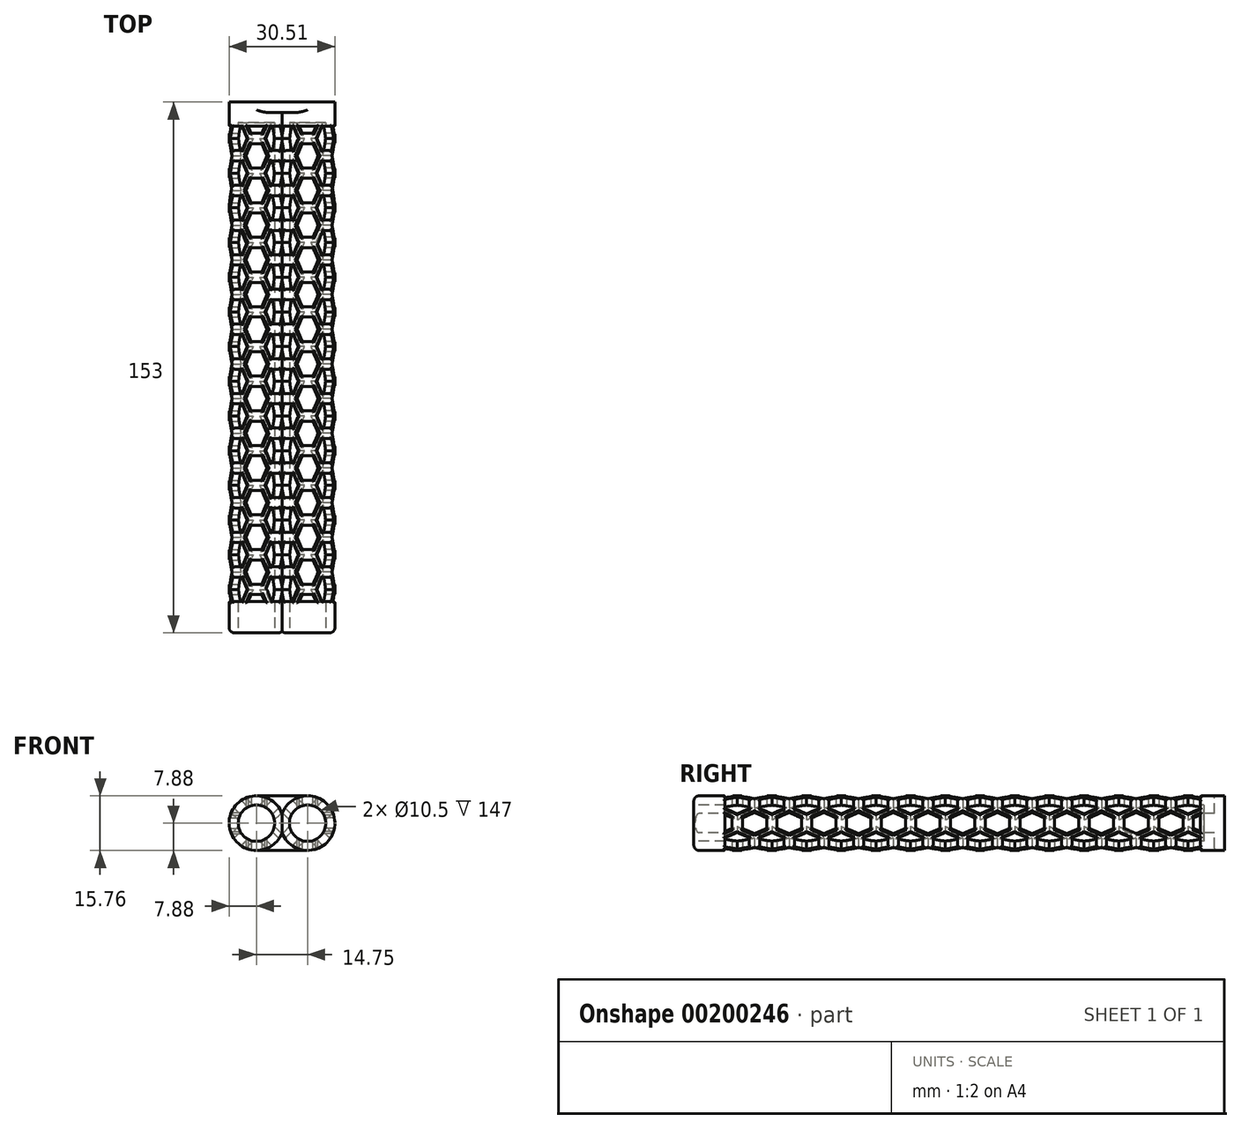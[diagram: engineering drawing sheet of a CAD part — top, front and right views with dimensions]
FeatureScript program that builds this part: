
annotation { "Feature Type Name" : "Feature", "Feature Type Description" : "" }
export const myFeature = defineFeature(function(context is Context, id is Id, definition is map)
    precondition{}
    {
        {
            var Q0;
            Q0=qCreatedBy(makeId("Front.planeOp"),FACE);
            var sketch = newSketch(context, id + "F0", { "sketchPlane" : qUnion([Q0])});
            skCircle(sketch, "E0", {"center": v(0, 0) * mm, "radius": 7.88 * mm});
            skSolve(sketch);
        }
        {
            var Q0;
            Q0=makeQuery(id+"F0.imprint","IMPRINT",FACE,{"disambiguationData":[TD([[makeQuery(id+"F0.imprint","IMPRINT",EDGE,{"derivedFrom":sQuery(id+"F0.wireOp",EDGE,"E0")}),1.0]])]});
            extrude(context, id + "F1", {"entities" : qUnion([Q0]), "oppositeDirection" : true, "depth" : 150 * mm});
        }
        {
            var Q0;
            Q0=makeQuery(id+"F1.opExtrude","CAP_FACE",FACE,{"disambiguationData":[OSD([sQuery(id+"F0.wireOp",EDGE,"E0")])],"isStart":true});
            var sketch = newSketch(context, id + "F2", { "sketchPlane" : qUnion([Q0])});
            skCircle(sketch, "E1", {"center": v(0, 0) * mm, "radius": 5.25 * mm});
            skSolve(sketch);
        }
        {
            var Q0;
            Q0=qSketchRegion(id+"F2",true);
            extrude(context, id + "F3", {"entities" : qUnion([Q0]), "operationType" : NewBodyOperationType.REMOVE, "oppositeDirection" : true, "depth" : 147 * mm});
        }
        {
            var Q0;
            Q0=qCreatedBy(makeId("Top.planeOp"),FACE);
            var sketch = newSketch(context, id + "F4", { "sketchPlane" : qUnion([Q0])});
            skLineSegment(sketch, "E2", {"start": v(0, 0) * mm, "end": v(0, 9) * mm, "construction": true});
            skLineSegment(sketch, "E3", {"start": v(0, 9) * mm, "end": v(-3, 9) * mm, "construction": true});
            skLineSegment(sketch, "E4", {"start": v(3, 9) * mm, "end": v(1.5, 9) * mm, "construction": true});
            skLineSegment(sketch, "E5", {"start": v(1.5, 9) * mm, "end": v(-1.5, 9) * mm, "construction": true});
            skLineSegment(sketch, "E6", {"start": v(-1.5, 9) * mm, "end": v(-3, 9) * mm, "construction": true});
            skLineSegment(sketch, "E7", {"start": v(-3, 9) * mm, "end": v(-3, 12.5) * mm, "construction": true});
            skLineSegment(sketch, "E8", {"start": v(-3, 12.5) * mm, "end": v(-3, 16) * mm, "construction": true});
            skLineSegment(sketch, "E9", {"start": v(-3, 16) * mm, "end": v(-1.5, 16) * mm, "construction": true});
            skLineSegment(sketch, "E10", {"start": v(-1.5, 16) * mm, "end": v(1.5, 16) * mm, "construction": true});
            skLineSegment(sketch, "E11", {"start": v(1.5, 16) * mm, "end": v(3, 16) * mm, "construction": true});
            skLineSegment(sketch, "E12", {"start": v(3, 16) * mm, "end": v(3, 12.5) * mm, "construction": true});
            skLineSegment(sketch, "E13", {"start": v(3, 12.5) * mm, "end": v(3, 9) * mm, "construction": true});
            skLineSegment(sketch, "E14", {"start": v(1.5, 16) * mm, "end": v(3, 12.5) * mm});
            skLineSegment(sketch, "E15", {"start": v(3, 12.5) * mm, "end": v(1.5, 9) * mm});
            skLineSegment(sketch, "E16", {"start": v(1.5, 9) * mm, "end": v(-1.5, 9) * mm});
            skLineSegment(sketch, "E17", {"start": v(-1.5, 9) * mm, "end": v(-3, 12.5) * mm});
            skLineSegment(sketch, "E18", {"start": v(-3, 12.5) * mm, "end": v(-1.5, 16) * mm});
            skLineSegment(sketch, "E19", {"start": v(-1.5, 16) * mm, "end": v(1.5, 16) * mm});
            skLineSegment(sketch, "E20", {"start": v(0, 9) * mm, "end": v(0, 19) * mm, "construction": true});
            skLineSegment(sketch, "E21", {"start": v(0, 19) * mm, "end": v(-3, 19) * mm, "construction": true});
            skLineSegment(sketch, "E22", {"start": v(3, 19) * mm, "end": v(1.5, 19) * mm, "construction": true});
            skLineSegment(sketch, "E23", {"start": v(1.5, 19) * mm, "end": v(-1.5, 19) * mm, "construction": true});
            skLineSegment(sketch, "E24", {"start": v(-1.5, 19) * mm, "end": v(-3, 19) * mm, "construction": true});
            skLineSegment(sketch, "E25", {"start": v(-3, 19) * mm, "end": v(-3, 22.5) * mm, "construction": true});
            skLineSegment(sketch, "E26", {"start": v(-3, 22.5) * mm, "end": v(-3, 26) * mm, "construction": true});
            skLineSegment(sketch, "E27", {"start": v(-3, 26) * mm, "end": v(-1.5, 26) * mm, "construction": true});
            skLineSegment(sketch, "E28", {"start": v(-1.5, 26) * mm, "end": v(1.5, 26) * mm, "construction": true});
            skLineSegment(sketch, "E29", {"start": v(1.5, 26) * mm, "end": v(3, 26) * mm, "construction": true});
            skLineSegment(sketch, "E30", {"start": v(3, 26) * mm, "end": v(3, 22.5) * mm, "construction": true});
            skLineSegment(sketch, "E31", {"start": v(3, 22.5) * mm, "end": v(3, 19) * mm, "construction": true});
            skLineSegment(sketch, "E32", {"start": v(1.5, 26) * mm, "end": v(3, 22.5) * mm});
            skLineSegment(sketch, "E33", {"start": v(3, 22.5) * mm, "end": v(1.5, 19) * mm});
            skLineSegment(sketch, "E34", {"start": v(1.5, 19) * mm, "end": v(-1.5, 19) * mm});
            skLineSegment(sketch, "E35", {"start": v(-1.5, 19) * mm, "end": v(-3, 22.5) * mm});
            skLineSegment(sketch, "E36", {"start": v(-3, 22.5) * mm, "end": v(-1.5, 26) * mm});
            skLineSegment(sketch, "E37", {"start": v(-1.5, 26) * mm, "end": v(1.5, 26) * mm});
            skLineSegment(sketch, "E38", {"start": v(0, 19) * mm, "end": v(0, 29) * mm, "construction": true});
            skLineSegment(sketch, "E39", {"start": v(0, 29) * mm, "end": v(-3, 29) * mm, "construction": true});
            skLineSegment(sketch, "E40", {"start": v(3, 29) * mm, "end": v(1.5, 29) * mm, "construction": true});
            skLineSegment(sketch, "E41", {"start": v(1.5, 29) * mm, "end": v(-1.5, 29) * mm, "construction": true});
            skLineSegment(sketch, "E42", {"start": v(-1.5, 29) * mm, "end": v(-3, 29) * mm, "construction": true});
            skLineSegment(sketch, "E43", {"start": v(-3, 29) * mm, "end": v(-3, 32.5) * mm, "construction": true});
            skLineSegment(sketch, "E44", {"start": v(-3, 32.5) * mm, "end": v(-3, 36) * mm, "construction": true});
            skLineSegment(sketch, "E45", {"start": v(-3, 36) * mm, "end": v(-1.5, 36) * mm, "construction": true});
            skLineSegment(sketch, "E46", {"start": v(-1.5, 36) * mm, "end": v(1.5, 36) * mm, "construction": true});
            skLineSegment(sketch, "E47", {"start": v(1.5, 36) * mm, "end": v(3, 36) * mm, "construction": true});
            skLineSegment(sketch, "E48", {"start": v(3, 36) * mm, "end": v(3, 32.5) * mm, "construction": true});
            skLineSegment(sketch, "E49", {"start": v(3, 32.5) * mm, "end": v(3, 29) * mm, "construction": true});
            skLineSegment(sketch, "E50", {"start": v(1.5, 36) * mm, "end": v(3, 32.5) * mm});
            skLineSegment(sketch, "E51", {"start": v(3, 32.5) * mm, "end": v(1.5, 29) * mm});
            skLineSegment(sketch, "E52", {"start": v(1.5, 29) * mm, "end": v(-1.5, 29) * mm});
            skLineSegment(sketch, "E53", {"start": v(-1.5, 29) * mm, "end": v(-3, 32.5) * mm});
            skLineSegment(sketch, "E54", {"start": v(-3, 32.5) * mm, "end": v(-1.5, 36) * mm});
            skLineSegment(sketch, "E55", {"start": v(-1.5, 36) * mm, "end": v(1.5, 36) * mm});
            skLineSegment(sketch, "E56", {"start": v(0, 29) * mm, "end": v(0, 39) * mm, "construction": true});
            skLineSegment(sketch, "E57", {"start": v(0, 39) * mm, "end": v(-3, 39) * mm, "construction": true});
            skLineSegment(sketch, "E58", {"start": v(3, 39) * mm, "end": v(1.5, 39) * mm, "construction": true});
            skLineSegment(sketch, "E59", {"start": v(1.5, 39) * mm, "end": v(-1.5, 39) * mm, "construction": true});
            skLineSegment(sketch, "E60", {"start": v(-1.5, 39) * mm, "end": v(-3, 39) * mm, "construction": true});
            skLineSegment(sketch, "E61", {"start": v(-3, 39) * mm, "end": v(-3, 42.5) * mm, "construction": true});
            skLineSegment(sketch, "E62", {"start": v(-3, 42.5) * mm, "end": v(-3, 46) * mm, "construction": true});
            skLineSegment(sketch, "E63", {"start": v(-3, 46) * mm, "end": v(-1.5, 46) * mm, "construction": true});
            skLineSegment(sketch, "E64", {"start": v(-1.5, 46) * mm, "end": v(1.5, 46) * mm, "construction": true});
            skLineSegment(sketch, "E65", {"start": v(1.5, 46) * mm, "end": v(3, 46) * mm, "construction": true});
            skLineSegment(sketch, "E66", {"start": v(3, 46) * mm, "end": v(3, 42.5) * mm, "construction": true});
            skLineSegment(sketch, "E67", {"start": v(3, 42.5) * mm, "end": v(3, 39) * mm, "construction": true});
            skLineSegment(sketch, "E68", {"start": v(1.5, 46) * mm, "end": v(3, 42.5) * mm});
            skLineSegment(sketch, "E69", {"start": v(3, 42.5) * mm, "end": v(1.5, 39) * mm});
            skLineSegment(sketch, "E70", {"start": v(1.5, 39) * mm, "end": v(-1.5, 39) * mm});
            skLineSegment(sketch, "E71", {"start": v(-1.5, 39) * mm, "end": v(-3, 42.5) * mm});
            skLineSegment(sketch, "E72", {"start": v(-3, 42.5) * mm, "end": v(-1.5, 46) * mm});
            skLineSegment(sketch, "E73", {"start": v(-1.5, 46) * mm, "end": v(1.5, 46) * mm});
            skLineSegment(sketch, "E74", {"start": v(0, 39) * mm, "end": v(0, 49) * mm, "construction": true});
            skLineSegment(sketch, "E75", {"start": v(0, 49) * mm, "end": v(-3, 49) * mm, "construction": true});
            skLineSegment(sketch, "E76", {"start": v(3, 49) * mm, "end": v(1.5, 49) * mm, "construction": true});
            skLineSegment(sketch, "E77", {"start": v(1.5, 49) * mm, "end": v(-1.5, 49) * mm, "construction": true});
            skLineSegment(sketch, "E78", {"start": v(-1.5, 49) * mm, "end": v(-3, 49) * mm, "construction": true});
            skLineSegment(sketch, "E79", {"start": v(-3, 49) * mm, "end": v(-3, 52.5) * mm, "construction": true});
            skLineSegment(sketch, "E80", {"start": v(-3, 52.5) * mm, "end": v(-3, 56) * mm, "construction": true});
            skLineSegment(sketch, "E81", {"start": v(-3, 56) * mm, "end": v(-1.5, 56) * mm, "construction": true});
            skLineSegment(sketch, "E82", {"start": v(-1.5, 56) * mm, "end": v(1.5, 56) * mm, "construction": true});
            skLineSegment(sketch, "E83", {"start": v(1.5, 56) * mm, "end": v(3, 56) * mm, "construction": true});
            skLineSegment(sketch, "E84", {"start": v(3, 56) * mm, "end": v(3, 52.5) * mm, "construction": true});
            skLineSegment(sketch, "E85", {"start": v(3, 52.5) * mm, "end": v(3, 49) * mm, "construction": true});
            skLineSegment(sketch, "E86", {"start": v(1.5, 56) * mm, "end": v(3, 52.5) * mm});
            skLineSegment(sketch, "E87", {"start": v(3, 52.5) * mm, "end": v(1.5, 49) * mm});
            skLineSegment(sketch, "E88", {"start": v(1.5, 49) * mm, "end": v(-1.5, 49) * mm});
            skLineSegment(sketch, "E89", {"start": v(-1.5, 49) * mm, "end": v(-3, 52.5) * mm});
            skLineSegment(sketch, "E90", {"start": v(-3, 52.5) * mm, "end": v(-1.5, 56) * mm});
            skLineSegment(sketch, "E91", {"start": v(-1.5, 56) * mm, "end": v(1.5, 56) * mm});
            skLineSegment(sketch, "E92", {"start": v(0, 49) * mm, "end": v(0, 59) * mm, "construction": true});
            skLineSegment(sketch, "E93", {"start": v(0, 59) * mm, "end": v(-3, 59) * mm, "construction": true});
            skLineSegment(sketch, "E94", {"start": v(3, 59) * mm, "end": v(1.5, 59) * mm, "construction": true});
            skLineSegment(sketch, "E95", {"start": v(1.5, 59) * mm, "end": v(-1.5, 59) * mm, "construction": true});
            skLineSegment(sketch, "E96", {"start": v(-1.5, 59) * mm, "end": v(-3, 59) * mm, "construction": true});
            skLineSegment(sketch, "E97", {"start": v(-3, 59) * mm, "end": v(-3, 62.5) * mm, "construction": true});
            skLineSegment(sketch, "E98", {"start": v(-3, 62.5) * mm, "end": v(-3, 66) * mm, "construction": true});
            skLineSegment(sketch, "E99", {"start": v(-3, 66) * mm, "end": v(-1.5, 66) * mm, "construction": true});
            skLineSegment(sketch, "E100", {"start": v(-1.5, 66) * mm, "end": v(1.5, 66) * mm, "construction": true});
            skLineSegment(sketch, "E101", {"start": v(1.5, 66) * mm, "end": v(3, 66) * mm, "construction": true});
            skLineSegment(sketch, "E102", {"start": v(3, 66) * mm, "end": v(3, 62.5) * mm, "construction": true});
            skLineSegment(sketch, "E103", {"start": v(3, 62.5) * mm, "end": v(3, 59) * mm, "construction": true});
            skLineSegment(sketch, "E104", {"start": v(1.5, 66) * mm, "end": v(3, 62.5) * mm});
            skLineSegment(sketch, "E105", {"start": v(3, 62.5) * mm, "end": v(1.5, 59) * mm});
            skLineSegment(sketch, "E106", {"start": v(1.5, 59) * mm, "end": v(-1.5, 59) * mm});
            skLineSegment(sketch, "E107", {"start": v(-1.5, 59) * mm, "end": v(-3, 62.5) * mm});
            skLineSegment(sketch, "E108", {"start": v(-3, 62.5) * mm, "end": v(-1.5, 66) * mm});
            skLineSegment(sketch, "E109", {"start": v(-1.5, 66) * mm, "end": v(1.5, 66) * mm});
            skLineSegment(sketch, "E110", {"start": v(0, 59) * mm, "end": v(0, 69) * mm, "construction": true});
            skLineSegment(sketch, "E111", {"start": v(0, 69) * mm, "end": v(-3, 69) * mm, "construction": true});
            skLineSegment(sketch, "E112", {"start": v(3, 69) * mm, "end": v(1.5, 69) * mm, "construction": true});
            skLineSegment(sketch, "E113", {"start": v(1.5, 69) * mm, "end": v(-1.5, 69) * mm, "construction": true});
            skLineSegment(sketch, "E114", {"start": v(-1.5, 69) * mm, "end": v(-3, 69) * mm, "construction": true});
            skLineSegment(sketch, "E115", {"start": v(-3, 69) * mm, "end": v(-3, 72.5) * mm, "construction": true});
            skLineSegment(sketch, "E116", {"start": v(-3, 72.5) * mm, "end": v(-3, 76) * mm, "construction": true});
            skLineSegment(sketch, "E117", {"start": v(-3, 76) * mm, "end": v(-1.5, 76) * mm, "construction": true});
            skLineSegment(sketch, "E118", {"start": v(-1.5, 76) * mm, "end": v(1.5, 76) * mm, "construction": true});
            skLineSegment(sketch, "E119", {"start": v(1.5, 76) * mm, "end": v(3, 76) * mm, "construction": true});
            skLineSegment(sketch, "E120", {"start": v(3, 76) * mm, "end": v(3, 72.5) * mm, "construction": true});
            skLineSegment(sketch, "E121", {"start": v(3, 72.5) * mm, "end": v(3, 69) * mm, "construction": true});
            skLineSegment(sketch, "E122", {"start": v(1.5, 76) * mm, "end": v(3, 72.5) * mm});
            skLineSegment(sketch, "E123", {"start": v(3, 72.5) * mm, "end": v(1.5, 69) * mm});
            skLineSegment(sketch, "E124", {"start": v(1.5, 69) * mm, "end": v(-1.5, 69) * mm});
            skLineSegment(sketch, "E125", {"start": v(-1.5, 69) * mm, "end": v(-3, 72.5) * mm});
            skLineSegment(sketch, "E126", {"start": v(-3, 72.5) * mm, "end": v(-1.5, 76) * mm});
            skLineSegment(sketch, "E127", {"start": v(-1.5, 76) * mm, "end": v(1.5, 76) * mm});
            skLineSegment(sketch, "E128", {"start": v(0, 69) * mm, "end": v(0, 79) * mm, "construction": true});
            skLineSegment(sketch, "E129", {"start": v(0, 79) * mm, "end": v(-3, 79) * mm, "construction": true});
            skLineSegment(sketch, "E130", {"start": v(3, 79) * mm, "end": v(1.5, 79) * mm, "construction": true});
            skLineSegment(sketch, "E131", {"start": v(1.5, 79) * mm, "end": v(-1.5, 79) * mm, "construction": true});
            skLineSegment(sketch, "E132", {"start": v(-1.5, 79) * mm, "end": v(-3, 79) * mm, "construction": true});
            skLineSegment(sketch, "E133", {"start": v(-3, 79) * mm, "end": v(-3, 82.5) * mm, "construction": true});
            skLineSegment(sketch, "E134", {"start": v(-3, 82.5) * mm, "end": v(-3, 86) * mm, "construction": true});
            skLineSegment(sketch, "E135", {"start": v(-3, 86) * mm, "end": v(-1.5, 86) * mm, "construction": true});
            skLineSegment(sketch, "E136", {"start": v(-1.5, 86) * mm, "end": v(1.5, 86) * mm, "construction": true});
            skLineSegment(sketch, "E137", {"start": v(1.5, 86) * mm, "end": v(3, 86) * mm, "construction": true});
            skLineSegment(sketch, "E138", {"start": v(3, 86) * mm, "end": v(3, 82.5) * mm, "construction": true});
            skLineSegment(sketch, "E139", {"start": v(3, 82.5) * mm, "end": v(3, 79) * mm, "construction": true});
            skLineSegment(sketch, "E140", {"start": v(1.5, 86) * mm, "end": v(3, 82.5) * mm});
            skLineSegment(sketch, "E141", {"start": v(3, 82.5) * mm, "end": v(1.5, 79) * mm});
            skLineSegment(sketch, "E142", {"start": v(1.5, 79) * mm, "end": v(-1.5, 79) * mm});
            skLineSegment(sketch, "E143", {"start": v(-1.5, 79) * mm, "end": v(-3, 82.5) * mm});
            skLineSegment(sketch, "E144", {"start": v(-3, 82.5) * mm, "end": v(-1.5, 86) * mm});
            skLineSegment(sketch, "E145", {"start": v(-1.5, 86) * mm, "end": v(1.5, 86) * mm});
            skLineSegment(sketch, "E146", {"start": v(0, 79) * mm, "end": v(0, 89) * mm, "construction": true});
            skLineSegment(sketch, "E147", {"start": v(0, 89) * mm, "end": v(-3, 89) * mm, "construction": true});
            skLineSegment(sketch, "E148", {"start": v(3, 89) * mm, "end": v(1.5, 89) * mm, "construction": true});
            skLineSegment(sketch, "E149", {"start": v(1.5, 89) * mm, "end": v(-1.5, 89) * mm, "construction": true});
            skLineSegment(sketch, "E150", {"start": v(-1.5, 89) * mm, "end": v(-3, 89) * mm, "construction": true});
            skLineSegment(sketch, "E151", {"start": v(-3, 89) * mm, "end": v(-3, 92.5) * mm, "construction": true});
            skLineSegment(sketch, "E152", {"start": v(-3, 92.5) * mm, "end": v(-3, 96) * mm, "construction": true});
            skLineSegment(sketch, "E153", {"start": v(-3, 96) * mm, "end": v(-1.5, 96) * mm, "construction": true});
            skLineSegment(sketch, "E154", {"start": v(-1.5, 96) * mm, "end": v(1.5, 96) * mm, "construction": true});
            skLineSegment(sketch, "E155", {"start": v(1.5, 96) * mm, "end": v(3, 96) * mm, "construction": true});
            skLineSegment(sketch, "E156", {"start": v(3, 96) * mm, "end": v(3, 92.5) * mm, "construction": true});
            skLineSegment(sketch, "E157", {"start": v(3, 92.5) * mm, "end": v(3, 89) * mm, "construction": true});
            skLineSegment(sketch, "E158", {"start": v(1.5, 96) * mm, "end": v(3, 92.5) * mm});
            skLineSegment(sketch, "E159", {"start": v(3, 92.5) * mm, "end": v(1.5, 89) * mm});
            skLineSegment(sketch, "E160", {"start": v(1.5, 89) * mm, "end": v(-1.5, 89) * mm});
            skLineSegment(sketch, "E161", {"start": v(-1.5, 89) * mm, "end": v(-3, 92.5) * mm});
            skLineSegment(sketch, "E162", {"start": v(-3, 92.5) * mm, "end": v(-1.5, 96) * mm});
            skLineSegment(sketch, "E163", {"start": v(-1.5, 96) * mm, "end": v(1.5, 96) * mm});
            skLineSegment(sketch, "E164", {"start": v(0, 89) * mm, "end": v(0, 99) * mm, "construction": true});
            skLineSegment(sketch, "E165", {"start": v(0, 99) * mm, "end": v(-3, 99) * mm, "construction": true});
            skLineSegment(sketch, "E166", {"start": v(3, 99) * mm, "end": v(1.5, 99) * mm, "construction": true});
            skLineSegment(sketch, "E167", {"start": v(1.5, 99) * mm, "end": v(-1.5, 99) * mm, "construction": true});
            skLineSegment(sketch, "E168", {"start": v(-1.5, 99) * mm, "end": v(-3, 99) * mm, "construction": true});
            skLineSegment(sketch, "E169", {"start": v(-3, 99) * mm, "end": v(-3, 102.5) * mm, "construction": true});
            skLineSegment(sketch, "E170", {"start": v(-3, 102.5) * mm, "end": v(-3, 106) * mm, "construction": true});
            skLineSegment(sketch, "E171", {"start": v(-3, 106) * mm, "end": v(-1.5, 106) * mm, "construction": true});
            skLineSegment(sketch, "E172", {"start": v(-1.5, 106) * mm, "end": v(1.5, 106) * mm, "construction": true});
            skLineSegment(sketch, "E173", {"start": v(1.5, 106) * mm, "end": v(3, 106) * mm, "construction": true});
            skLineSegment(sketch, "E174", {"start": v(3, 106) * mm, "end": v(3, 102.5) * mm, "construction": true});
            skLineSegment(sketch, "E175", {"start": v(3, 102.5) * mm, "end": v(3, 99) * mm, "construction": true});
            skLineSegment(sketch, "E176", {"start": v(1.5, 106) * mm, "end": v(3, 102.5) * mm});
            skLineSegment(sketch, "E177", {"start": v(3, 102.5) * mm, "end": v(1.5, 99) * mm});
            skLineSegment(sketch, "E178", {"start": v(1.5, 99) * mm, "end": v(-1.5, 99) * mm});
            skLineSegment(sketch, "E179", {"start": v(-1.5, 99) * mm, "end": v(-3, 102.5) * mm});
            skLineSegment(sketch, "E180", {"start": v(-3, 102.5) * mm, "end": v(-1.5, 106) * mm});
            skLineSegment(sketch, "E181", {"start": v(-1.5, 106) * mm, "end": v(1.5, 106) * mm});
            skLineSegment(sketch, "E182", {"start": v(0, 99) * mm, "end": v(0, 109) * mm, "construction": true});
            skLineSegment(sketch, "E183", {"start": v(0, 109) * mm, "end": v(-3, 109) * mm, "construction": true});
            skLineSegment(sketch, "E184", {"start": v(3, 109) * mm, "end": v(1.5, 109) * mm, "construction": true});
            skLineSegment(sketch, "E185", {"start": v(1.5, 109) * mm, "end": v(-1.5, 109) * mm, "construction": true});
            skLineSegment(sketch, "E186", {"start": v(-1.5, 109) * mm, "end": v(-3, 109) * mm, "construction": true});
            skLineSegment(sketch, "E187", {"start": v(-3, 109) * mm, "end": v(-3, 112.5) * mm, "construction": true});
            skLineSegment(sketch, "E188", {"start": v(-3, 112.5) * mm, "end": v(-3, 116) * mm, "construction": true});
            skLineSegment(sketch, "E189", {"start": v(-3, 116) * mm, "end": v(-1.5, 116) * mm, "construction": true});
            skLineSegment(sketch, "E190", {"start": v(-1.5, 116) * mm, "end": v(1.5, 116) * mm, "construction": true});
            skLineSegment(sketch, "E191", {"start": v(1.5, 116) * mm, "end": v(3, 116) * mm, "construction": true});
            skLineSegment(sketch, "E192", {"start": v(3, 116) * mm, "end": v(3, 112.5) * mm, "construction": true});
            skLineSegment(sketch, "E193", {"start": v(3, 112.5) * mm, "end": v(3, 109) * mm, "construction": true});
            skLineSegment(sketch, "E194", {"start": v(1.5, 116) * mm, "end": v(3, 112.5) * mm});
            skLineSegment(sketch, "E195", {"start": v(3, 112.5) * mm, "end": v(1.5, 109) * mm});
            skLineSegment(sketch, "E196", {"start": v(1.5, 109) * mm, "end": v(-1.5, 109) * mm});
            skLineSegment(sketch, "E197", {"start": v(-1.5, 109) * mm, "end": v(-3, 112.5) * mm});
            skLineSegment(sketch, "E198", {"start": v(-3, 112.5) * mm, "end": v(-1.5, 116) * mm});
            skLineSegment(sketch, "E199", {"start": v(-1.5, 116) * mm, "end": v(1.5, 116) * mm});
            skLineSegment(sketch, "E200", {"start": v(0, 109) * mm, "end": v(0, 119) * mm, "construction": true});
            skLineSegment(sketch, "E201", {"start": v(0, 119) * mm, "end": v(-3, 119) * mm, "construction": true});
            skLineSegment(sketch, "E202", {"start": v(3, 119) * mm, "end": v(1.5, 119) * mm, "construction": true});
            skLineSegment(sketch, "E203", {"start": v(1.5, 119) * mm, "end": v(-1.5, 119) * mm, "construction": true});
            skLineSegment(sketch, "E204", {"start": v(-1.5, 119) * mm, "end": v(-3, 119) * mm, "construction": true});
            skLineSegment(sketch, "E205", {"start": v(-3, 119) * mm, "end": v(-3, 122.5) * mm, "construction": true});
            skLineSegment(sketch, "E206", {"start": v(-3, 122.5) * mm, "end": v(-3, 126) * mm, "construction": true});
            skLineSegment(sketch, "E207", {"start": v(-3, 126) * mm, "end": v(-1.5, 126) * mm, "construction": true});
            skLineSegment(sketch, "E208", {"start": v(-1.5, 126) * mm, "end": v(1.5, 126) * mm, "construction": true});
            skLineSegment(sketch, "E209", {"start": v(1.5, 126) * mm, "end": v(3, 126) * mm, "construction": true});
            skLineSegment(sketch, "E210", {"start": v(3, 126) * mm, "end": v(3, 122.5) * mm, "construction": true});
            skLineSegment(sketch, "E211", {"start": v(3, 122.5) * mm, "end": v(3, 119) * mm, "construction": true});
            skLineSegment(sketch, "E212", {"start": v(1.5, 126) * mm, "end": v(3, 122.5) * mm});
            skLineSegment(sketch, "E213", {"start": v(3, 122.5) * mm, "end": v(1.5, 119) * mm});
            skLineSegment(sketch, "E214", {"start": v(1.5, 119) * mm, "end": v(-1.5, 119) * mm});
            skLineSegment(sketch, "E215", {"start": v(-1.5, 119) * mm, "end": v(-3, 122.5) * mm});
            skLineSegment(sketch, "E216", {"start": v(-3, 122.5) * mm, "end": v(-1.5, 126) * mm});
            skLineSegment(sketch, "E217", {"start": v(-1.5, 126) * mm, "end": v(1.5, 126) * mm});
            skLineSegment(sketch, "E218", {"start": v(0, 119) * mm, "end": v(0, 129) * mm, "construction": true});
            skLineSegment(sketch, "E219", {"start": v(0, 129) * mm, "end": v(-3, 129) * mm, "construction": true});
            skLineSegment(sketch, "E220", {"start": v(3, 129) * mm, "end": v(1.5, 129) * mm, "construction": true});
            skLineSegment(sketch, "E221", {"start": v(1.5, 129) * mm, "end": v(-1.5, 129) * mm, "construction": true});
            skLineSegment(sketch, "E222", {"start": v(-1.5, 129) * mm, "end": v(-3, 129) * mm, "construction": true});
            skLineSegment(sketch, "E223", {"start": v(-3, 129) * mm, "end": v(-3, 132.5) * mm, "construction": true});
            skLineSegment(sketch, "E224", {"start": v(-3, 132.5) * mm, "end": v(-3, 136) * mm, "construction": true});
            skLineSegment(sketch, "E225", {"start": v(-3, 136) * mm, "end": v(-1.5, 136) * mm, "construction": true});
            skLineSegment(sketch, "E226", {"start": v(-1.5, 136) * mm, "end": v(1.5, 136) * mm, "construction": true});
            skLineSegment(sketch, "E227", {"start": v(1.5, 136) * mm, "end": v(3, 136) * mm, "construction": true});
            skLineSegment(sketch, "E228", {"start": v(3, 136) * mm, "end": v(3, 132.5) * mm, "construction": true});
            skLineSegment(sketch, "E229", {"start": v(3, 132.5) * mm, "end": v(3, 129) * mm, "construction": true});
            skLineSegment(sketch, "E230", {"start": v(1.5, 136) * mm, "end": v(3, 132.5) * mm});
            skLineSegment(sketch, "E231", {"start": v(3, 132.5) * mm, "end": v(1.5, 129) * mm});
            skLineSegment(sketch, "E232", {"start": v(1.5, 129) * mm, "end": v(-1.5, 129) * mm});
            skLineSegment(sketch, "E233", {"start": v(-1.5, 129) * mm, "end": v(-3, 132.5) * mm});
            skLineSegment(sketch, "E234", {"start": v(-3, 132.5) * mm, "end": v(-1.5, 136) * mm});
            skLineSegment(sketch, "E235", {"start": v(-1.5, 136) * mm, "end": v(1.5, 136) * mm});
            skLineSegment(sketch, "E236", {"start": v(0, 129) * mm, "end": v(0, 139) * mm, "construction": true});
            skLineSegment(sketch, "E237", {"start": v(0, 139) * mm, "end": v(-3, 139) * mm, "construction": true});
            skLineSegment(sketch, "E238", {"start": v(3, 139) * mm, "end": v(1.5, 139) * mm, "construction": true});
            skLineSegment(sketch, "E239", {"start": v(1.5, 139) * mm, "end": v(-1.5, 139) * mm, "construction": true});
            skLineSegment(sketch, "E240", {"start": v(-1.5, 139) * mm, "end": v(-3, 139) * mm, "construction": true});
            skLineSegment(sketch, "E241", {"start": v(-3, 139) * mm, "end": v(-3, 142.5) * mm, "construction": true});
            skLineSegment(sketch, "E242", {"start": v(-3, 142.5) * mm, "end": v(-3, 146) * mm, "construction": true});
            skLineSegment(sketch, "E243", {"start": v(-3, 146) * mm, "end": v(-1.5, 146) * mm, "construction": true});
            skLineSegment(sketch, "E244", {"start": v(-1.5, 146) * mm, "end": v(1.5, 146) * mm, "construction": true});
            skLineSegment(sketch, "E245", {"start": v(1.5, 146) * mm, "end": v(3, 146) * mm, "construction": true});
            skLineSegment(sketch, "E246", {"start": v(3, 146) * mm, "end": v(3, 142.5) * mm, "construction": true});
            skLineSegment(sketch, "E247", {"start": v(3, 142.5) * mm, "end": v(3, 139) * mm, "construction": true});
            skLineSegment(sketch, "E248", {"start": v(1.5, 146) * mm, "end": v(3, 142.5) * mm});
            skLineSegment(sketch, "E249", {"start": v(3, 142.5) * mm, "end": v(1.5, 139) * mm});
            skLineSegment(sketch, "E250", {"start": v(1.5, 139) * mm, "end": v(-1.5, 139) * mm});
            skLineSegment(sketch, "E251", {"start": v(-1.5, 139) * mm, "end": v(-3, 142.5) * mm});
            skLineSegment(sketch, "E252", {"start": v(-3, 142.5) * mm, "end": v(-1.5, 146) * mm});
            skLineSegment(sketch, "E253", {"start": v(-1.5, 146) * mm, "end": v(1.5, 146) * mm});
            skSolve(sketch);
        }
        {
            var Q0;
            Q0=qSketchRegion(id+"F4",true);
            extrude(context, id + "F5", {"entities" : qUnion([Q0]), "operationType" : NewBodyOperationType.REMOVE, "endBound" : BoundingType.SYMMETRIC, "depth" : 25 * mm});
        }
        {
            var Q0;
            Q0=qCreatedBy(makeId("Right.planeOp"),FACE);
            var sketch = newSketch(context, id + "F6", { "sketchPlane" : qUnion([Q0])});
            skLineSegment(sketch, "E254", {"start": v(0, 0) * mm, "end": v(9, 0) * mm, "construction": true});
            skLineSegment(sketch, "E255", {"start": v(9, 0) * mm, "end": v(9, 3) * mm, "construction": true});
            skLineSegment(sketch, "E256", {"start": v(9, -3) * mm, "end": v(9, -1.5) * mm, "construction": true});
            skLineSegment(sketch, "E257", {"start": v(9, -1.5) * mm, "end": v(9, 1.5) * mm, "construction": true});
            skLineSegment(sketch, "E258", {"start": v(9, 1.5) * mm, "end": v(9, 3) * mm, "construction": true});
            skLineSegment(sketch, "E259", {"start": v(9, 3) * mm, "end": v(12.5, 3) * mm, "construction": true});
            skLineSegment(sketch, "E260", {"start": v(12.5, 3) * mm, "end": v(16, 3) * mm, "construction": true});
            skLineSegment(sketch, "E261", {"start": v(16, 3) * mm, "end": v(16, 1.5) * mm, "construction": true});
            skLineSegment(sketch, "E262", {"start": v(16, 1.5) * mm, "end": v(16, -1.5) * mm, "construction": true});
            skLineSegment(sketch, "E263", {"start": v(16, -1.5) * mm, "end": v(16, -3) * mm, "construction": true});
            skLineSegment(sketch, "E264", {"start": v(16, -3) * mm, "end": v(12.5, -3) * mm, "construction": true});
            skLineSegment(sketch, "E265", {"start": v(12.5, -3) * mm, "end": v(9, -3) * mm, "construction": true});
            skLineSegment(sketch, "E266", {"start": v(16, -1.5) * mm, "end": v(12.5, -3) * mm});
            skLineSegment(sketch, "E267", {"start": v(12.5, -3) * mm, "end": v(9, -1.5) * mm});
            skLineSegment(sketch, "E268", {"start": v(9, -1.5) * mm, "end": v(9, 1.5) * mm});
            skLineSegment(sketch, "E269", {"start": v(9, 1.5) * mm, "end": v(12.5, 3) * mm});
            skLineSegment(sketch, "E270", {"start": v(12.5, 3) * mm, "end": v(16, 1.5) * mm});
            skLineSegment(sketch, "E271", {"start": v(16, 1.5) * mm, "end": v(16, -1.5) * mm});
            skLineSegment(sketch, "E272", {"start": v(9, 0) * mm, "end": v(19, 0) * mm, "construction": true});
            skLineSegment(sketch, "E273", {"start": v(19, 0) * mm, "end": v(19, 3) * mm, "construction": true});
            skLineSegment(sketch, "E274", {"start": v(19, -3) * mm, "end": v(19, -1.5) * mm, "construction": true});
            skLineSegment(sketch, "E275", {"start": v(19, -1.5) * mm, "end": v(19, 1.5) * mm, "construction": true});
            skLineSegment(sketch, "E276", {"start": v(19, 1.5) * mm, "end": v(19, 3) * mm, "construction": true});
            skLineSegment(sketch, "E277", {"start": v(19, 3) * mm, "end": v(22.5, 3) * mm, "construction": true});
            skLineSegment(sketch, "E278", {"start": v(22.5, 3) * mm, "end": v(26, 3) * mm, "construction": true});
            skLineSegment(sketch, "E279", {"start": v(26, 3) * mm, "end": v(26, 1.5) * mm, "construction": true});
            skLineSegment(sketch, "E280", {"start": v(26, 1.5) * mm, "end": v(26, -1.5) * mm, "construction": true});
            skLineSegment(sketch, "E281", {"start": v(26, -1.5) * mm, "end": v(26, -3) * mm, "construction": true});
            skLineSegment(sketch, "E282", {"start": v(26, -3) * mm, "end": v(22.5, -3) * mm, "construction": true});
            skLineSegment(sketch, "E283", {"start": v(22.5, -3) * mm, "end": v(19, -3) * mm, "construction": true});
            skLineSegment(sketch, "E284", {"start": v(26, -1.5) * mm, "end": v(22.5, -3) * mm});
            skLineSegment(sketch, "E285", {"start": v(22.5, -3) * mm, "end": v(19, -1.5) * mm});
            skLineSegment(sketch, "E286", {"start": v(19, -1.5) * mm, "end": v(19, 1.5) * mm});
            skLineSegment(sketch, "E287", {"start": v(19, 1.5) * mm, "end": v(22.5, 3) * mm});
            skLineSegment(sketch, "E288", {"start": v(22.5, 3) * mm, "end": v(26, 1.5) * mm});
            skLineSegment(sketch, "E289", {"start": v(26, 1.5) * mm, "end": v(26, -1.5) * mm});
            skLineSegment(sketch, "E290", {"start": v(19, 0) * mm, "end": v(29, 0) * mm, "construction": true});
            skLineSegment(sketch, "E291", {"start": v(29, 0) * mm, "end": v(29, 3) * mm, "construction": true});
            skLineSegment(sketch, "E292", {"start": v(29, -3) * mm, "end": v(29, -1.5) * mm, "construction": true});
            skLineSegment(sketch, "E293", {"start": v(29, -1.5) * mm, "end": v(29, 1.5) * mm, "construction": true});
            skLineSegment(sketch, "E294", {"start": v(29, 1.5) * mm, "end": v(29, 3) * mm, "construction": true});
            skLineSegment(sketch, "E295", {"start": v(29, 3) * mm, "end": v(32.5, 3) * mm, "construction": true});
            skLineSegment(sketch, "E296", {"start": v(32.5, 3) * mm, "end": v(36, 3) * mm, "construction": true});
            skLineSegment(sketch, "E297", {"start": v(36, 3) * mm, "end": v(36, 1.5) * mm, "construction": true});
            skLineSegment(sketch, "E298", {"start": v(36, 1.5) * mm, "end": v(36, -1.5) * mm, "construction": true});
            skLineSegment(sketch, "E299", {"start": v(36, -1.5) * mm, "end": v(36, -3) * mm, "construction": true});
            skLineSegment(sketch, "E300", {"start": v(36, -3) * mm, "end": v(32.5, -3) * mm, "construction": true});
            skLineSegment(sketch, "E301", {"start": v(32.5, -3) * mm, "end": v(29, -3) * mm, "construction": true});
            skLineSegment(sketch, "E302", {"start": v(36, -1.5) * mm, "end": v(32.5, -3) * mm});
            skLineSegment(sketch, "E303", {"start": v(32.5, -3) * mm, "end": v(29, -1.5) * mm});
            skLineSegment(sketch, "E304", {"start": v(29, -1.5) * mm, "end": v(29, 1.5) * mm});
            skLineSegment(sketch, "E305", {"start": v(29, 1.5) * mm, "end": v(32.5, 3) * mm});
            skLineSegment(sketch, "E306", {"start": v(32.5, 3) * mm, "end": v(36, 1.5) * mm});
            skLineSegment(sketch, "E307", {"start": v(36, 1.5) * mm, "end": v(36, -1.5) * mm});
            skLineSegment(sketch, "E308", {"start": v(29, 0) * mm, "end": v(39, 0) * mm, "construction": true});
            skLineSegment(sketch, "E309", {"start": v(39, 0) * mm, "end": v(39, 3) * mm, "construction": true});
            skLineSegment(sketch, "E310", {"start": v(39, -3) * mm, "end": v(39, -1.5) * mm, "construction": true});
            skLineSegment(sketch, "E311", {"start": v(39, -1.5) * mm, "end": v(39, 1.5) * mm, "construction": true});
            skLineSegment(sketch, "E312", {"start": v(39, 1.5) * mm, "end": v(39, 3) * mm, "construction": true});
            skLineSegment(sketch, "E313", {"start": v(39, 3) * mm, "end": v(42.5, 3) * mm, "construction": true});
            skLineSegment(sketch, "E314", {"start": v(42.5, 3) * mm, "end": v(46, 3) * mm, "construction": true});
            skLineSegment(sketch, "E315", {"start": v(46, 3) * mm, "end": v(46, 1.5) * mm, "construction": true});
            skLineSegment(sketch, "E316", {"start": v(46, 1.5) * mm, "end": v(46, -1.5) * mm, "construction": true});
            skLineSegment(sketch, "E317", {"start": v(46, -1.5) * mm, "end": v(46, -3) * mm, "construction": true});
            skLineSegment(sketch, "E318", {"start": v(46, -3) * mm, "end": v(42.5, -3) * mm, "construction": true});
            skLineSegment(sketch, "E319", {"start": v(42.5, -3) * mm, "end": v(39, -3) * mm, "construction": true});
            skLineSegment(sketch, "E320", {"start": v(46, -1.5) * mm, "end": v(42.5, -3) * mm});
            skLineSegment(sketch, "E321", {"start": v(42.5, -3) * mm, "end": v(39, -1.5) * mm});
            skLineSegment(sketch, "E322", {"start": v(39, -1.5) * mm, "end": v(39, 1.5) * mm});
            skLineSegment(sketch, "E323", {"start": v(39, 1.5) * mm, "end": v(42.5, 3) * mm});
            skLineSegment(sketch, "E324", {"start": v(42.5, 3) * mm, "end": v(46, 1.5) * mm});
            skLineSegment(sketch, "E325", {"start": v(46, 1.5) * mm, "end": v(46, -1.5) * mm});
            skLineSegment(sketch, "E326", {"start": v(39, 0) * mm, "end": v(49, 0) * mm, "construction": true});
            skLineSegment(sketch, "E327", {"start": v(49, 0) * mm, "end": v(49, 3) * mm, "construction": true});
            skLineSegment(sketch, "E328", {"start": v(49, -3) * mm, "end": v(49, -1.5) * mm, "construction": true});
            skLineSegment(sketch, "E329", {"start": v(49, -1.5) * mm, "end": v(49, 1.5) * mm, "construction": true});
            skLineSegment(sketch, "E330", {"start": v(49, 1.5) * mm, "end": v(49, 3) * mm, "construction": true});
            skLineSegment(sketch, "E331", {"start": v(49, 3) * mm, "end": v(52.5, 3) * mm, "construction": true});
            skLineSegment(sketch, "E332", {"start": v(52.5, 3) * mm, "end": v(56, 3) * mm, "construction": true});
            skLineSegment(sketch, "E333", {"start": v(56, 3) * mm, "end": v(56, 1.5) * mm, "construction": true});
            skLineSegment(sketch, "E334", {"start": v(56, 1.5) * mm, "end": v(56, -1.5) * mm, "construction": true});
            skLineSegment(sketch, "E335", {"start": v(56, -1.5) * mm, "end": v(56, -3) * mm, "construction": true});
            skLineSegment(sketch, "E336", {"start": v(56, -3) * mm, "end": v(52.5, -3) * mm, "construction": true});
            skLineSegment(sketch, "E337", {"start": v(52.5, -3) * mm, "end": v(49, -3) * mm, "construction": true});
            skLineSegment(sketch, "E338", {"start": v(56, -1.5) * mm, "end": v(52.5, -3) * mm});
            skLineSegment(sketch, "E339", {"start": v(52.5, -3) * mm, "end": v(49, -1.5) * mm});
            skLineSegment(sketch, "E340", {"start": v(49, -1.5) * mm, "end": v(49, 1.5) * mm});
            skLineSegment(sketch, "E341", {"start": v(49, 1.5) * mm, "end": v(52.5, 3) * mm});
            skLineSegment(sketch, "E342", {"start": v(52.5, 3) * mm, "end": v(56, 1.5) * mm});
            skLineSegment(sketch, "E343", {"start": v(56, 1.5) * mm, "end": v(56, -1.5) * mm});
            skLineSegment(sketch, "E344", {"start": v(49, 0) * mm, "end": v(59, 0) * mm, "construction": true});
            skLineSegment(sketch, "E345", {"start": v(59, 0) * mm, "end": v(59, 3) * mm, "construction": true});
            skLineSegment(sketch, "E346", {"start": v(59, -3) * mm, "end": v(59, -1.5) * mm, "construction": true});
            skLineSegment(sketch, "E347", {"start": v(59, -1.5) * mm, "end": v(59, 1.5) * mm, "construction": true});
            skLineSegment(sketch, "E348", {"start": v(59, 1.5) * mm, "end": v(59, 3) * mm, "construction": true});
            skLineSegment(sketch, "E349", {"start": v(59, 3) * mm, "end": v(62.5, 3) * mm, "construction": true});
            skLineSegment(sketch, "E350", {"start": v(62.5, 3) * mm, "end": v(66, 3) * mm, "construction": true});
            skLineSegment(sketch, "E351", {"start": v(66, 3) * mm, "end": v(66, 1.5) * mm, "construction": true});
            skLineSegment(sketch, "E352", {"start": v(66, 1.5) * mm, "end": v(66, -1.5) * mm, "construction": true});
            skLineSegment(sketch, "E353", {"start": v(66, -1.5) * mm, "end": v(66, -3) * mm, "construction": true});
            skLineSegment(sketch, "E354", {"start": v(66, -3) * mm, "end": v(62.5, -3) * mm, "construction": true});
            skLineSegment(sketch, "E355", {"start": v(62.5, -3) * mm, "end": v(59, -3) * mm, "construction": true});
            skLineSegment(sketch, "E356", {"start": v(66, -1.5) * mm, "end": v(62.5, -3) * mm});
            skLineSegment(sketch, "E357", {"start": v(62.5, -3) * mm, "end": v(59, -1.5) * mm});
            skLineSegment(sketch, "E358", {"start": v(59, -1.5) * mm, "end": v(59, 1.5) * mm});
            skLineSegment(sketch, "E359", {"start": v(59, 1.5) * mm, "end": v(62.5, 3) * mm});
            skLineSegment(sketch, "E360", {"start": v(62.5, 3) * mm, "end": v(66, 1.5) * mm});
            skLineSegment(sketch, "E361", {"start": v(66, 1.5) * mm, "end": v(66, -1.5) * mm});
            skLineSegment(sketch, "E362", {"start": v(59, 0) * mm, "end": v(69, 0) * mm, "construction": true});
            skLineSegment(sketch, "E363", {"start": v(69, 0) * mm, "end": v(69, 3) * mm, "construction": true});
            skLineSegment(sketch, "E364", {"start": v(69, -3) * mm, "end": v(69, -1.5) * mm, "construction": true});
            skLineSegment(sketch, "E365", {"start": v(69, -1.5) * mm, "end": v(69, 1.5) * mm, "construction": true});
            skLineSegment(sketch, "E366", {"start": v(69, 1.5) * mm, "end": v(69, 3) * mm, "construction": true});
            skLineSegment(sketch, "E367", {"start": v(69, 3) * mm, "end": v(72.5, 3) * mm, "construction": true});
            skLineSegment(sketch, "E368", {"start": v(72.5, 3) * mm, "end": v(76, 3) * mm, "construction": true});
            skLineSegment(sketch, "E369", {"start": v(76, 3) * mm, "end": v(76, 1.5) * mm, "construction": true});
            skLineSegment(sketch, "E370", {"start": v(76, 1.5) * mm, "end": v(76, -1.5) * mm, "construction": true});
            skLineSegment(sketch, "E371", {"start": v(76, -1.5) * mm, "end": v(76, -3) * mm, "construction": true});
            skLineSegment(sketch, "E372", {"start": v(76, -3) * mm, "end": v(72.5, -3) * mm, "construction": true});
            skLineSegment(sketch, "E373", {"start": v(72.5, -3) * mm, "end": v(69, -3) * mm, "construction": true});
            skLineSegment(sketch, "E374", {"start": v(76, -1.5) * mm, "end": v(72.5, -3) * mm});
            skLineSegment(sketch, "E375", {"start": v(72.5, -3) * mm, "end": v(69, -1.5) * mm});
            skLineSegment(sketch, "E376", {"start": v(69, -1.5) * mm, "end": v(69, 1.5) * mm});
            skLineSegment(sketch, "E377", {"start": v(69, 1.5) * mm, "end": v(72.5, 3) * mm});
            skLineSegment(sketch, "E378", {"start": v(72.5, 3) * mm, "end": v(76, 1.5) * mm});
            skLineSegment(sketch, "E379", {"start": v(76, 1.5) * mm, "end": v(76, -1.5) * mm});
            skLineSegment(sketch, "E380", {"start": v(69, 0) * mm, "end": v(79, 0) * mm, "construction": true});
            skLineSegment(sketch, "E381", {"start": v(79, 0) * mm, "end": v(79, 3) * mm, "construction": true});
            skLineSegment(sketch, "E382", {"start": v(79, -3) * mm, "end": v(79, -1.5) * mm, "construction": true});
            skLineSegment(sketch, "E383", {"start": v(79, -1.5) * mm, "end": v(79, 1.5) * mm, "construction": true});
            skLineSegment(sketch, "E384", {"start": v(79, 1.5) * mm, "end": v(79, 3) * mm, "construction": true});
            skLineSegment(sketch, "E385", {"start": v(79, 3) * mm, "end": v(82.5, 3) * mm, "construction": true});
            skLineSegment(sketch, "E386", {"start": v(82.5, 3) * mm, "end": v(86, 3) * mm, "construction": true});
            skLineSegment(sketch, "E387", {"start": v(86, 3) * mm, "end": v(86, 1.5) * mm, "construction": true});
            skLineSegment(sketch, "E388", {"start": v(86, 1.5) * mm, "end": v(86, -1.5) * mm, "construction": true});
            skLineSegment(sketch, "E389", {"start": v(86, -1.5) * mm, "end": v(86, -3) * mm, "construction": true});
            skLineSegment(sketch, "E390", {"start": v(86, -3) * mm, "end": v(82.5, -3) * mm, "construction": true});
            skLineSegment(sketch, "E391", {"start": v(82.5, -3) * mm, "end": v(79, -3) * mm, "construction": true});
            skLineSegment(sketch, "E392", {"start": v(86, -1.5) * mm, "end": v(82.5, -3) * mm});
            skLineSegment(sketch, "E393", {"start": v(82.5, -3) * mm, "end": v(79, -1.5) * mm});
            skLineSegment(sketch, "E394", {"start": v(79, -1.5) * mm, "end": v(79, 1.5) * mm});
            skLineSegment(sketch, "E395", {"start": v(79, 1.5) * mm, "end": v(82.5, 3) * mm});
            skLineSegment(sketch, "E396", {"start": v(82.5, 3) * mm, "end": v(86, 1.5) * mm});
            skLineSegment(sketch, "E397", {"start": v(86, 1.5) * mm, "end": v(86, -1.5) * mm});
            skLineSegment(sketch, "E398", {"start": v(79, 0) * mm, "end": v(89, 0) * mm, "construction": true});
            skLineSegment(sketch, "E399", {"start": v(89, 0) * mm, "end": v(89, 3) * mm, "construction": true});
            skLineSegment(sketch, "E400", {"start": v(89, -3) * mm, "end": v(89, -1.5) * mm, "construction": true});
            skLineSegment(sketch, "E401", {"start": v(89, -1.5) * mm, "end": v(89, 1.5) * mm, "construction": true});
            skLineSegment(sketch, "E402", {"start": v(89, 1.5) * mm, "end": v(89, 3) * mm, "construction": true});
            skLineSegment(sketch, "E403", {"start": v(89, 3) * mm, "end": v(92.5, 3) * mm, "construction": true});
            skLineSegment(sketch, "E404", {"start": v(92.5, 3) * mm, "end": v(96, 3) * mm, "construction": true});
            skLineSegment(sketch, "E405", {"start": v(96, 3) * mm, "end": v(96, 1.5) * mm, "construction": true});
            skLineSegment(sketch, "E406", {"start": v(96, 1.5) * mm, "end": v(96, -1.5) * mm, "construction": true});
            skLineSegment(sketch, "E407", {"start": v(96, -1.5) * mm, "end": v(96, -3) * mm, "construction": true});
            skLineSegment(sketch, "E408", {"start": v(96, -3) * mm, "end": v(92.5, -3) * mm, "construction": true});
            skLineSegment(sketch, "E409", {"start": v(92.5, -3) * mm, "end": v(89, -3) * mm, "construction": true});
            skLineSegment(sketch, "E410", {"start": v(96, -1.5) * mm, "end": v(92.5, -3) * mm});
            skLineSegment(sketch, "E411", {"start": v(92.5, -3) * mm, "end": v(89, -1.5) * mm});
            skLineSegment(sketch, "E412", {"start": v(89, -1.5) * mm, "end": v(89, 1.5) * mm});
            skLineSegment(sketch, "E413", {"start": v(89, 1.5) * mm, "end": v(92.5, 3) * mm});
            skLineSegment(sketch, "E414", {"start": v(92.5, 3) * mm, "end": v(96, 1.5) * mm});
            skLineSegment(sketch, "E415", {"start": v(96, 1.5) * mm, "end": v(96, -1.5) * mm});
            skLineSegment(sketch, "E416", {"start": v(89, 0) * mm, "end": v(99, 0) * mm, "construction": true});
            skLineSegment(sketch, "E417", {"start": v(99, 0) * mm, "end": v(99, 3) * mm, "construction": true});
            skLineSegment(sketch, "E418", {"start": v(99, -3) * mm, "end": v(99, -1.5) * mm, "construction": true});
            skLineSegment(sketch, "E419", {"start": v(99, -1.5) * mm, "end": v(99, 1.5) * mm, "construction": true});
            skLineSegment(sketch, "E420", {"start": v(99, 1.5) * mm, "end": v(99, 3) * mm, "construction": true});
            skLineSegment(sketch, "E421", {"start": v(99, 3) * mm, "end": v(102.5, 3) * mm, "construction": true});
            skLineSegment(sketch, "E422", {"start": v(102.5, 3) * mm, "end": v(106, 3) * mm, "construction": true});
            skLineSegment(sketch, "E423", {"start": v(106, 3) * mm, "end": v(106, 1.5) * mm, "construction": true});
            skLineSegment(sketch, "E424", {"start": v(106, 1.5) * mm, "end": v(106, -1.5) * mm, "construction": true});
            skLineSegment(sketch, "E425", {"start": v(106, -1.5) * mm, "end": v(106, -3) * mm, "construction": true});
            skLineSegment(sketch, "E426", {"start": v(106, -3) * mm, "end": v(102.5, -3) * mm, "construction": true});
            skLineSegment(sketch, "E427", {"start": v(102.5, -3) * mm, "end": v(99, -3) * mm, "construction": true});
            skLineSegment(sketch, "E428", {"start": v(106, -1.5) * mm, "end": v(102.5, -3) * mm});
            skLineSegment(sketch, "E429", {"start": v(102.5, -3) * mm, "end": v(99, -1.5) * mm});
            skLineSegment(sketch, "E430", {"start": v(99, -1.5) * mm, "end": v(99, 1.5) * mm});
            skLineSegment(sketch, "E431", {"start": v(99, 1.5) * mm, "end": v(102.5, 3) * mm});
            skLineSegment(sketch, "E432", {"start": v(102.5, 3) * mm, "end": v(106, 1.5) * mm});
            skLineSegment(sketch, "E433", {"start": v(106, 1.5) * mm, "end": v(106, -1.5) * mm});
            skLineSegment(sketch, "E434", {"start": v(99, 0) * mm, "end": v(109, 0) * mm, "construction": true});
            skLineSegment(sketch, "E435", {"start": v(109, 0) * mm, "end": v(109, 3) * mm, "construction": true});
            skLineSegment(sketch, "E436", {"start": v(109, -3) * mm, "end": v(109, -1.5) * mm, "construction": true});
            skLineSegment(sketch, "E437", {"start": v(109, -1.5) * mm, "end": v(109, 1.5) * mm, "construction": true});
            skLineSegment(sketch, "E438", {"start": v(109, 1.5) * mm, "end": v(109, 3) * mm, "construction": true});
            skLineSegment(sketch, "E439", {"start": v(109, 3) * mm, "end": v(112.5, 3) * mm, "construction": true});
            skLineSegment(sketch, "E440", {"start": v(112.5, 3) * mm, "end": v(116, 3) * mm, "construction": true});
            skLineSegment(sketch, "E441", {"start": v(116, 3) * mm, "end": v(116, 1.5) * mm, "construction": true});
            skLineSegment(sketch, "E442", {"start": v(116, 1.5) * mm, "end": v(116, -1.5) * mm, "construction": true});
            skLineSegment(sketch, "E443", {"start": v(116, -1.5) * mm, "end": v(116, -3) * mm, "construction": true});
            skLineSegment(sketch, "E444", {"start": v(116, -3) * mm, "end": v(112.5, -3) * mm, "construction": true});
            skLineSegment(sketch, "E445", {"start": v(112.5, -3) * mm, "end": v(109, -3) * mm, "construction": true});
            skLineSegment(sketch, "E446", {"start": v(116, -1.5) * mm, "end": v(112.5, -3) * mm});
            skLineSegment(sketch, "E447", {"start": v(112.5, -3) * mm, "end": v(109, -1.5) * mm});
            skLineSegment(sketch, "E448", {"start": v(109, -1.5) * mm, "end": v(109, 1.5) * mm});
            skLineSegment(sketch, "E449", {"start": v(109, 1.5) * mm, "end": v(112.5, 3) * mm});
            skLineSegment(sketch, "E450", {"start": v(112.5, 3) * mm, "end": v(116, 1.5) * mm});
            skLineSegment(sketch, "E451", {"start": v(116, 1.5) * mm, "end": v(116, -1.5) * mm});
            skLineSegment(sketch, "E452", {"start": v(109, 0) * mm, "end": v(119, 0) * mm, "construction": true});
            skLineSegment(sketch, "E453", {"start": v(119, 0) * mm, "end": v(119, 3) * mm, "construction": true});
            skLineSegment(sketch, "E454", {"start": v(119, -3) * mm, "end": v(119, -1.5) * mm, "construction": true});
            skLineSegment(sketch, "E455", {"start": v(119, -1.5) * mm, "end": v(119, 1.5) * mm, "construction": true});
            skLineSegment(sketch, "E456", {"start": v(119, 1.5) * mm, "end": v(119, 3) * mm, "construction": true});
            skLineSegment(sketch, "E457", {"start": v(119, 3) * mm, "end": v(122.5, 3) * mm, "construction": true});
            skLineSegment(sketch, "E458", {"start": v(122.5, 3) * mm, "end": v(126, 3) * mm, "construction": true});
            skLineSegment(sketch, "E459", {"start": v(126, 3) * mm, "end": v(126, 1.5) * mm, "construction": true});
            skLineSegment(sketch, "E460", {"start": v(126, 1.5) * mm, "end": v(126, -1.5) * mm, "construction": true});
            skLineSegment(sketch, "E461", {"start": v(126, -1.5) * mm, "end": v(126, -3) * mm, "construction": true});
            skLineSegment(sketch, "E462", {"start": v(126, -3) * mm, "end": v(122.5, -3) * mm, "construction": true});
            skLineSegment(sketch, "E463", {"start": v(122.5, -3) * mm, "end": v(119, -3) * mm, "construction": true});
            skLineSegment(sketch, "E464", {"start": v(126, -1.5) * mm, "end": v(122.5, -3) * mm});
            skLineSegment(sketch, "E465", {"start": v(122.5, -3) * mm, "end": v(119, -1.5) * mm});
            skLineSegment(sketch, "E466", {"start": v(119, -1.5) * mm, "end": v(119, 1.5) * mm});
            skLineSegment(sketch, "E467", {"start": v(119, 1.5) * mm, "end": v(122.5, 3) * mm});
            skLineSegment(sketch, "E468", {"start": v(122.5, 3) * mm, "end": v(126, 1.5) * mm});
            skLineSegment(sketch, "E469", {"start": v(126, 1.5) * mm, "end": v(126, -1.5) * mm});
            skLineSegment(sketch, "E470", {"start": v(119, 0) * mm, "end": v(129, 0) * mm, "construction": true});
            skLineSegment(sketch, "E471", {"start": v(129, 0) * mm, "end": v(129, 3) * mm, "construction": true});
            skLineSegment(sketch, "E472", {"start": v(129, -3) * mm, "end": v(129, -1.5) * mm, "construction": true});
            skLineSegment(sketch, "E473", {"start": v(129, -1.5) * mm, "end": v(129, 1.5) * mm, "construction": true});
            skLineSegment(sketch, "E474", {"start": v(129, 1.5) * mm, "end": v(129, 3) * mm, "construction": true});
            skLineSegment(sketch, "E475", {"start": v(129, 3) * mm, "end": v(132.5, 3) * mm, "construction": true});
            skLineSegment(sketch, "E476", {"start": v(132.5, 3) * mm, "end": v(136, 3) * mm, "construction": true});
            skLineSegment(sketch, "E477", {"start": v(136, 3) * mm, "end": v(136, 1.5) * mm, "construction": true});
            skLineSegment(sketch, "E478", {"start": v(136, 1.5) * mm, "end": v(136, -1.5) * mm, "construction": true});
            skLineSegment(sketch, "E479", {"start": v(136, -1.5) * mm, "end": v(136, -3) * mm, "construction": true});
            skLineSegment(sketch, "E480", {"start": v(136, -3) * mm, "end": v(132.5, -3) * mm, "construction": true});
            skLineSegment(sketch, "E481", {"start": v(132.5, -3) * mm, "end": v(129, -3) * mm, "construction": true});
            skLineSegment(sketch, "E482", {"start": v(136, -1.5) * mm, "end": v(132.5, -3) * mm});
            skLineSegment(sketch, "E483", {"start": v(132.5, -3) * mm, "end": v(129, -1.5) * mm});
            skLineSegment(sketch, "E484", {"start": v(129, -1.5) * mm, "end": v(129, 1.5) * mm});
            skLineSegment(sketch, "E485", {"start": v(129, 1.5) * mm, "end": v(132.5, 3) * mm});
            skLineSegment(sketch, "E486", {"start": v(132.5, 3) * mm, "end": v(136, 1.5) * mm});
            skLineSegment(sketch, "E487", {"start": v(136, 1.5) * mm, "end": v(136, -1.5) * mm});
            skLineSegment(sketch, "E488", {"start": v(129, 0) * mm, "end": v(139, 0) * mm, "construction": true});
            skLineSegment(sketch, "E489", {"start": v(139, 0) * mm, "end": v(139, 3) * mm, "construction": true});
            skLineSegment(sketch, "E490", {"start": v(139, -3) * mm, "end": v(139, -1.5) * mm, "construction": true});
            skLineSegment(sketch, "E491", {"start": v(139, -1.5) * mm, "end": v(139, 1.5) * mm, "construction": true});
            skLineSegment(sketch, "E492", {"start": v(139, 1.5) * mm, "end": v(139, 3) * mm, "construction": true});
            skLineSegment(sketch, "E493", {"start": v(139, 3) * mm, "end": v(142.5, 3) * mm, "construction": true});
            skLineSegment(sketch, "E494", {"start": v(142.5, 3) * mm, "end": v(146, 3) * mm, "construction": true});
            skLineSegment(sketch, "E495", {"start": v(146, 3) * mm, "end": v(146, 1.5) * mm, "construction": true});
            skLineSegment(sketch, "E496", {"start": v(146, 1.5) * mm, "end": v(146, -1.5) * mm, "construction": true});
            skLineSegment(sketch, "E497", {"start": v(146, -1.5) * mm, "end": v(146, -3) * mm, "construction": true});
            skLineSegment(sketch, "E498", {"start": v(146, -3) * mm, "end": v(142.5, -3) * mm, "construction": true});
            skLineSegment(sketch, "E499", {"start": v(142.5, -3) * mm, "end": v(139, -3) * mm, "construction": true});
            skLineSegment(sketch, "E500", {"start": v(146, -1.5) * mm, "end": v(142.5, -3) * mm});
            skLineSegment(sketch, "E501", {"start": v(142.5, -3) * mm, "end": v(139, -1.5) * mm});
            skLineSegment(sketch, "E502", {"start": v(139, -1.5) * mm, "end": v(139, 1.5) * mm});
            skLineSegment(sketch, "E503", {"start": v(139, 1.5) * mm, "end": v(142.5, 3) * mm});
            skLineSegment(sketch, "E504", {"start": v(142.5, 3) * mm, "end": v(146, 1.5) * mm});
            skLineSegment(sketch, "E505", {"start": v(146, 1.5) * mm, "end": v(146, -1.5) * mm});
            skSolve(sketch);
        }
        {
            var Q0;
            Q0=qSketchRegion(id+"F6",true);
            extrude(context, id + "F7", {"entities" : qUnion([Q0]), "operationType" : NewBodyOperationType.REMOVE, "endBound" : BoundingType.SYMMETRIC, "oppositeDirection" : true, "depth" : 25 * mm});
        }
        {
            var Q0;
            Q0=makeQuery(id+"F1.opExtrude","SWEPT_BODY",BODY,{"disambiguationData":[OSD([sQuery(id+"F0.wireOp",EDGE,"E0")])]});
            var Q1;
            Q1=makeQuery(id+"F1.opExtrude","SWEPT_FACE",FACE,{"disambiguationData":[OSD([sQuery(id+"F0.wireOp",EDGE,"E0")])]});
            transform(context, id + "F8", {"entities" : qUnion([Q0]), "transformType" : TransformType.ROTATION, "transformAxis" : qUnion([Q1]), "angle" : 45 * degree, "makeCopy" : false});
        }
        {
            var Q0;
            Q0=qCreatedBy(makeId("Top.planeOp"),FACE);
            var sketch = newSketch(context, id + "F9", { "sketchPlane" : qUnion([Q0])});
            skLineSegment(sketch, "E506", {"start": v(0, 0) * mm, "end": v(0, 4) * mm, "construction": true});
            skLineSegment(sketch, "E507", {"start": v(-3, 7.5) * mm, "end": v(-3, 11) * mm, "construction": true});
            skLineSegment(sketch, "E508", {"start": v(-3, 11) * mm, "end": v(-1.5, 11) * mm, "construction": true});
            skLineSegment(sketch, "E509", {"start": v(-1.5, 11) * mm, "end": v(1.5, 11) * mm, "construction": true});
            skLineSegment(sketch, "E510", {"start": v(1.5, 11) * mm, "end": v(3, 11) * mm, "construction": true});
            skLineSegment(sketch, "E511", {"start": v(3, 11) * mm, "end": v(3, 7.5) * mm, "construction": true});
            skLineSegment(sketch, "E512", {"start": v(-1.5, 11) * mm, "end": v(1.5, 11) * mm});
            skLineSegment(sketch, "E513", {"start": v(0, 4) * mm, "end": v(0, 14) * mm, "construction": true});
            skPoint(sketch, "E513.endSnap0", {"position": v(0, 11) * mm});
            skLineSegment(sketch, "E514", {"start": v(0, 14) * mm, "end": v(-3, 14) * mm, "construction": true});
            skLineSegment(sketch, "E515", {"start": v(3, 14) * mm, "end": v(1.5, 14) * mm, "construction": true});
            skLineSegment(sketch, "E516", {"start": v(1.5, 14) * mm, "end": v(-1.5, 14) * mm, "construction": true});
            skLineSegment(sketch, "E517", {"start": v(-1.5, 14) * mm, "end": v(-3, 14) * mm, "construction": true});
            skLineSegment(sketch, "E518", {"start": v(-3, 14) * mm, "end": v(-3, 17.5) * mm, "construction": true});
            skLineSegment(sketch, "E519", {"start": v(-3, 17.5) * mm, "end": v(-3, 21) * mm, "construction": true});
            skLineSegment(sketch, "E520", {"start": v(-3, 21) * mm, "end": v(-1.5, 21) * mm, "construction": true});
            skLineSegment(sketch, "E521", {"start": v(-1.5, 21) * mm, "end": v(1.5, 21) * mm, "construction": true});
            skLineSegment(sketch, "E522", {"start": v(1.5, 21) * mm, "end": v(3, 21) * mm, "construction": true});
            skLineSegment(sketch, "E523", {"start": v(3, 21) * mm, "end": v(3, 17.5) * mm, "construction": true});
            skLineSegment(sketch, "E524", {"start": v(3, 17.5) * mm, "end": v(3, 14) * mm, "construction": true});
            skLineSegment(sketch, "E525", {"start": v(1.5, 21) * mm, "end": v(3, 17.5) * mm});
            skLineSegment(sketch, "E526", {"start": v(3, 17.5) * mm, "end": v(1.5, 14) * mm});
            skLineSegment(sketch, "E527", {"start": v(1.5, 14) * mm, "end": v(-1.5, 14) * mm});
            skLineSegment(sketch, "E528", {"start": v(-1.5, 14) * mm, "end": v(-3, 17.5) * mm});
            skLineSegment(sketch, "E529", {"start": v(-3, 17.5) * mm, "end": v(-1.5, 21) * mm});
            skLineSegment(sketch, "E530", {"start": v(-1.5, 21) * mm, "end": v(1.5, 21) * mm});
            skLineSegment(sketch, "E531", {"start": v(0, 14) * mm, "end": v(0, 24) * mm, "construction": true});
            skLineSegment(sketch, "E532", {"start": v(0, 24) * mm, "end": v(-3, 24) * mm, "construction": true});
            skLineSegment(sketch, "E533", {"start": v(3, 24) * mm, "end": v(1.5, 24) * mm, "construction": true});
            skLineSegment(sketch, "E534", {"start": v(1.5, 24) * mm, "end": v(-1.5, 24) * mm, "construction": true});
            skLineSegment(sketch, "E535", {"start": v(-1.5, 24) * mm, "end": v(-3, 24) * mm, "construction": true});
            skLineSegment(sketch, "E536", {"start": v(-3, 24) * mm, "end": v(-3, 27.5) * mm, "construction": true});
            skLineSegment(sketch, "E537", {"start": v(-3, 27.5) * mm, "end": v(-3, 31) * mm, "construction": true});
            skLineSegment(sketch, "E538", {"start": v(-3, 31) * mm, "end": v(-1.5, 31) * mm, "construction": true});
            skLineSegment(sketch, "E539", {"start": v(-1.5, 31) * mm, "end": v(1.5, 31) * mm, "construction": true});
            skLineSegment(sketch, "E540", {"start": v(1.5, 31) * mm, "end": v(3, 31) * mm, "construction": true});
            skLineSegment(sketch, "E541", {"start": v(3, 31) * mm, "end": v(3, 27.5) * mm, "construction": true});
            skLineSegment(sketch, "E542", {"start": v(3, 27.5) * mm, "end": v(3, 24) * mm, "construction": true});
            skLineSegment(sketch, "E543", {"start": v(1.5, 31) * mm, "end": v(3, 27.5) * mm});
            skLineSegment(sketch, "E544", {"start": v(3, 27.5) * mm, "end": v(1.5, 24) * mm});
            skLineSegment(sketch, "E545", {"start": v(1.5, 24) * mm, "end": v(-1.5, 24) * mm});
            skLineSegment(sketch, "E546", {"start": v(-1.5, 24) * mm, "end": v(-3, 27.5) * mm});
            skLineSegment(sketch, "E547", {"start": v(-3, 27.5) * mm, "end": v(-1.5, 31) * mm});
            skLineSegment(sketch, "E548", {"start": v(-1.5, 31) * mm, "end": v(1.5, 31) * mm});
            skLineSegment(sketch, "E549", {"start": v(0, 24) * mm, "end": v(0, 34) * mm, "construction": true});
            skLineSegment(sketch, "E550", {"start": v(0, 34) * mm, "end": v(-3, 34) * mm, "construction": true});
            skLineSegment(sketch, "E551", {"start": v(3, 34) * mm, "end": v(1.5, 34) * mm, "construction": true});
            skLineSegment(sketch, "E552", {"start": v(1.5, 34) * mm, "end": v(-1.5, 34) * mm, "construction": true});
            skLineSegment(sketch, "E553", {"start": v(-1.5, 34) * mm, "end": v(-3, 34) * mm, "construction": true});
            skLineSegment(sketch, "E554", {"start": v(-3, 34) * mm, "end": v(-3, 37.5) * mm, "construction": true});
            skLineSegment(sketch, "E555", {"start": v(-3, 37.5) * mm, "end": v(-3, 41) * mm, "construction": true});
            skLineSegment(sketch, "E556", {"start": v(-3, 41) * mm, "end": v(-1.5, 41) * mm, "construction": true});
            skLineSegment(sketch, "E557", {"start": v(-1.5, 41) * mm, "end": v(1.5, 41) * mm, "construction": true});
            skLineSegment(sketch, "E558", {"start": v(1.5, 41) * mm, "end": v(3, 41) * mm, "construction": true});
            skLineSegment(sketch, "E559", {"start": v(3, 41) * mm, "end": v(3, 37.5) * mm, "construction": true});
            skLineSegment(sketch, "E560", {"start": v(3, 37.5) * mm, "end": v(3, 34) * mm, "construction": true});
            skLineSegment(sketch, "E561", {"start": v(1.5, 41) * mm, "end": v(3, 37.5) * mm});
            skLineSegment(sketch, "E562", {"start": v(3, 37.5) * mm, "end": v(1.5, 34) * mm});
            skLineSegment(sketch, "E563", {"start": v(1.5, 34) * mm, "end": v(-1.5, 34) * mm});
            skLineSegment(sketch, "E564", {"start": v(-1.5, 34) * mm, "end": v(-3, 37.5) * mm});
            skLineSegment(sketch, "E565", {"start": v(-3, 37.5) * mm, "end": v(-1.5, 41) * mm});
            skLineSegment(sketch, "E566", {"start": v(-1.5, 41) * mm, "end": v(1.5, 41) * mm});
            skLineSegment(sketch, "E567", {"start": v(0, 34) * mm, "end": v(0, 44) * mm, "construction": true});
            skLineSegment(sketch, "E568", {"start": v(0, 44) * mm, "end": v(-3, 44) * mm, "construction": true});
            skLineSegment(sketch, "E569", {"start": v(3, 44) * mm, "end": v(1.5, 44) * mm, "construction": true});
            skLineSegment(sketch, "E570", {"start": v(1.5, 44) * mm, "end": v(-1.5, 44) * mm, "construction": true});
            skLineSegment(sketch, "E571", {"start": v(-1.5, 44) * mm, "end": v(-3, 44) * mm, "construction": true});
            skLineSegment(sketch, "E572", {"start": v(-3, 44) * mm, "end": v(-3, 47.5) * mm, "construction": true});
            skLineSegment(sketch, "E573", {"start": v(-3, 47.5) * mm, "end": v(-3, 51) * mm, "construction": true});
            skLineSegment(sketch, "E574", {"start": v(-3, 51) * mm, "end": v(-1.5, 51) * mm, "construction": true});
            skLineSegment(sketch, "E575", {"start": v(-1.5, 51) * mm, "end": v(1.5, 51) * mm, "construction": true});
            skLineSegment(sketch, "E576", {"start": v(1.5, 51) * mm, "end": v(3, 51) * mm, "construction": true});
            skLineSegment(sketch, "E577", {"start": v(3, 51) * mm, "end": v(3, 47.5) * mm, "construction": true});
            skLineSegment(sketch, "E578", {"start": v(3, 47.5) * mm, "end": v(3, 44) * mm, "construction": true});
            skLineSegment(sketch, "E579", {"start": v(1.5, 51) * mm, "end": v(3, 47.5) * mm});
            skLineSegment(sketch, "E580", {"start": v(3, 47.5) * mm, "end": v(1.5, 44) * mm});
            skLineSegment(sketch, "E581", {"start": v(1.5, 44) * mm, "end": v(-1.5, 44) * mm});
            skLineSegment(sketch, "E582", {"start": v(-1.5, 44) * mm, "end": v(-3, 47.5) * mm});
            skLineSegment(sketch, "E583", {"start": v(-3, 47.5) * mm, "end": v(-1.5, 51) * mm});
            skLineSegment(sketch, "E584", {"start": v(-1.5, 51) * mm, "end": v(1.5, 51) * mm});
            skLineSegment(sketch, "E585", {"start": v(0, 44) * mm, "end": v(0, 54) * mm, "construction": true});
            skLineSegment(sketch, "E586", {"start": v(0, 54) * mm, "end": v(-3, 54) * mm, "construction": true});
            skLineSegment(sketch, "E587", {"start": v(3, 54) * mm, "end": v(1.5, 54) * mm, "construction": true});
            skLineSegment(sketch, "E588", {"start": v(1.5, 54) * mm, "end": v(-1.5, 54) * mm, "construction": true});
            skLineSegment(sketch, "E589", {"start": v(-1.5, 54) * mm, "end": v(-3, 54) * mm, "construction": true});
            skLineSegment(sketch, "E590", {"start": v(-3, 54) * mm, "end": v(-3, 57.5) * mm, "construction": true});
            skLineSegment(sketch, "E591", {"start": v(-3, 57.5) * mm, "end": v(-3, 61) * mm, "construction": true});
            skLineSegment(sketch, "E592", {"start": v(-3, 61) * mm, "end": v(-1.5, 61) * mm, "construction": true});
            skLineSegment(sketch, "E593", {"start": v(-1.5, 61) * mm, "end": v(1.5, 61) * mm, "construction": true});
            skLineSegment(sketch, "E594", {"start": v(1.5, 61) * mm, "end": v(3, 61) * mm, "construction": true});
            skLineSegment(sketch, "E595", {"start": v(3, 61) * mm, "end": v(3, 57.5) * mm, "construction": true});
            skLineSegment(sketch, "E596", {"start": v(3, 57.5) * mm, "end": v(3, 54) * mm, "construction": true});
            skLineSegment(sketch, "E597", {"start": v(1.5, 61) * mm, "end": v(3, 57.5) * mm});
            skLineSegment(sketch, "E598", {"start": v(3, 57.5) * mm, "end": v(1.5, 54) * mm});
            skLineSegment(sketch, "E599", {"start": v(1.5, 54) * mm, "end": v(-1.5, 54) * mm});
            skLineSegment(sketch, "E600", {"start": v(-1.5, 54) * mm, "end": v(-3, 57.5) * mm});
            skLineSegment(sketch, "E601", {"start": v(-3, 57.5) * mm, "end": v(-1.5, 61) * mm});
            skLineSegment(sketch, "E602", {"start": v(-1.5, 61) * mm, "end": v(1.5, 61) * mm});
            skLineSegment(sketch, "E603", {"start": v(0, 54) * mm, "end": v(0, 64) * mm, "construction": true});
            skLineSegment(sketch, "E604", {"start": v(0, 64) * mm, "end": v(-3, 64) * mm, "construction": true});
            skLineSegment(sketch, "E605", {"start": v(3, 64) * mm, "end": v(1.5, 64) * mm, "construction": true});
            skLineSegment(sketch, "E606", {"start": v(1.5, 64) * mm, "end": v(-1.5, 64) * mm, "construction": true});
            skLineSegment(sketch, "E607", {"start": v(-1.5, 64) * mm, "end": v(-3, 64) * mm, "construction": true});
            skLineSegment(sketch, "E608", {"start": v(-3, 64) * mm, "end": v(-3, 67.5) * mm, "construction": true});
            skLineSegment(sketch, "E609", {"start": v(-3, 67.5) * mm, "end": v(-3, 71) * mm, "construction": true});
            skLineSegment(sketch, "E610", {"start": v(-3, 71) * mm, "end": v(-1.5, 71) * mm, "construction": true});
            skLineSegment(sketch, "E611", {"start": v(-1.5, 71) * mm, "end": v(1.5, 71) * mm, "construction": true});
            skLineSegment(sketch, "E612", {"start": v(1.5, 71) * mm, "end": v(3, 71) * mm, "construction": true});
            skLineSegment(sketch, "E613", {"start": v(3, 71) * mm, "end": v(3, 67.5) * mm, "construction": true});
            skLineSegment(sketch, "E614", {"start": v(3, 67.5) * mm, "end": v(3, 64) * mm, "construction": true});
            skLineSegment(sketch, "E615", {"start": v(1.5, 71) * mm, "end": v(3, 67.5) * mm});
            skLineSegment(sketch, "E616", {"start": v(3, 67.5) * mm, "end": v(1.5, 64) * mm});
            skLineSegment(sketch, "E617", {"start": v(1.5, 64) * mm, "end": v(-1.5, 64) * mm});
            skLineSegment(sketch, "E618", {"start": v(-1.5, 64) * mm, "end": v(-3, 67.5) * mm});
            skLineSegment(sketch, "E619", {"start": v(-3, 67.5) * mm, "end": v(-1.5, 71) * mm});
            skLineSegment(sketch, "E620", {"start": v(-1.5, 71) * mm, "end": v(1.5, 71) * mm});
            skLineSegment(sketch, "E621", {"start": v(0, 64) * mm, "end": v(0, 74) * mm, "construction": true});
            skLineSegment(sketch, "E622", {"start": v(0, 74) * mm, "end": v(-3, 74) * mm, "construction": true});
            skLineSegment(sketch, "E623", {"start": v(3, 74) * mm, "end": v(1.5, 74) * mm, "construction": true});
            skLineSegment(sketch, "E624", {"start": v(1.5, 74) * mm, "end": v(-1.5, 74) * mm, "construction": true});
            skLineSegment(sketch, "E625", {"start": v(-1.5, 74) * mm, "end": v(-3, 74) * mm, "construction": true});
            skLineSegment(sketch, "E626", {"start": v(-3, 74) * mm, "end": v(-3, 77.5) * mm, "construction": true});
            skLineSegment(sketch, "E627", {"start": v(-3, 77.5) * mm, "end": v(-3, 81) * mm, "construction": true});
            skLineSegment(sketch, "E628", {"start": v(-3, 81) * mm, "end": v(-1.5, 81) * mm, "construction": true});
            skLineSegment(sketch, "E629", {"start": v(-1.5, 81) * mm, "end": v(1.5, 81) * mm, "construction": true});
            skLineSegment(sketch, "E630", {"start": v(1.5, 81) * mm, "end": v(3, 81) * mm, "construction": true});
            skLineSegment(sketch, "E631", {"start": v(3, 81) * mm, "end": v(3, 77.5) * mm, "construction": true});
            skLineSegment(sketch, "E632", {"start": v(3, 77.5) * mm, "end": v(3, 74) * mm, "construction": true});
            skLineSegment(sketch, "E633", {"start": v(1.5, 81) * mm, "end": v(3, 77.5) * mm});
            skLineSegment(sketch, "E634", {"start": v(3, 77.5) * mm, "end": v(1.5, 74) * mm});
            skLineSegment(sketch, "E635", {"start": v(1.5, 74) * mm, "end": v(-1.5, 74) * mm});
            skLineSegment(sketch, "E636", {"start": v(-1.5, 74) * mm, "end": v(-3, 77.5) * mm});
            skLineSegment(sketch, "E637", {"start": v(-3, 77.5) * mm, "end": v(-1.5, 81) * mm});
            skLineSegment(sketch, "E638", {"start": v(-1.5, 81) * mm, "end": v(1.5, 81) * mm});
            skLineSegment(sketch, "E639", {"start": v(0, 74) * mm, "end": v(0, 84) * mm, "construction": true});
            skLineSegment(sketch, "E640", {"start": v(0, 84) * mm, "end": v(-3, 84) * mm, "construction": true});
            skLineSegment(sketch, "E641", {"start": v(3, 84) * mm, "end": v(1.5, 84) * mm, "construction": true});
            skLineSegment(sketch, "E642", {"start": v(1.5, 84) * mm, "end": v(-1.5, 84) * mm, "construction": true});
            skLineSegment(sketch, "E643", {"start": v(-1.5, 84) * mm, "end": v(-3, 84) * mm, "construction": true});
            skLineSegment(sketch, "E644", {"start": v(-3, 84) * mm, "end": v(-3, 87.5) * mm, "construction": true});
            skLineSegment(sketch, "E645", {"start": v(-3, 87.5) * mm, "end": v(-3, 91) * mm, "construction": true});
            skLineSegment(sketch, "E646", {"start": v(-3, 91) * mm, "end": v(-1.5, 91) * mm, "construction": true});
            skLineSegment(sketch, "E647", {"start": v(-1.5, 91) * mm, "end": v(1.5, 91) * mm, "construction": true});
            skLineSegment(sketch, "E648", {"start": v(1.5, 91) * mm, "end": v(3, 91) * mm, "construction": true});
            skLineSegment(sketch, "E649", {"start": v(3, 91) * mm, "end": v(3, 87.5) * mm, "construction": true});
            skLineSegment(sketch, "E650", {"start": v(3, 87.5) * mm, "end": v(3, 84) * mm, "construction": true});
            skLineSegment(sketch, "E651", {"start": v(1.5, 91) * mm, "end": v(3, 87.5) * mm});
            skLineSegment(sketch, "E652", {"start": v(3, 87.5) * mm, "end": v(1.5, 84) * mm});
            skLineSegment(sketch, "E653", {"start": v(1.5, 84) * mm, "end": v(-1.5, 84) * mm});
            skLineSegment(sketch, "E654", {"start": v(-1.5, 84) * mm, "end": v(-3, 87.5) * mm});
            skLineSegment(sketch, "E655", {"start": v(-3, 87.5) * mm, "end": v(-1.5, 91) * mm});
            skLineSegment(sketch, "E656", {"start": v(-1.5, 91) * mm, "end": v(1.5, 91) * mm});
            skLineSegment(sketch, "E657", {"start": v(0, 84) * mm, "end": v(0, 94) * mm, "construction": true});
            skLineSegment(sketch, "E658", {"start": v(0, 94) * mm, "end": v(-3, 94) * mm, "construction": true});
            skLineSegment(sketch, "E659", {"start": v(3, 94) * mm, "end": v(1.5, 94) * mm, "construction": true});
            skLineSegment(sketch, "E660", {"start": v(1.5, 94) * mm, "end": v(-1.5, 94) * mm, "construction": true});
            skLineSegment(sketch, "E661", {"start": v(-1.5, 94) * mm, "end": v(-3, 94) * mm, "construction": true});
            skLineSegment(sketch, "E662", {"start": v(-3, 94) * mm, "end": v(-3, 97.5) * mm, "construction": true});
            skLineSegment(sketch, "E663", {"start": v(-3, 97.5) * mm, "end": v(-3, 101) * mm, "construction": true});
            skLineSegment(sketch, "E664", {"start": v(-3, 101) * mm, "end": v(-1.5, 101) * mm, "construction": true});
            skLineSegment(sketch, "E665", {"start": v(-1.5, 101) * mm, "end": v(1.5, 101) * mm, "construction": true});
            skLineSegment(sketch, "E666", {"start": v(1.5, 101) * mm, "end": v(3, 101) * mm, "construction": true});
            skLineSegment(sketch, "E667", {"start": v(3, 101) * mm, "end": v(3, 97.5) * mm, "construction": true});
            skLineSegment(sketch, "E668", {"start": v(3, 97.5) * mm, "end": v(3, 94) * mm, "construction": true});
            skLineSegment(sketch, "E669", {"start": v(1.5, 101) * mm, "end": v(3, 97.5) * mm});
            skLineSegment(sketch, "E670", {"start": v(3, 97.5) * mm, "end": v(1.5, 94) * mm});
            skLineSegment(sketch, "E671", {"start": v(1.5, 94) * mm, "end": v(-1.5, 94) * mm});
            skLineSegment(sketch, "E672", {"start": v(-1.5, 94) * mm, "end": v(-3, 97.5) * mm});
            skLineSegment(sketch, "E673", {"start": v(-3, 97.5) * mm, "end": v(-1.5, 101) * mm});
            skLineSegment(sketch, "E674", {"start": v(-1.5, 101) * mm, "end": v(1.5, 101) * mm});
            skLineSegment(sketch, "E675", {"start": v(0, 94) * mm, "end": v(0, 104) * mm, "construction": true});
            skLineSegment(sketch, "E676", {"start": v(0, 104) * mm, "end": v(-3, 104) * mm, "construction": true});
            skLineSegment(sketch, "E677", {"start": v(3, 104) * mm, "end": v(1.5, 104) * mm, "construction": true});
            skLineSegment(sketch, "E678", {"start": v(1.5, 104) * mm, "end": v(-1.5, 104) * mm, "construction": true});
            skLineSegment(sketch, "E679", {"start": v(-1.5, 104) * mm, "end": v(-3, 104) * mm, "construction": true});
            skLineSegment(sketch, "E680", {"start": v(-3, 104) * mm, "end": v(-3, 107.5) * mm, "construction": true});
            skLineSegment(sketch, "E681", {"start": v(-3, 107.5) * mm, "end": v(-3, 111) * mm, "construction": true});
            skLineSegment(sketch, "E682", {"start": v(-3, 111) * mm, "end": v(-1.5, 111) * mm, "construction": true});
            skLineSegment(sketch, "E683", {"start": v(-1.5, 111) * mm, "end": v(1.5, 111) * mm, "construction": true});
            skLineSegment(sketch, "E684", {"start": v(1.5, 111) * mm, "end": v(3, 111) * mm, "construction": true});
            skLineSegment(sketch, "E685", {"start": v(3, 111) * mm, "end": v(3, 107.5) * mm, "construction": true});
            skLineSegment(sketch, "E686", {"start": v(3, 107.5) * mm, "end": v(3, 104) * mm, "construction": true});
            skLineSegment(sketch, "E687", {"start": v(1.5, 111) * mm, "end": v(3, 107.5) * mm});
            skLineSegment(sketch, "E688", {"start": v(3, 107.5) * mm, "end": v(1.5, 104) * mm});
            skLineSegment(sketch, "E689", {"start": v(1.5, 104) * mm, "end": v(-1.5, 104) * mm});
            skLineSegment(sketch, "E690", {"start": v(-1.5, 104) * mm, "end": v(-3, 107.5) * mm});
            skLineSegment(sketch, "E691", {"start": v(-3, 107.5) * mm, "end": v(-1.5, 111) * mm});
            skLineSegment(sketch, "E692", {"start": v(-1.5, 111) * mm, "end": v(1.5, 111) * mm});
            skLineSegment(sketch, "E693", {"start": v(0, 104) * mm, "end": v(0, 114) * mm, "construction": true});
            skLineSegment(sketch, "E694", {"start": v(0, 114) * mm, "end": v(-3, 114) * mm, "construction": true});
            skLineSegment(sketch, "E695", {"start": v(3, 114) * mm, "end": v(1.5, 114) * mm, "construction": true});
            skLineSegment(sketch, "E696", {"start": v(1.5, 114) * mm, "end": v(-1.5, 114) * mm, "construction": true});
            skLineSegment(sketch, "E697", {"start": v(-1.5, 114) * mm, "end": v(-3, 114) * mm, "construction": true});
            skLineSegment(sketch, "E698", {"start": v(-3, 114) * mm, "end": v(-3, 117.5) * mm, "construction": true});
            skLineSegment(sketch, "E699", {"start": v(-3, 117.5) * mm, "end": v(-3, 121) * mm, "construction": true});
            skLineSegment(sketch, "E700", {"start": v(-3, 121) * mm, "end": v(-1.5, 121) * mm, "construction": true});
            skLineSegment(sketch, "E701", {"start": v(-1.5, 121) * mm, "end": v(1.5, 121) * mm, "construction": true});
            skLineSegment(sketch, "E702", {"start": v(1.5, 121) * mm, "end": v(3, 121) * mm, "construction": true});
            skLineSegment(sketch, "E703", {"start": v(3, 121) * mm, "end": v(3, 117.5) * mm, "construction": true});
            skLineSegment(sketch, "E704", {"start": v(3, 117.5) * mm, "end": v(3, 114) * mm, "construction": true});
            skLineSegment(sketch, "E705", {"start": v(1.5, 121) * mm, "end": v(3, 117.5) * mm});
            skLineSegment(sketch, "E706", {"start": v(3, 117.5) * mm, "end": v(1.5, 114) * mm});
            skLineSegment(sketch, "E707", {"start": v(1.5, 114) * mm, "end": v(-1.5, 114) * mm});
            skLineSegment(sketch, "E708", {"start": v(-1.5, 114) * mm, "end": v(-3, 117.5) * mm});
            skLineSegment(sketch, "E709", {"start": v(-3, 117.5) * mm, "end": v(-1.5, 121) * mm});
            skLineSegment(sketch, "E710", {"start": v(-1.5, 121) * mm, "end": v(1.5, 121) * mm});
            skLineSegment(sketch, "E711", {"start": v(0, 114) * mm, "end": v(0, 124) * mm, "construction": true});
            skLineSegment(sketch, "E712", {"start": v(0, 124) * mm, "end": v(-3, 124) * mm, "construction": true});
            skLineSegment(sketch, "E713", {"start": v(3, 124) * mm, "end": v(1.5, 124) * mm, "construction": true});
            skLineSegment(sketch, "E714", {"start": v(1.5, 124) * mm, "end": v(-1.5, 124) * mm, "construction": true});
            skLineSegment(sketch, "E715", {"start": v(-1.5, 124) * mm, "end": v(-3, 124) * mm, "construction": true});
            skLineSegment(sketch, "E716", {"start": v(-3, 124) * mm, "end": v(-3, 127.5) * mm, "construction": true});
            skLineSegment(sketch, "E717", {"start": v(-3, 127.5) * mm, "end": v(-3, 131) * mm, "construction": true});
            skLineSegment(sketch, "E718", {"start": v(-3, 131) * mm, "end": v(-1.5, 131) * mm, "construction": true});
            skLineSegment(sketch, "E719", {"start": v(-1.5, 131) * mm, "end": v(1.5, 131) * mm, "construction": true});
            skLineSegment(sketch, "E720", {"start": v(1.5, 131) * mm, "end": v(3, 131) * mm, "construction": true});
            skLineSegment(sketch, "E721", {"start": v(3, 131) * mm, "end": v(3, 127.5) * mm, "construction": true});
            skLineSegment(sketch, "E722", {"start": v(3, 127.5) * mm, "end": v(3, 124) * mm, "construction": true});
            skLineSegment(sketch, "E723", {"start": v(1.5, 131) * mm, "end": v(3, 127.5) * mm});
            skLineSegment(sketch, "E724", {"start": v(3, 127.5) * mm, "end": v(1.5, 124) * mm});
            skLineSegment(sketch, "E725", {"start": v(1.5, 124) * mm, "end": v(-1.5, 124) * mm});
            skLineSegment(sketch, "E726", {"start": v(-1.5, 124) * mm, "end": v(-3, 127.5) * mm});
            skLineSegment(sketch, "E727", {"start": v(-3, 127.5) * mm, "end": v(-1.5, 131) * mm});
            skLineSegment(sketch, "E728", {"start": v(-1.5, 131) * mm, "end": v(1.5, 131) * mm});
            skLineSegment(sketch, "E729", {"start": v(0, 124) * mm, "end": v(0, 134) * mm, "construction": true});
            skLineSegment(sketch, "E730", {"start": v(0, 134) * mm, "end": v(-3, 134) * mm, "construction": true});
            skLineSegment(sketch, "E731", {"start": v(3, 134) * mm, "end": v(1.5, 134) * mm, "construction": true});
            skLineSegment(sketch, "E732", {"start": v(1.5, 134) * mm, "end": v(-1.5, 134) * mm, "construction": true});
            skLineSegment(sketch, "E733", {"start": v(-1.5, 134) * mm, "end": v(-3, 134) * mm, "construction": true});
            skLineSegment(sketch, "E734", {"start": v(-3, 134) * mm, "end": v(-3, 137.5) * mm, "construction": true});
            skLineSegment(sketch, "E735", {"start": v(-3, 137.5) * mm, "end": v(-3, 141) * mm, "construction": true});
            skLineSegment(sketch, "E736", {"start": v(-3, 141) * mm, "end": v(-1.5, 141) * mm, "construction": true});
            skLineSegment(sketch, "E737", {"start": v(-1.5, 141) * mm, "end": v(1.5, 141) * mm, "construction": true});
            skLineSegment(sketch, "E738", {"start": v(1.5, 141) * mm, "end": v(3, 141) * mm, "construction": true});
            skLineSegment(sketch, "E739", {"start": v(3, 141) * mm, "end": v(3, 137.5) * mm, "construction": true});
            skLineSegment(sketch, "E740", {"start": v(3, 137.5) * mm, "end": v(3, 134) * mm, "construction": true});
            skLineSegment(sketch, "E741", {"start": v(1.5, 141) * mm, "end": v(3, 137.5) * mm});
            skLineSegment(sketch, "E742", {"start": v(3, 137.5) * mm, "end": v(1.5, 134) * mm});
            skLineSegment(sketch, "E743", {"start": v(1.5, 134) * mm, "end": v(-1.5, 134) * mm});
            skLineSegment(sketch, "E744", {"start": v(-1.5, 134) * mm, "end": v(-3, 137.5) * mm});
            skLineSegment(sketch, "E745", {"start": v(-3, 137.5) * mm, "end": v(-1.5, 141) * mm});
            skLineSegment(sketch, "E746", {"start": v(-1.5, 141) * mm, "end": v(1.5, 141) * mm});
            skLineSegment(sketch, "E747", {"start": v(0, 134) * mm, "end": v(0, 144) * mm, "construction": true});
            skLineSegment(sketch, "E748", {"start": v(0, 144) * mm, "end": v(-3, 144) * mm, "construction": true});
            skLineSegment(sketch, "E749", {"start": v(3, 144) * mm, "end": v(1.5, 144) * mm, "construction": true});
            skLineSegment(sketch, "E750", {"start": v(1.5, 144) * mm, "end": v(-1.5, 144) * mm, "construction": true});
            skLineSegment(sketch, "E751", {"start": v(-1.5, 144) * mm, "end": v(-3, 144) * mm, "construction": true});
            skLineSegment(sketch, "E752", {"start": v(1.5, 144) * mm, "end": v(-1.5, 144) * mm});
            skLineSegment(sketch, "E753", {"start": v(1.5, 11) * mm, "end": v(1.5, 9) * mm, "construction": true});
            skLineSegment(sketch, "E754", {"start": v(1.5, 9) * mm, "end": v(2.36, 9) * mm});
            skLineSegment(sketch, "E755", {"start": v(1.5, 9) * mm, "end": v(-2.36, 9) * mm});
            skLineSegment(sketch, "E756", {"start": v(1.5, 11) * mm, "end": v(2.36, 9) * mm});
            skLineSegment(sketch, "E757", {"start": v(-1.5, 11) * mm, "end": v(-2.36, 9) * mm});
            skLineSegment(sketch, "E758", {"start": v(1.5, 144) * mm, "end": v(1.5, 146) * mm, "construction": true});
            skLineSegment(sketch, "E759", {"start": v(1.5, 146) * mm, "end": v(2.36, 146) * mm});
            skLineSegment(sketch, "E760", {"start": v(1.5, 146) * mm, "end": v(-2.36, 146) * mm});
            skLineSegment(sketch, "E761", {"start": v(1.5, 144) * mm, "end": v(2.36, 146) * mm});
            skLineSegment(sketch, "E762", {"start": v(-2.36, 146) * mm, "end": v(-1.5, 144) * mm});
            skSolve(sketch);
        }
        {
            var Q0;
            Q0=qSketchRegion(id+"F9",true);
            extrude(context, id + "F10", {"entities" : qUnion([Q0]), "operationType" : NewBodyOperationType.REMOVE, "endBound" : BoundingType.SYMMETRIC, "depth" : 25 * mm});
        }
        {
            var Q0;
            Q0=qCreatedBy(makeId("Right.planeOp"),FACE);
            var sketch = newSketch(context, id + "F11", { "sketchPlane" : qUnion([Q0])});
            skLineSegment(sketch, "E763", {"start": v(0, 0) * mm, "end": v(4, 0) * mm, "construction": true});
            skLineSegment(sketch, "E764", {"start": v(7.5, 3) * mm, "end": v(11, 3) * mm, "construction": true});
            skLineSegment(sketch, "E765", {"start": v(11, 3) * mm, "end": v(11, 1.5) * mm, "construction": true});
            skLineSegment(sketch, "E766", {"start": v(11, 1.5) * mm, "end": v(11, -1.5) * mm, "construction": true});
            skLineSegment(sketch, "E767", {"start": v(11, -1.5) * mm, "end": v(11, -3) * mm, "construction": true});
            skLineSegment(sketch, "E768", {"start": v(11, -3) * mm, "end": v(7.5, -3) * mm, "construction": true});
            skLineSegment(sketch, "E769", {"start": v(11, 1.5) * mm, "end": v(11, -1.5) * mm});
            skLineSegment(sketch, "E770", {"start": v(4, 0) * mm, "end": v(14, 0) * mm, "construction": true});
            skPoint(sketch, "E770.endSnap0", {"position": v(11, 0) * mm});
            skLineSegment(sketch, "E771", {"start": v(14, 0) * mm, "end": v(14, 3) * mm, "construction": true});
            skLineSegment(sketch, "E772", {"start": v(14, -3) * mm, "end": v(14, -1.5) * mm, "construction": true});
            skLineSegment(sketch, "E773", {"start": v(14, -1.5) * mm, "end": v(14, 1.5) * mm, "construction": true});
            skLineSegment(sketch, "E774", {"start": v(14, 1.5) * mm, "end": v(14, 3) * mm, "construction": true});
            skLineSegment(sketch, "E775", {"start": v(14, 3) * mm, "end": v(17.5, 3) * mm, "construction": true});
            skLineSegment(sketch, "E776", {"start": v(17.5, 3) * mm, "end": v(21, 3) * mm, "construction": true});
            skLineSegment(sketch, "E777", {"start": v(21, 3) * mm, "end": v(21, 1.5) * mm, "construction": true});
            skLineSegment(sketch, "E778", {"start": v(21, 1.5) * mm, "end": v(21, -1.5) * mm, "construction": true});
            skLineSegment(sketch, "E779", {"start": v(21, -1.5) * mm, "end": v(21, -3) * mm, "construction": true});
            skLineSegment(sketch, "E780", {"start": v(21, -3) * mm, "end": v(17.5, -3) * mm, "construction": true});
            skLineSegment(sketch, "E781", {"start": v(17.5, -3) * mm, "end": v(14, -3) * mm, "construction": true});
            skLineSegment(sketch, "E782", {"start": v(21, -1.5) * mm, "end": v(17.5, -3) * mm});
            skLineSegment(sketch, "E783", {"start": v(17.5, -3) * mm, "end": v(14, -1.5) * mm});
            skLineSegment(sketch, "E784", {"start": v(14, -1.5) * mm, "end": v(14, 1.5) * mm});
            skLineSegment(sketch, "E785", {"start": v(14, 1.5) * mm, "end": v(17.5, 3) * mm});
            skLineSegment(sketch, "E786", {"start": v(17.5, 3) * mm, "end": v(21, 1.5) * mm});
            skLineSegment(sketch, "E787", {"start": v(21, 1.5) * mm, "end": v(21, -1.5) * mm});
            skLineSegment(sketch, "E788", {"start": v(14, 0) * mm, "end": v(24, 0) * mm, "construction": true});
            skLineSegment(sketch, "E789", {"start": v(24, 0) * mm, "end": v(24, 3) * mm, "construction": true});
            skLineSegment(sketch, "E790", {"start": v(24, -3) * mm, "end": v(24, -1.5) * mm, "construction": true});
            skLineSegment(sketch, "E791", {"start": v(24, -1.5) * mm, "end": v(24, 1.5) * mm, "construction": true});
            skLineSegment(sketch, "E792", {"start": v(24, 1.5) * mm, "end": v(24, 3) * mm, "construction": true});
            skLineSegment(sketch, "E793", {"start": v(24, 3) * mm, "end": v(27.5, 3) * mm, "construction": true});
            skLineSegment(sketch, "E794", {"start": v(27.5, 3) * mm, "end": v(31, 3) * mm, "construction": true});
            skLineSegment(sketch, "E795", {"start": v(31, 3) * mm, "end": v(31, 1.5) * mm, "construction": true});
            skLineSegment(sketch, "E796", {"start": v(31, 1.5) * mm, "end": v(31, -1.5) * mm, "construction": true});
            skLineSegment(sketch, "E797", {"start": v(31, -1.5) * mm, "end": v(31, -3) * mm, "construction": true});
            skLineSegment(sketch, "E798", {"start": v(31, -3) * mm, "end": v(27.5, -3) * mm, "construction": true});
            skLineSegment(sketch, "E799", {"start": v(27.5, -3) * mm, "end": v(24, -3) * mm, "construction": true});
            skLineSegment(sketch, "E800", {"start": v(31, -1.5) * mm, "end": v(27.5, -3) * mm});
            skLineSegment(sketch, "E801", {"start": v(27.5, -3) * mm, "end": v(24, -1.5) * mm});
            skLineSegment(sketch, "E802", {"start": v(24, -1.5) * mm, "end": v(24, 1.5) * mm});
            skLineSegment(sketch, "E803", {"start": v(24, 1.5) * mm, "end": v(27.5, 3) * mm});
            skLineSegment(sketch, "E804", {"start": v(27.5, 3) * mm, "end": v(31, 1.5) * mm});
            skLineSegment(sketch, "E805", {"start": v(31, 1.5) * mm, "end": v(31, -1.5) * mm});
            skLineSegment(sketch, "E806", {"start": v(24, 0) * mm, "end": v(34, 0) * mm, "construction": true});
            skLineSegment(sketch, "E807", {"start": v(34, 0) * mm, "end": v(34, 3) * mm, "construction": true});
            skLineSegment(sketch, "E808", {"start": v(34, -3) * mm, "end": v(34, -1.5) * mm, "construction": true});
            skLineSegment(sketch, "E809", {"start": v(34, -1.5) * mm, "end": v(34, 1.5) * mm, "construction": true});
            skLineSegment(sketch, "E810", {"start": v(34, 1.5) * mm, "end": v(34, 3) * mm, "construction": true});
            skLineSegment(sketch, "E811", {"start": v(34, 3) * mm, "end": v(37.5, 3) * mm, "construction": true});
            skLineSegment(sketch, "E812", {"start": v(37.5, 3) * mm, "end": v(41, 3) * mm, "construction": true});
            skLineSegment(sketch, "E813", {"start": v(41, 3) * mm, "end": v(41, 1.5) * mm, "construction": true});
            skLineSegment(sketch, "E814", {"start": v(41, 1.5) * mm, "end": v(41, -1.5) * mm, "construction": true});
            skLineSegment(sketch, "E815", {"start": v(41, -1.5) * mm, "end": v(41, -3) * mm, "construction": true});
            skLineSegment(sketch, "E816", {"start": v(41, -3) * mm, "end": v(37.5, -3) * mm, "construction": true});
            skLineSegment(sketch, "E817", {"start": v(37.5, -3) * mm, "end": v(34, -3) * mm, "construction": true});
            skLineSegment(sketch, "E818", {"start": v(41, -1.5) * mm, "end": v(37.5, -3) * mm});
            skLineSegment(sketch, "E819", {"start": v(37.5, -3) * mm, "end": v(34, -1.5) * mm});
            skLineSegment(sketch, "E820", {"start": v(34, -1.5) * mm, "end": v(34, 1.5) * mm});
            skLineSegment(sketch, "E821", {"start": v(34, 1.5) * mm, "end": v(37.5, 3) * mm});
            skLineSegment(sketch, "E822", {"start": v(37.5, 3) * mm, "end": v(41, 1.5) * mm});
            skLineSegment(sketch, "E823", {"start": v(41, 1.5) * mm, "end": v(41, -1.5) * mm});
            skLineSegment(sketch, "E824", {"start": v(34, 0) * mm, "end": v(44, 0) * mm, "construction": true});
            skLineSegment(sketch, "E825", {"start": v(44, 0) * mm, "end": v(44, 3) * mm, "construction": true});
            skLineSegment(sketch, "E826", {"start": v(44, -3) * mm, "end": v(44, -1.5) * mm, "construction": true});
            skLineSegment(sketch, "E827", {"start": v(44, -1.5) * mm, "end": v(44, 1.5) * mm, "construction": true});
            skLineSegment(sketch, "E828", {"start": v(44, 1.5) * mm, "end": v(44, 3) * mm, "construction": true});
            skLineSegment(sketch, "E829", {"start": v(44, 3) * mm, "end": v(47.5, 3) * mm, "construction": true});
            skLineSegment(sketch, "E830", {"start": v(47.5, 3) * mm, "end": v(51, 3) * mm, "construction": true});
            skLineSegment(sketch, "E831", {"start": v(51, 3) * mm, "end": v(51, 1.5) * mm, "construction": true});
            skLineSegment(sketch, "E832", {"start": v(51, 1.5) * mm, "end": v(51, -1.5) * mm, "construction": true});
            skLineSegment(sketch, "E833", {"start": v(51, -1.5) * mm, "end": v(51, -3) * mm, "construction": true});
            skLineSegment(sketch, "E834", {"start": v(51, -3) * mm, "end": v(47.5, -3) * mm, "construction": true});
            skLineSegment(sketch, "E835", {"start": v(47.5, -3) * mm, "end": v(44, -3) * mm, "construction": true});
            skLineSegment(sketch, "E836", {"start": v(51, -1.5) * mm, "end": v(47.5, -3) * mm});
            skLineSegment(sketch, "E837", {"start": v(47.5, -3) * mm, "end": v(44, -1.5) * mm});
            skLineSegment(sketch, "E838", {"start": v(44, -1.5) * mm, "end": v(44, 1.5) * mm});
            skLineSegment(sketch, "E839", {"start": v(44, 1.5) * mm, "end": v(47.5, 3) * mm});
            skLineSegment(sketch, "E840", {"start": v(47.5, 3) * mm, "end": v(51, 1.5) * mm});
            skLineSegment(sketch, "E841", {"start": v(51, 1.5) * mm, "end": v(51, -1.5) * mm});
            skLineSegment(sketch, "E842", {"start": v(44, 0) * mm, "end": v(54, 0) * mm, "construction": true});
            skLineSegment(sketch, "E843", {"start": v(54, 0) * mm, "end": v(54, 3) * mm, "construction": true});
            skLineSegment(sketch, "E844", {"start": v(54, -3) * mm, "end": v(54, -1.5) * mm, "construction": true});
            skLineSegment(sketch, "E845", {"start": v(54, -1.5) * mm, "end": v(54, 1.5) * mm, "construction": true});
            skLineSegment(sketch, "E846", {"start": v(54, 1.5) * mm, "end": v(54, 3) * mm, "construction": true});
            skLineSegment(sketch, "E847", {"start": v(54, 3) * mm, "end": v(57.5, 3) * mm, "construction": true});
            skLineSegment(sketch, "E848", {"start": v(57.5, 3) * mm, "end": v(61, 3) * mm, "construction": true});
            skLineSegment(sketch, "E849", {"start": v(61, 3) * mm, "end": v(61, 1.5) * mm, "construction": true});
            skLineSegment(sketch, "E850", {"start": v(61, 1.5) * mm, "end": v(61, -1.5) * mm, "construction": true});
            skLineSegment(sketch, "E851", {"start": v(61, -1.5) * mm, "end": v(61, -3) * mm, "construction": true});
            skLineSegment(sketch, "E852", {"start": v(61, -3) * mm, "end": v(57.5, -3) * mm, "construction": true});
            skLineSegment(sketch, "E853", {"start": v(57.5, -3) * mm, "end": v(54, -3) * mm, "construction": true});
            skLineSegment(sketch, "E854", {"start": v(61, -1.5) * mm, "end": v(57.5, -3) * mm});
            skLineSegment(sketch, "E855", {"start": v(57.5, -3) * mm, "end": v(54, -1.5) * mm});
            skLineSegment(sketch, "E856", {"start": v(54, -1.5) * mm, "end": v(54, 1.5) * mm});
            skLineSegment(sketch, "E857", {"start": v(54, 1.5) * mm, "end": v(57.5, 3) * mm});
            skLineSegment(sketch, "E858", {"start": v(57.5, 3) * mm, "end": v(61, 1.5) * mm});
            skLineSegment(sketch, "E859", {"start": v(61, 1.5) * mm, "end": v(61, -1.5) * mm});
            skLineSegment(sketch, "E860", {"start": v(54, 0) * mm, "end": v(64, 0) * mm, "construction": true});
            skLineSegment(sketch, "E861", {"start": v(64, 0) * mm, "end": v(64, 3) * mm, "construction": true});
            skLineSegment(sketch, "E862", {"start": v(64, -3) * mm, "end": v(64, -1.5) * mm, "construction": true});
            skLineSegment(sketch, "E863", {"start": v(64, -1.5) * mm, "end": v(64, 1.5) * mm, "construction": true});
            skLineSegment(sketch, "E864", {"start": v(64, 1.5) * mm, "end": v(64, 3) * mm, "construction": true});
            skLineSegment(sketch, "E865", {"start": v(64, 3) * mm, "end": v(67.5, 3) * mm, "construction": true});
            skLineSegment(sketch, "E866", {"start": v(67.5, 3) * mm, "end": v(71, 3) * mm, "construction": true});
            skLineSegment(sketch, "E867", {"start": v(71, 3) * mm, "end": v(71, 1.5) * mm, "construction": true});
            skLineSegment(sketch, "E868", {"start": v(71, 1.5) * mm, "end": v(71, -1.5) * mm, "construction": true});
            skLineSegment(sketch, "E869", {"start": v(71, -1.5) * mm, "end": v(71, -3) * mm, "construction": true});
            skLineSegment(sketch, "E870", {"start": v(71, -3) * mm, "end": v(67.5, -3) * mm, "construction": true});
            skLineSegment(sketch, "E871", {"start": v(67.5, -3) * mm, "end": v(64, -3) * mm, "construction": true});
            skLineSegment(sketch, "E872", {"start": v(71, -1.5) * mm, "end": v(67.5, -3) * mm});
            skLineSegment(sketch, "E873", {"start": v(67.5, -3) * mm, "end": v(64, -1.5) * mm});
            skLineSegment(sketch, "E874", {"start": v(64, -1.5) * mm, "end": v(64, 1.5) * mm});
            skLineSegment(sketch, "E875", {"start": v(64, 1.5) * mm, "end": v(67.5, 3) * mm});
            skLineSegment(sketch, "E876", {"start": v(67.5, 3) * mm, "end": v(71, 1.5) * mm});
            skLineSegment(sketch, "E877", {"start": v(71, 1.5) * mm, "end": v(71, -1.5) * mm});
            skLineSegment(sketch, "E878", {"start": v(64, 0) * mm, "end": v(74, 0) * mm, "construction": true});
            skLineSegment(sketch, "E879", {"start": v(74, 0) * mm, "end": v(74, 3) * mm, "construction": true});
            skLineSegment(sketch, "E880", {"start": v(74, -3) * mm, "end": v(74, -1.5) * mm, "construction": true});
            skLineSegment(sketch, "E881", {"start": v(74, -1.5) * mm, "end": v(74, 1.5) * mm, "construction": true});
            skLineSegment(sketch, "E882", {"start": v(74, 1.5) * mm, "end": v(74, 3) * mm, "construction": true});
            skLineSegment(sketch, "E883", {"start": v(74, 3) * mm, "end": v(77.5, 3) * mm, "construction": true});
            skLineSegment(sketch, "E884", {"start": v(77.5, 3) * mm, "end": v(81, 3) * mm, "construction": true});
            skLineSegment(sketch, "E885", {"start": v(81, 3) * mm, "end": v(81, 1.5) * mm, "construction": true});
            skLineSegment(sketch, "E886", {"start": v(81, 1.5) * mm, "end": v(81, -1.5) * mm, "construction": true});
            skLineSegment(sketch, "E887", {"start": v(81, -1.5) * mm, "end": v(81, -3) * mm, "construction": true});
            skLineSegment(sketch, "E888", {"start": v(81, -3) * mm, "end": v(77.5, -3) * mm, "construction": true});
            skLineSegment(sketch, "E889", {"start": v(77.5, -3) * mm, "end": v(74, -3) * mm, "construction": true});
            skLineSegment(sketch, "E890", {"start": v(81, -1.5) * mm, "end": v(77.5, -3) * mm});
            skLineSegment(sketch, "E891", {"start": v(77.5, -3) * mm, "end": v(74, -1.5) * mm});
            skLineSegment(sketch, "E892", {"start": v(74, -1.5) * mm, "end": v(74, 1.5) * mm});
            skLineSegment(sketch, "E893", {"start": v(74, 1.5) * mm, "end": v(77.5, 3) * mm});
            skLineSegment(sketch, "E894", {"start": v(77.5, 3) * mm, "end": v(81, 1.5) * mm});
            skLineSegment(sketch, "E895", {"start": v(81, 1.5) * mm, "end": v(81, -1.5) * mm});
            skLineSegment(sketch, "E896", {"start": v(74, 0) * mm, "end": v(84, 0) * mm, "construction": true});
            skLineSegment(sketch, "E897", {"start": v(84, 0) * mm, "end": v(84, 3) * mm, "construction": true});
            skLineSegment(sketch, "E898", {"start": v(84, -3) * mm, "end": v(84, -1.5) * mm, "construction": true});
            skLineSegment(sketch, "E899", {"start": v(84, -1.5) * mm, "end": v(84, 1.5) * mm, "construction": true});
            skLineSegment(sketch, "E900", {"start": v(84, 1.5) * mm, "end": v(84, 3) * mm, "construction": true});
            skLineSegment(sketch, "E901", {"start": v(84, 3) * mm, "end": v(87.5, 3) * mm, "construction": true});
            skLineSegment(sketch, "E902", {"start": v(87.5, 3) * mm, "end": v(91, 3) * mm, "construction": true});
            skLineSegment(sketch, "E903", {"start": v(91, 3) * mm, "end": v(91, 1.5) * mm, "construction": true});
            skLineSegment(sketch, "E904", {"start": v(91, 1.5) * mm, "end": v(91, -1.5) * mm, "construction": true});
            skLineSegment(sketch, "E905", {"start": v(91, -1.5) * mm, "end": v(91, -3) * mm, "construction": true});
            skLineSegment(sketch, "E906", {"start": v(91, -3) * mm, "end": v(87.5, -3) * mm, "construction": true});
            skLineSegment(sketch, "E907", {"start": v(87.5, -3) * mm, "end": v(84, -3) * mm, "construction": true});
            skLineSegment(sketch, "E908", {"start": v(91, -1.5) * mm, "end": v(87.5, -3) * mm});
            skLineSegment(sketch, "E909", {"start": v(87.5, -3) * mm, "end": v(84, -1.5) * mm});
            skLineSegment(sketch, "E910", {"start": v(84, -1.5) * mm, "end": v(84, 1.5) * mm});
            skLineSegment(sketch, "E911", {"start": v(84, 1.5) * mm, "end": v(87.5, 3) * mm});
            skLineSegment(sketch, "E912", {"start": v(87.5, 3) * mm, "end": v(91, 1.5) * mm});
            skLineSegment(sketch, "E913", {"start": v(91, 1.5) * mm, "end": v(91, -1.5) * mm});
            skLineSegment(sketch, "E914", {"start": v(84, 0) * mm, "end": v(94, 0) * mm, "construction": true});
            skLineSegment(sketch, "E915", {"start": v(94, 0) * mm, "end": v(94, 3) * mm, "construction": true});
            skLineSegment(sketch, "E916", {"start": v(94, -3) * mm, "end": v(94, -1.5) * mm, "construction": true});
            skLineSegment(sketch, "E917", {"start": v(94, -1.5) * mm, "end": v(94, 1.5) * mm, "construction": true});
            skLineSegment(sketch, "E918", {"start": v(94, 1.5) * mm, "end": v(94, 3) * mm, "construction": true});
            skLineSegment(sketch, "E919", {"start": v(94, 3) * mm, "end": v(97.5, 3) * mm, "construction": true});
            skLineSegment(sketch, "E920", {"start": v(97.5, 3) * mm, "end": v(101, 3) * mm, "construction": true});
            skLineSegment(sketch, "E921", {"start": v(101, 3) * mm, "end": v(101, 1.5) * mm, "construction": true});
            skLineSegment(sketch, "E922", {"start": v(101, 1.5) * mm, "end": v(101, -1.5) * mm, "construction": true});
            skLineSegment(sketch, "E923", {"start": v(101, -1.5) * mm, "end": v(101, -3) * mm, "construction": true});
            skLineSegment(sketch, "E924", {"start": v(101, -3) * mm, "end": v(97.5, -3) * mm, "construction": true});
            skLineSegment(sketch, "E925", {"start": v(97.5, -3) * mm, "end": v(94, -3) * mm, "construction": true});
            skLineSegment(sketch, "E926", {"start": v(101, -1.5) * mm, "end": v(97.5, -3) * mm});
            skLineSegment(sketch, "E927", {"start": v(97.5, -3) * mm, "end": v(94, -1.5) * mm});
            skLineSegment(sketch, "E928", {"start": v(94, -1.5) * mm, "end": v(94, 1.5) * mm});
            skLineSegment(sketch, "E929", {"start": v(94, 1.5) * mm, "end": v(97.5, 3) * mm});
            skLineSegment(sketch, "E930", {"start": v(97.5, 3) * mm, "end": v(101, 1.5) * mm});
            skLineSegment(sketch, "E931", {"start": v(101, 1.5) * mm, "end": v(101, -1.5) * mm});
            skLineSegment(sketch, "E932", {"start": v(94, 0) * mm, "end": v(104, 0) * mm, "construction": true});
            skLineSegment(sketch, "E933", {"start": v(104, 0) * mm, "end": v(104, 3) * mm, "construction": true});
            skLineSegment(sketch, "E934", {"start": v(104, -3) * mm, "end": v(104, -1.5) * mm, "construction": true});
            skLineSegment(sketch, "E935", {"start": v(104, -1.5) * mm, "end": v(104, 1.5) * mm, "construction": true});
            skLineSegment(sketch, "E936", {"start": v(104, 1.5) * mm, "end": v(104, 3) * mm, "construction": true});
            skLineSegment(sketch, "E937", {"start": v(104, 3) * mm, "end": v(107.5, 3) * mm, "construction": true});
            skLineSegment(sketch, "E938", {"start": v(107.5, 3) * mm, "end": v(111, 3) * mm, "construction": true});
            skLineSegment(sketch, "E939", {"start": v(111, 3) * mm, "end": v(111, 1.5) * mm, "construction": true});
            skLineSegment(sketch, "E940", {"start": v(111, 1.5) * mm, "end": v(111, -1.5) * mm, "construction": true});
            skLineSegment(sketch, "E941", {"start": v(111, -1.5) * mm, "end": v(111, -3) * mm, "construction": true});
            skLineSegment(sketch, "E942", {"start": v(111, -3) * mm, "end": v(107.5, -3) * mm, "construction": true});
            skLineSegment(sketch, "E943", {"start": v(107.5, -3) * mm, "end": v(104, -3) * mm, "construction": true});
            skLineSegment(sketch, "E944", {"start": v(111, -1.5) * mm, "end": v(107.5, -3) * mm});
            skLineSegment(sketch, "E945", {"start": v(107.5, -3) * mm, "end": v(104, -1.5) * mm});
            skLineSegment(sketch, "E946", {"start": v(104, -1.5) * mm, "end": v(104, 1.5) * mm});
            skLineSegment(sketch, "E947", {"start": v(104, 1.5) * mm, "end": v(107.5, 3) * mm});
            skLineSegment(sketch, "E948", {"start": v(107.5, 3) * mm, "end": v(111, 1.5) * mm});
            skLineSegment(sketch, "E949", {"start": v(111, 1.5) * mm, "end": v(111, -1.5) * mm});
            skLineSegment(sketch, "E950", {"start": v(104, 0) * mm, "end": v(114, 0) * mm, "construction": true});
            skLineSegment(sketch, "E951", {"start": v(114, 0) * mm, "end": v(114, 3) * mm, "construction": true});
            skLineSegment(sketch, "E952", {"start": v(114, -3) * mm, "end": v(114, -1.5) * mm, "construction": true});
            skLineSegment(sketch, "E953", {"start": v(114, -1.5) * mm, "end": v(114, 1.5) * mm, "construction": true});
            skLineSegment(sketch, "E954", {"start": v(114, 1.5) * mm, "end": v(114, 3) * mm, "construction": true});
            skLineSegment(sketch, "E955", {"start": v(114, 3) * mm, "end": v(117.5, 3) * mm, "construction": true});
            skLineSegment(sketch, "E956", {"start": v(117.5, 3) * mm, "end": v(121, 3) * mm, "construction": true});
            skLineSegment(sketch, "E957", {"start": v(121, 3) * mm, "end": v(121, 1.5) * mm, "construction": true});
            skLineSegment(sketch, "E958", {"start": v(121, 1.5) * mm, "end": v(121, -1.5) * mm, "construction": true});
            skLineSegment(sketch, "E959", {"start": v(121, -1.5) * mm, "end": v(121, -3) * mm, "construction": true});
            skLineSegment(sketch, "E960", {"start": v(121, -3) * mm, "end": v(117.5, -3) * mm, "construction": true});
            skLineSegment(sketch, "E961", {"start": v(117.5, -3) * mm, "end": v(114, -3) * mm, "construction": true});
            skLineSegment(sketch, "E962", {"start": v(121, -1.5) * mm, "end": v(117.5, -3) * mm});
            skLineSegment(sketch, "E963", {"start": v(117.5, -3) * mm, "end": v(114, -1.5) * mm});
            skLineSegment(sketch, "E964", {"start": v(114, -1.5) * mm, "end": v(114, 1.5) * mm});
            skLineSegment(sketch, "E965", {"start": v(114, 1.5) * mm, "end": v(117.5, 3) * mm});
            skLineSegment(sketch, "E966", {"start": v(117.5, 3) * mm, "end": v(121, 1.5) * mm});
            skLineSegment(sketch, "E967", {"start": v(121, 1.5) * mm, "end": v(121, -1.5) * mm});
            skLineSegment(sketch, "E968", {"start": v(114, 0) * mm, "end": v(124, 0) * mm, "construction": true});
            skLineSegment(sketch, "E969", {"start": v(124, 0) * mm, "end": v(124, 3) * mm, "construction": true});
            skLineSegment(sketch, "E970", {"start": v(124, -3) * mm, "end": v(124, -1.5) * mm, "construction": true});
            skLineSegment(sketch, "E971", {"start": v(124, -1.5) * mm, "end": v(124, 1.5) * mm, "construction": true});
            skLineSegment(sketch, "E972", {"start": v(124, 1.5) * mm, "end": v(124, 3) * mm, "construction": true});
            skLineSegment(sketch, "E973", {"start": v(124, 3) * mm, "end": v(127.5, 3) * mm, "construction": true});
            skLineSegment(sketch, "E974", {"start": v(127.5, 3) * mm, "end": v(131, 3) * mm, "construction": true});
            skLineSegment(sketch, "E975", {"start": v(131, 3) * mm, "end": v(131, 1.5) * mm, "construction": true});
            skLineSegment(sketch, "E976", {"start": v(131, 1.5) * mm, "end": v(131, -1.5) * mm, "construction": true});
            skLineSegment(sketch, "E977", {"start": v(131, -1.5) * mm, "end": v(131, -3) * mm, "construction": true});
            skLineSegment(sketch, "E978", {"start": v(131, -3) * mm, "end": v(127.5, -3) * mm, "construction": true});
            skLineSegment(sketch, "E979", {"start": v(127.5, -3) * mm, "end": v(124, -3) * mm, "construction": true});
            skLineSegment(sketch, "E980", {"start": v(131, -1.5) * mm, "end": v(127.5, -3) * mm});
            skLineSegment(sketch, "E981", {"start": v(127.5, -3) * mm, "end": v(124, -1.5) * mm});
            skLineSegment(sketch, "E982", {"start": v(124, -1.5) * mm, "end": v(124, 1.5) * mm});
            skLineSegment(sketch, "E983", {"start": v(124, 1.5) * mm, "end": v(127.5, 3) * mm});
            skLineSegment(sketch, "E984", {"start": v(127.5, 3) * mm, "end": v(131, 1.5) * mm});
            skLineSegment(sketch, "E985", {"start": v(131, 1.5) * mm, "end": v(131, -1.5) * mm});
            skLineSegment(sketch, "E986", {"start": v(124, 0) * mm, "end": v(134, 0) * mm, "construction": true});
            skLineSegment(sketch, "E987", {"start": v(134, 0) * mm, "end": v(134, 3) * mm, "construction": true});
            skLineSegment(sketch, "E988", {"start": v(134, -3) * mm, "end": v(134, -1.5) * mm, "construction": true});
            skLineSegment(sketch, "E989", {"start": v(134, -1.5) * mm, "end": v(134, 1.5) * mm, "construction": true});
            skLineSegment(sketch, "E990", {"start": v(134, 1.5) * mm, "end": v(134, 3) * mm, "construction": true});
            skLineSegment(sketch, "E991", {"start": v(134, 3) * mm, "end": v(137.5, 3) * mm, "construction": true});
            skLineSegment(sketch, "E992", {"start": v(137.5, 3) * mm, "end": v(141, 3) * mm, "construction": true});
            skLineSegment(sketch, "E993", {"start": v(141, 3) * mm, "end": v(141, 1.5) * mm, "construction": true});
            skLineSegment(sketch, "E994", {"start": v(141, 1.5) * mm, "end": v(141, -1.5) * mm, "construction": true});
            skLineSegment(sketch, "E995", {"start": v(141, -1.5) * mm, "end": v(141, -3) * mm, "construction": true});
            skLineSegment(sketch, "E996", {"start": v(141, -3) * mm, "end": v(137.5, -3) * mm, "construction": true});
            skLineSegment(sketch, "E997", {"start": v(137.5, -3) * mm, "end": v(134, -3) * mm, "construction": true});
            skLineSegment(sketch, "E998", {"start": v(141, -1.5) * mm, "end": v(137.5, -3) * mm});
            skLineSegment(sketch, "E999", {"start": v(137.5, -3) * mm, "end": v(134, -1.5) * mm});
            skLineSegment(sketch, "E1000", {"start": v(134, -1.5) * mm, "end": v(134, 1.5) * mm});
            skLineSegment(sketch, "E1001", {"start": v(134, 1.5) * mm, "end": v(137.5, 3) * mm});
            skLineSegment(sketch, "E1002", {"start": v(137.5, 3) * mm, "end": v(141, 1.5) * mm});
            skLineSegment(sketch, "E1003", {"start": v(141, 1.5) * mm, "end": v(141, -1.5) * mm});
            skLineSegment(sketch, "E1004", {"start": v(134, 0) * mm, "end": v(144, 0) * mm, "construction": true});
            skLineSegment(sketch, "E1005", {"start": v(144, 0) * mm, "end": v(144, 3) * mm, "construction": true});
            skLineSegment(sketch, "E1006", {"start": v(144, -3) * mm, "end": v(144, -1.5) * mm, "construction": true});
            skLineSegment(sketch, "E1007", {"start": v(144, -1.5) * mm, "end": v(144, 1.5) * mm, "construction": true});
            skLineSegment(sketch, "E1008", {"start": v(144, 1.5) * mm, "end": v(144, 3) * mm, "construction": true});
            skLineSegment(sketch, "E1009", {"start": v(144, -1.5) * mm, "end": v(144, 1.5) * mm});
            skLineSegment(sketch, "E1010", {"start": v(11, -1.5) * mm, "end": v(9, -1.5) * mm, "construction": true});
            skLineSegment(sketch, "E1011", {"start": v(9, -1.5) * mm, "end": v(9, -2.36) * mm});
            skLineSegment(sketch, "E1012", {"start": v(9, -1.5) * mm, "end": v(9, 2.36) * mm});
            skLineSegment(sketch, "E1013", {"start": v(11, -1.5) * mm, "end": v(9, -2.36) * mm});
            skLineSegment(sketch, "E1014", {"start": v(11, 1.5) * mm, "end": v(9, 2.36) * mm});
            skLineSegment(sketch, "E1015", {"start": v(144, -1.5) * mm, "end": v(146, -1.5) * mm, "construction": true});
            skLineSegment(sketch, "E1016", {"start": v(146, -1.5) * mm, "end": v(146, -2.36) * mm});
            skLineSegment(sketch, "E1017", {"start": v(146, -1.5) * mm, "end": v(146, 2.36) * mm});
            skLineSegment(sketch, "E1018", {"start": v(144, -1.5) * mm, "end": v(146, -2.36) * mm});
            skLineSegment(sketch, "E1019", {"start": v(146, 2.36) * mm, "end": v(144, 1.5) * mm});
            skSolve(sketch);
        }
        {
            var Q0;
            Q0=qSketchRegion(id+"F11",true);
            extrude(context, id + "F12", {"entities" : qUnion([Q0]), "operationType" : NewBodyOperationType.REMOVE, "oppositeDirection" : true, "depth" : 25 * mm});
        }
        {
            var Q0;
            Q0=makeQuery(id+"F1.opExtrude","CAP_EDGE",EDGE,{"disambiguationData":[OSD([sQuery(id+"F0.wireOp",EDGE,"E0")])],"isStart":true});
            fillet(context, id + "F13", {"entities" : qUnion([Q0]), "radius" : 1.5 * mm, "tangentPropagation" : true, "allowEdgeOverflow" : false});
        }
        {
            var Q0;
            Q0=makeQuery(id+"F5.boolean.opBoolean","INTERSECT",EDGE,{"disambiguationData":[OD(0.0)],"derivedFrom":[makeQuery(id+"F1.opExtrude","SWEPT_FACE",FACE,{"disambiguationData":[OSD([sQuery(id+"F0.wireOp",EDGE,"E0")])]}),makeQuery(id+"F5.opExtrude","SWEPT_FACE",FACE,{"disambiguationData":[OSD([sQuery(id+"F4.wireOp",EDGE,"E231")])]})]});
            var Q1;
            Q1=makeQuery(id+"F5.boolean.opBoolean","INTERSECT",EDGE,{"disambiguationData":[OD(0.0)],"derivedFrom":[makeQuery(id+"F1.opExtrude","SWEPT_FACE",FACE,{"disambiguationData":[OSD([sQuery(id+"F0.wireOp",EDGE,"E0")])]}),makeQuery(id+"F5.opExtrude","SWEPT_FACE",FACE,{"disambiguationData":[OSD([sQuery(id+"F4.wireOp",EDGE,"E232")])]})]});
            var Q2;
            Q2=makeQuery(id+"F5.boolean.opBoolean","INTERSECT",EDGE,{"disambiguationData":[OD(0.0)],"derivedFrom":[makeQuery(id+"F1.opExtrude","SWEPT_FACE",FACE,{"disambiguationData":[OSD([sQuery(id+"F0.wireOp",EDGE,"E0")])]}),makeQuery(id+"F5.opExtrude","SWEPT_FACE",FACE,{"disambiguationData":[OSD([sQuery(id+"F4.wireOp",EDGE,"E233")])]})]});
            var Q3;
            Q3=makeQuery(id+"F5.boolean.opBoolean","INTERSECT",EDGE,{"disambiguationData":[OD(0.0)],"derivedFrom":[makeQuery(id+"F1.opExtrude","SWEPT_FACE",FACE,{"disambiguationData":[OSD([sQuery(id+"F0.wireOp",EDGE,"E0")])]}),makeQuery(id+"F5.opExtrude","SWEPT_FACE",FACE,{"disambiguationData":[OSD([sQuery(id+"F4.wireOp",EDGE,"E234")])]})]});
            var Q4;
            Q4=makeQuery(id+"F5.boolean.opBoolean","INTERSECT",EDGE,{"disambiguationData":[OD(0.0)],"derivedFrom":[makeQuery(id+"F1.opExtrude","SWEPT_FACE",FACE,{"disambiguationData":[OSD([sQuery(id+"F0.wireOp",EDGE,"E0")])]}),makeQuery(id+"F5.opExtrude","SWEPT_FACE",FACE,{"disambiguationData":[OSD([sQuery(id+"F4.wireOp",EDGE,"E235")])]})]});
            var Q5;
            Q5=makeQuery(id+"F5.boolean.opBoolean","INTERSECT",EDGE,{"disambiguationData":[OD(0.0)],"derivedFrom":[makeQuery(id+"F1.opExtrude","SWEPT_FACE",FACE,{"disambiguationData":[OSD([sQuery(id+"F0.wireOp",EDGE,"E0")])]}),makeQuery(id+"F5.opExtrude","SWEPT_FACE",FACE,{"disambiguationData":[OSD([sQuery(id+"F4.wireOp",EDGE,"E230")])]})]});
            var Q6;
            Q6=makeQuery(id+"F5.boolean.opBoolean","INTERSECT",EDGE,{"disambiguationData":[OD(0.0)],"derivedFrom":[makeQuery(id+"F1.opExtrude","SWEPT_FACE",FACE,{"disambiguationData":[OSD([sQuery(id+"F0.wireOp",EDGE,"E0")])]}),makeQuery(id+"F5.opExtrude","SWEPT_FACE",FACE,{"disambiguationData":[OSD([sQuery(id+"F4.wireOp",EDGE,"E212")])]})]});
            var Q7;
            Q7=makeQuery(id+"F5.boolean.opBoolean","INTERSECT",EDGE,{"disambiguationData":[OD(0.0)],"derivedFrom":[makeQuery(id+"F1.opExtrude","SWEPT_FACE",FACE,{"disambiguationData":[OSD([sQuery(id+"F0.wireOp",EDGE,"E0")])]}),makeQuery(id+"F5.opExtrude","SWEPT_FACE",FACE,{"disambiguationData":[OSD([sQuery(id+"F4.wireOp",EDGE,"E217")])]})]});
            var Q8;
            Q8=makeQuery(id+"F5.boolean.opBoolean","INTERSECT",EDGE,{"disambiguationData":[OD(0.0)],"derivedFrom":[makeQuery(id+"F1.opExtrude","SWEPT_FACE",FACE,{"disambiguationData":[OSD([sQuery(id+"F0.wireOp",EDGE,"E0")])]}),makeQuery(id+"F5.opExtrude","SWEPT_FACE",FACE,{"disambiguationData":[OSD([sQuery(id+"F4.wireOp",EDGE,"E216")])]})]});
            var Q9;
            Q9=makeQuery(id+"F5.boolean.opBoolean","INTERSECT",EDGE,{"disambiguationData":[OD(0.0)],"derivedFrom":[makeQuery(id+"F1.opExtrude","SWEPT_FACE",FACE,{"disambiguationData":[OSD([sQuery(id+"F0.wireOp",EDGE,"E0")])]}),makeQuery(id+"F5.opExtrude","SWEPT_FACE",FACE,{"disambiguationData":[OSD([sQuery(id+"F4.wireOp",EDGE,"E215")])]})]});
            var Q10;
            Q10=makeQuery(id+"F5.boolean.opBoolean","INTERSECT",EDGE,{"disambiguationData":[OD(0.0)],"derivedFrom":[makeQuery(id+"F1.opExtrude","SWEPT_FACE",FACE,{"disambiguationData":[OSD([sQuery(id+"F0.wireOp",EDGE,"E0")])]}),makeQuery(id+"F5.opExtrude","SWEPT_FACE",FACE,{"disambiguationData":[OSD([sQuery(id+"F4.wireOp",EDGE,"E214")])]})]});
            var Q11;
            Q11=makeQuery(id+"F5.boolean.opBoolean","INTERSECT",EDGE,{"disambiguationData":[OD(0.0)],"derivedFrom":[makeQuery(id+"F1.opExtrude","SWEPT_FACE",FACE,{"disambiguationData":[OSD([sQuery(id+"F0.wireOp",EDGE,"E0")])]}),makeQuery(id+"F5.opExtrude","SWEPT_FACE",FACE,{"disambiguationData":[OSD([sQuery(id+"F4.wireOp",EDGE,"E213")])]})]});
            var Q12;
            Q12=makeQuery(id+"F5.boolean.opBoolean","INTERSECT",EDGE,{"disambiguationData":[OD(0.0)],"derivedFrom":[makeQuery(id+"F1.opExtrude","SWEPT_FACE",FACE,{"disambiguationData":[OSD([sQuery(id+"F0.wireOp",EDGE,"E0")])]}),makeQuery(id+"F5.opExtrude","SWEPT_FACE",FACE,{"disambiguationData":[OSD([sQuery(id+"F4.wireOp",EDGE,"E194")])]})]});
            var Q13;
            Q13=makeQuery(id+"F5.boolean.opBoolean","INTERSECT",EDGE,{"disambiguationData":[OD(0.0)],"derivedFrom":[makeQuery(id+"F1.opExtrude","SWEPT_FACE",FACE,{"disambiguationData":[OSD([sQuery(id+"F0.wireOp",EDGE,"E0")])]}),makeQuery(id+"F5.opExtrude","SWEPT_FACE",FACE,{"disambiguationData":[OSD([sQuery(id+"F4.wireOp",EDGE,"E199")])]})]});
            var Q14;
            Q14=makeQuery(id+"F5.boolean.opBoolean","INTERSECT",EDGE,{"disambiguationData":[OD(0.0)],"derivedFrom":[makeQuery(id+"F1.opExtrude","SWEPT_FACE",FACE,{"disambiguationData":[OSD([sQuery(id+"F0.wireOp",EDGE,"E0")])]}),makeQuery(id+"F5.opExtrude","SWEPT_FACE",FACE,{"disambiguationData":[OSD([sQuery(id+"F4.wireOp",EDGE,"E198")])]})]});
            var Q15;
            Q15=makeQuery(id+"F5.boolean.opBoolean","INTERSECT",EDGE,{"disambiguationData":[OD(0.0)],"derivedFrom":[makeQuery(id+"F1.opExtrude","SWEPT_FACE",FACE,{"disambiguationData":[OSD([sQuery(id+"F0.wireOp",EDGE,"E0")])]}),makeQuery(id+"F5.opExtrude","SWEPT_FACE",FACE,{"disambiguationData":[OSD([sQuery(id+"F4.wireOp",EDGE,"E197")])]})]});
            var Q16;
            Q16=makeQuery(id+"F5.boolean.opBoolean","INTERSECT",EDGE,{"disambiguationData":[OD(0.0)],"derivedFrom":[makeQuery(id+"F1.opExtrude","SWEPT_FACE",FACE,{"disambiguationData":[OSD([sQuery(id+"F0.wireOp",EDGE,"E0")])]}),makeQuery(id+"F5.opExtrude","SWEPT_FACE",FACE,{"disambiguationData":[OSD([sQuery(id+"F4.wireOp",EDGE,"E196")])]})]});
            var Q17;
            Q17=makeQuery(id+"F5.boolean.opBoolean","INTERSECT",EDGE,{"disambiguationData":[OD(0.0)],"derivedFrom":[makeQuery(id+"F1.opExtrude","SWEPT_FACE",FACE,{"disambiguationData":[OSD([sQuery(id+"F0.wireOp",EDGE,"E0")])]}),makeQuery(id+"F5.opExtrude","SWEPT_FACE",FACE,{"disambiguationData":[OSD([sQuery(id+"F4.wireOp",EDGE,"E195")])]})]});
            var Q18;
            Q18=makeQuery(id+"F5.boolean.opBoolean","INTERSECT",EDGE,{"disambiguationData":[OD(0.0)],"derivedFrom":[makeQuery(id+"F1.opExtrude","SWEPT_FACE",FACE,{"disambiguationData":[OSD([sQuery(id+"F0.wireOp",EDGE,"E0")])]}),makeQuery(id+"F5.opExtrude","SWEPT_FACE",FACE,{"disambiguationData":[OSD([sQuery(id+"F4.wireOp",EDGE,"E181")])]})]});
            var Q19;
            Q19=makeQuery(id+"F5.boolean.opBoolean","INTERSECT",EDGE,{"disambiguationData":[OD(0.0)],"derivedFrom":[makeQuery(id+"F1.opExtrude","SWEPT_FACE",FACE,{"disambiguationData":[OSD([sQuery(id+"F0.wireOp",EDGE,"E0")])]}),makeQuery(id+"F5.opExtrude","SWEPT_FACE",FACE,{"disambiguationData":[OSD([sQuery(id+"F4.wireOp",EDGE,"E180")])]})]});
            var Q20;
            Q20=makeQuery(id+"F5.boolean.opBoolean","INTERSECT",EDGE,{"disambiguationData":[OD(0.0)],"derivedFrom":[makeQuery(id+"F1.opExtrude","SWEPT_FACE",FACE,{"disambiguationData":[OSD([sQuery(id+"F0.wireOp",EDGE,"E0")])]}),makeQuery(id+"F5.opExtrude","SWEPT_FACE",FACE,{"disambiguationData":[OSD([sQuery(id+"F4.wireOp",EDGE,"E179")])]})]});
            var Q21;
            Q21=makeQuery(id+"F5.boolean.opBoolean","INTERSECT",EDGE,{"disambiguationData":[OD(0.0)],"derivedFrom":[makeQuery(id+"F1.opExtrude","SWEPT_FACE",FACE,{"disambiguationData":[OSD([sQuery(id+"F0.wireOp",EDGE,"E0")])]}),makeQuery(id+"F5.opExtrude","SWEPT_FACE",FACE,{"disambiguationData":[OSD([sQuery(id+"F4.wireOp",EDGE,"E178")])]})]});
            var Q22;
            Q22=makeQuery(id+"F5.boolean.opBoolean","INTERSECT",EDGE,{"disambiguationData":[OD(0.0)],"derivedFrom":[makeQuery(id+"F1.opExtrude","SWEPT_FACE",FACE,{"disambiguationData":[OSD([sQuery(id+"F0.wireOp",EDGE,"E0")])]}),makeQuery(id+"F5.opExtrude","SWEPT_FACE",FACE,{"disambiguationData":[OSD([sQuery(id+"F4.wireOp",EDGE,"E177")])]})]});
            var Q23;
            Q23=makeQuery(id+"F5.boolean.opBoolean","INTERSECT",EDGE,{"disambiguationData":[OD(0.0)],"derivedFrom":[makeQuery(id+"F1.opExtrude","SWEPT_FACE",FACE,{"disambiguationData":[OSD([sQuery(id+"F0.wireOp",EDGE,"E0")])]}),makeQuery(id+"F5.opExtrude","SWEPT_FACE",FACE,{"disambiguationData":[OSD([sQuery(id+"F4.wireOp",EDGE,"E176")])]})]});
            var Q24;
            Q24=makeQuery(id+"F5.boolean.opBoolean","INTERSECT",EDGE,{"disambiguationData":[OD(0.0)],"derivedFrom":[makeQuery(id+"F1.opExtrude","SWEPT_FACE",FACE,{"disambiguationData":[OSD([sQuery(id+"F0.wireOp",EDGE,"E0")])]}),makeQuery(id+"F5.opExtrude","SWEPT_FACE",FACE,{"disambiguationData":[OSD([sQuery(id+"F4.wireOp",EDGE,"E158")])]})]});
            var Q25;
            Q25=makeQuery(id+"F5.boolean.opBoolean","INTERSECT",EDGE,{"disambiguationData":[OD(0.0)],"derivedFrom":[makeQuery(id+"F1.opExtrude","SWEPT_FACE",FACE,{"disambiguationData":[OSD([sQuery(id+"F0.wireOp",EDGE,"E0")])]}),makeQuery(id+"F5.opExtrude","SWEPT_FACE",FACE,{"disambiguationData":[OSD([sQuery(id+"F4.wireOp",EDGE,"E163")])]})]});
            var Q26;
            Q26=makeQuery(id+"F5.boolean.opBoolean","INTERSECT",EDGE,{"disambiguationData":[OD(0.0)],"derivedFrom":[makeQuery(id+"F1.opExtrude","SWEPT_FACE",FACE,{"disambiguationData":[OSD([sQuery(id+"F0.wireOp",EDGE,"E0")])]}),makeQuery(id+"F5.opExtrude","SWEPT_FACE",FACE,{"disambiguationData":[OSD([sQuery(id+"F4.wireOp",EDGE,"E162")])]})]});
            var Q27;
            Q27=makeQuery(id+"F5.boolean.opBoolean","INTERSECT",EDGE,{"disambiguationData":[OD(0.0)],"derivedFrom":[makeQuery(id+"F1.opExtrude","SWEPT_FACE",FACE,{"disambiguationData":[OSD([sQuery(id+"F0.wireOp",EDGE,"E0")])]}),makeQuery(id+"F5.opExtrude","SWEPT_FACE",FACE,{"disambiguationData":[OSD([sQuery(id+"F4.wireOp",EDGE,"E161")])]})]});
            var Q28;
            Q28=makeQuery(id+"F5.boolean.opBoolean","INTERSECT",EDGE,{"disambiguationData":[OD(0.0)],"derivedFrom":[makeQuery(id+"F1.opExtrude","SWEPT_FACE",FACE,{"disambiguationData":[OSD([sQuery(id+"F0.wireOp",EDGE,"E0")])]}),makeQuery(id+"F5.opExtrude","SWEPT_FACE",FACE,{"disambiguationData":[OSD([sQuery(id+"F4.wireOp",EDGE,"E160")])]})]});
            var Q29;
            Q29=makeQuery(id+"F5.boolean.opBoolean","INTERSECT",EDGE,{"disambiguationData":[OD(0.0)],"derivedFrom":[makeQuery(id+"F1.opExtrude","SWEPT_FACE",FACE,{"disambiguationData":[OSD([sQuery(id+"F0.wireOp",EDGE,"E0")])]}),makeQuery(id+"F5.opExtrude","SWEPT_FACE",FACE,{"disambiguationData":[OSD([sQuery(id+"F4.wireOp",EDGE,"E159")])]})]});
            var Q30;
            Q30=makeQuery(id+"F5.boolean.opBoolean","INTERSECT",EDGE,{"disambiguationData":[OD(0.0)],"derivedFrom":[makeQuery(id+"F1.opExtrude","SWEPT_FACE",FACE,{"disambiguationData":[OSD([sQuery(id+"F0.wireOp",EDGE,"E0")])]}),makeQuery(id+"F5.opExtrude","SWEPT_FACE",FACE,{"disambiguationData":[OSD([sQuery(id+"F4.wireOp",EDGE,"E145")])]})]});
            var Q31;
            Q31=makeQuery(id+"F5.boolean.opBoolean","INTERSECT",EDGE,{"disambiguationData":[OD(0.0)],"derivedFrom":[makeQuery(id+"F1.opExtrude","SWEPT_FACE",FACE,{"disambiguationData":[OSD([sQuery(id+"F0.wireOp",EDGE,"E0")])]}),makeQuery(id+"F5.opExtrude","SWEPT_FACE",FACE,{"disambiguationData":[OSD([sQuery(id+"F4.wireOp",EDGE,"E144")])]})]});
            var Q32;
            Q32=makeQuery(id+"F5.boolean.opBoolean","INTERSECT",EDGE,{"disambiguationData":[OD(0.0)],"derivedFrom":[makeQuery(id+"F1.opExtrude","SWEPT_FACE",FACE,{"disambiguationData":[OSD([sQuery(id+"F0.wireOp",EDGE,"E0")])]}),makeQuery(id+"F5.opExtrude","SWEPT_FACE",FACE,{"disambiguationData":[OSD([sQuery(id+"F4.wireOp",EDGE,"E143")])]})]});
            var Q33;
            Q33=makeQuery(id+"F5.boolean.opBoolean","INTERSECT",EDGE,{"disambiguationData":[OD(0.0)],"derivedFrom":[makeQuery(id+"F1.opExtrude","SWEPT_FACE",FACE,{"disambiguationData":[OSD([sQuery(id+"F0.wireOp",EDGE,"E0")])]}),makeQuery(id+"F5.opExtrude","SWEPT_FACE",FACE,{"disambiguationData":[OSD([sQuery(id+"F4.wireOp",EDGE,"E142")])]})]});
            var Q34;
            Q34=makeQuery(id+"F5.boolean.opBoolean","INTERSECT",EDGE,{"disambiguationData":[OD(0.0)],"derivedFrom":[makeQuery(id+"F1.opExtrude","SWEPT_FACE",FACE,{"disambiguationData":[OSD([sQuery(id+"F0.wireOp",EDGE,"E0")])]}),makeQuery(id+"F5.opExtrude","SWEPT_FACE",FACE,{"disambiguationData":[OSD([sQuery(id+"F4.wireOp",EDGE,"E141")])]})]});
            var Q35;
            Q35=makeQuery(id+"F5.boolean.opBoolean","INTERSECT",EDGE,{"disambiguationData":[OD(0.0)],"derivedFrom":[makeQuery(id+"F1.opExtrude","SWEPT_FACE",FACE,{"disambiguationData":[OSD([sQuery(id+"F0.wireOp",EDGE,"E0")])]}),makeQuery(id+"F5.opExtrude","SWEPT_FACE",FACE,{"disambiguationData":[OSD([sQuery(id+"F4.wireOp",EDGE,"E140")])]})]});
            var Q36;
            Q36=makeQuery(id+"F5.boolean.opBoolean","INTERSECT",EDGE,{"disambiguationData":[OD(0.0)],"derivedFrom":[makeQuery(id+"F1.opExtrude","SWEPT_FACE",FACE,{"disambiguationData":[OSD([sQuery(id+"F0.wireOp",EDGE,"E0")])]}),makeQuery(id+"F5.opExtrude","SWEPT_FACE",FACE,{"disambiguationData":[OSD([sQuery(id+"F4.wireOp",EDGE,"E125")])]})]});
            var Q37;
            Q37=makeQuery(id+"F5.boolean.opBoolean","INTERSECT",EDGE,{"disambiguationData":[OD(0.0)],"derivedFrom":[makeQuery(id+"F1.opExtrude","SWEPT_FACE",FACE,{"disambiguationData":[OSD([sQuery(id+"F0.wireOp",EDGE,"E0")])]}),makeQuery(id+"F5.opExtrude","SWEPT_FACE",FACE,{"disambiguationData":[OSD([sQuery(id+"F4.wireOp",EDGE,"E126")])]})]});
            var Q38;
            Q38=makeQuery(id+"F5.boolean.opBoolean","INTERSECT",EDGE,{"disambiguationData":[OD(0.0)],"derivedFrom":[makeQuery(id+"F1.opExtrude","SWEPT_FACE",FACE,{"disambiguationData":[OSD([sQuery(id+"F0.wireOp",EDGE,"E0")])]}),makeQuery(id+"F5.opExtrude","SWEPT_FACE",FACE,{"disambiguationData":[OSD([sQuery(id+"F4.wireOp",EDGE,"E127")])]})]});
            var Q39;
            Q39=makeQuery(id+"F5.boolean.opBoolean","INTERSECT",EDGE,{"disambiguationData":[OD(0.0)],"derivedFrom":[makeQuery(id+"F1.opExtrude","SWEPT_FACE",FACE,{"disambiguationData":[OSD([sQuery(id+"F0.wireOp",EDGE,"E0")])]}),makeQuery(id+"F5.opExtrude","SWEPT_FACE",FACE,{"disambiguationData":[OSD([sQuery(id+"F4.wireOp",EDGE,"E122")])]})]});
            var Q40;
            Q40=makeQuery(id+"F5.boolean.opBoolean","INTERSECT",EDGE,{"disambiguationData":[OD(0.0)],"derivedFrom":[makeQuery(id+"F1.opExtrude","SWEPT_FACE",FACE,{"disambiguationData":[OSD([sQuery(id+"F0.wireOp",EDGE,"E0")])]}),makeQuery(id+"F5.opExtrude","SWEPT_FACE",FACE,{"disambiguationData":[OSD([sQuery(id+"F4.wireOp",EDGE,"E123")])]})]});
            var Q41;
            Q41=makeQuery(id+"F5.boolean.opBoolean","INTERSECT",EDGE,{"disambiguationData":[OD(0.0)],"derivedFrom":[makeQuery(id+"F1.opExtrude","SWEPT_FACE",FACE,{"disambiguationData":[OSD([sQuery(id+"F0.wireOp",EDGE,"E0")])]}),makeQuery(id+"F5.opExtrude","SWEPT_FACE",FACE,{"disambiguationData":[OSD([sQuery(id+"F4.wireOp",EDGE,"E124")])]})]});
            var Q42;
            Q42=makeQuery(id+"F5.boolean.opBoolean","INTERSECT",EDGE,{"disambiguationData":[OD(0.0)],"derivedFrom":[makeQuery(id+"F1.opExtrude","SWEPT_FACE",FACE,{"disambiguationData":[OSD([sQuery(id+"F0.wireOp",EDGE,"E0")])]}),makeQuery(id+"F5.opExtrude","SWEPT_FACE",FACE,{"disambiguationData":[OSD([sQuery(id+"F4.wireOp",EDGE,"E109")])]})]});
            var Q43;
            Q43=makeQuery(id+"F5.boolean.opBoolean","INTERSECT",EDGE,{"disambiguationData":[OD(0.0)],"derivedFrom":[makeQuery(id+"F1.opExtrude","SWEPT_FACE",FACE,{"disambiguationData":[OSD([sQuery(id+"F0.wireOp",EDGE,"E0")])]}),makeQuery(id+"F5.opExtrude","SWEPT_FACE",FACE,{"disambiguationData":[OSD([sQuery(id+"F4.wireOp",EDGE,"E108")])]})]});
            var Q44;
            Q44=makeQuery(id+"F5.boolean.opBoolean","INTERSECT",EDGE,{"disambiguationData":[OD(0.0)],"derivedFrom":[makeQuery(id+"F1.opExtrude","SWEPT_FACE",FACE,{"disambiguationData":[OSD([sQuery(id+"F0.wireOp",EDGE,"E0")])]}),makeQuery(id+"F5.opExtrude","SWEPT_FACE",FACE,{"disambiguationData":[OSD([sQuery(id+"F4.wireOp",EDGE,"E107")])]})]});
            var Q45;
            Q45=makeQuery(id+"F5.boolean.opBoolean","INTERSECT",EDGE,{"disambiguationData":[OD(0.0)],"derivedFrom":[makeQuery(id+"F1.opExtrude","SWEPT_FACE",FACE,{"disambiguationData":[OSD([sQuery(id+"F0.wireOp",EDGE,"E0")])]}),makeQuery(id+"F5.opExtrude","SWEPT_FACE",FACE,{"disambiguationData":[OSD([sQuery(id+"F4.wireOp",EDGE,"E106")])]})]});
            var Q46;
            Q46=makeQuery(id+"F5.boolean.opBoolean","INTERSECT",EDGE,{"disambiguationData":[OD(0.0)],"derivedFrom":[makeQuery(id+"F1.opExtrude","SWEPT_FACE",FACE,{"disambiguationData":[OSD([sQuery(id+"F0.wireOp",EDGE,"E0")])]}),makeQuery(id+"F5.opExtrude","SWEPT_FACE",FACE,{"disambiguationData":[OSD([sQuery(id+"F4.wireOp",EDGE,"E105")])]})]});
            var Q47;
            Q47=makeQuery(id+"F5.boolean.opBoolean","INTERSECT",EDGE,{"disambiguationData":[OD(0.0)],"derivedFrom":[makeQuery(id+"F1.opExtrude","SWEPT_FACE",FACE,{"disambiguationData":[OSD([sQuery(id+"F0.wireOp",EDGE,"E0")])]}),makeQuery(id+"F5.opExtrude","SWEPT_FACE",FACE,{"disambiguationData":[OSD([sQuery(id+"F4.wireOp",EDGE,"E104")])]})]});
            var Q48;
            Q48=makeQuery(id+"F5.boolean.opBoolean","INTERSECT",EDGE,{"disambiguationData":[OD(0.0)],"derivedFrom":[makeQuery(id+"F1.opExtrude","SWEPT_FACE",FACE,{"disambiguationData":[OSD([sQuery(id+"F0.wireOp",EDGE,"E0")])]}),makeQuery(id+"F5.opExtrude","SWEPT_FACE",FACE,{"disambiguationData":[OSD([sQuery(id+"F4.wireOp",EDGE,"E86")])]})]});
            var Q49;
            Q49=makeQuery(id+"F5.boolean.opBoolean","INTERSECT",EDGE,{"disambiguationData":[OD(0.0)],"derivedFrom":[makeQuery(id+"F1.opExtrude","SWEPT_FACE",FACE,{"disambiguationData":[OSD([sQuery(id+"F0.wireOp",EDGE,"E0")])]}),makeQuery(id+"F5.opExtrude","SWEPT_FACE",FACE,{"disambiguationData":[OSD([sQuery(id+"F4.wireOp",EDGE,"E91")])]})]});
            var Q50;
            Q50=makeQuery(id+"F5.boolean.opBoolean","INTERSECT",EDGE,{"disambiguationData":[OD(0.0)],"derivedFrom":[makeQuery(id+"F1.opExtrude","SWEPT_FACE",FACE,{"disambiguationData":[OSD([sQuery(id+"F0.wireOp",EDGE,"E0")])]}),makeQuery(id+"F5.opExtrude","SWEPT_FACE",FACE,{"disambiguationData":[OSD([sQuery(id+"F4.wireOp",EDGE,"E90")])]})]});
            var Q51;
            Q51=makeQuery(id+"F5.boolean.opBoolean","INTERSECT",EDGE,{"disambiguationData":[OD(0.0)],"derivedFrom":[makeQuery(id+"F1.opExtrude","SWEPT_FACE",FACE,{"disambiguationData":[OSD([sQuery(id+"F0.wireOp",EDGE,"E0")])]}),makeQuery(id+"F5.opExtrude","SWEPT_FACE",FACE,{"disambiguationData":[OSD([sQuery(id+"F4.wireOp",EDGE,"E89")])]})]});
            var Q52;
            Q52=makeQuery(id+"F5.boolean.opBoolean","INTERSECT",EDGE,{"disambiguationData":[OD(0.0)],"derivedFrom":[makeQuery(id+"F1.opExtrude","SWEPT_FACE",FACE,{"disambiguationData":[OSD([sQuery(id+"F0.wireOp",EDGE,"E0")])]}),makeQuery(id+"F5.opExtrude","SWEPT_FACE",FACE,{"disambiguationData":[OSD([sQuery(id+"F4.wireOp",EDGE,"E88")])]})]});
            var Q53;
            Q53=makeQuery(id+"F5.boolean.opBoolean","INTERSECT",EDGE,{"disambiguationData":[OD(0.0)],"derivedFrom":[makeQuery(id+"F1.opExtrude","SWEPT_FACE",FACE,{"disambiguationData":[OSD([sQuery(id+"F0.wireOp",EDGE,"E0")])]}),makeQuery(id+"F5.opExtrude","SWEPT_FACE",FACE,{"disambiguationData":[OSD([sQuery(id+"F4.wireOp",EDGE,"E87")])]})]});
            var Q54;
            Q54=makeQuery(id+"F5.boolean.opBoolean","INTERSECT",EDGE,{"disambiguationData":[OD(0.0)],"derivedFrom":[makeQuery(id+"F1.opExtrude","SWEPT_FACE",FACE,{"disambiguationData":[OSD([sQuery(id+"F0.wireOp",EDGE,"E0")])]}),makeQuery(id+"F5.opExtrude","SWEPT_FACE",FACE,{"disambiguationData":[OSD([sQuery(id+"F4.wireOp",EDGE,"E71")])]})]});
            var Q55;
            Q55=makeQuery(id+"F5.boolean.opBoolean","INTERSECT",EDGE,{"disambiguationData":[OD(0.0)],"derivedFrom":[makeQuery(id+"F1.opExtrude","SWEPT_FACE",FACE,{"disambiguationData":[OSD([sQuery(id+"F0.wireOp",EDGE,"E0")])]}),makeQuery(id+"F5.opExtrude","SWEPT_FACE",FACE,{"disambiguationData":[OSD([sQuery(id+"F4.wireOp",EDGE,"E72")])]})]});
            var Q56;
            Q56=makeQuery(id+"F5.boolean.opBoolean","INTERSECT",EDGE,{"disambiguationData":[OD(0.0)],"derivedFrom":[makeQuery(id+"F1.opExtrude","SWEPT_FACE",FACE,{"disambiguationData":[OSD([sQuery(id+"F0.wireOp",EDGE,"E0")])]}),makeQuery(id+"F5.opExtrude","SWEPT_FACE",FACE,{"disambiguationData":[OSD([sQuery(id+"F4.wireOp",EDGE,"E73")])]})]});
            var Q57;
            Q57=makeQuery(id+"F5.boolean.opBoolean","INTERSECT",EDGE,{"disambiguationData":[OD(0.0)],"derivedFrom":[makeQuery(id+"F1.opExtrude","SWEPT_FACE",FACE,{"disambiguationData":[OSD([sQuery(id+"F0.wireOp",EDGE,"E0")])]}),makeQuery(id+"F5.opExtrude","SWEPT_FACE",FACE,{"disambiguationData":[OSD([sQuery(id+"F4.wireOp",EDGE,"E68")])]})]});
            var Q58;
            Q58=makeQuery(id+"F5.boolean.opBoolean","INTERSECT",EDGE,{"disambiguationData":[OD(0.0)],"derivedFrom":[makeQuery(id+"F1.opExtrude","SWEPT_FACE",FACE,{"disambiguationData":[OSD([sQuery(id+"F0.wireOp",EDGE,"E0")])]}),makeQuery(id+"F5.opExtrude","SWEPT_FACE",FACE,{"disambiguationData":[OSD([sQuery(id+"F4.wireOp",EDGE,"E69")])]})]});
            var Q59;
            Q59=makeQuery(id+"F5.boolean.opBoolean","INTERSECT",EDGE,{"disambiguationData":[OD(0.0)],"derivedFrom":[makeQuery(id+"F1.opExtrude","SWEPT_FACE",FACE,{"disambiguationData":[OSD([sQuery(id+"F0.wireOp",EDGE,"E0")])]}),makeQuery(id+"F5.opExtrude","SWEPT_FACE",FACE,{"disambiguationData":[OSD([sQuery(id+"F4.wireOp",EDGE,"E70")])]})]});
            var Q60;
            Q60=makeQuery(id+"F5.boolean.opBoolean","INTERSECT",EDGE,{"disambiguationData":[OD(0.0)],"derivedFrom":[makeQuery(id+"F1.opExtrude","SWEPT_FACE",FACE,{"disambiguationData":[OSD([sQuery(id+"F0.wireOp",EDGE,"E0")])]}),makeQuery(id+"F5.opExtrude","SWEPT_FACE",FACE,{"disambiguationData":[OSD([sQuery(id+"F4.wireOp",EDGE,"E55")])]})]});
            var Q61;
            Q61=makeQuery(id+"F5.boolean.opBoolean","INTERSECT",EDGE,{"disambiguationData":[OD(0.0)],"derivedFrom":[makeQuery(id+"F1.opExtrude","SWEPT_FACE",FACE,{"disambiguationData":[OSD([sQuery(id+"F0.wireOp",EDGE,"E0")])]}),makeQuery(id+"F5.opExtrude","SWEPT_FACE",FACE,{"disambiguationData":[OSD([sQuery(id+"F4.wireOp",EDGE,"E54")])]})]});
            var Q62;
            Q62=makeQuery(id+"F5.boolean.opBoolean","INTERSECT",EDGE,{"disambiguationData":[OD(0.0)],"derivedFrom":[makeQuery(id+"F1.opExtrude","SWEPT_FACE",FACE,{"disambiguationData":[OSD([sQuery(id+"F0.wireOp",EDGE,"E0")])]}),makeQuery(id+"F5.opExtrude","SWEPT_FACE",FACE,{"disambiguationData":[OSD([sQuery(id+"F4.wireOp",EDGE,"E53")])]})]});
            var Q63;
            Q63=makeQuery(id+"F5.boolean.opBoolean","INTERSECT",EDGE,{"disambiguationData":[OD(0.0)],"derivedFrom":[makeQuery(id+"F1.opExtrude","SWEPT_FACE",FACE,{"disambiguationData":[OSD([sQuery(id+"F0.wireOp",EDGE,"E0")])]}),makeQuery(id+"F5.opExtrude","SWEPT_FACE",FACE,{"disambiguationData":[OSD([sQuery(id+"F4.wireOp",EDGE,"E52")])]})]});
            var Q64;
            Q64=makeQuery(id+"F5.boolean.opBoolean","INTERSECT",EDGE,{"disambiguationData":[OD(0.0)],"derivedFrom":[makeQuery(id+"F1.opExtrude","SWEPT_FACE",FACE,{"disambiguationData":[OSD([sQuery(id+"F0.wireOp",EDGE,"E0")])]}),makeQuery(id+"F5.opExtrude","SWEPT_FACE",FACE,{"disambiguationData":[OSD([sQuery(id+"F4.wireOp",EDGE,"E51")])]})]});
            var Q65;
            Q65=makeQuery(id+"F5.boolean.opBoolean","INTERSECT",EDGE,{"disambiguationData":[OD(0.0)],"derivedFrom":[makeQuery(id+"F1.opExtrude","SWEPT_FACE",FACE,{"disambiguationData":[OSD([sQuery(id+"F0.wireOp",EDGE,"E0")])]}),makeQuery(id+"F5.opExtrude","SWEPT_FACE",FACE,{"disambiguationData":[OSD([sQuery(id+"F4.wireOp",EDGE,"E50")])]})]});
            var Q66;
            Q66=makeQuery(id+"F5.boolean.opBoolean","INTERSECT",EDGE,{"disambiguationData":[OD(0.0)],"derivedFrom":[makeQuery(id+"F1.opExtrude","SWEPT_FACE",FACE,{"disambiguationData":[OSD([sQuery(id+"F0.wireOp",EDGE,"E0")])]}),makeQuery(id+"F5.opExtrude","SWEPT_FACE",FACE,{"disambiguationData":[OSD([sQuery(id+"F4.wireOp",EDGE,"E37")])]})]});
            var Q67;
            Q67=makeQuery(id+"F5.boolean.opBoolean","INTERSECT",EDGE,{"disambiguationData":[OD(0.0)],"derivedFrom":[makeQuery(id+"F1.opExtrude","SWEPT_FACE",FACE,{"disambiguationData":[OSD([sQuery(id+"F0.wireOp",EDGE,"E0")])]}),makeQuery(id+"F5.opExtrude","SWEPT_FACE",FACE,{"disambiguationData":[OSD([sQuery(id+"F4.wireOp",EDGE,"E35")])]})]});
            var Q68;
            Q68=makeQuery(id+"F5.boolean.opBoolean","INTERSECT",EDGE,{"disambiguationData":[OD(0.0)],"derivedFrom":[makeQuery(id+"F1.opExtrude","SWEPT_FACE",FACE,{"disambiguationData":[OSD([sQuery(id+"F0.wireOp",EDGE,"E0")])]}),makeQuery(id+"F5.opExtrude","SWEPT_FACE",FACE,{"disambiguationData":[OSD([sQuery(id+"F4.wireOp",EDGE,"E34")])]})]});
            var Q69;
            Q69=makeQuery(id+"F5.boolean.opBoolean","INTERSECT",EDGE,{"disambiguationData":[OD(0.0)],"derivedFrom":[makeQuery(id+"F1.opExtrude","SWEPT_FACE",FACE,{"disambiguationData":[OSD([sQuery(id+"F0.wireOp",EDGE,"E0")])]}),makeQuery(id+"F5.opExtrude","SWEPT_FACE",FACE,{"disambiguationData":[OSD([sQuery(id+"F4.wireOp",EDGE,"E33")])]})]});
            var Q70;
            Q70=makeQuery(id+"F5.boolean.opBoolean","INTERSECT",EDGE,{"disambiguationData":[OD(0.0)],"derivedFrom":[makeQuery(id+"F1.opExtrude","SWEPT_FACE",FACE,{"disambiguationData":[OSD([sQuery(id+"F0.wireOp",EDGE,"E0")])]}),makeQuery(id+"F5.opExtrude","SWEPT_FACE",FACE,{"disambiguationData":[OSD([sQuery(id+"F4.wireOp",EDGE,"E32")])]})]});
            var Q71;
            Q71=makeQuery(id+"F5.boolean.opBoolean","INTERSECT",EDGE,{"disambiguationData":[OD(0.0)],"derivedFrom":[makeQuery(id+"F1.opExtrude","SWEPT_FACE",FACE,{"disambiguationData":[OSD([sQuery(id+"F0.wireOp",EDGE,"E0")])]}),makeQuery(id+"F5.opExtrude","SWEPT_FACE",FACE,{"disambiguationData":[OSD([sQuery(id+"F4.wireOp",EDGE,"E36")])]})]});
            var Q72;
            Q72=makeQuery(id+"F5.boolean.opBoolean","INTERSECT",EDGE,{"disambiguationData":[OD(0.0)],"derivedFrom":[makeQuery(id+"F1.opExtrude","SWEPT_FACE",FACE,{"disambiguationData":[OSD([sQuery(id+"F0.wireOp",EDGE,"E0")])]}),makeQuery(id+"F5.opExtrude","SWEPT_FACE",FACE,{"disambiguationData":[OSD([sQuery(id+"F4.wireOp",EDGE,"E17")])]})]});
            var Q73;
            Q73=makeQuery(id+"F5.boolean.opBoolean","INTERSECT",EDGE,{"disambiguationData":[OD(0.0)],"derivedFrom":[makeQuery(id+"F1.opExtrude","SWEPT_FACE",FACE,{"disambiguationData":[OSD([sQuery(id+"F0.wireOp",EDGE,"E0")])]}),makeQuery(id+"F5.opExtrude","SWEPT_FACE",FACE,{"disambiguationData":[OSD([sQuery(id+"F4.wireOp",EDGE,"E18")])]})]});
            var Q74;
            Q74=makeQuery(id+"F5.boolean.opBoolean","INTERSECT",EDGE,{"disambiguationData":[OD(0.0)],"derivedFrom":[makeQuery(id+"F1.opExtrude","SWEPT_FACE",FACE,{"disambiguationData":[OSD([sQuery(id+"F0.wireOp",EDGE,"E0")])]}),makeQuery(id+"F5.opExtrude","SWEPT_FACE",FACE,{"disambiguationData":[OSD([sQuery(id+"F4.wireOp",EDGE,"E19")])]})]});
            var Q75;
            Q75=makeQuery(id+"F5.boolean.opBoolean","INTERSECT",EDGE,{"disambiguationData":[OD(0.0)],"derivedFrom":[makeQuery(id+"F1.opExtrude","SWEPT_FACE",FACE,{"disambiguationData":[OSD([sQuery(id+"F0.wireOp",EDGE,"E0")])]}),makeQuery(id+"F5.opExtrude","SWEPT_FACE",FACE,{"disambiguationData":[OSD([sQuery(id+"F4.wireOp",EDGE,"E14")])]})]});
            var Q76;
            Q76=makeQuery(id+"F5.boolean.opBoolean","INTERSECT",EDGE,{"disambiguationData":[OD(0.0)],"derivedFrom":[makeQuery(id+"F1.opExtrude","SWEPT_FACE",FACE,{"disambiguationData":[OSD([sQuery(id+"F0.wireOp",EDGE,"E0")])]}),makeQuery(id+"F5.opExtrude","SWEPT_FACE",FACE,{"disambiguationData":[OSD([sQuery(id+"F4.wireOp",EDGE,"E15")])]})]});
            var Q77;
            Q77=makeQuery(id+"F5.boolean.opBoolean","INTERSECT",EDGE,{"disambiguationData":[OD(0.0)],"derivedFrom":[makeQuery(id+"F1.opExtrude","SWEPT_FACE",FACE,{"disambiguationData":[OSD([sQuery(id+"F0.wireOp",EDGE,"E0")])]}),makeQuery(id+"F5.opExtrude","SWEPT_FACE",FACE,{"disambiguationData":[OSD([sQuery(id+"F4.wireOp",EDGE,"E16")])]})]});
            var Q78;
            Q78=makeQuery(id+"F5.boolean.opBoolean","INTERSECT",EDGE,{"disambiguationData":[OD(0.0)],"derivedFrom":[makeQuery(id+"F1.opExtrude","SWEPT_FACE",FACE,{"disambiguationData":[OSD([sQuery(id+"F0.wireOp",EDGE,"E0")])]}),makeQuery(id+"F5.opExtrude","SWEPT_FACE",FACE,{"disambiguationData":[OSD([sQuery(id+"F4.wireOp",EDGE,"E249")])]})]});
            var Q79;
            Q79=makeQuery(id+"F5.boolean.opBoolean","INTERSECT",EDGE,{"disambiguationData":[OD(0.0)],"derivedFrom":[makeQuery(id+"F1.opExtrude","SWEPT_FACE",FACE,{"disambiguationData":[OSD([sQuery(id+"F0.wireOp",EDGE,"E0")])]}),makeQuery(id+"F5.opExtrude","SWEPT_FACE",FACE,{"disambiguationData":[OSD([sQuery(id+"F4.wireOp",EDGE,"E250")])]})]});
            var Q80;
            Q80=makeQuery(id+"F5.boolean.opBoolean","INTERSECT",EDGE,{"disambiguationData":[OD(0.0)],"derivedFrom":[makeQuery(id+"F1.opExtrude","SWEPT_FACE",FACE,{"disambiguationData":[OSD([sQuery(id+"F0.wireOp",EDGE,"E0")])]}),makeQuery(id+"F5.opExtrude","SWEPT_FACE",FACE,{"disambiguationData":[OSD([sQuery(id+"F4.wireOp",EDGE,"E251")])]})]});
            var Q81;
            Q81=makeQuery(id+"F5.boolean.opBoolean","INTERSECT",EDGE,{"disambiguationData":[OD(0.0)],"derivedFrom":[makeQuery(id+"F1.opExtrude","SWEPT_FACE",FACE,{"disambiguationData":[OSD([sQuery(id+"F0.wireOp",EDGE,"E0")])]}),makeQuery(id+"F5.opExtrude","SWEPT_FACE",FACE,{"disambiguationData":[OSD([sQuery(id+"F4.wireOp",EDGE,"E252")])]})]});
            var Q82;
            Q82=makeQuery(id+"F5.boolean.opBoolean","INTERSECT",EDGE,{"disambiguationData":[OD(0.0)],"derivedFrom":[makeQuery(id+"F1.opExtrude","SWEPT_FACE",FACE,{"disambiguationData":[OSD([sQuery(id+"F0.wireOp",EDGE,"E0")])]}),makeQuery(id+"F5.opExtrude","SWEPT_FACE",FACE,{"disambiguationData":[OSD([sQuery(id+"F4.wireOp",EDGE,"E253")])]})]});
            var Q83;
            Q83=makeQuery(id+"F5.boolean.opBoolean","INTERSECT",EDGE,{"disambiguationData":[OD(0.0)],"derivedFrom":[makeQuery(id+"F1.opExtrude","SWEPT_FACE",FACE,{"disambiguationData":[OSD([sQuery(id+"F0.wireOp",EDGE,"E0")])]}),makeQuery(id+"F5.opExtrude","SWEPT_FACE",FACE,{"disambiguationData":[OSD([sQuery(id+"F4.wireOp",EDGE,"E248")])]})]});
            var Q84;
            Q84=makeQuery(id+"F7.boolean.opBoolean","INTERSECT",EDGE,{"disambiguationData":[OD(0.0)],"derivedFrom":[makeQuery(id+"F1.opExtrude","SWEPT_FACE",FACE,{"disambiguationData":[OSD([sQuery(id+"F0.wireOp",EDGE,"E0")])]}),makeQuery(id+"F7.opExtrude","SWEPT_FACE",FACE,{"disambiguationData":[OSD([sQuery(id+"F6.wireOp",EDGE,"E504")])]})]});
            var Q85;
            Q85=makeQuery(id+"F7.boolean.opBoolean","INTERSECT",EDGE,{"disambiguationData":[OD(0.0)],"derivedFrom":[makeQuery(id+"F1.opExtrude","SWEPT_FACE",FACE,{"disambiguationData":[OSD([sQuery(id+"F0.wireOp",EDGE,"E0")])]}),makeQuery(id+"F7.opExtrude","SWEPT_FACE",FACE,{"disambiguationData":[OSD([sQuery(id+"F6.wireOp",EDGE,"E503")])]})]});
            var Q86;
            Q86=makeQuery(id+"F7.boolean.opBoolean","INTERSECT",EDGE,{"disambiguationData":[OD(0.0)],"derivedFrom":[makeQuery(id+"F1.opExtrude","SWEPT_FACE",FACE,{"disambiguationData":[OSD([sQuery(id+"F0.wireOp",EDGE,"E0")])]}),makeQuery(id+"F7.opExtrude","SWEPT_FACE",FACE,{"disambiguationData":[OSD([sQuery(id+"F6.wireOp",EDGE,"E502")])]})]});
            var Q87;
            Q87=makeQuery(id+"F7.boolean.opBoolean","INTERSECT",EDGE,{"disambiguationData":[OD(0.0)],"derivedFrom":[makeQuery(id+"F1.opExtrude","SWEPT_FACE",FACE,{"disambiguationData":[OSD([sQuery(id+"F0.wireOp",EDGE,"E0")])]}),makeQuery(id+"F7.opExtrude","SWEPT_FACE",FACE,{"disambiguationData":[OSD([sQuery(id+"F6.wireOp",EDGE,"E501")])]})]});
            var Q88;
            Q88=makeQuery(id+"F7.boolean.opBoolean","INTERSECT",EDGE,{"disambiguationData":[OD(0.0)],"derivedFrom":[makeQuery(id+"F1.opExtrude","SWEPT_FACE",FACE,{"disambiguationData":[OSD([sQuery(id+"F0.wireOp",EDGE,"E0")])]}),makeQuery(id+"F7.opExtrude","SWEPT_FACE",FACE,{"disambiguationData":[OSD([sQuery(id+"F6.wireOp",EDGE,"E500")])]})]});
            var Q89;
            Q89=makeQuery(id+"F7.boolean.opBoolean","INTERSECT",EDGE,{"disambiguationData":[OD(0.0)],"derivedFrom":[makeQuery(id+"F1.opExtrude","SWEPT_FACE",FACE,{"disambiguationData":[OSD([sQuery(id+"F0.wireOp",EDGE,"E0")])]}),makeQuery(id+"F7.opExtrude","SWEPT_FACE",FACE,{"disambiguationData":[OSD([sQuery(id+"F6.wireOp",EDGE,"E505")])]})]});
            var Q90;
            Q90=makeQuery(id+"F7.boolean.opBoolean","INTERSECT",EDGE,{"disambiguationData":[OD(0.0)],"derivedFrom":[makeQuery(id+"F1.opExtrude","SWEPT_FACE",FACE,{"disambiguationData":[OSD([sQuery(id+"F0.wireOp",EDGE,"E0")])]}),makeQuery(id+"F7.opExtrude","SWEPT_FACE",FACE,{"disambiguationData":[OSD([sQuery(id+"F6.wireOp",EDGE,"E482")])]})]});
            var Q91;
            Q91=makeQuery(id+"F7.boolean.opBoolean","INTERSECT",EDGE,{"disambiguationData":[OD(0.0)],"derivedFrom":[makeQuery(id+"F1.opExtrude","SWEPT_FACE",FACE,{"disambiguationData":[OSD([sQuery(id+"F0.wireOp",EDGE,"E0")])]}),makeQuery(id+"F7.opExtrude","SWEPT_FACE",FACE,{"disambiguationData":[OSD([sQuery(id+"F6.wireOp",EDGE,"E483")])]})]});
            var Q92;
            Q92=makeQuery(id+"F7.boolean.opBoolean","INTERSECT",EDGE,{"disambiguationData":[OD(0.0)],"derivedFrom":[makeQuery(id+"F1.opExtrude","SWEPT_FACE",FACE,{"disambiguationData":[OSD([sQuery(id+"F0.wireOp",EDGE,"E0")])]}),makeQuery(id+"F7.opExtrude","SWEPT_FACE",FACE,{"disambiguationData":[OSD([sQuery(id+"F6.wireOp",EDGE,"E484")])]})]});
            var Q93;
            Q93=makeQuery(id+"F7.boolean.opBoolean","INTERSECT",EDGE,{"disambiguationData":[OD(0.0)],"derivedFrom":[makeQuery(id+"F1.opExtrude","SWEPT_FACE",FACE,{"disambiguationData":[OSD([sQuery(id+"F0.wireOp",EDGE,"E0")])]}),makeQuery(id+"F7.opExtrude","SWEPT_FACE",FACE,{"disambiguationData":[OSD([sQuery(id+"F6.wireOp",EDGE,"E485")])]})]});
            var Q94;
            Q94=makeQuery(id+"F7.boolean.opBoolean","INTERSECT",EDGE,{"disambiguationData":[OD(0.0)],"derivedFrom":[makeQuery(id+"F1.opExtrude","SWEPT_FACE",FACE,{"disambiguationData":[OSD([sQuery(id+"F0.wireOp",EDGE,"E0")])]}),makeQuery(id+"F7.opExtrude","SWEPT_FACE",FACE,{"disambiguationData":[OSD([sQuery(id+"F6.wireOp",EDGE,"E486")])]})]});
            var Q95;
            Q95=makeQuery(id+"F7.boolean.opBoolean","INTERSECT",EDGE,{"disambiguationData":[OD(0.0)],"derivedFrom":[makeQuery(id+"F1.opExtrude","SWEPT_FACE",FACE,{"disambiguationData":[OSD([sQuery(id+"F0.wireOp",EDGE,"E0")])]}),makeQuery(id+"F7.opExtrude","SWEPT_FACE",FACE,{"disambiguationData":[OSD([sQuery(id+"F6.wireOp",EDGE,"E487")])]})]});
            var Q96;
            Q96=makeQuery(id+"F7.boolean.opBoolean","INTERSECT",EDGE,{"disambiguationData":[OD(0.0)],"derivedFrom":[makeQuery(id+"F1.opExtrude","SWEPT_FACE",FACE,{"disambiguationData":[OSD([sQuery(id+"F0.wireOp",EDGE,"E0")])]}),makeQuery(id+"F7.opExtrude","SWEPT_FACE",FACE,{"disambiguationData":[OSD([sQuery(id+"F6.wireOp",EDGE,"E467")])]})]});
            var Q97;
            Q97=makeQuery(id+"F7.boolean.opBoolean","INTERSECT",EDGE,{"disambiguationData":[OD(0.0)],"derivedFrom":[makeQuery(id+"F1.opExtrude","SWEPT_FACE",FACE,{"disambiguationData":[OSD([sQuery(id+"F0.wireOp",EDGE,"E0")])]}),makeQuery(id+"F7.opExtrude","SWEPT_FACE",FACE,{"disambiguationData":[OSD([sQuery(id+"F6.wireOp",EDGE,"E466")])]})]});
            var Q98;
            Q98=makeQuery(id+"F7.boolean.opBoolean","INTERSECT",EDGE,{"disambiguationData":[OD(0.0)],"derivedFrom":[makeQuery(id+"F1.opExtrude","SWEPT_FACE",FACE,{"disambiguationData":[OSD([sQuery(id+"F0.wireOp",EDGE,"E0")])]}),makeQuery(id+"F7.opExtrude","SWEPT_FACE",FACE,{"disambiguationData":[OSD([sQuery(id+"F6.wireOp",EDGE,"E465")])]})]});
            var Q99;
            Q99=makeQuery(id+"F7.boolean.opBoolean","INTERSECT",EDGE,{"disambiguationData":[OD(0.0)],"derivedFrom":[makeQuery(id+"F1.opExtrude","SWEPT_FACE",FACE,{"disambiguationData":[OSD([sQuery(id+"F0.wireOp",EDGE,"E0")])]}),makeQuery(id+"F7.opExtrude","SWEPT_FACE",FACE,{"disambiguationData":[OSD([sQuery(id+"F6.wireOp",EDGE,"E464")])]})]});
            var Q100;
            Q100=makeQuery(id+"F7.boolean.opBoolean","INTERSECT",EDGE,{"disambiguationData":[OD(0.0)],"derivedFrom":[makeQuery(id+"F1.opExtrude","SWEPT_FACE",FACE,{"disambiguationData":[OSD([sQuery(id+"F0.wireOp",EDGE,"E0")])]}),makeQuery(id+"F7.opExtrude","SWEPT_FACE",FACE,{"disambiguationData":[OSD([sQuery(id+"F6.wireOp",EDGE,"E469")])]})]});
            var Q101;
            Q101=makeQuery(id+"F7.boolean.opBoolean","INTERSECT",EDGE,{"disambiguationData":[OD(0.0)],"derivedFrom":[makeQuery(id+"F1.opExtrude","SWEPT_FACE",FACE,{"disambiguationData":[OSD([sQuery(id+"F0.wireOp",EDGE,"E0")])]}),makeQuery(id+"F7.opExtrude","SWEPT_FACE",FACE,{"disambiguationData":[OSD([sQuery(id+"F6.wireOp",EDGE,"E468")])]})]});
            var Q102;
            Q102=makeQuery(id+"F10.boolean.opBoolean","INTERSECT",EDGE,{"disambiguationData":[OD(0.0)],"derivedFrom":[makeQuery(id+"F1.opExtrude","SWEPT_FACE",FACE,{"disambiguationData":[OSD([sQuery(id+"F0.wireOp",EDGE,"E0")])]}),makeQuery(id+"F10.opExtrude","SWEPT_FACE",FACE,{"disambiguationData":[OSD([sQuery(id+"F9.wireOp",EDGE,"E746")])]})]});
            var Q103;
            Q103=makeQuery(id+"F10.boolean.opBoolean","INTERSECT",EDGE,{"disambiguationData":[OD(0.0)],"derivedFrom":[makeQuery(id+"F1.opExtrude","SWEPT_FACE",FACE,{"disambiguationData":[OSD([sQuery(id+"F0.wireOp",EDGE,"E0")])]}),makeQuery(id+"F10.opExtrude","SWEPT_FACE",FACE,{"disambiguationData":[OSD([sQuery(id+"F9.wireOp",EDGE,"E741")])]})]});
            var Q104;
            Q104=makeQuery(id+"F10.boolean.opBoolean","INTERSECT",EDGE,{"disambiguationData":[OD(0.0)],"derivedFrom":[makeQuery(id+"F1.opExtrude","SWEPT_FACE",FACE,{"disambiguationData":[OSD([sQuery(id+"F0.wireOp",EDGE,"E0")])]}),makeQuery(id+"F10.opExtrude","SWEPT_FACE",FACE,{"disambiguationData":[OSD([sQuery(id+"F9.wireOp",EDGE,"E742")])]})]});
            var Q105;
            Q105=makeQuery(id+"F10.boolean.opBoolean","INTERSECT",EDGE,{"disambiguationData":[OD(0.0)],"derivedFrom":[makeQuery(id+"F1.opExtrude","SWEPT_FACE",FACE,{"disambiguationData":[OSD([sQuery(id+"F0.wireOp",EDGE,"E0")])]}),makeQuery(id+"F10.opExtrude","SWEPT_FACE",FACE,{"disambiguationData":[OSD([sQuery(id+"F9.wireOp",EDGE,"E743")])]})]});
            var Q106;
            Q106=makeQuery(id+"F10.boolean.opBoolean","INTERSECT",EDGE,{"disambiguationData":[OD(0.0)],"derivedFrom":[makeQuery(id+"F1.opExtrude","SWEPT_FACE",FACE,{"disambiguationData":[OSD([sQuery(id+"F0.wireOp",EDGE,"E0")])]}),makeQuery(id+"F10.opExtrude","SWEPT_FACE",FACE,{"disambiguationData":[OSD([sQuery(id+"F9.wireOp",EDGE,"E744")])]})]});
            var Q107;
            Q107=makeQuery(id+"F10.boolean.opBoolean","INTERSECT",EDGE,{"disambiguationData":[OD(0.0)],"derivedFrom":[makeQuery(id+"F1.opExtrude","SWEPT_FACE",FACE,{"disambiguationData":[OSD([sQuery(id+"F0.wireOp",EDGE,"E0")])]}),makeQuery(id+"F10.opExtrude","SWEPT_FACE",FACE,{"disambiguationData":[OSD([sQuery(id+"F9.wireOp",EDGE,"E745")])]})]});
            var Q108;
            Q108=makeQuery(id+"F10.boolean.opBoolean","INTERSECT",EDGE,{"disambiguationData":[OD(0.0)],"derivedFrom":[makeQuery(id+"F1.opExtrude","SWEPT_FACE",FACE,{"disambiguationData":[OSD([sQuery(id+"F0.wireOp",EDGE,"E0")])]}),makeQuery(id+"F10.opExtrude","SWEPT_FACE",FACE,{"disambiguationData":[OSD([sQuery(id+"F9.wireOp",EDGE,"E752")])]})]});
            var Q109;
            Q109=makeQuery(id+"F10.boolean.opBoolean","INTERSECT",EDGE,{"disambiguationData":[OD(0.0)],"derivedFrom":[makeQuery(id+"F1.opExtrude","SWEPT_FACE",FACE,{"disambiguationData":[OSD([sQuery(id+"F0.wireOp",EDGE,"E0")])]}),makeQuery(id+"F10.opExtrude","SWEPT_FACE",FACE,{"disambiguationData":[OSD([sQuery(id+"F9.wireOp",EDGE,"E761")])]})]});
            var Q110;
            Q110=makeQuery(id+"F10.boolean.opBoolean","INTERSECT",EDGE,{"disambiguationData":[OD(0.0)],"derivedFrom":[makeQuery(id+"F1.opExtrude","SWEPT_FACE",FACE,{"disambiguationData":[OSD([sQuery(id+"F0.wireOp",EDGE,"E0")])]}),makeQuery(id+"F10.opExtrude","SWEPT_FACE",FACE,{"disambiguationData":[OSD([sQuery(id+"F9.wireOp",EDGE,"E759"),sQuery(id+"F9.wireOp",EDGE,"E760")])]})]});
            var Q111;
            Q111=makeQuery(id+"F10.boolean.opBoolean","INTERSECT",EDGE,{"disambiguationData":[OD(0.0)],"derivedFrom":[makeQuery(id+"F1.opExtrude","SWEPT_FACE",FACE,{"disambiguationData":[OSD([sQuery(id+"F0.wireOp",EDGE,"E0")])]}),makeQuery(id+"F10.opExtrude","SWEPT_FACE",FACE,{"disambiguationData":[OSD([sQuery(id+"F9.wireOp",EDGE,"E762")])]})]});
            var Q112;
            Q112=makeQuery(id+"F10.boolean.opBoolean","INTERSECT",EDGE,{"disambiguationData":[OD(0.0)],"derivedFrom":[makeQuery(id+"F1.opExtrude","SWEPT_FACE",FACE,{"disambiguationData":[OSD([sQuery(id+"F0.wireOp",EDGE,"E0")])]}),makeQuery(id+"F10.opExtrude","SWEPT_FACE",FACE,{"disambiguationData":[OSD([sQuery(id+"F9.wireOp",EDGE,"E728")])]})]});
            var Q113;
            Q113=makeQuery(id+"F10.boolean.opBoolean","INTERSECT",EDGE,{"disambiguationData":[OD(0.0)],"derivedFrom":[makeQuery(id+"F1.opExtrude","SWEPT_FACE",FACE,{"disambiguationData":[OSD([sQuery(id+"F0.wireOp",EDGE,"E0")])]}),makeQuery(id+"F10.opExtrude","SWEPT_FACE",FACE,{"disambiguationData":[OSD([sQuery(id+"F9.wireOp",EDGE,"E727")])]})]});
            var Q114;
            Q114=makeQuery(id+"F10.boolean.opBoolean","INTERSECT",EDGE,{"disambiguationData":[OD(0.0)],"derivedFrom":[makeQuery(id+"F1.opExtrude","SWEPT_FACE",FACE,{"disambiguationData":[OSD([sQuery(id+"F0.wireOp",EDGE,"E0")])]}),makeQuery(id+"F10.opExtrude","SWEPT_FACE",FACE,{"disambiguationData":[OSD([sQuery(id+"F9.wireOp",EDGE,"E726")])]})]});
            var Q115;
            Q115=makeQuery(id+"F10.boolean.opBoolean","INTERSECT",EDGE,{"disambiguationData":[OD(0.0)],"derivedFrom":[makeQuery(id+"F1.opExtrude","SWEPT_FACE",FACE,{"disambiguationData":[OSD([sQuery(id+"F0.wireOp",EDGE,"E0")])]}),makeQuery(id+"F10.opExtrude","SWEPT_FACE",FACE,{"disambiguationData":[OSD([sQuery(id+"F9.wireOp",EDGE,"E725")])]})]});
            var Q116;
            Q116=makeQuery(id+"F10.boolean.opBoolean","INTERSECT",EDGE,{"disambiguationData":[OD(0.0)],"derivedFrom":[makeQuery(id+"F1.opExtrude","SWEPT_FACE",FACE,{"disambiguationData":[OSD([sQuery(id+"F0.wireOp",EDGE,"E0")])]}),makeQuery(id+"F10.opExtrude","SWEPT_FACE",FACE,{"disambiguationData":[OSD([sQuery(id+"F9.wireOp",EDGE,"E724")])]})]});
            var Q117;
            Q117=makeQuery(id+"F10.boolean.opBoolean","INTERSECT",EDGE,{"disambiguationData":[OD(0.0)],"derivedFrom":[makeQuery(id+"F1.opExtrude","SWEPT_FACE",FACE,{"disambiguationData":[OSD([sQuery(id+"F0.wireOp",EDGE,"E0")])]}),makeQuery(id+"F10.opExtrude","SWEPT_FACE",FACE,{"disambiguationData":[OSD([sQuery(id+"F9.wireOp",EDGE,"E723")])]})]});
            var Q118;
            Q118=makeQuery(id+"F10.boolean.opBoolean","INTERSECT",EDGE,{"disambiguationData":[OD(0.0)],"derivedFrom":[makeQuery(id+"F1.opExtrude","SWEPT_FACE",FACE,{"disambiguationData":[OSD([sQuery(id+"F0.wireOp",EDGE,"E0")])]}),makeQuery(id+"F10.opExtrude","SWEPT_FACE",FACE,{"disambiguationData":[OSD([sQuery(id+"F9.wireOp",EDGE,"E710")])]})]});
            var Q119;
            Q119=makeQuery(id+"F10.boolean.opBoolean","INTERSECT",EDGE,{"disambiguationData":[OD(0.0)],"derivedFrom":[makeQuery(id+"F1.opExtrude","SWEPT_FACE",FACE,{"disambiguationData":[OSD([sQuery(id+"F0.wireOp",EDGE,"E0")])]}),makeQuery(id+"F10.opExtrude","SWEPT_FACE",FACE,{"disambiguationData":[OSD([sQuery(id+"F9.wireOp",EDGE,"E705")])]})]});
            var Q120;
            Q120=makeQuery(id+"F10.boolean.opBoolean","INTERSECT",EDGE,{"disambiguationData":[OD(0.0)],"derivedFrom":[makeQuery(id+"F1.opExtrude","SWEPT_FACE",FACE,{"disambiguationData":[OSD([sQuery(id+"F0.wireOp",EDGE,"E0")])]}),makeQuery(id+"F10.opExtrude","SWEPT_FACE",FACE,{"disambiguationData":[OSD([sQuery(id+"F9.wireOp",EDGE,"E706")])]})]});
            var Q121;
            Q121=makeQuery(id+"F10.boolean.opBoolean","INTERSECT",EDGE,{"disambiguationData":[OD(0.0)],"derivedFrom":[makeQuery(id+"F1.opExtrude","SWEPT_FACE",FACE,{"disambiguationData":[OSD([sQuery(id+"F0.wireOp",EDGE,"E0")])]}),makeQuery(id+"F10.opExtrude","SWEPT_FACE",FACE,{"disambiguationData":[OSD([sQuery(id+"F9.wireOp",EDGE,"E707")])]})]});
            var Q122;
            Q122=makeQuery(id+"F10.boolean.opBoolean","INTERSECT",EDGE,{"disambiguationData":[OD(0.0)],"derivedFrom":[makeQuery(id+"F1.opExtrude","SWEPT_FACE",FACE,{"disambiguationData":[OSD([sQuery(id+"F0.wireOp",EDGE,"E0")])]}),makeQuery(id+"F10.opExtrude","SWEPT_FACE",FACE,{"disambiguationData":[OSD([sQuery(id+"F9.wireOp",EDGE,"E708")])]})]});
            var Q123;
            Q123=makeQuery(id+"F10.boolean.opBoolean","INTERSECT",EDGE,{"disambiguationData":[OD(0.0)],"derivedFrom":[makeQuery(id+"F1.opExtrude","SWEPT_FACE",FACE,{"disambiguationData":[OSD([sQuery(id+"F0.wireOp",EDGE,"E0")])]}),makeQuery(id+"F10.opExtrude","SWEPT_FACE",FACE,{"disambiguationData":[OSD([sQuery(id+"F9.wireOp",EDGE,"E709")])]})]});
            var Q124;
            Q124=makeQuery(id+"F10.boolean.opBoolean","INTERSECT",EDGE,{"disambiguationData":[OD(0.0)],"derivedFrom":[makeQuery(id+"F1.opExtrude","SWEPT_FACE",FACE,{"disambiguationData":[OSD([sQuery(id+"F0.wireOp",EDGE,"E0")])]}),makeQuery(id+"F10.opExtrude","SWEPT_FACE",FACE,{"disambiguationData":[OSD([sQuery(id+"F9.wireOp",EDGE,"E692")])]})]});
            var Q125;
            Q125=makeQuery(id+"F10.boolean.opBoolean","INTERSECT",EDGE,{"disambiguationData":[OD(0.0)],"derivedFrom":[makeQuery(id+"F1.opExtrude","SWEPT_FACE",FACE,{"disambiguationData":[OSD([sQuery(id+"F0.wireOp",EDGE,"E0")])]}),makeQuery(id+"F10.opExtrude","SWEPT_FACE",FACE,{"disambiguationData":[OSD([sQuery(id+"F9.wireOp",EDGE,"E687")])]})]});
            var Q126;
            Q126=makeQuery(id+"F10.boolean.opBoolean","INTERSECT",EDGE,{"disambiguationData":[OD(0.0)],"derivedFrom":[makeQuery(id+"F1.opExtrude","SWEPT_FACE",FACE,{"disambiguationData":[OSD([sQuery(id+"F0.wireOp",EDGE,"E0")])]}),makeQuery(id+"F10.opExtrude","SWEPT_FACE",FACE,{"disambiguationData":[OSD([sQuery(id+"F9.wireOp",EDGE,"E688")])]})]});
            var Q127;
            Q127=makeQuery(id+"F10.boolean.opBoolean","INTERSECT",EDGE,{"disambiguationData":[OD(0.0)],"derivedFrom":[makeQuery(id+"F1.opExtrude","SWEPT_FACE",FACE,{"disambiguationData":[OSD([sQuery(id+"F0.wireOp",EDGE,"E0")])]}),makeQuery(id+"F10.opExtrude","SWEPT_FACE",FACE,{"disambiguationData":[OSD([sQuery(id+"F9.wireOp",EDGE,"E689")])]})]});
            var Q128;
            Q128=makeQuery(id+"F10.boolean.opBoolean","INTERSECT",EDGE,{"disambiguationData":[OD(0.0)],"derivedFrom":[makeQuery(id+"F1.opExtrude","SWEPT_FACE",FACE,{"disambiguationData":[OSD([sQuery(id+"F0.wireOp",EDGE,"E0")])]}),makeQuery(id+"F10.opExtrude","SWEPT_FACE",FACE,{"disambiguationData":[OSD([sQuery(id+"F9.wireOp",EDGE,"E690")])]})]});
            var Q129;
            Q129=makeQuery(id+"F10.boolean.opBoolean","INTERSECT",EDGE,{"disambiguationData":[OD(0.0)],"derivedFrom":[makeQuery(id+"F1.opExtrude","SWEPT_FACE",FACE,{"disambiguationData":[OSD([sQuery(id+"F0.wireOp",EDGE,"E0")])]}),makeQuery(id+"F10.opExtrude","SWEPT_FACE",FACE,{"disambiguationData":[OSD([sQuery(id+"F9.wireOp",EDGE,"E691")])]})]});
            var Q130;
            Q130=makeQuery(id+"F7.boolean.opBoolean","INTERSECT",EDGE,{"disambiguationData":[OD(0.0)],"derivedFrom":[makeQuery(id+"F1.opExtrude","SWEPT_FACE",FACE,{"disambiguationData":[OSD([sQuery(id+"F0.wireOp",EDGE,"E0")])]}),makeQuery(id+"F7.opExtrude","SWEPT_FACE",FACE,{"disambiguationData":[OSD([sQuery(id+"F6.wireOp",EDGE,"E448")])]})]});
            var Q131;
            Q131=makeQuery(id+"F7.boolean.opBoolean","INTERSECT",EDGE,{"disambiguationData":[OD(0.0)],"derivedFrom":[makeQuery(id+"F1.opExtrude","SWEPT_FACE",FACE,{"disambiguationData":[OSD([sQuery(id+"F0.wireOp",EDGE,"E0")])]}),makeQuery(id+"F7.opExtrude","SWEPT_FACE",FACE,{"disambiguationData":[OSD([sQuery(id+"F6.wireOp",EDGE,"E449")])]})]});
            var Q132;
            Q132=makeQuery(id+"F7.boolean.opBoolean","INTERSECT",EDGE,{"disambiguationData":[OD(0.0)],"derivedFrom":[makeQuery(id+"F1.opExtrude","SWEPT_FACE",FACE,{"disambiguationData":[OSD([sQuery(id+"F0.wireOp",EDGE,"E0")])]}),makeQuery(id+"F7.opExtrude","SWEPT_FACE",FACE,{"disambiguationData":[OSD([sQuery(id+"F6.wireOp",EDGE,"E450")])]})]});
            var Q133;
            Q133=makeQuery(id+"F7.boolean.opBoolean","INTERSECT",EDGE,{"disambiguationData":[OD(0.0)],"derivedFrom":[makeQuery(id+"F1.opExtrude","SWEPT_FACE",FACE,{"disambiguationData":[OSD([sQuery(id+"F0.wireOp",EDGE,"E0")])]}),makeQuery(id+"F7.opExtrude","SWEPT_FACE",FACE,{"disambiguationData":[OSD([sQuery(id+"F6.wireOp",EDGE,"E451")])]})]});
            var Q134;
            Q134=makeQuery(id+"F7.boolean.opBoolean","INTERSECT",EDGE,{"disambiguationData":[OD(0.0)],"derivedFrom":[makeQuery(id+"F1.opExtrude","SWEPT_FACE",FACE,{"disambiguationData":[OSD([sQuery(id+"F0.wireOp",EDGE,"E0")])]}),makeQuery(id+"F7.opExtrude","SWEPT_FACE",FACE,{"disambiguationData":[OSD([sQuery(id+"F6.wireOp",EDGE,"E447")])]})]});
            var Q135;
            Q135=makeQuery(id+"F10.boolean.opBoolean","INTERSECT",EDGE,{"disambiguationData":[OD(0.0)],"derivedFrom":[makeQuery(id+"F1.opExtrude","SWEPT_FACE",FACE,{"disambiguationData":[OSD([sQuery(id+"F0.wireOp",EDGE,"E0")])]}),makeQuery(id+"F10.opExtrude","SWEPT_FACE",FACE,{"disambiguationData":[OSD([sQuery(id+"F9.wireOp",EDGE,"E671")])]})]});
            var Q136;
            Q136=makeQuery(id+"F10.boolean.opBoolean","INTERSECT",EDGE,{"disambiguationData":[OD(0.0)],"derivedFrom":[makeQuery(id+"F1.opExtrude","SWEPT_FACE",FACE,{"disambiguationData":[OSD([sQuery(id+"F0.wireOp",EDGE,"E0")])]}),makeQuery(id+"F10.opExtrude","SWEPT_FACE",FACE,{"disambiguationData":[OSD([sQuery(id+"F9.wireOp",EDGE,"E670")])]})]});
            var Q137;
            Q137=makeQuery(id+"F10.boolean.opBoolean","INTERSECT",EDGE,{"disambiguationData":[OD(0.0)],"derivedFrom":[makeQuery(id+"F1.opExtrude","SWEPT_FACE",FACE,{"disambiguationData":[OSD([sQuery(id+"F0.wireOp",EDGE,"E0")])]}),makeQuery(id+"F10.opExtrude","SWEPT_FACE",FACE,{"disambiguationData":[OSD([sQuery(id+"F9.wireOp",EDGE,"E669")])]})]});
            var Q138;
            Q138=makeQuery(id+"F10.boolean.opBoolean","INTERSECT",EDGE,{"disambiguationData":[OD(0.0)],"derivedFrom":[makeQuery(id+"F1.opExtrude","SWEPT_FACE",FACE,{"disambiguationData":[OSD([sQuery(id+"F0.wireOp",EDGE,"E0")])]}),makeQuery(id+"F10.opExtrude","SWEPT_FACE",FACE,{"disambiguationData":[OSD([sQuery(id+"F9.wireOp",EDGE,"E674")])]})]});
            var Q139;
            Q139=makeQuery(id+"F10.boolean.opBoolean","INTERSECT",EDGE,{"disambiguationData":[OD(0.0)],"derivedFrom":[makeQuery(id+"F1.opExtrude","SWEPT_FACE",FACE,{"disambiguationData":[OSD([sQuery(id+"F0.wireOp",EDGE,"E0")])]}),makeQuery(id+"F10.opExtrude","SWEPT_FACE",FACE,{"disambiguationData":[OSD([sQuery(id+"F9.wireOp",EDGE,"E673")])]})]});
            var Q140;
            Q140=makeQuery(id+"F10.boolean.opBoolean","INTERSECT",EDGE,{"disambiguationData":[OD(0.0)],"derivedFrom":[makeQuery(id+"F1.opExtrude","SWEPT_FACE",FACE,{"disambiguationData":[OSD([sQuery(id+"F0.wireOp",EDGE,"E0")])]}),makeQuery(id+"F10.opExtrude","SWEPT_FACE",FACE,{"disambiguationData":[OSD([sQuery(id+"F9.wireOp",EDGE,"E672")])]})]});
            var Q141;
            Q141=makeQuery(id+"F7.boolean.opBoolean","INTERSECT",EDGE,{"disambiguationData":[OD(0.0)],"derivedFrom":[makeQuery(id+"F1.opExtrude","SWEPT_FACE",FACE,{"disambiguationData":[OSD([sQuery(id+"F0.wireOp",EDGE,"E0")])]}),makeQuery(id+"F7.opExtrude","SWEPT_FACE",FACE,{"disambiguationData":[OSD([sQuery(id+"F6.wireOp",EDGE,"E430")])]})]});
            var Q142;
            Q142=makeQuery(id+"F7.boolean.opBoolean","INTERSECT",EDGE,{"disambiguationData":[OD(0.0)],"derivedFrom":[makeQuery(id+"F1.opExtrude","SWEPT_FACE",FACE,{"disambiguationData":[OSD([sQuery(id+"F0.wireOp",EDGE,"E0")])]}),makeQuery(id+"F7.opExtrude","SWEPT_FACE",FACE,{"disambiguationData":[OSD([sQuery(id+"F6.wireOp",EDGE,"E431")])]})]});
            var Q143;
            Q143=makeQuery(id+"F7.boolean.opBoolean","INTERSECT",EDGE,{"disambiguationData":[OD(0.0)],"derivedFrom":[makeQuery(id+"F1.opExtrude","SWEPT_FACE",FACE,{"disambiguationData":[OSD([sQuery(id+"F0.wireOp",EDGE,"E0")])]}),makeQuery(id+"F7.opExtrude","SWEPT_FACE",FACE,{"disambiguationData":[OSD([sQuery(id+"F6.wireOp",EDGE,"E432")])]})]});
            var Q144;
            Q144=makeQuery(id+"F7.boolean.opBoolean","INTERSECT",EDGE,{"disambiguationData":[OD(0.0)],"derivedFrom":[makeQuery(id+"F1.opExtrude","SWEPT_FACE",FACE,{"disambiguationData":[OSD([sQuery(id+"F0.wireOp",EDGE,"E0")])]}),makeQuery(id+"F7.opExtrude","SWEPT_FACE",FACE,{"disambiguationData":[OSD([sQuery(id+"F6.wireOp",EDGE,"E433")])]})]});
            var Q145;
            Q145=makeQuery(id+"F7.boolean.opBoolean","INTERSECT",EDGE,{"disambiguationData":[OD(0.0)],"derivedFrom":[makeQuery(id+"F1.opExtrude","SWEPT_FACE",FACE,{"disambiguationData":[OSD([sQuery(id+"F0.wireOp",EDGE,"E0")])]}),makeQuery(id+"F7.opExtrude","SWEPT_FACE",FACE,{"disambiguationData":[OSD([sQuery(id+"F6.wireOp",EDGE,"E428")])]})]});
            var Q146;
            Q146=makeQuery(id+"F7.boolean.opBoolean","INTERSECT",EDGE,{"disambiguationData":[OD(0.0)],"derivedFrom":[makeQuery(id+"F1.opExtrude","SWEPT_FACE",FACE,{"disambiguationData":[OSD([sQuery(id+"F0.wireOp",EDGE,"E0")])]}),makeQuery(id+"F7.opExtrude","SWEPT_FACE",FACE,{"disambiguationData":[OSD([sQuery(id+"F6.wireOp",EDGE,"E429")])]})]});
            var Q147;
            Q147=makeQuery(id+"F10.boolean.opBoolean","INTERSECT",EDGE,{"disambiguationData":[OD(0.0)],"derivedFrom":[makeQuery(id+"F1.opExtrude","SWEPT_FACE",FACE,{"disambiguationData":[OSD([sQuery(id+"F0.wireOp",EDGE,"E0")])]}),makeQuery(id+"F10.opExtrude","SWEPT_FACE",FACE,{"disambiguationData":[OSD([sQuery(id+"F9.wireOp",EDGE,"E653")])]})]});
            var Q148;
            Q148=makeQuery(id+"F10.boolean.opBoolean","INTERSECT",EDGE,{"disambiguationData":[OD(0.0)],"derivedFrom":[makeQuery(id+"F1.opExtrude","SWEPT_FACE",FACE,{"disambiguationData":[OSD([sQuery(id+"F0.wireOp",EDGE,"E0")])]}),makeQuery(id+"F10.opExtrude","SWEPT_FACE",FACE,{"disambiguationData":[OSD([sQuery(id+"F9.wireOp",EDGE,"E654")])]})]});
            var Q149;
            Q149=makeQuery(id+"F10.boolean.opBoolean","INTERSECT",EDGE,{"disambiguationData":[OD(0.0)],"derivedFrom":[makeQuery(id+"F1.opExtrude","SWEPT_FACE",FACE,{"disambiguationData":[OSD([sQuery(id+"F0.wireOp",EDGE,"E0")])]}),makeQuery(id+"F10.opExtrude","SWEPT_FACE",FACE,{"disambiguationData":[OSD([sQuery(id+"F9.wireOp",EDGE,"E655")])]})]});
            var Q150;
            Q150=makeQuery(id+"F10.boolean.opBoolean","INTERSECT",EDGE,{"disambiguationData":[OD(0.0)],"derivedFrom":[makeQuery(id+"F1.opExtrude","SWEPT_FACE",FACE,{"disambiguationData":[OSD([sQuery(id+"F0.wireOp",EDGE,"E0")])]}),makeQuery(id+"F10.opExtrude","SWEPT_FACE",FACE,{"disambiguationData":[OSD([sQuery(id+"F9.wireOp",EDGE,"E656")])]})]});
            var Q151;
            Q151=makeQuery(id+"F10.boolean.opBoolean","INTERSECT",EDGE,{"disambiguationData":[OD(0.0)],"derivedFrom":[makeQuery(id+"F1.opExtrude","SWEPT_FACE",FACE,{"disambiguationData":[OSD([sQuery(id+"F0.wireOp",EDGE,"E0")])]}),makeQuery(id+"F10.opExtrude","SWEPT_FACE",FACE,{"disambiguationData":[OSD([sQuery(id+"F9.wireOp",EDGE,"E651")])]})]});
            var Q152;
            Q152=makeQuery(id+"F10.boolean.opBoolean","INTERSECT",EDGE,{"disambiguationData":[OD(0.0)],"derivedFrom":[makeQuery(id+"F1.opExtrude","SWEPT_FACE",FACE,{"disambiguationData":[OSD([sQuery(id+"F0.wireOp",EDGE,"E0")])]}),makeQuery(id+"F10.opExtrude","SWEPT_FACE",FACE,{"disambiguationData":[OSD([sQuery(id+"F9.wireOp",EDGE,"E652")])]})]});
            var Q153;
            Q153=makeQuery(id+"F7.boolean.opBoolean","INTERSECT",EDGE,{"disambiguationData":[OD(0.0)],"derivedFrom":[makeQuery(id+"F1.opExtrude","SWEPT_FACE",FACE,{"disambiguationData":[OSD([sQuery(id+"F0.wireOp",EDGE,"E0")])]}),makeQuery(id+"F7.opExtrude","SWEPT_FACE",FACE,{"disambiguationData":[OSD([sQuery(id+"F6.wireOp",EDGE,"E412")])]})]});
            var Q154;
            Q154=makeQuery(id+"F7.boolean.opBoolean","INTERSECT",EDGE,{"disambiguationData":[OD(0.0)],"derivedFrom":[makeQuery(id+"F1.opExtrude","SWEPT_FACE",FACE,{"disambiguationData":[OSD([sQuery(id+"F0.wireOp",EDGE,"E0")])]}),makeQuery(id+"F7.opExtrude","SWEPT_FACE",FACE,{"disambiguationData":[OSD([sQuery(id+"F6.wireOp",EDGE,"E413")])]})]});
            var Q155;
            Q155=makeQuery(id+"F7.boolean.opBoolean","INTERSECT",EDGE,{"disambiguationData":[OD(0.0)],"derivedFrom":[makeQuery(id+"F1.opExtrude","SWEPT_FACE",FACE,{"disambiguationData":[OSD([sQuery(id+"F0.wireOp",EDGE,"E0")])]}),makeQuery(id+"F7.opExtrude","SWEPT_FACE",FACE,{"disambiguationData":[OSD([sQuery(id+"F6.wireOp",EDGE,"E414")])]})]});
            var Q156;
            Q156=makeQuery(id+"F7.boolean.opBoolean","INTERSECT",EDGE,{"disambiguationData":[OD(0.0)],"derivedFrom":[makeQuery(id+"F1.opExtrude","SWEPT_FACE",FACE,{"disambiguationData":[OSD([sQuery(id+"F0.wireOp",EDGE,"E0")])]}),makeQuery(id+"F7.opExtrude","SWEPT_FACE",FACE,{"disambiguationData":[OSD([sQuery(id+"F6.wireOp",EDGE,"E415")])]})]});
            var Q157;
            Q157=makeQuery(id+"F7.boolean.opBoolean","INTERSECT",EDGE,{"disambiguationData":[OD(0.0)],"derivedFrom":[makeQuery(id+"F1.opExtrude","SWEPT_FACE",FACE,{"disambiguationData":[OSD([sQuery(id+"F0.wireOp",EDGE,"E0")])]}),makeQuery(id+"F7.opExtrude","SWEPT_FACE",FACE,{"disambiguationData":[OSD([sQuery(id+"F6.wireOp",EDGE,"E410")])]})]});
            var Q158;
            Q158=makeQuery(id+"F7.boolean.opBoolean","INTERSECT",EDGE,{"disambiguationData":[OD(0.0)],"derivedFrom":[makeQuery(id+"F1.opExtrude","SWEPT_FACE",FACE,{"disambiguationData":[OSD([sQuery(id+"F0.wireOp",EDGE,"E0")])]}),makeQuery(id+"F7.opExtrude","SWEPT_FACE",FACE,{"disambiguationData":[OSD([sQuery(id+"F6.wireOp",EDGE,"E411")])]})]});
            var Q159;
            Q159=makeQuery(id+"F10.boolean.opBoolean","INTERSECT",EDGE,{"disambiguationData":[OD(0.0)],"derivedFrom":[makeQuery(id+"F1.opExtrude","SWEPT_FACE",FACE,{"disambiguationData":[OSD([sQuery(id+"F0.wireOp",EDGE,"E0")])]}),makeQuery(id+"F10.opExtrude","SWEPT_FACE",FACE,{"disambiguationData":[OSD([sQuery(id+"F9.wireOp",EDGE,"E635")])]})]});
            var Q160;
            Q160=makeQuery(id+"F10.boolean.opBoolean","INTERSECT",EDGE,{"disambiguationData":[OD(0.0)],"derivedFrom":[makeQuery(id+"F1.opExtrude","SWEPT_FACE",FACE,{"disambiguationData":[OSD([sQuery(id+"F0.wireOp",EDGE,"E0")])]}),makeQuery(id+"F10.opExtrude","SWEPT_FACE",FACE,{"disambiguationData":[OSD([sQuery(id+"F9.wireOp",EDGE,"E634")])]})]});
            var Q161;
            Q161=makeQuery(id+"F10.boolean.opBoolean","INTERSECT",EDGE,{"disambiguationData":[OD(0.0)],"derivedFrom":[makeQuery(id+"F1.opExtrude","SWEPT_FACE",FACE,{"disambiguationData":[OSD([sQuery(id+"F0.wireOp",EDGE,"E0")])]}),makeQuery(id+"F10.opExtrude","SWEPT_FACE",FACE,{"disambiguationData":[OSD([sQuery(id+"F9.wireOp",EDGE,"E633")])]})]});
            var Q162;
            Q162=makeQuery(id+"F10.boolean.opBoolean","INTERSECT",EDGE,{"disambiguationData":[OD(0.0)],"derivedFrom":[makeQuery(id+"F1.opExtrude","SWEPT_FACE",FACE,{"disambiguationData":[OSD([sQuery(id+"F0.wireOp",EDGE,"E0")])]}),makeQuery(id+"F10.opExtrude","SWEPT_FACE",FACE,{"disambiguationData":[OSD([sQuery(id+"F9.wireOp",EDGE,"E638")])]})]});
            var Q163;
            Q163=makeQuery(id+"F10.boolean.opBoolean","INTERSECT",EDGE,{"disambiguationData":[OD(0.0)],"derivedFrom":[makeQuery(id+"F1.opExtrude","SWEPT_FACE",FACE,{"disambiguationData":[OSD([sQuery(id+"F0.wireOp",EDGE,"E0")])]}),makeQuery(id+"F10.opExtrude","SWEPT_FACE",FACE,{"disambiguationData":[OSD([sQuery(id+"F9.wireOp",EDGE,"E637")])]})]});
            var Q164;
            Q164=makeQuery(id+"F10.boolean.opBoolean","INTERSECT",EDGE,{"disambiguationData":[OD(0.0)],"derivedFrom":[makeQuery(id+"F1.opExtrude","SWEPT_FACE",FACE,{"disambiguationData":[OSD([sQuery(id+"F0.wireOp",EDGE,"E0")])]}),makeQuery(id+"F10.opExtrude","SWEPT_FACE",FACE,{"disambiguationData":[OSD([sQuery(id+"F9.wireOp",EDGE,"E636")])]})]});
            var Q165;
            Q165=makeQuery(id+"F10.boolean.opBoolean","INTERSECT",EDGE,{"disambiguationData":[OD(0.0)],"derivedFrom":[makeQuery(id+"F1.opExtrude","SWEPT_FACE",FACE,{"disambiguationData":[OSD([sQuery(id+"F0.wireOp",EDGE,"E0")])]}),makeQuery(id+"F10.opExtrude","SWEPT_FACE",FACE,{"disambiguationData":[OSD([sQuery(id+"F9.wireOp",EDGE,"E638")])]})]});
            var Q166;
            Q166=makeQuery(id+"F10.boolean.opBoolean","INTERSECT",EDGE,{"disambiguationData":[OD(0.0)],"derivedFrom":[makeQuery(id+"F1.opExtrude","SWEPT_FACE",FACE,{"disambiguationData":[OSD([sQuery(id+"F0.wireOp",EDGE,"E0")])]}),makeQuery(id+"F10.opExtrude","SWEPT_FACE",FACE,{"disambiguationData":[OSD([sQuery(id+"F9.wireOp",EDGE,"E620")])]})]});
            var Q167;
            Q167=makeQuery(id+"F10.boolean.opBoolean","INTERSECT",EDGE,{"disambiguationData":[OD(0.0)],"derivedFrom":[makeQuery(id+"F1.opExtrude","SWEPT_FACE",FACE,{"disambiguationData":[OSD([sQuery(id+"F0.wireOp",EDGE,"E0")])]}),makeQuery(id+"F10.opExtrude","SWEPT_FACE",FACE,{"disambiguationData":[OSD([sQuery(id+"F9.wireOp",EDGE,"E615")])]})]});
            var Q168;
            Q168=makeQuery(id+"F10.boolean.opBoolean","INTERSECT",EDGE,{"disambiguationData":[OD(0.0)],"derivedFrom":[makeQuery(id+"F1.opExtrude","SWEPT_FACE",FACE,{"disambiguationData":[OSD([sQuery(id+"F0.wireOp",EDGE,"E0")])]}),makeQuery(id+"F10.opExtrude","SWEPT_FACE",FACE,{"disambiguationData":[OSD([sQuery(id+"F9.wireOp",EDGE,"E616")])]})]});
            var Q169;
            Q169=makeQuery(id+"F10.boolean.opBoolean","INTERSECT",EDGE,{"disambiguationData":[OD(0.0)],"derivedFrom":[makeQuery(id+"F1.opExtrude","SWEPT_FACE",FACE,{"disambiguationData":[OSD([sQuery(id+"F0.wireOp",EDGE,"E0")])]}),makeQuery(id+"F10.opExtrude","SWEPT_FACE",FACE,{"disambiguationData":[OSD([sQuery(id+"F9.wireOp",EDGE,"E617")])]})]});
            var Q170;
            Q170=makeQuery(id+"F10.boolean.opBoolean","INTERSECT",EDGE,{"disambiguationData":[OD(0.0)],"derivedFrom":[makeQuery(id+"F1.opExtrude","SWEPT_FACE",FACE,{"disambiguationData":[OSD([sQuery(id+"F0.wireOp",EDGE,"E0")])]}),makeQuery(id+"F10.opExtrude","SWEPT_FACE",FACE,{"disambiguationData":[OSD([sQuery(id+"F9.wireOp",EDGE,"E618")])]})]});
            var Q171;
            Q171=makeQuery(id+"F10.boolean.opBoolean","INTERSECT",EDGE,{"disambiguationData":[OD(0.0)],"derivedFrom":[makeQuery(id+"F1.opExtrude","SWEPT_FACE",FACE,{"disambiguationData":[OSD([sQuery(id+"F0.wireOp",EDGE,"E0")])]}),makeQuery(id+"F10.opExtrude","SWEPT_FACE",FACE,{"disambiguationData":[OSD([sQuery(id+"F9.wireOp",EDGE,"E619")])]})]});
            var Q172;
            Q172=makeQuery(id+"F7.boolean.opBoolean","INTERSECT",EDGE,{"disambiguationData":[OD(0.0)],"derivedFrom":[makeQuery(id+"F1.opExtrude","SWEPT_FACE",FACE,{"disambiguationData":[OSD([sQuery(id+"F0.wireOp",EDGE,"E0")])]}),makeQuery(id+"F7.opExtrude","SWEPT_FACE",FACE,{"disambiguationData":[OSD([sQuery(id+"F6.wireOp",EDGE,"E376")])]})]});
            var Q173;
            Q173=makeQuery(id+"F7.boolean.opBoolean","INTERSECT",EDGE,{"disambiguationData":[OD(0.0)],"derivedFrom":[makeQuery(id+"F1.opExtrude","SWEPT_FACE",FACE,{"disambiguationData":[OSD([sQuery(id+"F0.wireOp",EDGE,"E0")])]}),makeQuery(id+"F7.opExtrude","SWEPT_FACE",FACE,{"disambiguationData":[OSD([sQuery(id+"F6.wireOp",EDGE,"E377")])]})]});
            var Q174;
            Q174=makeQuery(id+"F7.boolean.opBoolean","INTERSECT",EDGE,{"disambiguationData":[OD(0.0)],"derivedFrom":[makeQuery(id+"F1.opExtrude","SWEPT_FACE",FACE,{"disambiguationData":[OSD([sQuery(id+"F0.wireOp",EDGE,"E0")])]}),makeQuery(id+"F7.opExtrude","SWEPT_FACE",FACE,{"disambiguationData":[OSD([sQuery(id+"F6.wireOp",EDGE,"E378")])]})]});
            var Q175;
            Q175=makeQuery(id+"F7.boolean.opBoolean","INTERSECT",EDGE,{"disambiguationData":[OD(0.0)],"derivedFrom":[makeQuery(id+"F1.opExtrude","SWEPT_FACE",FACE,{"disambiguationData":[OSD([sQuery(id+"F0.wireOp",EDGE,"E0")])]}),makeQuery(id+"F7.opExtrude","SWEPT_FACE",FACE,{"disambiguationData":[OSD([sQuery(id+"F6.wireOp",EDGE,"E379")])]})]});
            var Q176;
            Q176=makeQuery(id+"F7.boolean.opBoolean","INTERSECT",EDGE,{"disambiguationData":[OD(0.0)],"derivedFrom":[makeQuery(id+"F1.opExtrude","SWEPT_FACE",FACE,{"disambiguationData":[OSD([sQuery(id+"F0.wireOp",EDGE,"E0")])]}),makeQuery(id+"F7.opExtrude","SWEPT_FACE",FACE,{"disambiguationData":[OSD([sQuery(id+"F6.wireOp",EDGE,"E374")])]})]});
            var Q177;
            Q177=makeQuery(id+"F7.boolean.opBoolean","INTERSECT",EDGE,{"disambiguationData":[OD(0.0)],"derivedFrom":[makeQuery(id+"F1.opExtrude","SWEPT_FACE",FACE,{"disambiguationData":[OSD([sQuery(id+"F0.wireOp",EDGE,"E0")])]}),makeQuery(id+"F7.opExtrude","SWEPT_FACE",FACE,{"disambiguationData":[OSD([sQuery(id+"F6.wireOp",EDGE,"E375")])]})]});
            var Q178;
            Q178=makeQuery(id+"F7.boolean.opBoolean","INTERSECT",EDGE,{"disambiguationData":[OD(0.0)],"derivedFrom":[makeQuery(id+"F1.opExtrude","SWEPT_FACE",FACE,{"disambiguationData":[OSD([sQuery(id+"F0.wireOp",EDGE,"E0")])]}),makeQuery(id+"F7.opExtrude","SWEPT_FACE",FACE,{"disambiguationData":[OSD([sQuery(id+"F6.wireOp",EDGE,"E394")])]})]});
            var Q179;
            Q179=makeQuery(id+"F7.boolean.opBoolean","INTERSECT",EDGE,{"disambiguationData":[OD(0.0)],"derivedFrom":[makeQuery(id+"F1.opExtrude","SWEPT_FACE",FACE,{"disambiguationData":[OSD([sQuery(id+"F0.wireOp",EDGE,"E0")])]}),makeQuery(id+"F7.opExtrude","SWEPT_FACE",FACE,{"disambiguationData":[OSD([sQuery(id+"F6.wireOp",EDGE,"E395")])]})]});
            var Q180;
            Q180=makeQuery(id+"F7.boolean.opBoolean","INTERSECT",EDGE,{"disambiguationData":[OD(0.0)],"derivedFrom":[makeQuery(id+"F1.opExtrude","SWEPT_FACE",FACE,{"disambiguationData":[OSD([sQuery(id+"F0.wireOp",EDGE,"E0")])]}),makeQuery(id+"F7.opExtrude","SWEPT_FACE",FACE,{"disambiguationData":[OSD([sQuery(id+"F6.wireOp",EDGE,"E396")])]})]});
            var Q181;
            Q181=makeQuery(id+"F7.boolean.opBoolean","INTERSECT",EDGE,{"disambiguationData":[OD(0.0)],"derivedFrom":[makeQuery(id+"F1.opExtrude","SWEPT_FACE",FACE,{"disambiguationData":[OSD([sQuery(id+"F0.wireOp",EDGE,"E0")])]}),makeQuery(id+"F7.opExtrude","SWEPT_FACE",FACE,{"disambiguationData":[OSD([sQuery(id+"F6.wireOp",EDGE,"E397")])]})]});
            var Q182;
            Q182=makeQuery(id+"F7.boolean.opBoolean","INTERSECT",EDGE,{"disambiguationData":[OD(0.0)],"derivedFrom":[makeQuery(id+"F1.opExtrude","SWEPT_FACE",FACE,{"disambiguationData":[OSD([sQuery(id+"F0.wireOp",EDGE,"E0")])]}),makeQuery(id+"F7.opExtrude","SWEPT_FACE",FACE,{"disambiguationData":[OSD([sQuery(id+"F6.wireOp",EDGE,"E392")])]})]});
            var Q183;
            Q183=makeQuery(id+"F7.boolean.opBoolean","INTERSECT",EDGE,{"disambiguationData":[OD(0.0)],"derivedFrom":[makeQuery(id+"F1.opExtrude","SWEPT_FACE",FACE,{"disambiguationData":[OSD([sQuery(id+"F0.wireOp",EDGE,"E0")])]}),makeQuery(id+"F7.opExtrude","SWEPT_FACE",FACE,{"disambiguationData":[OSD([sQuery(id+"F6.wireOp",EDGE,"E393")])]})]});
            var Q184;
            Q184=makeQuery(id+"F7.boolean.opBoolean","INTERSECT",EDGE,{"disambiguationData":[OD(0.0)],"derivedFrom":[makeQuery(id+"F1.opExtrude","SWEPT_FACE",FACE,{"disambiguationData":[OSD([sQuery(id+"F0.wireOp",EDGE,"E0")])]}),makeQuery(id+"F7.opExtrude","SWEPT_FACE",FACE,{"disambiguationData":[OSD([sQuery(id+"F6.wireOp",EDGE,"E358")])]})]});
            var Q185;
            Q185=makeQuery(id+"F7.boolean.opBoolean","INTERSECT",EDGE,{"disambiguationData":[OD(0.0)],"derivedFrom":[makeQuery(id+"F1.opExtrude","SWEPT_FACE",FACE,{"disambiguationData":[OSD([sQuery(id+"F0.wireOp",EDGE,"E0")])]}),makeQuery(id+"F7.opExtrude","SWEPT_FACE",FACE,{"disambiguationData":[OSD([sQuery(id+"F6.wireOp",EDGE,"E359")])]})]});
            var Q186;
            Q186=makeQuery(id+"F7.boolean.opBoolean","INTERSECT",EDGE,{"disambiguationData":[OD(0.0)],"derivedFrom":[makeQuery(id+"F1.opExtrude","SWEPT_FACE",FACE,{"disambiguationData":[OSD([sQuery(id+"F0.wireOp",EDGE,"E0")])]}),makeQuery(id+"F7.opExtrude","SWEPT_FACE",FACE,{"disambiguationData":[OSD([sQuery(id+"F6.wireOp",EDGE,"E360")])]})]});
            var Q187;
            Q187=makeQuery(id+"F7.boolean.opBoolean","INTERSECT",EDGE,{"disambiguationData":[OD(0.0)],"derivedFrom":[makeQuery(id+"F1.opExtrude","SWEPT_FACE",FACE,{"disambiguationData":[OSD([sQuery(id+"F0.wireOp",EDGE,"E0")])]}),makeQuery(id+"F7.opExtrude","SWEPT_FACE",FACE,{"disambiguationData":[OSD([sQuery(id+"F6.wireOp",EDGE,"E361")])]})]});
            var Q188;
            Q188=makeQuery(id+"F7.boolean.opBoolean","INTERSECT",EDGE,{"disambiguationData":[OD(0.0)],"derivedFrom":[makeQuery(id+"F1.opExtrude","SWEPT_FACE",FACE,{"disambiguationData":[OSD([sQuery(id+"F0.wireOp",EDGE,"E0")])]}),makeQuery(id+"F7.opExtrude","SWEPT_FACE",FACE,{"disambiguationData":[OSD([sQuery(id+"F6.wireOp",EDGE,"E356")])]})]});
            var Q189;
            Q189=makeQuery(id+"F7.boolean.opBoolean","INTERSECT",EDGE,{"disambiguationData":[OD(0.0)],"derivedFrom":[makeQuery(id+"F1.opExtrude","SWEPT_FACE",FACE,{"disambiguationData":[OSD([sQuery(id+"F0.wireOp",EDGE,"E0")])]}),makeQuery(id+"F7.opExtrude","SWEPT_FACE",FACE,{"disambiguationData":[OSD([sQuery(id+"F6.wireOp",EDGE,"E357")])]})]});
            var Q190;
            Q190=makeQuery(id+"F10.boolean.opBoolean","INTERSECT",EDGE,{"disambiguationData":[OD(0.0)],"derivedFrom":[makeQuery(id+"F1.opExtrude","SWEPT_FACE",FACE,{"disambiguationData":[OSD([sQuery(id+"F0.wireOp",EDGE,"E0")])]}),makeQuery(id+"F10.opExtrude","SWEPT_FACE",FACE,{"disambiguationData":[OSD([sQuery(id+"F9.wireOp",EDGE,"E602")])]})]});
            var Q191;
            Q191=makeQuery(id+"F10.boolean.opBoolean","INTERSECT",EDGE,{"disambiguationData":[OD(0.0)],"derivedFrom":[makeQuery(id+"F1.opExtrude","SWEPT_FACE",FACE,{"disambiguationData":[OSD([sQuery(id+"F0.wireOp",EDGE,"E0")])]}),makeQuery(id+"F10.opExtrude","SWEPT_FACE",FACE,{"disambiguationData":[OSD([sQuery(id+"F9.wireOp",EDGE,"E601")])]})]});
            var Q192;
            Q192=makeQuery(id+"F10.boolean.opBoolean","INTERSECT",EDGE,{"disambiguationData":[OD(0.0)],"derivedFrom":[makeQuery(id+"F1.opExtrude","SWEPT_FACE",FACE,{"disambiguationData":[OSD([sQuery(id+"F0.wireOp",EDGE,"E0")])]}),makeQuery(id+"F10.opExtrude","SWEPT_FACE",FACE,{"disambiguationData":[OSD([sQuery(id+"F9.wireOp",EDGE,"E600")])]})]});
            var Q193;
            Q193=makeQuery(id+"F10.boolean.opBoolean","INTERSECT",EDGE,{"disambiguationData":[OD(0.0)],"derivedFrom":[makeQuery(id+"F1.opExtrude","SWEPT_FACE",FACE,{"disambiguationData":[OSD([sQuery(id+"F0.wireOp",EDGE,"E0")])]}),makeQuery(id+"F10.opExtrude","SWEPT_FACE",FACE,{"disambiguationData":[OSD([sQuery(id+"F9.wireOp",EDGE,"E599")])]})]});
            var Q194;
            Q194=makeQuery(id+"F10.boolean.opBoolean","INTERSECT",EDGE,{"disambiguationData":[OD(0.0)],"derivedFrom":[makeQuery(id+"F1.opExtrude","SWEPT_FACE",FACE,{"disambiguationData":[OSD([sQuery(id+"F0.wireOp",EDGE,"E0")])]}),makeQuery(id+"F10.opExtrude","SWEPT_FACE",FACE,{"disambiguationData":[OSD([sQuery(id+"F9.wireOp",EDGE,"E598")])]})]});
            var Q195;
            Q195=makeQuery(id+"F10.boolean.opBoolean","INTERSECT",EDGE,{"disambiguationData":[OD(0.0)],"derivedFrom":[makeQuery(id+"F1.opExtrude","SWEPT_FACE",FACE,{"disambiguationData":[OSD([sQuery(id+"F0.wireOp",EDGE,"E0")])]}),makeQuery(id+"F10.opExtrude","SWEPT_FACE",FACE,{"disambiguationData":[OSD([sQuery(id+"F9.wireOp",EDGE,"E597")])]})]});
            var Q196;
            Q196=makeQuery(id+"F7.boolean.opBoolean","INTERSECT",EDGE,{"disambiguationData":[OD(0.0)],"derivedFrom":[makeQuery(id+"F1.opExtrude","SWEPT_FACE",FACE,{"disambiguationData":[OSD([sQuery(id+"F0.wireOp",EDGE,"E0")])]}),makeQuery(id+"F7.opExtrude","SWEPT_FACE",FACE,{"disambiguationData":[OSD([sQuery(id+"F6.wireOp",EDGE,"E340")])]})]});
            var Q197;
            Q197=makeQuery(id+"F7.boolean.opBoolean","INTERSECT",EDGE,{"disambiguationData":[OD(0.0)],"derivedFrom":[makeQuery(id+"F1.opExtrude","SWEPT_FACE",FACE,{"disambiguationData":[OSD([sQuery(id+"F0.wireOp",EDGE,"E0")])]}),makeQuery(id+"F7.opExtrude","SWEPT_FACE",FACE,{"disambiguationData":[OSD([sQuery(id+"F6.wireOp",EDGE,"E341")])]})]});
            var Q198;
            Q198=makeQuery(id+"F7.boolean.opBoolean","INTERSECT",EDGE,{"disambiguationData":[OD(0.0)],"derivedFrom":[makeQuery(id+"F1.opExtrude","SWEPT_FACE",FACE,{"disambiguationData":[OSD([sQuery(id+"F0.wireOp",EDGE,"E0")])]}),makeQuery(id+"F7.opExtrude","SWEPT_FACE",FACE,{"disambiguationData":[OSD([sQuery(id+"F6.wireOp",EDGE,"E342")])]})]});
            var Q199;
            Q199=makeQuery(id+"F7.boolean.opBoolean","INTERSECT",EDGE,{"disambiguationData":[OD(0.0)],"derivedFrom":[makeQuery(id+"F1.opExtrude","SWEPT_FACE",FACE,{"disambiguationData":[OSD([sQuery(id+"F0.wireOp",EDGE,"E0")])]}),makeQuery(id+"F7.opExtrude","SWEPT_FACE",FACE,{"disambiguationData":[OSD([sQuery(id+"F6.wireOp",EDGE,"E343")])]})]});
            var Q200;
            Q200=makeQuery(id+"F7.boolean.opBoolean","INTERSECT",EDGE,{"disambiguationData":[OD(0.0)],"derivedFrom":[makeQuery(id+"F1.opExtrude","SWEPT_FACE",FACE,{"disambiguationData":[OSD([sQuery(id+"F0.wireOp",EDGE,"E0")])]}),makeQuery(id+"F7.opExtrude","SWEPT_FACE",FACE,{"disambiguationData":[OSD([sQuery(id+"F6.wireOp",EDGE,"E338")])]})]});
            var Q201;
            Q201=makeQuery(id+"F7.boolean.opBoolean","INTERSECT",EDGE,{"disambiguationData":[OD(0.0)],"derivedFrom":[makeQuery(id+"F1.opExtrude","SWEPT_FACE",FACE,{"disambiguationData":[OSD([sQuery(id+"F0.wireOp",EDGE,"E0")])]}),makeQuery(id+"F7.opExtrude","SWEPT_FACE",FACE,{"disambiguationData":[OSD([sQuery(id+"F6.wireOp",EDGE,"E339")])]})]});
            var Q202;
            Q202=makeQuery(id+"F10.boolean.opBoolean","INTERSECT",EDGE,{"disambiguationData":[OD(0.0)],"derivedFrom":[makeQuery(id+"F1.opExtrude","SWEPT_FACE",FACE,{"disambiguationData":[OSD([sQuery(id+"F0.wireOp",EDGE,"E0")])]}),makeQuery(id+"F10.opExtrude","SWEPT_FACE",FACE,{"disambiguationData":[OSD([sQuery(id+"F9.wireOp",EDGE,"E583")])]})]});
            var Q203;
            Q203=makeQuery(id+"F10.boolean.opBoolean","INTERSECT",EDGE,{"disambiguationData":[OD(0.0)],"derivedFrom":[makeQuery(id+"F1.opExtrude","SWEPT_FACE",FACE,{"disambiguationData":[OSD([sQuery(id+"F0.wireOp",EDGE,"E0")])]}),makeQuery(id+"F10.opExtrude","SWEPT_FACE",FACE,{"disambiguationData":[OSD([sQuery(id+"F9.wireOp",EDGE,"E582")])]})]});
            var Q204;
            Q204=makeQuery(id+"F10.boolean.opBoolean","INTERSECT",EDGE,{"disambiguationData":[OD(0.0)],"derivedFrom":[makeQuery(id+"F1.opExtrude","SWEPT_FACE",FACE,{"disambiguationData":[OSD([sQuery(id+"F0.wireOp",EDGE,"E0")])]}),makeQuery(id+"F10.opExtrude","SWEPT_FACE",FACE,{"disambiguationData":[OSD([sQuery(id+"F9.wireOp",EDGE,"E581")])]})]});
            var Q205;
            Q205=makeQuery(id+"F10.boolean.opBoolean","INTERSECT",EDGE,{"disambiguationData":[OD(0.0)],"derivedFrom":[makeQuery(id+"F1.opExtrude","SWEPT_FACE",FACE,{"disambiguationData":[OSD([sQuery(id+"F0.wireOp",EDGE,"E0")])]}),makeQuery(id+"F10.opExtrude","SWEPT_FACE",FACE,{"disambiguationData":[OSD([sQuery(id+"F9.wireOp",EDGE,"E580")])]})]});
            var Q206;
            Q206=makeQuery(id+"F10.boolean.opBoolean","INTERSECT",EDGE,{"disambiguationData":[OD(0.0)],"derivedFrom":[makeQuery(id+"F1.opExtrude","SWEPT_FACE",FACE,{"disambiguationData":[OSD([sQuery(id+"F0.wireOp",EDGE,"E0")])]}),makeQuery(id+"F10.opExtrude","SWEPT_FACE",FACE,{"disambiguationData":[OSD([sQuery(id+"F9.wireOp",EDGE,"E579")])]})]});
            var Q207;
            Q207=makeQuery(id+"F10.boolean.opBoolean","INTERSECT",EDGE,{"disambiguationData":[OD(0.0)],"derivedFrom":[makeQuery(id+"F1.opExtrude","SWEPT_FACE",FACE,{"disambiguationData":[OSD([sQuery(id+"F0.wireOp",EDGE,"E0")])]}),makeQuery(id+"F10.opExtrude","SWEPT_FACE",FACE,{"disambiguationData":[OSD([sQuery(id+"F9.wireOp",EDGE,"E584")])]})]});
            var Q208;
            Q208=makeQuery(id+"F10.boolean.opBoolean","INTERSECT",EDGE,{"disambiguationData":[OD(0.0)],"derivedFrom":[makeQuery(id+"F1.opExtrude","SWEPT_FACE",FACE,{"disambiguationData":[OSD([sQuery(id+"F0.wireOp",EDGE,"E0")])]}),makeQuery(id+"F10.opExtrude","SWEPT_FACE",FACE,{"disambiguationData":[OSD([sQuery(id+"F9.wireOp",EDGE,"E563")])]})]});
            var Q209;
            Q209=makeQuery(id+"F10.boolean.opBoolean","INTERSECT",EDGE,{"disambiguationData":[OD(0.0)],"derivedFrom":[makeQuery(id+"F1.opExtrude","SWEPT_FACE",FACE,{"disambiguationData":[OSD([sQuery(id+"F0.wireOp",EDGE,"E0")])]}),makeQuery(id+"F10.opExtrude","SWEPT_FACE",FACE,{"disambiguationData":[OSD([sQuery(id+"F9.wireOp",EDGE,"E564")])]})]});
            var Q210;
            Q210=makeQuery(id+"F10.boolean.opBoolean","INTERSECT",EDGE,{"disambiguationData":[OD(0.0)],"derivedFrom":[makeQuery(id+"F1.opExtrude","SWEPT_FACE",FACE,{"disambiguationData":[OSD([sQuery(id+"F0.wireOp",EDGE,"E0")])]}),makeQuery(id+"F10.opExtrude","SWEPT_FACE",FACE,{"disambiguationData":[OSD([sQuery(id+"F9.wireOp",EDGE,"E565")])]})]});
            var Q211;
            Q211=makeQuery(id+"F10.boolean.opBoolean","INTERSECT",EDGE,{"disambiguationData":[OD(0.0)],"derivedFrom":[makeQuery(id+"F1.opExtrude","SWEPT_FACE",FACE,{"disambiguationData":[OSD([sQuery(id+"F0.wireOp",EDGE,"E0")])]}),makeQuery(id+"F10.opExtrude","SWEPT_FACE",FACE,{"disambiguationData":[OSD([sQuery(id+"F9.wireOp",EDGE,"E566")])]})]});
            var Q212;
            Q212=makeQuery(id+"F10.boolean.opBoolean","INTERSECT",EDGE,{"disambiguationData":[OD(0.0)],"derivedFrom":[makeQuery(id+"F1.opExtrude","SWEPT_FACE",FACE,{"disambiguationData":[OSD([sQuery(id+"F0.wireOp",EDGE,"E0")])]}),makeQuery(id+"F10.opExtrude","SWEPT_FACE",FACE,{"disambiguationData":[OSD([sQuery(id+"F9.wireOp",EDGE,"E561")])]})]});
            var Q213;
            Q213=makeQuery(id+"F10.boolean.opBoolean","INTERSECT",EDGE,{"disambiguationData":[OD(0.0)],"derivedFrom":[makeQuery(id+"F1.opExtrude","SWEPT_FACE",FACE,{"disambiguationData":[OSD([sQuery(id+"F0.wireOp",EDGE,"E0")])]}),makeQuery(id+"F10.opExtrude","SWEPT_FACE",FACE,{"disambiguationData":[OSD([sQuery(id+"F9.wireOp",EDGE,"E562")])]})]});
            var Q214;
            Q214=makeQuery(id+"F7.boolean.opBoolean","INTERSECT",EDGE,{"disambiguationData":[OD(0.0)],"derivedFrom":[makeQuery(id+"F1.opExtrude","SWEPT_FACE",FACE,{"disambiguationData":[OSD([sQuery(id+"F0.wireOp",EDGE,"E0")])]}),makeQuery(id+"F7.opExtrude","SWEPT_FACE",FACE,{"disambiguationData":[OSD([sQuery(id+"F6.wireOp",EDGE,"E322")])]})]});
            var Q215;
            Q215=makeQuery(id+"F7.boolean.opBoolean","INTERSECT",EDGE,{"disambiguationData":[OD(0.0)],"derivedFrom":[makeQuery(id+"F1.opExtrude","SWEPT_FACE",FACE,{"disambiguationData":[OSD([sQuery(id+"F0.wireOp",EDGE,"E0")])]}),makeQuery(id+"F7.opExtrude","SWEPT_FACE",FACE,{"disambiguationData":[OSD([sQuery(id+"F6.wireOp",EDGE,"E323")])]})]});
            var Q216;
            Q216=makeQuery(id+"F7.boolean.opBoolean","INTERSECT",EDGE,{"disambiguationData":[OD(0.0)],"derivedFrom":[makeQuery(id+"F1.opExtrude","SWEPT_FACE",FACE,{"disambiguationData":[OSD([sQuery(id+"F0.wireOp",EDGE,"E0")])]}),makeQuery(id+"F7.opExtrude","SWEPT_FACE",FACE,{"disambiguationData":[OSD([sQuery(id+"F6.wireOp",EDGE,"E324")])]})]});
            var Q217;
            Q217=makeQuery(id+"F7.boolean.opBoolean","INTERSECT",EDGE,{"disambiguationData":[OD(0.0)],"derivedFrom":[makeQuery(id+"F1.opExtrude","SWEPT_FACE",FACE,{"disambiguationData":[OSD([sQuery(id+"F0.wireOp",EDGE,"E0")])]}),makeQuery(id+"F7.opExtrude","SWEPT_FACE",FACE,{"disambiguationData":[OSD([sQuery(id+"F6.wireOp",EDGE,"E325")])]})]});
            var Q218;
            Q218=makeQuery(id+"F7.boolean.opBoolean","INTERSECT",EDGE,{"disambiguationData":[OD(0.0)],"derivedFrom":[makeQuery(id+"F1.opExtrude","SWEPT_FACE",FACE,{"disambiguationData":[OSD([sQuery(id+"F0.wireOp",EDGE,"E0")])]}),makeQuery(id+"F7.opExtrude","SWEPT_FACE",FACE,{"disambiguationData":[OSD([sQuery(id+"F6.wireOp",EDGE,"E320")])]})]});
            var Q219;
            Q219=makeQuery(id+"F7.boolean.opBoolean","INTERSECT",EDGE,{"disambiguationData":[OD(0.0)],"derivedFrom":[makeQuery(id+"F1.opExtrude","SWEPT_FACE",FACE,{"disambiguationData":[OSD([sQuery(id+"F0.wireOp",EDGE,"E0")])]}),makeQuery(id+"F7.opExtrude","SWEPT_FACE",FACE,{"disambiguationData":[OSD([sQuery(id+"F6.wireOp",EDGE,"E321")])]})]});
            var Q220;
            Q220=makeQuery(id+"F10.boolean.opBoolean","INTERSECT",EDGE,{"disambiguationData":[OD(0.0)],"derivedFrom":[makeQuery(id+"F1.opExtrude","SWEPT_FACE",FACE,{"disambiguationData":[OSD([sQuery(id+"F0.wireOp",EDGE,"E0")])]}),makeQuery(id+"F10.opExtrude","SWEPT_FACE",FACE,{"disambiguationData":[OSD([sQuery(id+"F9.wireOp",EDGE,"E545")])]})]});
            var Q221;
            Q221=makeQuery(id+"F10.boolean.opBoolean","INTERSECT",EDGE,{"disambiguationData":[OD(0.0)],"derivedFrom":[makeQuery(id+"F1.opExtrude","SWEPT_FACE",FACE,{"disambiguationData":[OSD([sQuery(id+"F0.wireOp",EDGE,"E0")])]}),makeQuery(id+"F10.opExtrude","SWEPT_FACE",FACE,{"disambiguationData":[OSD([sQuery(id+"F9.wireOp",EDGE,"E546")])]})]});
            var Q222;
            Q222=makeQuery(id+"F10.boolean.opBoolean","INTERSECT",EDGE,{"disambiguationData":[OD(0.0)],"derivedFrom":[makeQuery(id+"F1.opExtrude","SWEPT_FACE",FACE,{"disambiguationData":[OSD([sQuery(id+"F0.wireOp",EDGE,"E0")])]}),makeQuery(id+"F10.opExtrude","SWEPT_FACE",FACE,{"disambiguationData":[OSD([sQuery(id+"F9.wireOp",EDGE,"E547")])]})]});
            var Q223;
            Q223=makeQuery(id+"F10.boolean.opBoolean","INTERSECT",EDGE,{"disambiguationData":[OD(0.0)],"derivedFrom":[makeQuery(id+"F1.opExtrude","SWEPT_FACE",FACE,{"disambiguationData":[OSD([sQuery(id+"F0.wireOp",EDGE,"E0")])]}),makeQuery(id+"F10.opExtrude","SWEPT_FACE",FACE,{"disambiguationData":[OSD([sQuery(id+"F9.wireOp",EDGE,"E548")])]})]});
            var Q224;
            Q224=makeQuery(id+"F10.boolean.opBoolean","INTERSECT",EDGE,{"disambiguationData":[OD(0.0)],"derivedFrom":[makeQuery(id+"F1.opExtrude","SWEPT_FACE",FACE,{"disambiguationData":[OSD([sQuery(id+"F0.wireOp",EDGE,"E0")])]}),makeQuery(id+"F10.opExtrude","SWEPT_FACE",FACE,{"disambiguationData":[OSD([sQuery(id+"F9.wireOp",EDGE,"E543")])]})]});
            var Q225;
            Q225=makeQuery(id+"F10.boolean.opBoolean","INTERSECT",EDGE,{"disambiguationData":[OD(0.0)],"derivedFrom":[makeQuery(id+"F1.opExtrude","SWEPT_FACE",FACE,{"disambiguationData":[OSD([sQuery(id+"F0.wireOp",EDGE,"E0")])]}),makeQuery(id+"F10.opExtrude","SWEPT_FACE",FACE,{"disambiguationData":[OSD([sQuery(id+"F9.wireOp",EDGE,"E544")])]})]});
            var Q226;
            Q226=makeQuery(id+"F7.boolean.opBoolean","INTERSECT",EDGE,{"disambiguationData":[OD(0.0)],"derivedFrom":[makeQuery(id+"F1.opExtrude","SWEPT_FACE",FACE,{"disambiguationData":[OSD([sQuery(id+"F0.wireOp",EDGE,"E0")])]}),makeQuery(id+"F7.opExtrude","SWEPT_FACE",FACE,{"disambiguationData":[OSD([sQuery(id+"F6.wireOp",EDGE,"E304")])]})]});
            var Q227;
            Q227=makeQuery(id+"F7.boolean.opBoolean","INTERSECT",EDGE,{"disambiguationData":[OD(0.0)],"derivedFrom":[makeQuery(id+"F1.opExtrude","SWEPT_FACE",FACE,{"disambiguationData":[OSD([sQuery(id+"F0.wireOp",EDGE,"E0")])]}),makeQuery(id+"F7.opExtrude","SWEPT_FACE",FACE,{"disambiguationData":[OSD([sQuery(id+"F6.wireOp",EDGE,"E305")])]})]});
            var Q228;
            Q228=makeQuery(id+"F7.boolean.opBoolean","INTERSECT",EDGE,{"disambiguationData":[OD(0.0)],"derivedFrom":[makeQuery(id+"F1.opExtrude","SWEPT_FACE",FACE,{"disambiguationData":[OSD([sQuery(id+"F0.wireOp",EDGE,"E0")])]}),makeQuery(id+"F7.opExtrude","SWEPT_FACE",FACE,{"disambiguationData":[OSD([sQuery(id+"F6.wireOp",EDGE,"E306")])]})]});
            var Q229;
            Q229=makeQuery(id+"F7.boolean.opBoolean","INTERSECT",EDGE,{"disambiguationData":[OD(0.0)],"derivedFrom":[makeQuery(id+"F1.opExtrude","SWEPT_FACE",FACE,{"disambiguationData":[OSD([sQuery(id+"F0.wireOp",EDGE,"E0")])]}),makeQuery(id+"F7.opExtrude","SWEPT_FACE",FACE,{"disambiguationData":[OSD([sQuery(id+"F6.wireOp",EDGE,"E307")])]})]});
            var Q230;
            Q230=makeQuery(id+"F7.boolean.opBoolean","INTERSECT",EDGE,{"disambiguationData":[OD(0.0)],"derivedFrom":[makeQuery(id+"F1.opExtrude","SWEPT_FACE",FACE,{"disambiguationData":[OSD([sQuery(id+"F0.wireOp",EDGE,"E0")])]}),makeQuery(id+"F7.opExtrude","SWEPT_FACE",FACE,{"disambiguationData":[OSD([sQuery(id+"F6.wireOp",EDGE,"E302")])]})]});
            var Q231;
            Q231=makeQuery(id+"F7.boolean.opBoolean","INTERSECT",EDGE,{"disambiguationData":[OD(0.0)],"derivedFrom":[makeQuery(id+"F1.opExtrude","SWEPT_FACE",FACE,{"disambiguationData":[OSD([sQuery(id+"F0.wireOp",EDGE,"E0")])]}),makeQuery(id+"F7.opExtrude","SWEPT_FACE",FACE,{"disambiguationData":[OSD([sQuery(id+"F6.wireOp",EDGE,"E303")])]})]});
            var Q232;
            Q232=makeQuery(id+"F10.boolean.opBoolean","INTERSECT",EDGE,{"disambiguationData":[OD(0.0)],"derivedFrom":[makeQuery(id+"F1.opExtrude","SWEPT_FACE",FACE,{"disambiguationData":[OSD([sQuery(id+"F0.wireOp",EDGE,"E0")])]}),makeQuery(id+"F10.opExtrude","SWEPT_FACE",FACE,{"disambiguationData":[OSD([sQuery(id+"F9.wireOp",EDGE,"E530")])]})]});
            var Q233;
            Q233=makeQuery(id+"F10.boolean.opBoolean","INTERSECT",EDGE,{"disambiguationData":[OD(0.0)],"derivedFrom":[makeQuery(id+"F1.opExtrude","SWEPT_FACE",FACE,{"disambiguationData":[OSD([sQuery(id+"F0.wireOp",EDGE,"E0")])]}),makeQuery(id+"F10.opExtrude","SWEPT_FACE",FACE,{"disambiguationData":[OSD([sQuery(id+"F9.wireOp",EDGE,"E529")])]})]});
            var Q234;
            Q234=makeQuery(id+"F10.boolean.opBoolean","INTERSECT",EDGE,{"disambiguationData":[OD(0.0)],"derivedFrom":[makeQuery(id+"F1.opExtrude","SWEPT_FACE",FACE,{"disambiguationData":[OSD([sQuery(id+"F0.wireOp",EDGE,"E0")])]}),makeQuery(id+"F10.opExtrude","SWEPT_FACE",FACE,{"disambiguationData":[OSD([sQuery(id+"F9.wireOp",EDGE,"E528")])]})]});
            var Q235;
            Q235=makeQuery(id+"F10.boolean.opBoolean","INTERSECT",EDGE,{"disambiguationData":[OD(0.0)],"derivedFrom":[makeQuery(id+"F1.opExtrude","SWEPT_FACE",FACE,{"disambiguationData":[OSD([sQuery(id+"F0.wireOp",EDGE,"E0")])]}),makeQuery(id+"F10.opExtrude","SWEPT_FACE",FACE,{"disambiguationData":[OSD([sQuery(id+"F9.wireOp",EDGE,"E527")])]})]});
            var Q236;
            Q236=makeQuery(id+"F10.boolean.opBoolean","INTERSECT",EDGE,{"disambiguationData":[OD(0.0)],"derivedFrom":[makeQuery(id+"F1.opExtrude","SWEPT_FACE",FACE,{"disambiguationData":[OSD([sQuery(id+"F0.wireOp",EDGE,"E0")])]}),makeQuery(id+"F10.opExtrude","SWEPT_FACE",FACE,{"disambiguationData":[OSD([sQuery(id+"F9.wireOp",EDGE,"E526")])]})]});
            var Q237;
            Q237=makeQuery(id+"F10.boolean.opBoolean","INTERSECT",EDGE,{"disambiguationData":[OD(0.0)],"derivedFrom":[makeQuery(id+"F1.opExtrude","SWEPT_FACE",FACE,{"disambiguationData":[OSD([sQuery(id+"F0.wireOp",EDGE,"E0")])]}),makeQuery(id+"F10.opExtrude","SWEPT_FACE",FACE,{"disambiguationData":[OSD([sQuery(id+"F9.wireOp",EDGE,"E525")])]})]});
            var Q238;
            Q238=makeQuery(id+"F7.boolean.opBoolean","INTERSECT",EDGE,{"disambiguationData":[OD(0.0)],"derivedFrom":[makeQuery(id+"F1.opExtrude","SWEPT_FACE",FACE,{"disambiguationData":[OSD([sQuery(id+"F0.wireOp",EDGE,"E0")])]}),makeQuery(id+"F7.opExtrude","SWEPT_FACE",FACE,{"disambiguationData":[OSD([sQuery(id+"F6.wireOp",EDGE,"E286")])]})]});
            var Q239;
            Q239=makeQuery(id+"F7.boolean.opBoolean","INTERSECT",EDGE,{"disambiguationData":[OD(0.0)],"derivedFrom":[makeQuery(id+"F1.opExtrude","SWEPT_FACE",FACE,{"disambiguationData":[OSD([sQuery(id+"F0.wireOp",EDGE,"E0")])]}),makeQuery(id+"F7.opExtrude","SWEPT_FACE",FACE,{"disambiguationData":[OSD([sQuery(id+"F6.wireOp",EDGE,"E287")])]})]});
            var Q240;
            Q240=makeQuery(id+"F7.boolean.opBoolean","INTERSECT",EDGE,{"disambiguationData":[OD(0.0)],"derivedFrom":[makeQuery(id+"F1.opExtrude","SWEPT_FACE",FACE,{"disambiguationData":[OSD([sQuery(id+"F0.wireOp",EDGE,"E0")])]}),makeQuery(id+"F7.opExtrude","SWEPT_FACE",FACE,{"disambiguationData":[OSD([sQuery(id+"F6.wireOp",EDGE,"E288")])]})]});
            var Q241;
            Q241=makeQuery(id+"F7.boolean.opBoolean","INTERSECT",EDGE,{"disambiguationData":[OD(0.0)],"derivedFrom":[makeQuery(id+"F1.opExtrude","SWEPT_FACE",FACE,{"disambiguationData":[OSD([sQuery(id+"F0.wireOp",EDGE,"E0")])]}),makeQuery(id+"F7.opExtrude","SWEPT_FACE",FACE,{"disambiguationData":[OSD([sQuery(id+"F6.wireOp",EDGE,"E289")])]})]});
            var Q242;
            Q242=makeQuery(id+"F7.boolean.opBoolean","INTERSECT",EDGE,{"disambiguationData":[OD(0.0)],"derivedFrom":[makeQuery(id+"F1.opExtrude","SWEPT_FACE",FACE,{"disambiguationData":[OSD([sQuery(id+"F0.wireOp",EDGE,"E0")])]}),makeQuery(id+"F7.opExtrude","SWEPT_FACE",FACE,{"disambiguationData":[OSD([sQuery(id+"F6.wireOp",EDGE,"E284")])]})]});
            var Q243;
            Q243=makeQuery(id+"F7.boolean.opBoolean","INTERSECT",EDGE,{"disambiguationData":[OD(0.0)],"derivedFrom":[makeQuery(id+"F1.opExtrude","SWEPT_FACE",FACE,{"disambiguationData":[OSD([sQuery(id+"F0.wireOp",EDGE,"E0")])]}),makeQuery(id+"F7.opExtrude","SWEPT_FACE",FACE,{"disambiguationData":[OSD([sQuery(id+"F6.wireOp",EDGE,"E285")])]})]});
            var Q244;
            Q244=makeQuery(id+"F7.boolean.opBoolean","INTERSECT",EDGE,{"disambiguationData":[OD(0.0)],"derivedFrom":[makeQuery(id+"F1.opExtrude","SWEPT_FACE",FACE,{"disambiguationData":[OSD([sQuery(id+"F0.wireOp",EDGE,"E0")])]}),makeQuery(id+"F7.opExtrude","SWEPT_FACE",FACE,{"disambiguationData":[OSD([sQuery(id+"F6.wireOp",EDGE,"E288")])]})]});
            var Q245;
            Q245=makeQuery(id+"F7.boolean.opBoolean","INTERSECT",EDGE,{"disambiguationData":[OD(0.0)],"derivedFrom":[makeQuery(id+"F1.opExtrude","SWEPT_FACE",FACE,{"disambiguationData":[OSD([sQuery(id+"F0.wireOp",EDGE,"E0")])]}),makeQuery(id+"F7.opExtrude","SWEPT_FACE",FACE,{"disambiguationData":[OSD([sQuery(id+"F6.wireOp",EDGE,"E270")])]})]});
            var Q246;
            Q246=makeQuery(id+"F7.boolean.opBoolean","INTERSECT",EDGE,{"disambiguationData":[OD(0.0)],"derivedFrom":[makeQuery(id+"F1.opExtrude","SWEPT_FACE",FACE,{"disambiguationData":[OSD([sQuery(id+"F0.wireOp",EDGE,"E0")])]}),makeQuery(id+"F7.opExtrude","SWEPT_FACE",FACE,{"disambiguationData":[OSD([sQuery(id+"F6.wireOp",EDGE,"E269")])]})]});
            var Q247;
            Q247=makeQuery(id+"F7.boolean.opBoolean","INTERSECT",EDGE,{"disambiguationData":[OD(0.0)],"derivedFrom":[makeQuery(id+"F1.opExtrude","SWEPT_FACE",FACE,{"disambiguationData":[OSD([sQuery(id+"F0.wireOp",EDGE,"E0")])]}),makeQuery(id+"F7.opExtrude","SWEPT_FACE",FACE,{"disambiguationData":[OSD([sQuery(id+"F6.wireOp",EDGE,"E268")])]})]});
            var Q248;
            Q248=makeQuery(id+"F7.boolean.opBoolean","INTERSECT",EDGE,{"disambiguationData":[OD(0.0)],"derivedFrom":[makeQuery(id+"F1.opExtrude","SWEPT_FACE",FACE,{"disambiguationData":[OSD([sQuery(id+"F0.wireOp",EDGE,"E0")])]}),makeQuery(id+"F7.opExtrude","SWEPT_FACE",FACE,{"disambiguationData":[OSD([sQuery(id+"F6.wireOp",EDGE,"E267")])]})]});
            var Q249;
            Q249=makeQuery(id+"F7.boolean.opBoolean","INTERSECT",EDGE,{"disambiguationData":[OD(0.0)],"derivedFrom":[makeQuery(id+"F1.opExtrude","SWEPT_FACE",FACE,{"disambiguationData":[OSD([sQuery(id+"F0.wireOp",EDGE,"E0")])]}),makeQuery(id+"F7.opExtrude","SWEPT_FACE",FACE,{"disambiguationData":[OSD([sQuery(id+"F6.wireOp",EDGE,"E266")])]})]});
            var Q250;
            Q250=makeQuery(id+"F7.boolean.opBoolean","INTERSECT",EDGE,{"disambiguationData":[OD(0.0)],"derivedFrom":[makeQuery(id+"F1.opExtrude","SWEPT_FACE",FACE,{"disambiguationData":[OSD([sQuery(id+"F0.wireOp",EDGE,"E0")])]}),makeQuery(id+"F7.opExtrude","SWEPT_FACE",FACE,{"disambiguationData":[OSD([sQuery(id+"F6.wireOp",EDGE,"E271")])]})]});
            var Q251;
            Q251=makeQuery(id+"F10.boolean.opBoolean","INTERSECT",EDGE,{"disambiguationData":[OD(0.0)],"derivedFrom":[makeQuery(id+"F1.opExtrude","SWEPT_FACE",FACE,{"disambiguationData":[OSD([sQuery(id+"F0.wireOp",EDGE,"E0")])]}),makeQuery(id+"F10.opExtrude","SWEPT_FACE",FACE,{"disambiguationData":[OSD([sQuery(id+"F9.wireOp",EDGE,"E512")])]})]});
            var Q252;
            Q252=makeQuery(id+"F10.boolean.opBoolean","INTERSECT",EDGE,{"disambiguationData":[OD(0.0)],"derivedFrom":[makeQuery(id+"F1.opExtrude","SWEPT_FACE",FACE,{"disambiguationData":[OSD([sQuery(id+"F0.wireOp",EDGE,"E0")])]}),makeQuery(id+"F10.opExtrude","SWEPT_FACE",FACE,{"disambiguationData":[OSD([sQuery(id+"F9.wireOp",EDGE,"E756")])]})]});
            var Q253;
            Q253=makeQuery(id+"F10.boolean.opBoolean","INTERSECT",EDGE,{"disambiguationData":[OD(0.0)],"derivedFrom":[makeQuery(id+"F1.opExtrude","SWEPT_FACE",FACE,{"disambiguationData":[OSD([sQuery(id+"F0.wireOp",EDGE,"E0")])]}),makeQuery(id+"F10.opExtrude","SWEPT_FACE",FACE,{"disambiguationData":[OSD([sQuery(id+"F9.wireOp",EDGE,"E754"),sQuery(id+"F9.wireOp",EDGE,"E755")])]})]});
            var Q254;
            Q254=makeQuery(id+"F10.boolean.opBoolean","INTERSECT",EDGE,{"disambiguationData":[OD(0.0)],"derivedFrom":[makeQuery(id+"F1.opExtrude","SWEPT_FACE",FACE,{"disambiguationData":[OSD([sQuery(id+"F0.wireOp",EDGE,"E0")])]}),makeQuery(id+"F10.opExtrude","SWEPT_FACE",FACE,{"disambiguationData":[OSD([sQuery(id+"F9.wireOp",EDGE,"E757")])]})]});
            var Q255;
            Q255=makeQuery(id+"F12.boolean.opBoolean","INTERSECT",EDGE,{"derivedFrom":[makeQuery(id+"F1.opExtrude","SWEPT_FACE",FACE,{"disambiguationData":[OSD([sQuery(id+"F0.wireOp",EDGE,"E0")])]}),makeQuery(id+"F12.opExtrude","SWEPT_FACE",FACE,{"disambiguationData":[OSD([sQuery(id+"F11.wireOp",EDGE,"E1011"),sQuery(id+"F11.wireOp",EDGE,"E1012")])]})]});
            var Q256;
            Q256=makeQuery(id+"F12.boolean.opBoolean","INTERSECT",EDGE,{"derivedFrom":[makeQuery(id+"F1.opExtrude","SWEPT_FACE",FACE,{"disambiguationData":[OSD([sQuery(id+"F0.wireOp",EDGE,"E0")])]}),makeQuery(id+"F12.opExtrude","SWEPT_FACE",FACE,{"disambiguationData":[OSD([sQuery(id+"F11.wireOp",EDGE,"E1013")])]})]});
            var Q257;
            Q257=makeQuery(id+"F12.boolean.opBoolean","INTERSECT",EDGE,{"derivedFrom":[makeQuery(id+"F1.opExtrude","SWEPT_FACE",FACE,{"disambiguationData":[OSD([sQuery(id+"F0.wireOp",EDGE,"E0")])]}),makeQuery(id+"F12.opExtrude","SWEPT_FACE",FACE,{"disambiguationData":[OSD([sQuery(id+"F11.wireOp",EDGE,"E769")])]})]});
            var Q258;
            Q258=makeQuery(id+"F12.boolean.opBoolean","INTERSECT",EDGE,{"derivedFrom":[makeQuery(id+"F1.opExtrude","SWEPT_FACE",FACE,{"disambiguationData":[OSD([sQuery(id+"F0.wireOp",EDGE,"E0")])]}),makeQuery(id+"F12.opExtrude","SWEPT_FACE",FACE,{"disambiguationData":[OSD([sQuery(id+"F11.wireOp",EDGE,"E1014")])]})]});
            var Q259;
            Q259=makeQuery(id+"F5.boolean.opBoolean","INTERSECT",EDGE,{"disambiguationData":[OD(1.0)],"derivedFrom":[makeQuery(id+"F1.opExtrude","SWEPT_FACE",FACE,{"disambiguationData":[OSD([sQuery(id+"F0.wireOp",EDGE,"E0")])]}),makeQuery(id+"F5.opExtrude","SWEPT_FACE",FACE,{"disambiguationData":[OSD([sQuery(id+"F4.wireOp",EDGE,"E15")])]})]});
            var Q260;
            Q260=makeQuery(id+"F5.boolean.opBoolean","INTERSECT",EDGE,{"disambiguationData":[OD(1.0)],"derivedFrom":[makeQuery(id+"F1.opExtrude","SWEPT_FACE",FACE,{"disambiguationData":[OSD([sQuery(id+"F0.wireOp",EDGE,"E0")])]}),makeQuery(id+"F5.opExtrude","SWEPT_FACE",FACE,{"disambiguationData":[OSD([sQuery(id+"F4.wireOp",EDGE,"E16")])]})]});
            var Q261;
            Q261=makeQuery(id+"F5.boolean.opBoolean","INTERSECT",EDGE,{"disambiguationData":[OD(1.0)],"derivedFrom":[makeQuery(id+"F1.opExtrude","SWEPT_FACE",FACE,{"disambiguationData":[OSD([sQuery(id+"F0.wireOp",EDGE,"E0")])]}),makeQuery(id+"F5.opExtrude","SWEPT_FACE",FACE,{"disambiguationData":[OSD([sQuery(id+"F4.wireOp",EDGE,"E17")])]})]});
            var Q262;
            Q262=makeQuery(id+"F5.boolean.opBoolean","INTERSECT",EDGE,{"disambiguationData":[OD(1.0)],"derivedFrom":[makeQuery(id+"F1.opExtrude","SWEPT_FACE",FACE,{"disambiguationData":[OSD([sQuery(id+"F0.wireOp",EDGE,"E0")])]}),makeQuery(id+"F5.opExtrude","SWEPT_FACE",FACE,{"disambiguationData":[OSD([sQuery(id+"F4.wireOp",EDGE,"E18")])]})]});
            var Q263;
            Q263=makeQuery(id+"F5.boolean.opBoolean","INTERSECT",EDGE,{"disambiguationData":[OD(1.0)],"derivedFrom":[makeQuery(id+"F1.opExtrude","SWEPT_FACE",FACE,{"disambiguationData":[OSD([sQuery(id+"F0.wireOp",EDGE,"E0")])]}),makeQuery(id+"F5.opExtrude","SWEPT_FACE",FACE,{"disambiguationData":[OSD([sQuery(id+"F4.wireOp",EDGE,"E19")])]})]});
            var Q264;
            Q264=makeQuery(id+"F5.boolean.opBoolean","INTERSECT",EDGE,{"disambiguationData":[OD(1.0)],"derivedFrom":[makeQuery(id+"F1.opExtrude","SWEPT_FACE",FACE,{"disambiguationData":[OSD([sQuery(id+"F0.wireOp",EDGE,"E0")])]}),makeQuery(id+"F5.opExtrude","SWEPT_FACE",FACE,{"disambiguationData":[OSD([sQuery(id+"F4.wireOp",EDGE,"E14")])]})]});
            var Q265;
            Q265=makeQuery(id+"F12.boolean.opBoolean","INTERSECT",EDGE,{"derivedFrom":[makeQuery(id+"F1.opExtrude","SWEPT_FACE",FACE,{"disambiguationData":[OSD([sQuery(id+"F0.wireOp",EDGE,"E0")])]}),makeQuery(id+"F12.opExtrude","SWEPT_FACE",FACE,{"disambiguationData":[OSD([sQuery(id+"F11.wireOp",EDGE,"E784")])]})]});
            var Q266;
            Q266=makeQuery(id+"F12.boolean.opBoolean","INTERSECT",EDGE,{"derivedFrom":[makeQuery(id+"F1.opExtrude","SWEPT_FACE",FACE,{"disambiguationData":[OSD([sQuery(id+"F0.wireOp",EDGE,"E0")])]}),makeQuery(id+"F12.opExtrude","SWEPT_FACE",FACE,{"disambiguationData":[OSD([sQuery(id+"F11.wireOp",EDGE,"E785")])]})]});
            var Q267;
            Q267=makeQuery(id+"F12.boolean.opBoolean","INTERSECT",EDGE,{"derivedFrom":[makeQuery(id+"F1.opExtrude","SWEPT_FACE",FACE,{"disambiguationData":[OSD([sQuery(id+"F0.wireOp",EDGE,"E0")])]}),makeQuery(id+"F12.opExtrude","SWEPT_FACE",FACE,{"disambiguationData":[OSD([sQuery(id+"F11.wireOp",EDGE,"E786")])]})]});
            var Q268;
            Q268=makeQuery(id+"F12.boolean.opBoolean","INTERSECT",EDGE,{"derivedFrom":[makeQuery(id+"F1.opExtrude","SWEPT_FACE",FACE,{"disambiguationData":[OSD([sQuery(id+"F0.wireOp",EDGE,"E0")])]}),makeQuery(id+"F12.opExtrude","SWEPT_FACE",FACE,{"disambiguationData":[OSD([sQuery(id+"F11.wireOp",EDGE,"E787")])]})]});
            var Q269;
            Q269=makeQuery(id+"F12.boolean.opBoolean","INTERSECT",EDGE,{"derivedFrom":[makeQuery(id+"F1.opExtrude","SWEPT_FACE",FACE,{"disambiguationData":[OSD([sQuery(id+"F0.wireOp",EDGE,"E0")])]}),makeQuery(id+"F12.opExtrude","SWEPT_FACE",FACE,{"disambiguationData":[OSD([sQuery(id+"F11.wireOp",EDGE,"E782")])]})]});
            var Q270;
            Q270=makeQuery(id+"F12.boolean.opBoolean","INTERSECT",EDGE,{"derivedFrom":[makeQuery(id+"F1.opExtrude","SWEPT_FACE",FACE,{"disambiguationData":[OSD([sQuery(id+"F0.wireOp",EDGE,"E0")])]}),makeQuery(id+"F12.opExtrude","SWEPT_FACE",FACE,{"disambiguationData":[OSD([sQuery(id+"F11.wireOp",EDGE,"E783")])]})]});
            var Q271;
            Q271=makeQuery(id+"F12.boolean.opBoolean","INTERSECT",EDGE,{"derivedFrom":[makeQuery(id+"F1.opExtrude","SWEPT_FACE",FACE,{"disambiguationData":[OSD([sQuery(id+"F0.wireOp",EDGE,"E0")])]}),makeQuery(id+"F12.opExtrude","SWEPT_FACE",FACE,{"disambiguationData":[OSD([sQuery(id+"F11.wireOp",EDGE,"E786")])]})]});
            var Q272;
            Q272=makeQuery(id+"F12.boolean.opBoolean","INTERSECT",EDGE,{"derivedFrom":[makeQuery(id+"F1.opExtrude","SWEPT_FACE",FACE,{"disambiguationData":[OSD([sQuery(id+"F0.wireOp",EDGE,"E0")])]}),makeQuery(id+"F12.opExtrude","SWEPT_FACE",FACE,{"disambiguationData":[OSD([sQuery(id+"F11.wireOp",EDGE,"E804")])]})]});
            var Q273;
            Q273=makeQuery(id+"F12.boolean.opBoolean","INTERSECT",EDGE,{"derivedFrom":[makeQuery(id+"F1.opExtrude","SWEPT_FACE",FACE,{"disambiguationData":[OSD([sQuery(id+"F0.wireOp",EDGE,"E0")])]}),makeQuery(id+"F12.opExtrude","SWEPT_FACE",FACE,{"disambiguationData":[OSD([sQuery(id+"F11.wireOp",EDGE,"E805")])]})]});
            var Q274;
            Q274=makeQuery(id+"F12.boolean.opBoolean","INTERSECT",EDGE,{"derivedFrom":[makeQuery(id+"F1.opExtrude","SWEPT_FACE",FACE,{"disambiguationData":[OSD([sQuery(id+"F0.wireOp",EDGE,"E0")])]}),makeQuery(id+"F12.opExtrude","SWEPT_FACE",FACE,{"disambiguationData":[OSD([sQuery(id+"F11.wireOp",EDGE,"E800")])]})]});
            var Q275;
            Q275=makeQuery(id+"F12.boolean.opBoolean","INTERSECT",EDGE,{"derivedFrom":[makeQuery(id+"F1.opExtrude","SWEPT_FACE",FACE,{"disambiguationData":[OSD([sQuery(id+"F0.wireOp",EDGE,"E0")])]}),makeQuery(id+"F12.opExtrude","SWEPT_FACE",FACE,{"disambiguationData":[OSD([sQuery(id+"F11.wireOp",EDGE,"E801")])]})]});
            var Q276;
            Q276=makeQuery(id+"F12.boolean.opBoolean","INTERSECT",EDGE,{"derivedFrom":[makeQuery(id+"F1.opExtrude","SWEPT_FACE",FACE,{"disambiguationData":[OSD([sQuery(id+"F0.wireOp",EDGE,"E0")])]}),makeQuery(id+"F12.opExtrude","SWEPT_FACE",FACE,{"disambiguationData":[OSD([sQuery(id+"F11.wireOp",EDGE,"E802")])]})]});
            var Q277;
            Q277=makeQuery(id+"F12.boolean.opBoolean","INTERSECT",EDGE,{"derivedFrom":[makeQuery(id+"F1.opExtrude","SWEPT_FACE",FACE,{"disambiguationData":[OSD([sQuery(id+"F0.wireOp",EDGE,"E0")])]}),makeQuery(id+"F12.opExtrude","SWEPT_FACE",FACE,{"disambiguationData":[OSD([sQuery(id+"F11.wireOp",EDGE,"E803")])]})]});
            var Q278;
            Q278=makeQuery(id+"F12.boolean.opBoolean","INTERSECT",EDGE,{"derivedFrom":[makeQuery(id+"F1.opExtrude","SWEPT_FACE",FACE,{"disambiguationData":[OSD([sQuery(id+"F0.wireOp",EDGE,"E0")])]}),makeQuery(id+"F12.opExtrude","SWEPT_FACE",FACE,{"disambiguationData":[OSD([sQuery(id+"F11.wireOp",EDGE,"E838")])]})]});
            var Q279;
            Q279=makeQuery(id+"F12.boolean.opBoolean","INTERSECT",EDGE,{"derivedFrom":[makeQuery(id+"F1.opExtrude","SWEPT_FACE",FACE,{"disambiguationData":[OSD([sQuery(id+"F0.wireOp",EDGE,"E0")])]}),makeQuery(id+"F12.opExtrude","SWEPT_FACE",FACE,{"disambiguationData":[OSD([sQuery(id+"F11.wireOp",EDGE,"E839")])]})]});
            var Q280;
            Q280=makeQuery(id+"F12.boolean.opBoolean","INTERSECT",EDGE,{"derivedFrom":[makeQuery(id+"F1.opExtrude","SWEPT_FACE",FACE,{"disambiguationData":[OSD([sQuery(id+"F0.wireOp",EDGE,"E0")])]}),makeQuery(id+"F12.opExtrude","SWEPT_FACE",FACE,{"disambiguationData":[OSD([sQuery(id+"F11.wireOp",EDGE,"E840")])]})]});
            var Q281;
            Q281=makeQuery(id+"F12.boolean.opBoolean","INTERSECT",EDGE,{"derivedFrom":[makeQuery(id+"F1.opExtrude","SWEPT_FACE",FACE,{"disambiguationData":[OSD([sQuery(id+"F0.wireOp",EDGE,"E0")])]}),makeQuery(id+"F12.opExtrude","SWEPT_FACE",FACE,{"disambiguationData":[OSD([sQuery(id+"F11.wireOp",EDGE,"E841")])]})]});
            var Q282;
            Q282=makeQuery(id+"F12.boolean.opBoolean","INTERSECT",EDGE,{"derivedFrom":[makeQuery(id+"F1.opExtrude","SWEPT_FACE",FACE,{"disambiguationData":[OSD([sQuery(id+"F0.wireOp",EDGE,"E0")])]}),makeQuery(id+"F12.opExtrude","SWEPT_FACE",FACE,{"disambiguationData":[OSD([sQuery(id+"F11.wireOp",EDGE,"E836")])]})]});
            var Q283;
            Q283=makeQuery(id+"F12.boolean.opBoolean","INTERSECT",EDGE,{"derivedFrom":[makeQuery(id+"F1.opExtrude","SWEPT_FACE",FACE,{"disambiguationData":[OSD([sQuery(id+"F0.wireOp",EDGE,"E0")])]}),makeQuery(id+"F12.opExtrude","SWEPT_FACE",FACE,{"disambiguationData":[OSD([sQuery(id+"F11.wireOp",EDGE,"E837")])]})]});
            var Q284;
            Q284=makeQuery(id+"F12.boolean.opBoolean","INTERSECT",EDGE,{"derivedFrom":[makeQuery(id+"F1.opExtrude","SWEPT_FACE",FACE,{"disambiguationData":[OSD([sQuery(id+"F0.wireOp",EDGE,"E0")])]}),makeQuery(id+"F12.opExtrude","SWEPT_FACE",FACE,{"disambiguationData":[OSD([sQuery(id+"F11.wireOp",EDGE,"E823")])]})]});
            var Q285;
            Q285=makeQuery(id+"F12.boolean.opBoolean","INTERSECT",EDGE,{"derivedFrom":[makeQuery(id+"F1.opExtrude","SWEPT_FACE",FACE,{"disambiguationData":[OSD([sQuery(id+"F0.wireOp",EDGE,"E0")])]}),makeQuery(id+"F12.opExtrude","SWEPT_FACE",FACE,{"disambiguationData":[OSD([sQuery(id+"F11.wireOp",EDGE,"E822")])]})]});
            var Q286;
            Q286=makeQuery(id+"F12.boolean.opBoolean","INTERSECT",EDGE,{"derivedFrom":[makeQuery(id+"F1.opExtrude","SWEPT_FACE",FACE,{"disambiguationData":[OSD([sQuery(id+"F0.wireOp",EDGE,"E0")])]}),makeQuery(id+"F12.opExtrude","SWEPT_FACE",FACE,{"disambiguationData":[OSD([sQuery(id+"F11.wireOp",EDGE,"E821")])]})]});
            var Q287;
            Q287=makeQuery(id+"F12.boolean.opBoolean","INTERSECT",EDGE,{"derivedFrom":[makeQuery(id+"F1.opExtrude","SWEPT_FACE",FACE,{"disambiguationData":[OSD([sQuery(id+"F0.wireOp",EDGE,"E0")])]}),makeQuery(id+"F12.opExtrude","SWEPT_FACE",FACE,{"disambiguationData":[OSD([sQuery(id+"F11.wireOp",EDGE,"E820")])]})]});
            var Q288;
            Q288=makeQuery(id+"F12.boolean.opBoolean","INTERSECT",EDGE,{"derivedFrom":[makeQuery(id+"F1.opExtrude","SWEPT_FACE",FACE,{"disambiguationData":[OSD([sQuery(id+"F0.wireOp",EDGE,"E0")])]}),makeQuery(id+"F12.opExtrude","SWEPT_FACE",FACE,{"disambiguationData":[OSD([sQuery(id+"F11.wireOp",EDGE,"E819")])]})]});
            var Q289;
            Q289=makeQuery(id+"F12.boolean.opBoolean","INTERSECT",EDGE,{"derivedFrom":[makeQuery(id+"F1.opExtrude","SWEPT_FACE",FACE,{"disambiguationData":[OSD([sQuery(id+"F0.wireOp",EDGE,"E0")])]}),makeQuery(id+"F12.opExtrude","SWEPT_FACE",FACE,{"disambiguationData":[OSD([sQuery(id+"F11.wireOp",EDGE,"E818")])]})]});
            var Q290;
            Q290=makeQuery(id+"F12.boolean.opBoolean","INTERSECT",EDGE,{"derivedFrom":[makeQuery(id+"F1.opExtrude","SWEPT_FACE",FACE,{"disambiguationData":[OSD([sQuery(id+"F0.wireOp",EDGE,"E0")])]}),makeQuery(id+"F12.opExtrude","SWEPT_FACE",FACE,{"disambiguationData":[OSD([sQuery(id+"F11.wireOp",EDGE,"E856")])]})]});
            var Q291;
            Q291=makeQuery(id+"F12.boolean.opBoolean","INTERSECT",EDGE,{"derivedFrom":[makeQuery(id+"F1.opExtrude","SWEPT_FACE",FACE,{"disambiguationData":[OSD([sQuery(id+"F0.wireOp",EDGE,"E0")])]}),makeQuery(id+"F12.opExtrude","SWEPT_FACE",FACE,{"disambiguationData":[OSD([sQuery(id+"F11.wireOp",EDGE,"E855")])]})]});
            var Q292;
            Q292=makeQuery(id+"F12.boolean.opBoolean","INTERSECT",EDGE,{"derivedFrom":[makeQuery(id+"F1.opExtrude","SWEPT_FACE",FACE,{"disambiguationData":[OSD([sQuery(id+"F0.wireOp",EDGE,"E0")])]}),makeQuery(id+"F12.opExtrude","SWEPT_FACE",FACE,{"disambiguationData":[OSD([sQuery(id+"F11.wireOp",EDGE,"E859")])]})]});
            var Q293;
            Q293=makeQuery(id+"F12.boolean.opBoolean","INTERSECT",EDGE,{"derivedFrom":[makeQuery(id+"F1.opExtrude","SWEPT_FACE",FACE,{"disambiguationData":[OSD([sQuery(id+"F0.wireOp",EDGE,"E0")])]}),makeQuery(id+"F12.opExtrude","SWEPT_FACE",FACE,{"disambiguationData":[OSD([sQuery(id+"F11.wireOp",EDGE,"E858")])]})]});
            var Q294;
            Q294=makeQuery(id+"F12.boolean.opBoolean","INTERSECT",EDGE,{"derivedFrom":[makeQuery(id+"F1.opExtrude","SWEPT_FACE",FACE,{"disambiguationData":[OSD([sQuery(id+"F0.wireOp",EDGE,"E0")])]}),makeQuery(id+"F12.opExtrude","SWEPT_FACE",FACE,{"disambiguationData":[OSD([sQuery(id+"F11.wireOp",EDGE,"E857")])]})]});
            var Q295;
            Q295=makeQuery(id+"F12.boolean.opBoolean","INTERSECT",EDGE,{"derivedFrom":[makeQuery(id+"F1.opExtrude","SWEPT_FACE",FACE,{"disambiguationData":[OSD([sQuery(id+"F0.wireOp",EDGE,"E0")])]}),makeQuery(id+"F12.opExtrude","SWEPT_FACE",FACE,{"disambiguationData":[OSD([sQuery(id+"F11.wireOp",EDGE,"E854")])]})]});
            var Q296;
            Q296=makeQuery(id+"F12.boolean.opBoolean","INTERSECT",EDGE,{"derivedFrom":[makeQuery(id+"F1.opExtrude","SWEPT_FACE",FACE,{"disambiguationData":[OSD([sQuery(id+"F0.wireOp",EDGE,"E0")])]}),makeQuery(id+"F12.opExtrude","SWEPT_FACE",FACE,{"disambiguationData":[OSD([sQuery(id+"F11.wireOp",EDGE,"E874")])]})]});
            var Q297;
            Q297=makeQuery(id+"F12.boolean.opBoolean","INTERSECT",EDGE,{"derivedFrom":[makeQuery(id+"F1.opExtrude","SWEPT_FACE",FACE,{"disambiguationData":[OSD([sQuery(id+"F0.wireOp",EDGE,"E0")])]}),makeQuery(id+"F12.opExtrude","SWEPT_FACE",FACE,{"disambiguationData":[OSD([sQuery(id+"F11.wireOp",EDGE,"E873")])]})]});
            var Q298;
            Q298=makeQuery(id+"F12.boolean.opBoolean","INTERSECT",EDGE,{"derivedFrom":[makeQuery(id+"F1.opExtrude","SWEPT_FACE",FACE,{"disambiguationData":[OSD([sQuery(id+"F0.wireOp",EDGE,"E0")])]}),makeQuery(id+"F12.opExtrude","SWEPT_FACE",FACE,{"disambiguationData":[OSD([sQuery(id+"F11.wireOp",EDGE,"E872")])]})]});
            var Q299;
            Q299=makeQuery(id+"F12.boolean.opBoolean","INTERSECT",EDGE,{"derivedFrom":[makeQuery(id+"F1.opExtrude","SWEPT_FACE",FACE,{"disambiguationData":[OSD([sQuery(id+"F0.wireOp",EDGE,"E0")])]}),makeQuery(id+"F12.opExtrude","SWEPT_FACE",FACE,{"disambiguationData":[OSD([sQuery(id+"F11.wireOp",EDGE,"E877")])]})]});
            var Q300;
            Q300=makeQuery(id+"F12.boolean.opBoolean","INTERSECT",EDGE,{"derivedFrom":[makeQuery(id+"F1.opExtrude","SWEPT_FACE",FACE,{"disambiguationData":[OSD([sQuery(id+"F0.wireOp",EDGE,"E0")])]}),makeQuery(id+"F12.opExtrude","SWEPT_FACE",FACE,{"disambiguationData":[OSD([sQuery(id+"F11.wireOp",EDGE,"E876")])]})]});
            var Q301;
            Q301=makeQuery(id+"F12.boolean.opBoolean","INTERSECT",EDGE,{"derivedFrom":[makeQuery(id+"F1.opExtrude","SWEPT_FACE",FACE,{"disambiguationData":[OSD([sQuery(id+"F0.wireOp",EDGE,"E0")])]}),makeQuery(id+"F12.opExtrude","SWEPT_FACE",FACE,{"disambiguationData":[OSD([sQuery(id+"F11.wireOp",EDGE,"E875")])]})]});
            var Q302;
            Q302=makeQuery(id+"F12.boolean.opBoolean","INTERSECT",EDGE,{"derivedFrom":[makeQuery(id+"F1.opExtrude","SWEPT_FACE",FACE,{"disambiguationData":[OSD([sQuery(id+"F0.wireOp",EDGE,"E0")])]}),makeQuery(id+"F12.opExtrude","SWEPT_FACE",FACE,{"disambiguationData":[OSD([sQuery(id+"F11.wireOp",EDGE,"E892")])]})]});
            var Q303;
            Q303=makeQuery(id+"F12.boolean.opBoolean","INTERSECT",EDGE,{"derivedFrom":[makeQuery(id+"F1.opExtrude","SWEPT_FACE",FACE,{"disambiguationData":[OSD([sQuery(id+"F0.wireOp",EDGE,"E0")])]}),makeQuery(id+"F12.opExtrude","SWEPT_FACE",FACE,{"disambiguationData":[OSD([sQuery(id+"F11.wireOp",EDGE,"E893")])]})]});
            var Q304;
            Q304=makeQuery(id+"F12.boolean.opBoolean","INTERSECT",EDGE,{"derivedFrom":[makeQuery(id+"F1.opExtrude","SWEPT_FACE",FACE,{"disambiguationData":[OSD([sQuery(id+"F0.wireOp",EDGE,"E0")])]}),makeQuery(id+"F12.opExtrude","SWEPT_FACE",FACE,{"disambiguationData":[OSD([sQuery(id+"F11.wireOp",EDGE,"E894")])]})]});
            var Q305;
            Q305=makeQuery(id+"F12.boolean.opBoolean","INTERSECT",EDGE,{"derivedFrom":[makeQuery(id+"F1.opExtrude","SWEPT_FACE",FACE,{"disambiguationData":[OSD([sQuery(id+"F0.wireOp",EDGE,"E0")])]}),makeQuery(id+"F12.opExtrude","SWEPT_FACE",FACE,{"disambiguationData":[OSD([sQuery(id+"F11.wireOp",EDGE,"E895")])]})]});
            var Q306;
            Q306=makeQuery(id+"F12.boolean.opBoolean","INTERSECT",EDGE,{"derivedFrom":[makeQuery(id+"F1.opExtrude","SWEPT_FACE",FACE,{"disambiguationData":[OSD([sQuery(id+"F0.wireOp",EDGE,"E0")])]}),makeQuery(id+"F12.opExtrude","SWEPT_FACE",FACE,{"disambiguationData":[OSD([sQuery(id+"F11.wireOp",EDGE,"E890")])]})]});
            var Q307;
            Q307=makeQuery(id+"F12.boolean.opBoolean","INTERSECT",EDGE,{"derivedFrom":[makeQuery(id+"F1.opExtrude","SWEPT_FACE",FACE,{"disambiguationData":[OSD([sQuery(id+"F0.wireOp",EDGE,"E0")])]}),makeQuery(id+"F12.opExtrude","SWEPT_FACE",FACE,{"disambiguationData":[OSD([sQuery(id+"F11.wireOp",EDGE,"E891")])]})]});
            var Q308;
            Q308=makeQuery(id+"F12.boolean.opBoolean","INTERSECT",EDGE,{"derivedFrom":[makeQuery(id+"F1.opExtrude","SWEPT_FACE",FACE,{"disambiguationData":[OSD([sQuery(id+"F0.wireOp",EDGE,"E0")])]}),makeQuery(id+"F12.opExtrude","SWEPT_FACE",FACE,{"disambiguationData":[OSD([sQuery(id+"F11.wireOp",EDGE,"E910")])]})]});
            var Q309;
            Q309=makeQuery(id+"F12.boolean.opBoolean","INTERSECT",EDGE,{"derivedFrom":[makeQuery(id+"F1.opExtrude","SWEPT_FACE",FACE,{"disambiguationData":[OSD([sQuery(id+"F0.wireOp",EDGE,"E0")])]}),makeQuery(id+"F12.opExtrude","SWEPT_FACE",FACE,{"disambiguationData":[OSD([sQuery(id+"F11.wireOp",EDGE,"E908")])]})]});
            var Q310;
            Q310=makeQuery(id+"F12.boolean.opBoolean","INTERSECT",EDGE,{"derivedFrom":[makeQuery(id+"F1.opExtrude","SWEPT_FACE",FACE,{"disambiguationData":[OSD([sQuery(id+"F0.wireOp",EDGE,"E0")])]}),makeQuery(id+"F12.opExtrude","SWEPT_FACE",FACE,{"disambiguationData":[OSD([sQuery(id+"F11.wireOp",EDGE,"E913")])]})]});
            var Q311;
            Q311=makeQuery(id+"F12.boolean.opBoolean","INTERSECT",EDGE,{"derivedFrom":[makeQuery(id+"F1.opExtrude","SWEPT_FACE",FACE,{"disambiguationData":[OSD([sQuery(id+"F0.wireOp",EDGE,"E0")])]}),makeQuery(id+"F12.opExtrude","SWEPT_FACE",FACE,{"disambiguationData":[OSD([sQuery(id+"F11.wireOp",EDGE,"E912")])]})]});
            var Q312;
            Q312=makeQuery(id+"F12.boolean.opBoolean","INTERSECT",EDGE,{"derivedFrom":[makeQuery(id+"F1.opExtrude","SWEPT_FACE",FACE,{"disambiguationData":[OSD([sQuery(id+"F0.wireOp",EDGE,"E0")])]}),makeQuery(id+"F12.opExtrude","SWEPT_FACE",FACE,{"disambiguationData":[OSD([sQuery(id+"F11.wireOp",EDGE,"E911")])]})]});
            var Q313;
            Q313=makeQuery(id+"F12.boolean.opBoolean","INTERSECT",EDGE,{"derivedFrom":[makeQuery(id+"F1.opExtrude","SWEPT_FACE",FACE,{"disambiguationData":[OSD([sQuery(id+"F0.wireOp",EDGE,"E0")])]}),makeQuery(id+"F12.opExtrude","SWEPT_FACE",FACE,{"disambiguationData":[OSD([sQuery(id+"F11.wireOp",EDGE,"E909")])]})]});
            var Q314;
            Q314=makeQuery(id+"F12.boolean.opBoolean","INTERSECT",EDGE,{"derivedFrom":[makeQuery(id+"F1.opExtrude","SWEPT_FACE",FACE,{"disambiguationData":[OSD([sQuery(id+"F0.wireOp",EDGE,"E0")])]}),makeQuery(id+"F12.opExtrude","SWEPT_FACE",FACE,{"disambiguationData":[OSD([sQuery(id+"F11.wireOp",EDGE,"E927")])]})]});
            var Q315;
            Q315=makeQuery(id+"F12.boolean.opBoolean","INTERSECT",EDGE,{"derivedFrom":[makeQuery(id+"F1.opExtrude","SWEPT_FACE",FACE,{"disambiguationData":[OSD([sQuery(id+"F0.wireOp",EDGE,"E0")])]}),makeQuery(id+"F12.opExtrude","SWEPT_FACE",FACE,{"disambiguationData":[OSD([sQuery(id+"F11.wireOp",EDGE,"E926")])]})]});
            var Q316;
            Q316=makeQuery(id+"F12.boolean.opBoolean","INTERSECT",EDGE,{"derivedFrom":[makeQuery(id+"F1.opExtrude","SWEPT_FACE",FACE,{"disambiguationData":[OSD([sQuery(id+"F0.wireOp",EDGE,"E0")])]}),makeQuery(id+"F12.opExtrude","SWEPT_FACE",FACE,{"disambiguationData":[OSD([sQuery(id+"F11.wireOp",EDGE,"E931")])]})]});
            var Q317;
            Q317=makeQuery(id+"F12.boolean.opBoolean","INTERSECT",EDGE,{"derivedFrom":[makeQuery(id+"F1.opExtrude","SWEPT_FACE",FACE,{"disambiguationData":[OSD([sQuery(id+"F0.wireOp",EDGE,"E0")])]}),makeQuery(id+"F12.opExtrude","SWEPT_FACE",FACE,{"disambiguationData":[OSD([sQuery(id+"F11.wireOp",EDGE,"E930")])]})]});
            var Q318;
            Q318=makeQuery(id+"F12.boolean.opBoolean","INTERSECT",EDGE,{"derivedFrom":[makeQuery(id+"F1.opExtrude","SWEPT_FACE",FACE,{"disambiguationData":[OSD([sQuery(id+"F0.wireOp",EDGE,"E0")])]}),makeQuery(id+"F12.opExtrude","SWEPT_FACE",FACE,{"disambiguationData":[OSD([sQuery(id+"F11.wireOp",EDGE,"E929")])]})]});
            var Q319;
            Q319=makeQuery(id+"F12.boolean.opBoolean","INTERSECT",EDGE,{"derivedFrom":[makeQuery(id+"F1.opExtrude","SWEPT_FACE",FACE,{"disambiguationData":[OSD([sQuery(id+"F0.wireOp",EDGE,"E0")])]}),makeQuery(id+"F12.opExtrude","SWEPT_FACE",FACE,{"disambiguationData":[OSD([sQuery(id+"F11.wireOp",EDGE,"E928")])]})]});
            var Q320;
            Q320=makeQuery(id+"F12.boolean.opBoolean","INTERSECT",EDGE,{"derivedFrom":[makeQuery(id+"F1.opExtrude","SWEPT_FACE",FACE,{"disambiguationData":[OSD([sQuery(id+"F0.wireOp",EDGE,"E0")])]}),makeQuery(id+"F12.opExtrude","SWEPT_FACE",FACE,{"disambiguationData":[OSD([sQuery(id+"F11.wireOp",EDGE,"E946")])]})]});
            var Q321;
            Q321=makeQuery(id+"F12.boolean.opBoolean","INTERSECT",EDGE,{"derivedFrom":[makeQuery(id+"F1.opExtrude","SWEPT_FACE",FACE,{"disambiguationData":[OSD([sQuery(id+"F0.wireOp",EDGE,"E0")])]}),makeQuery(id+"F12.opExtrude","SWEPT_FACE",FACE,{"disambiguationData":[OSD([sQuery(id+"F11.wireOp",EDGE,"E945")])]})]});
            var Q322;
            Q322=makeQuery(id+"F12.boolean.opBoolean","INTERSECT",EDGE,{"derivedFrom":[makeQuery(id+"F1.opExtrude","SWEPT_FACE",FACE,{"disambiguationData":[OSD([sQuery(id+"F0.wireOp",EDGE,"E0")])]}),makeQuery(id+"F12.opExtrude","SWEPT_FACE",FACE,{"disambiguationData":[OSD([sQuery(id+"F11.wireOp",EDGE,"E944")])]})]});
            var Q323;
            Q323=makeQuery(id+"F12.boolean.opBoolean","INTERSECT",EDGE,{"derivedFrom":[makeQuery(id+"F1.opExtrude","SWEPT_FACE",FACE,{"disambiguationData":[OSD([sQuery(id+"F0.wireOp",EDGE,"E0")])]}),makeQuery(id+"F12.opExtrude","SWEPT_FACE",FACE,{"disambiguationData":[OSD([sQuery(id+"F11.wireOp",EDGE,"E949")])]})]});
            var Q324;
            Q324=makeQuery(id+"F12.boolean.opBoolean","INTERSECT",EDGE,{"derivedFrom":[makeQuery(id+"F1.opExtrude","SWEPT_FACE",FACE,{"disambiguationData":[OSD([sQuery(id+"F0.wireOp",EDGE,"E0")])]}),makeQuery(id+"F12.opExtrude","SWEPT_FACE",FACE,{"disambiguationData":[OSD([sQuery(id+"F11.wireOp",EDGE,"E948")])]})]});
            var Q325;
            Q325=makeQuery(id+"F12.boolean.opBoolean","INTERSECT",EDGE,{"derivedFrom":[makeQuery(id+"F1.opExtrude","SWEPT_FACE",FACE,{"disambiguationData":[OSD([sQuery(id+"F0.wireOp",EDGE,"E0")])]}),makeQuery(id+"F12.opExtrude","SWEPT_FACE",FACE,{"disambiguationData":[OSD([sQuery(id+"F11.wireOp",EDGE,"E947")])]})]});
            var Q326;
            Q326=makeQuery(id+"F12.boolean.opBoolean","INTERSECT",EDGE,{"derivedFrom":[makeQuery(id+"F1.opExtrude","SWEPT_FACE",FACE,{"disambiguationData":[OSD([sQuery(id+"F0.wireOp",EDGE,"E0")])]}),makeQuery(id+"F12.opExtrude","SWEPT_FACE",FACE,{"disambiguationData":[OSD([sQuery(id+"F11.wireOp",EDGE,"E964")])]})]});
            var Q327;
            Q327=makeQuery(id+"F12.boolean.opBoolean","INTERSECT",EDGE,{"derivedFrom":[makeQuery(id+"F1.opExtrude","SWEPT_FACE",FACE,{"disambiguationData":[OSD([sQuery(id+"F0.wireOp",EDGE,"E0")])]}),makeQuery(id+"F12.opExtrude","SWEPT_FACE",FACE,{"disambiguationData":[OSD([sQuery(id+"F11.wireOp",EDGE,"E965")])]})]});
            var Q328;
            Q328=makeQuery(id+"F12.boolean.opBoolean","INTERSECT",EDGE,{"derivedFrom":[makeQuery(id+"F1.opExtrude","SWEPT_FACE",FACE,{"disambiguationData":[OSD([sQuery(id+"F0.wireOp",EDGE,"E0")])]}),makeQuery(id+"F12.opExtrude","SWEPT_FACE",FACE,{"disambiguationData":[OSD([sQuery(id+"F11.wireOp",EDGE,"E966")])]})]});
            var Q329;
            Q329=makeQuery(id+"F12.boolean.opBoolean","INTERSECT",EDGE,{"derivedFrom":[makeQuery(id+"F1.opExtrude","SWEPT_FACE",FACE,{"disambiguationData":[OSD([sQuery(id+"F0.wireOp",EDGE,"E0")])]}),makeQuery(id+"F12.opExtrude","SWEPT_FACE",FACE,{"disambiguationData":[OSD([sQuery(id+"F11.wireOp",EDGE,"E967")])]})]});
            var Q330;
            Q330=makeQuery(id+"F12.boolean.opBoolean","INTERSECT",EDGE,{"derivedFrom":[makeQuery(id+"F1.opExtrude","SWEPT_FACE",FACE,{"disambiguationData":[OSD([sQuery(id+"F0.wireOp",EDGE,"E0")])]}),makeQuery(id+"F12.opExtrude","SWEPT_FACE",FACE,{"disambiguationData":[OSD([sQuery(id+"F11.wireOp",EDGE,"E962")])]})]});
            var Q331;
            Q331=makeQuery(id+"F12.boolean.opBoolean","INTERSECT",EDGE,{"derivedFrom":[makeQuery(id+"F1.opExtrude","SWEPT_FACE",FACE,{"disambiguationData":[OSD([sQuery(id+"F0.wireOp",EDGE,"E0")])]}),makeQuery(id+"F12.opExtrude","SWEPT_FACE",FACE,{"disambiguationData":[OSD([sQuery(id+"F11.wireOp",EDGE,"E963")])]})]});
            var Q332;
            Q332=makeQuery(id+"F12.boolean.opBoolean","INTERSECT",EDGE,{"derivedFrom":[makeQuery(id+"F1.opExtrude","SWEPT_FACE",FACE,{"disambiguationData":[OSD([sQuery(id+"F0.wireOp",EDGE,"E0")])]}),makeQuery(id+"F12.opExtrude","SWEPT_FACE",FACE,{"disambiguationData":[OSD([sQuery(id+"F11.wireOp",EDGE,"E982")])]})]});
            var Q333;
            Q333=makeQuery(id+"F12.boolean.opBoolean","INTERSECT",EDGE,{"derivedFrom":[makeQuery(id+"F1.opExtrude","SWEPT_FACE",FACE,{"disambiguationData":[OSD([sQuery(id+"F0.wireOp",EDGE,"E0")])]}),makeQuery(id+"F12.opExtrude","SWEPT_FACE",FACE,{"disambiguationData":[OSD([sQuery(id+"F11.wireOp",EDGE,"E981")])]})]});
            var Q334;
            Q334=makeQuery(id+"F12.boolean.opBoolean","INTERSECT",EDGE,{"derivedFrom":[makeQuery(id+"F1.opExtrude","SWEPT_FACE",FACE,{"disambiguationData":[OSD([sQuery(id+"F0.wireOp",EDGE,"E0")])]}),makeQuery(id+"F12.opExtrude","SWEPT_FACE",FACE,{"disambiguationData":[OSD([sQuery(id+"F11.wireOp",EDGE,"E980")])]})]});
            var Q335;
            Q335=makeQuery(id+"F12.boolean.opBoolean","INTERSECT",EDGE,{"derivedFrom":[makeQuery(id+"F1.opExtrude","SWEPT_FACE",FACE,{"disambiguationData":[OSD([sQuery(id+"F0.wireOp",EDGE,"E0")])]}),makeQuery(id+"F12.opExtrude","SWEPT_FACE",FACE,{"disambiguationData":[OSD([sQuery(id+"F11.wireOp",EDGE,"E985")])]})]});
            var Q336;
            Q336=makeQuery(id+"F12.boolean.opBoolean","INTERSECT",EDGE,{"derivedFrom":[makeQuery(id+"F1.opExtrude","SWEPT_FACE",FACE,{"disambiguationData":[OSD([sQuery(id+"F0.wireOp",EDGE,"E0")])]}),makeQuery(id+"F12.opExtrude","SWEPT_FACE",FACE,{"disambiguationData":[OSD([sQuery(id+"F11.wireOp",EDGE,"E984")])]})]});
            var Q337;
            Q337=makeQuery(id+"F12.boolean.opBoolean","INTERSECT",EDGE,{"derivedFrom":[makeQuery(id+"F1.opExtrude","SWEPT_FACE",FACE,{"disambiguationData":[OSD([sQuery(id+"F0.wireOp",EDGE,"E0")])]}),makeQuery(id+"F12.opExtrude","SWEPT_FACE",FACE,{"disambiguationData":[OSD([sQuery(id+"F11.wireOp",EDGE,"E1001")])]})]});
            var Q338;
            Q338=makeQuery(id+"F12.boolean.opBoolean","INTERSECT",EDGE,{"derivedFrom":[makeQuery(id+"F1.opExtrude","SWEPT_FACE",FACE,{"disambiguationData":[OSD([sQuery(id+"F0.wireOp",EDGE,"E0")])]}),makeQuery(id+"F12.opExtrude","SWEPT_FACE",FACE,{"disambiguationData":[OSD([sQuery(id+"F11.wireOp",EDGE,"E1002")])]})]});
            var Q339;
            Q339=makeQuery(id+"F12.boolean.opBoolean","INTERSECT",EDGE,{"derivedFrom":[makeQuery(id+"F1.opExtrude","SWEPT_FACE",FACE,{"disambiguationData":[OSD([sQuery(id+"F0.wireOp",EDGE,"E0")])]}),makeQuery(id+"F12.opExtrude","SWEPT_FACE",FACE,{"disambiguationData":[OSD([sQuery(id+"F11.wireOp",EDGE,"E1003")])]})]});
            var Q340;
            Q340=makeQuery(id+"F12.boolean.opBoolean","INTERSECT",EDGE,{"derivedFrom":[makeQuery(id+"F1.opExtrude","SWEPT_FACE",FACE,{"disambiguationData":[OSD([sQuery(id+"F0.wireOp",EDGE,"E0")])]}),makeQuery(id+"F12.opExtrude","SWEPT_FACE",FACE,{"disambiguationData":[OSD([sQuery(id+"F11.wireOp",EDGE,"E998")])]})]});
            var Q341;
            Q341=makeQuery(id+"F12.boolean.opBoolean","INTERSECT",EDGE,{"derivedFrom":[makeQuery(id+"F1.opExtrude","SWEPT_FACE",FACE,{"disambiguationData":[OSD([sQuery(id+"F0.wireOp",EDGE,"E0")])]}),makeQuery(id+"F12.opExtrude","SWEPT_FACE",FACE,{"disambiguationData":[OSD([sQuery(id+"F11.wireOp",EDGE,"E999")])]})]});
            var Q342;
            Q342=makeQuery(id+"F12.boolean.opBoolean","INTERSECT",EDGE,{"derivedFrom":[makeQuery(id+"F1.opExtrude","SWEPT_FACE",FACE,{"disambiguationData":[OSD([sQuery(id+"F0.wireOp",EDGE,"E0")])]}),makeQuery(id+"F12.opExtrude","SWEPT_FACE",FACE,{"disambiguationData":[OSD([sQuery(id+"F11.wireOp",EDGE,"E1000")])]})]});
            var Q343;
            Q343=makeQuery(id+"F12.boolean.opBoolean","INTERSECT",EDGE,{"derivedFrom":[makeQuery(id+"F1.opExtrude","SWEPT_FACE",FACE,{"disambiguationData":[OSD([sQuery(id+"F0.wireOp",EDGE,"E0")])]}),makeQuery(id+"F12.opExtrude","SWEPT_FACE",FACE,{"disambiguationData":[OSD([sQuery(id+"F11.wireOp",EDGE,"E1009")])]})]});
            var Q344;
            Q344=makeQuery(id+"F12.boolean.opBoolean","INTERSECT",EDGE,{"derivedFrom":[makeQuery(id+"F1.opExtrude","SWEPT_FACE",FACE,{"disambiguationData":[OSD([sQuery(id+"F0.wireOp",EDGE,"E0")])]}),makeQuery(id+"F12.opExtrude","SWEPT_FACE",FACE,{"disambiguationData":[OSD([sQuery(id+"F11.wireOp",EDGE,"E1018")])]})]});
            var Q345;
            Q345=makeQuery(id+"F12.boolean.opBoolean","INTERSECT",EDGE,{"derivedFrom":[makeQuery(id+"F1.opExtrude","SWEPT_FACE",FACE,{"disambiguationData":[OSD([sQuery(id+"F0.wireOp",EDGE,"E0")])]}),makeQuery(id+"F12.opExtrude","SWEPT_FACE",FACE,{"disambiguationData":[OSD([sQuery(id+"F11.wireOp",EDGE,"E1016"),sQuery(id+"F11.wireOp",EDGE,"E1017")])]})]});
            var Q346;
            Q346=makeQuery(id+"F12.boolean.opBoolean","INTERSECT",EDGE,{"derivedFrom":[makeQuery(id+"F1.opExtrude","SWEPT_FACE",FACE,{"disambiguationData":[OSD([sQuery(id+"F0.wireOp",EDGE,"E0")])]}),makeQuery(id+"F12.opExtrude","SWEPT_FACE",FACE,{"disambiguationData":[OSD([sQuery(id+"F11.wireOp",EDGE,"E1019")])]})]});
            var Q347;
            Q347=makeQuery(id+"F10.boolean.opBoolean","INTERSECT",EDGE,{"disambiguationData":[OD(1.0)],"derivedFrom":[makeQuery(id+"F1.opExtrude","SWEPT_FACE",FACE,{"disambiguationData":[OSD([sQuery(id+"F0.wireOp",EDGE,"E0")])]}),makeQuery(id+"F10.opExtrude","SWEPT_FACE",FACE,{"disambiguationData":[OSD([sQuery(id+"F9.wireOp",EDGE,"E548")])]})]});
            var Q348;
            Q348=makeQuery(id+"F10.boolean.opBoolean","INTERSECT",EDGE,{"disambiguationData":[OD(1.0)],"derivedFrom":[makeQuery(id+"F1.opExtrude","SWEPT_FACE",FACE,{"disambiguationData":[OSD([sQuery(id+"F0.wireOp",EDGE,"E0")])]}),makeQuery(id+"F10.opExtrude","SWEPT_FACE",FACE,{"disambiguationData":[OSD([sQuery(id+"F9.wireOp",EDGE,"E543")])]})]});
            var Q349;
            Q349=makeQuery(id+"F10.boolean.opBoolean","INTERSECT",EDGE,{"disambiguationData":[OD(1.0)],"derivedFrom":[makeQuery(id+"F1.opExtrude","SWEPT_FACE",FACE,{"disambiguationData":[OSD([sQuery(id+"F0.wireOp",EDGE,"E0")])]}),makeQuery(id+"F10.opExtrude","SWEPT_FACE",FACE,{"disambiguationData":[OSD([sQuery(id+"F9.wireOp",EDGE,"E544")])]})]});
            fillet(context, id + "F14", {"entities" : qUnion([Q0, Q1, Q2, Q3, Q4, Q5, Q6, Q7, Q8, Q9, Q10, Q11, Q12, Q13, Q14, Q15, Q16, Q17, Q18, Q19, Q20, Q21, Q22, Q23, Q24, Q25, Q26, Q27, Q28, Q29, Q30, Q31, Q32, Q33, Q34, Q35, Q36, Q37, Q38, Q39, Q40, Q41, Q42, Q43, Q44, Q45, Q46, Q47, Q48, Q49, Q50, Q51, Q52, Q53, Q54, Q55, Q56, Q57, Q58, Q59, Q60, Q61, Q62, Q63, Q64, Q65, Q66, Q67, Q68, Q69, Q70, Q71, Q72, Q73, Q74, Q75, Q76, Q77, Q78, Q79, Q80, Q81, Q82, Q83, Q84, Q85, Q86, Q87, Q88, Q89, Q90, Q91, Q92, Q93, Q94, Q95, Q96, Q97, Q98, Q99, Q100, Q101, Q102, Q103, Q104, Q105, Q106, Q107, Q108, Q109, Q110, Q111, Q112, Q113, Q114, Q115, Q116, Q117, Q118, Q119, Q120, Q121, Q122, Q123, Q124, Q125, Q126, Q127, Q128, Q129, Q130, Q131, Q132, Q133, Q134, Q135, Q136, Q137, Q138, Q139, Q140, Q141, Q142, Q143, Q144, Q145, Q146, Q147, Q148, Q149, Q150, Q151, Q152, Q153, Q154, Q155, Q156, Q157, Q158, Q159, Q160, Q161, Q162, Q163, Q164, Q165, Q166, Q167, Q168, Q169, Q170, Q171, Q172, Q173, Q174, Q175, Q176, Q177, Q178, Q179, Q180, Q181, Q182, Q183, Q184, Q185, Q186, Q187, Q188, Q189, Q190, Q191, Q192, Q193, Q194, Q195, Q196, Q197, Q198, Q199, Q200, Q201, Q202, Q203, Q204, Q205, Q206, Q207, Q208, Q209, Q210, Q211, Q212, Q213, Q214, Q215, Q216, Q217, Q218, Q219, Q220, Q221, Q222, Q223, Q224, Q225, Q226, Q227, Q228, Q229, Q230, Q231, Q232, Q233, Q234, Q235, Q236, Q237, Q238, Q239, Q240, Q241, Q242, Q243, Q244, Q245, Q246, Q247, Q248, Q249, Q250, Q251, Q252, Q253, Q254, Q255, Q256, Q257, Q258, Q259, Q260, Q261, Q262, Q263, Q264, Q265, Q266, Q267, Q268, Q269, Q270, Q271, Q272, Q273, Q274, Q275, Q276, Q277, Q278, Q279, Q280, Q281, Q282, Q283, Q284, Q285, Q286, Q287, Q288, Q289, Q290, Q291, Q292, Q293, Q294, Q295, Q296, Q297, Q298, Q299, Q300, Q301, Q302, Q303, Q304, Q305, Q306, Q307, Q308, Q309, Q310, Q311, Q312, Q313, Q314, Q315, Q316, Q317, Q318, Q319, Q320, Q321, Q322, Q323, Q324, Q325, Q326, Q327, Q328, Q329, Q330, Q331, Q332, Q333, Q334, Q335, Q336, Q337, Q338, Q339, Q340, Q341, Q342, Q343, Q344, Q345, Q346, Q347, Q348, Q349]), "radius" : .4 * mm, "tangentPropagation" : true, "allowEdgeOverflow" : false});
        }
        {
            var Q0;
            Q0=makeQuery(id+"F10.boolean.opBoolean","INTERSECT",EDGE,{"disambiguationData":[OD(1.0)],"derivedFrom":[makeQuery(id+"F1.opExtrude","SWEPT_FACE",FACE,{"disambiguationData":[OSD([sQuery(id+"F0.wireOp",EDGE,"E0")])]}),makeQuery(id+"F10.opExtrude","SWEPT_FACE",FACE,{"disambiguationData":[OSD([sQuery(id+"F9.wireOp",EDGE,"E580")])]})]});
            var Q1;
            Q1=makeQuery(id+"F10.boolean.opBoolean","INTERSECT",EDGE,{"disambiguationData":[OD(1.0)],"derivedFrom":[makeQuery(id+"F1.opExtrude","SWEPT_FACE",FACE,{"disambiguationData":[OSD([sQuery(id+"F0.wireOp",EDGE,"E0")])]}),makeQuery(id+"F10.opExtrude","SWEPT_FACE",FACE,{"disambiguationData":[OSD([sQuery(id+"F9.wireOp",EDGE,"E582")])]})]});
            var Q2;
            Q2=makeQuery(id+"F10.boolean.opBoolean","INTERSECT",EDGE,{"disambiguationData":[OD(1.0)],"derivedFrom":[makeQuery(id+"F1.opExtrude","SWEPT_FACE",FACE,{"disambiguationData":[OSD([sQuery(id+"F0.wireOp",EDGE,"E0")])]}),makeQuery(id+"F10.opExtrude","SWEPT_FACE",FACE,{"disambiguationData":[OSD([sQuery(id+"F9.wireOp",EDGE,"E581")])]})]});
            var Q3;
            Q3=makeQuery(id+"F10.boolean.opBoolean","INTERSECT",EDGE,{"disambiguationData":[OD(1.0)],"derivedFrom":[makeQuery(id+"F1.opExtrude","SWEPT_FACE",FACE,{"disambiguationData":[OSD([sQuery(id+"F0.wireOp",EDGE,"E0")])]}),makeQuery(id+"F10.opExtrude","SWEPT_FACE",FACE,{"disambiguationData":[OSD([sQuery(id+"F9.wireOp",EDGE,"E565")])]})]});
            var Q4;
            Q4=makeQuery(id+"F10.boolean.opBoolean","INTERSECT",EDGE,{"disambiguationData":[OD(1.0)],"derivedFrom":[makeQuery(id+"F1.opExtrude","SWEPT_FACE",FACE,{"disambiguationData":[OSD([sQuery(id+"F0.wireOp",EDGE,"E0")])]}),makeQuery(id+"F10.opExtrude","SWEPT_FACE",FACE,{"disambiguationData":[OSD([sQuery(id+"F9.wireOp",EDGE,"E564")])]})]});
            var Q5;
            Q5=makeQuery(id+"F10.boolean.opBoolean","INTERSECT",EDGE,{"disambiguationData":[OD(1.0)],"derivedFrom":[makeQuery(id+"F1.opExtrude","SWEPT_FACE",FACE,{"disambiguationData":[OSD([sQuery(id+"F0.wireOp",EDGE,"E0")])]}),makeQuery(id+"F10.opExtrude","SWEPT_FACE",FACE,{"disambiguationData":[OSD([sQuery(id+"F9.wireOp",EDGE,"E563")])]})]});
            var Q6;
            Q6=makeQuery(id+"F10.boolean.opBoolean","INTERSECT",EDGE,{"disambiguationData":[OD(1.0)],"derivedFrom":[makeQuery(id+"F1.opExtrude","SWEPT_FACE",FACE,{"disambiguationData":[OSD([sQuery(id+"F0.wireOp",EDGE,"E0")])]}),makeQuery(id+"F10.opExtrude","SWEPT_FACE",FACE,{"disambiguationData":[OSD([sQuery(id+"F9.wireOp",EDGE,"E562")])]})]});
            var Q7;
            Q7=makeQuery(id+"F10.boolean.opBoolean","INTERSECT",EDGE,{"disambiguationData":[OD(1.0)],"derivedFrom":[makeQuery(id+"F1.opExtrude","SWEPT_FACE",FACE,{"disambiguationData":[OSD([sQuery(id+"F0.wireOp",EDGE,"E0")])]}),makeQuery(id+"F10.opExtrude","SWEPT_FACE",FACE,{"disambiguationData":[OSD([sQuery(id+"F9.wireOp",EDGE,"E561")])]})]});
            var Q8;
            Q8=makeQuery(id+"F10.boolean.opBoolean","INTERSECT",EDGE,{"disambiguationData":[OD(1.0)],"derivedFrom":[makeQuery(id+"F1.opExtrude","SWEPT_FACE",FACE,{"disambiguationData":[OSD([sQuery(id+"F0.wireOp",EDGE,"E0")])]}),makeQuery(id+"F10.opExtrude","SWEPT_FACE",FACE,{"disambiguationData":[OSD([sQuery(id+"F9.wireOp",EDGE,"E566")])]})]});
            var Q9;
            Q9=makeQuery(id+"F10.boolean.opBoolean","INTERSECT",EDGE,{"disambiguationData":[OD(1.0)],"derivedFrom":[makeQuery(id+"F1.opExtrude","SWEPT_FACE",FACE,{"disambiguationData":[OSD([sQuery(id+"F0.wireOp",EDGE,"E0")])]}),makeQuery(id+"F10.opExtrude","SWEPT_FACE",FACE,{"disambiguationData":[OSD([sQuery(id+"F9.wireOp",EDGE,"E579")])]})]});
            var Q10;
            Q10=makeQuery(id+"F10.boolean.opBoolean","INTERSECT",EDGE,{"disambiguationData":[OD(1.0)],"derivedFrom":[makeQuery(id+"F1.opExtrude","SWEPT_FACE",FACE,{"disambiguationData":[OSD([sQuery(id+"F0.wireOp",EDGE,"E0")])]}),makeQuery(id+"F10.opExtrude","SWEPT_FACE",FACE,{"disambiguationData":[OSD([sQuery(id+"F9.wireOp",EDGE,"E584")])]})]});
            var Q11;
            Q11=makeQuery(id+"F10.boolean.opBoolean","INTERSECT",EDGE,{"disambiguationData":[OD(1.0)],"derivedFrom":[makeQuery(id+"F1.opExtrude","SWEPT_FACE",FACE,{"disambiguationData":[OSD([sQuery(id+"F0.wireOp",EDGE,"E0")])]}),makeQuery(id+"F10.opExtrude","SWEPT_FACE",FACE,{"disambiguationData":[OSD([sQuery(id+"F9.wireOp",EDGE,"E583")])]})]});
            var Q12;
            Q12=makeQuery(id+"F10.boolean.opBoolean","INTERSECT",EDGE,{"disambiguationData":[OD(1.0)],"derivedFrom":[makeQuery(id+"F1.opExtrude","SWEPT_FACE",FACE,{"disambiguationData":[OSD([sQuery(id+"F0.wireOp",EDGE,"E0")])]}),makeQuery(id+"F10.opExtrude","SWEPT_FACE",FACE,{"disambiguationData":[OSD([sQuery(id+"F9.wireOp",EDGE,"E602")])]})]});
            var Q13;
            Q13=makeQuery(id+"F10.boolean.opBoolean","INTERSECT",EDGE,{"disambiguationData":[OD(1.0)],"derivedFrom":[makeQuery(id+"F1.opExtrude","SWEPT_FACE",FACE,{"disambiguationData":[OSD([sQuery(id+"F0.wireOp",EDGE,"E0")])]}),makeQuery(id+"F10.opExtrude","SWEPT_FACE",FACE,{"disambiguationData":[OSD([sQuery(id+"F9.wireOp",EDGE,"E601")])]})]});
            var Q14;
            Q14=makeQuery(id+"F10.boolean.opBoolean","INTERSECT",EDGE,{"disambiguationData":[OD(1.0)],"derivedFrom":[makeQuery(id+"F1.opExtrude","SWEPT_FACE",FACE,{"disambiguationData":[OSD([sQuery(id+"F0.wireOp",EDGE,"E0")])]}),makeQuery(id+"F10.opExtrude","SWEPT_FACE",FACE,{"disambiguationData":[OSD([sQuery(id+"F9.wireOp",EDGE,"E600")])]})]});
            var Q15;
            Q15=makeQuery(id+"F10.boolean.opBoolean","INTERSECT",EDGE,{"disambiguationData":[OD(1.0)],"derivedFrom":[makeQuery(id+"F1.opExtrude","SWEPT_FACE",FACE,{"disambiguationData":[OSD([sQuery(id+"F0.wireOp",EDGE,"E0")])]}),makeQuery(id+"F10.opExtrude","SWEPT_FACE",FACE,{"disambiguationData":[OSD([sQuery(id+"F9.wireOp",EDGE,"E599")])]})]});
            var Q16;
            Q16=makeQuery(id+"F10.boolean.opBoolean","INTERSECT",EDGE,{"disambiguationData":[OD(1.0)],"derivedFrom":[makeQuery(id+"F1.opExtrude","SWEPT_FACE",FACE,{"disambiguationData":[OSD([sQuery(id+"F0.wireOp",EDGE,"E0")])]}),makeQuery(id+"F10.opExtrude","SWEPT_FACE",FACE,{"disambiguationData":[OSD([sQuery(id+"F9.wireOp",EDGE,"E598")])]})]});
            var Q17;
            Q17=makeQuery(id+"F10.boolean.opBoolean","INTERSECT",EDGE,{"disambiguationData":[OD(1.0)],"derivedFrom":[makeQuery(id+"F1.opExtrude","SWEPT_FACE",FACE,{"disambiguationData":[OSD([sQuery(id+"F0.wireOp",EDGE,"E0")])]}),makeQuery(id+"F10.opExtrude","SWEPT_FACE",FACE,{"disambiguationData":[OSD([sQuery(id+"F9.wireOp",EDGE,"E597")])]})]});
            var Q18;
            Q18=makeQuery(id+"F10.boolean.opBoolean","INTERSECT",EDGE,{"disambiguationData":[OD(1.0)],"derivedFrom":[makeQuery(id+"F1.opExtrude","SWEPT_FACE",FACE,{"disambiguationData":[OSD([sQuery(id+"F0.wireOp",EDGE,"E0")])]}),makeQuery(id+"F10.opExtrude","SWEPT_FACE",FACE,{"disambiguationData":[OSD([sQuery(id+"F9.wireOp",EDGE,"E620")])]})]});
            var Q19;
            Q19=makeQuery(id+"F10.boolean.opBoolean","INTERSECT",EDGE,{"disambiguationData":[OD(1.0)],"derivedFrom":[makeQuery(id+"F1.opExtrude","SWEPT_FACE",FACE,{"disambiguationData":[OSD([sQuery(id+"F0.wireOp",EDGE,"E0")])]}),makeQuery(id+"F10.opExtrude","SWEPT_FACE",FACE,{"disambiguationData":[OSD([sQuery(id+"F9.wireOp",EDGE,"E619")])]})]});
            var Q20;
            Q20=makeQuery(id+"F10.boolean.opBoolean","INTERSECT",EDGE,{"disambiguationData":[OD(1.0)],"derivedFrom":[makeQuery(id+"F1.opExtrude","SWEPT_FACE",FACE,{"disambiguationData":[OSD([sQuery(id+"F0.wireOp",EDGE,"E0")])]}),makeQuery(id+"F10.opExtrude","SWEPT_FACE",FACE,{"disambiguationData":[OSD([sQuery(id+"F9.wireOp",EDGE,"E618")])]})]});
            var Q21;
            Q21=makeQuery(id+"F10.boolean.opBoolean","INTERSECT",EDGE,{"disambiguationData":[OD(1.0)],"derivedFrom":[makeQuery(id+"F1.opExtrude","SWEPT_FACE",FACE,{"disambiguationData":[OSD([sQuery(id+"F0.wireOp",EDGE,"E0")])]}),makeQuery(id+"F10.opExtrude","SWEPT_FACE",FACE,{"disambiguationData":[OSD([sQuery(id+"F9.wireOp",EDGE,"E617")])]})]});
            var Q22;
            Q22=makeQuery(id+"F10.boolean.opBoolean","INTERSECT",EDGE,{"disambiguationData":[OD(1.0)],"derivedFrom":[makeQuery(id+"F1.opExtrude","SWEPT_FACE",FACE,{"disambiguationData":[OSD([sQuery(id+"F0.wireOp",EDGE,"E0")])]}),makeQuery(id+"F10.opExtrude","SWEPT_FACE",FACE,{"disambiguationData":[OSD([sQuery(id+"F9.wireOp",EDGE,"E616")])]})]});
            var Q23;
            Q23=makeQuery(id+"F10.boolean.opBoolean","INTERSECT",EDGE,{"disambiguationData":[OD(1.0)],"derivedFrom":[makeQuery(id+"F1.opExtrude","SWEPT_FACE",FACE,{"disambiguationData":[OSD([sQuery(id+"F0.wireOp",EDGE,"E0")])]}),makeQuery(id+"F10.opExtrude","SWEPT_FACE",FACE,{"disambiguationData":[OSD([sQuery(id+"F9.wireOp",EDGE,"E615")])]})]});
            var Q24;
            Q24=makeQuery(id+"F10.boolean.opBoolean","INTERSECT",EDGE,{"disambiguationData":[OD(1.0)],"derivedFrom":[makeQuery(id+"F1.opExtrude","SWEPT_FACE",FACE,{"disambiguationData":[OSD([sQuery(id+"F0.wireOp",EDGE,"E0")])]}),makeQuery(id+"F10.opExtrude","SWEPT_FACE",FACE,{"disambiguationData":[OSD([sQuery(id+"F9.wireOp",EDGE,"E635")])]})]});
            var Q25;
            Q25=makeQuery(id+"F10.boolean.opBoolean","INTERSECT",EDGE,{"disambiguationData":[OD(1.0)],"derivedFrom":[makeQuery(id+"F1.opExtrude","SWEPT_FACE",FACE,{"disambiguationData":[OSD([sQuery(id+"F0.wireOp",EDGE,"E0")])]}),makeQuery(id+"F10.opExtrude","SWEPT_FACE",FACE,{"disambiguationData":[OSD([sQuery(id+"F9.wireOp",EDGE,"E634")])]})]});
            var Q26;
            Q26=makeQuery(id+"F10.boolean.opBoolean","INTERSECT",EDGE,{"disambiguationData":[OD(1.0)],"derivedFrom":[makeQuery(id+"F1.opExtrude","SWEPT_FACE",FACE,{"disambiguationData":[OSD([sQuery(id+"F0.wireOp",EDGE,"E0")])]}),makeQuery(id+"F10.opExtrude","SWEPT_FACE",FACE,{"disambiguationData":[OSD([sQuery(id+"F9.wireOp",EDGE,"E633")])]})]});
            var Q27;
            Q27=makeQuery(id+"F10.boolean.opBoolean","INTERSECT",EDGE,{"disambiguationData":[OD(1.0)],"derivedFrom":[makeQuery(id+"F1.opExtrude","SWEPT_FACE",FACE,{"disambiguationData":[OSD([sQuery(id+"F0.wireOp",EDGE,"E0")])]}),makeQuery(id+"F10.opExtrude","SWEPT_FACE",FACE,{"disambiguationData":[OSD([sQuery(id+"F9.wireOp",EDGE,"E638")])]})]});
            var Q28;
            Q28=makeQuery(id+"F10.boolean.opBoolean","INTERSECT",EDGE,{"disambiguationData":[OD(1.0)],"derivedFrom":[makeQuery(id+"F1.opExtrude","SWEPT_FACE",FACE,{"disambiguationData":[OSD([sQuery(id+"F0.wireOp",EDGE,"E0")])]}),makeQuery(id+"F10.opExtrude","SWEPT_FACE",FACE,{"disambiguationData":[OSD([sQuery(id+"F9.wireOp",EDGE,"E637")])]})]});
            var Q29;
            Q29=makeQuery(id+"F10.boolean.opBoolean","INTERSECT",EDGE,{"disambiguationData":[OD(1.0)],"derivedFrom":[makeQuery(id+"F1.opExtrude","SWEPT_FACE",FACE,{"disambiguationData":[OSD([sQuery(id+"F0.wireOp",EDGE,"E0")])]}),makeQuery(id+"F10.opExtrude","SWEPT_FACE",FACE,{"disambiguationData":[OSD([sQuery(id+"F9.wireOp",EDGE,"E636")])]})]});
            var Q30;
            Q30=makeQuery(id+"F10.boolean.opBoolean","INTERSECT",EDGE,{"disambiguationData":[OD(1.0)],"derivedFrom":[makeQuery(id+"F1.opExtrude","SWEPT_FACE",FACE,{"disambiguationData":[OSD([sQuery(id+"F0.wireOp",EDGE,"E0")])]}),makeQuery(id+"F10.opExtrude","SWEPT_FACE",FACE,{"disambiguationData":[OSD([sQuery(id+"F9.wireOp",EDGE,"E656")])]})]});
            var Q31;
            Q31=makeQuery(id+"F10.boolean.opBoolean","INTERSECT",EDGE,{"disambiguationData":[OD(1.0)],"derivedFrom":[makeQuery(id+"F1.opExtrude","SWEPT_FACE",FACE,{"disambiguationData":[OSD([sQuery(id+"F0.wireOp",EDGE,"E0")])]}),makeQuery(id+"F10.opExtrude","SWEPT_FACE",FACE,{"disambiguationData":[OSD([sQuery(id+"F9.wireOp",EDGE,"E655")])]})]});
            var Q32;
            Q32=makeQuery(id+"F10.boolean.opBoolean","INTERSECT",EDGE,{"disambiguationData":[OD(1.0)],"derivedFrom":[makeQuery(id+"F1.opExtrude","SWEPT_FACE",FACE,{"disambiguationData":[OSD([sQuery(id+"F0.wireOp",EDGE,"E0")])]}),makeQuery(id+"F10.opExtrude","SWEPT_FACE",FACE,{"disambiguationData":[OSD([sQuery(id+"F9.wireOp",EDGE,"E654")])]})]});
            var Q33;
            Q33=makeQuery(id+"F10.boolean.opBoolean","INTERSECT",EDGE,{"disambiguationData":[OD(1.0)],"derivedFrom":[makeQuery(id+"F1.opExtrude","SWEPT_FACE",FACE,{"disambiguationData":[OSD([sQuery(id+"F0.wireOp",EDGE,"E0")])]}),makeQuery(id+"F10.opExtrude","SWEPT_FACE",FACE,{"disambiguationData":[OSD([sQuery(id+"F9.wireOp",EDGE,"E653")])]})]});
            var Q34;
            Q34=makeQuery(id+"F10.boolean.opBoolean","INTERSECT",EDGE,{"disambiguationData":[OD(1.0)],"derivedFrom":[makeQuery(id+"F1.opExtrude","SWEPT_FACE",FACE,{"disambiguationData":[OSD([sQuery(id+"F0.wireOp",EDGE,"E0")])]}),makeQuery(id+"F10.opExtrude","SWEPT_FACE",FACE,{"disambiguationData":[OSD([sQuery(id+"F9.wireOp",EDGE,"E652")])]})]});
            var Q35;
            Q35=makeQuery(id+"F10.boolean.opBoolean","INTERSECT",EDGE,{"disambiguationData":[OD(1.0)],"derivedFrom":[makeQuery(id+"F1.opExtrude","SWEPT_FACE",FACE,{"disambiguationData":[OSD([sQuery(id+"F0.wireOp",EDGE,"E0")])]}),makeQuery(id+"F10.opExtrude","SWEPT_FACE",FACE,{"disambiguationData":[OSD([sQuery(id+"F9.wireOp",EDGE,"E651")])]})]});
            var Q36;
            Q36=makeQuery(id+"F10.boolean.opBoolean","INTERSECT",EDGE,{"disambiguationData":[OD(1.0)],"derivedFrom":[makeQuery(id+"F1.opExtrude","SWEPT_FACE",FACE,{"disambiguationData":[OSD([sQuery(id+"F0.wireOp",EDGE,"E0")])]}),makeQuery(id+"F10.opExtrude","SWEPT_FACE",FACE,{"disambiguationData":[OSD([sQuery(id+"F9.wireOp",EDGE,"E671")])]})]});
            var Q37;
            Q37=makeQuery(id+"F10.boolean.opBoolean","INTERSECT",EDGE,{"disambiguationData":[OD(1.0)],"derivedFrom":[makeQuery(id+"F1.opExtrude","SWEPT_FACE",FACE,{"disambiguationData":[OSD([sQuery(id+"F0.wireOp",EDGE,"E0")])]}),makeQuery(id+"F10.opExtrude","SWEPT_FACE",FACE,{"disambiguationData":[OSD([sQuery(id+"F9.wireOp",EDGE,"E672")])]})]});
            var Q38;
            Q38=makeQuery(id+"F10.boolean.opBoolean","INTERSECT",EDGE,{"disambiguationData":[OD(1.0)],"derivedFrom":[makeQuery(id+"F1.opExtrude","SWEPT_FACE",FACE,{"disambiguationData":[OSD([sQuery(id+"F0.wireOp",EDGE,"E0")])]}),makeQuery(id+"F10.opExtrude","SWEPT_FACE",FACE,{"disambiguationData":[OSD([sQuery(id+"F9.wireOp",EDGE,"E673")])]})]});
            var Q39;
            Q39=makeQuery(id+"F10.boolean.opBoolean","INTERSECT",EDGE,{"disambiguationData":[OD(1.0)],"derivedFrom":[makeQuery(id+"F1.opExtrude","SWEPT_FACE",FACE,{"disambiguationData":[OSD([sQuery(id+"F0.wireOp",EDGE,"E0")])]}),makeQuery(id+"F10.opExtrude","SWEPT_FACE",FACE,{"disambiguationData":[OSD([sQuery(id+"F9.wireOp",EDGE,"E674")])]})]});
            var Q40;
            Q40=makeQuery(id+"F10.boolean.opBoolean","INTERSECT",EDGE,{"disambiguationData":[OD(1.0)],"derivedFrom":[makeQuery(id+"F1.opExtrude","SWEPT_FACE",FACE,{"disambiguationData":[OSD([sQuery(id+"F0.wireOp",EDGE,"E0")])]}),makeQuery(id+"F10.opExtrude","SWEPT_FACE",FACE,{"disambiguationData":[OSD([sQuery(id+"F9.wireOp",EDGE,"E669")])]})]});
            var Q41;
            Q41=makeQuery(id+"F10.boolean.opBoolean","INTERSECT",EDGE,{"disambiguationData":[OD(1.0)],"derivedFrom":[makeQuery(id+"F1.opExtrude","SWEPT_FACE",FACE,{"disambiguationData":[OSD([sQuery(id+"F0.wireOp",EDGE,"E0")])]}),makeQuery(id+"F10.opExtrude","SWEPT_FACE",FACE,{"disambiguationData":[OSD([sQuery(id+"F9.wireOp",EDGE,"E670")])]})]});
            var Q42;
            Q42=makeQuery(id+"F10.boolean.opBoolean","INTERSECT",EDGE,{"disambiguationData":[OD(1.0)],"derivedFrom":[makeQuery(id+"F1.opExtrude","SWEPT_FACE",FACE,{"disambiguationData":[OSD([sQuery(id+"F0.wireOp",EDGE,"E0")])]}),makeQuery(id+"F10.opExtrude","SWEPT_FACE",FACE,{"disambiguationData":[OSD([sQuery(id+"F9.wireOp",EDGE,"E689")])]})]});
            var Q43;
            Q43=makeQuery(id+"F10.boolean.opBoolean","INTERSECT",EDGE,{"disambiguationData":[OD(1.0)],"derivedFrom":[makeQuery(id+"F1.opExtrude","SWEPT_FACE",FACE,{"disambiguationData":[OSD([sQuery(id+"F0.wireOp",EDGE,"E0")])]}),makeQuery(id+"F10.opExtrude","SWEPT_FACE",FACE,{"disambiguationData":[OSD([sQuery(id+"F9.wireOp",EDGE,"E688")])]})]});
            var Q44;
            Q44=makeQuery(id+"F10.boolean.opBoolean","INTERSECT",EDGE,{"disambiguationData":[OD(1.0)],"derivedFrom":[makeQuery(id+"F1.opExtrude","SWEPT_FACE",FACE,{"disambiguationData":[OSD([sQuery(id+"F0.wireOp",EDGE,"E0")])]}),makeQuery(id+"F10.opExtrude","SWEPT_FACE",FACE,{"disambiguationData":[OSD([sQuery(id+"F9.wireOp",EDGE,"E687")])]})]});
            var Q45;
            Q45=makeQuery(id+"F10.boolean.opBoolean","INTERSECT",EDGE,{"disambiguationData":[OD(1.0)],"derivedFrom":[makeQuery(id+"F1.opExtrude","SWEPT_FACE",FACE,{"disambiguationData":[OSD([sQuery(id+"F0.wireOp",EDGE,"E0")])]}),makeQuery(id+"F10.opExtrude","SWEPT_FACE",FACE,{"disambiguationData":[OSD([sQuery(id+"F9.wireOp",EDGE,"E692")])]})]});
            var Q46;
            Q46=makeQuery(id+"F10.boolean.opBoolean","INTERSECT",EDGE,{"disambiguationData":[OD(1.0)],"derivedFrom":[makeQuery(id+"F1.opExtrude","SWEPT_FACE",FACE,{"disambiguationData":[OSD([sQuery(id+"F0.wireOp",EDGE,"E0")])]}),makeQuery(id+"F10.opExtrude","SWEPT_FACE",FACE,{"disambiguationData":[OSD([sQuery(id+"F9.wireOp",EDGE,"E691")])]})]});
            var Q47;
            Q47=makeQuery(id+"F10.boolean.opBoolean","INTERSECT",EDGE,{"disambiguationData":[OD(1.0)],"derivedFrom":[makeQuery(id+"F1.opExtrude","SWEPT_FACE",FACE,{"disambiguationData":[OSD([sQuery(id+"F0.wireOp",EDGE,"E0")])]}),makeQuery(id+"F10.opExtrude","SWEPT_FACE",FACE,{"disambiguationData":[OSD([sQuery(id+"F9.wireOp",EDGE,"E690")])]})]});
            var Q48;
            Q48=makeQuery(id+"F10.boolean.opBoolean","INTERSECT",EDGE,{"disambiguationData":[OD(1.0)],"derivedFrom":[makeQuery(id+"F1.opExtrude","SWEPT_FACE",FACE,{"disambiguationData":[OSD([sQuery(id+"F0.wireOp",EDGE,"E0")])]}),makeQuery(id+"F10.opExtrude","SWEPT_FACE",FACE,{"disambiguationData":[OSD([sQuery(id+"F9.wireOp",EDGE,"E710")])]})]});
            var Q49;
            Q49=makeQuery(id+"F10.boolean.opBoolean","INTERSECT",EDGE,{"disambiguationData":[OD(1.0)],"derivedFrom":[makeQuery(id+"F1.opExtrude","SWEPT_FACE",FACE,{"disambiguationData":[OSD([sQuery(id+"F0.wireOp",EDGE,"E0")])]}),makeQuery(id+"F10.opExtrude","SWEPT_FACE",FACE,{"disambiguationData":[OSD([sQuery(id+"F9.wireOp",EDGE,"E705")])]})]});
            var Q50;
            Q50=makeQuery(id+"F10.boolean.opBoolean","INTERSECT",EDGE,{"disambiguationData":[OD(1.0)],"derivedFrom":[makeQuery(id+"F1.opExtrude","SWEPT_FACE",FACE,{"disambiguationData":[OSD([sQuery(id+"F0.wireOp",EDGE,"E0")])]}),makeQuery(id+"F10.opExtrude","SWEPT_FACE",FACE,{"disambiguationData":[OSD([sQuery(id+"F9.wireOp",EDGE,"E706")])]})]});
            var Q51;
            Q51=makeQuery(id+"F10.boolean.opBoolean","INTERSECT",EDGE,{"disambiguationData":[OD(1.0)],"derivedFrom":[makeQuery(id+"F1.opExtrude","SWEPT_FACE",FACE,{"disambiguationData":[OSD([sQuery(id+"F0.wireOp",EDGE,"E0")])]}),makeQuery(id+"F10.opExtrude","SWEPT_FACE",FACE,{"disambiguationData":[OSD([sQuery(id+"F9.wireOp",EDGE,"E707")])]})]});
            var Q52;
            Q52=makeQuery(id+"F10.boolean.opBoolean","INTERSECT",EDGE,{"disambiguationData":[OD(1.0)],"derivedFrom":[makeQuery(id+"F1.opExtrude","SWEPT_FACE",FACE,{"disambiguationData":[OSD([sQuery(id+"F0.wireOp",EDGE,"E0")])]}),makeQuery(id+"F10.opExtrude","SWEPT_FACE",FACE,{"disambiguationData":[OSD([sQuery(id+"F9.wireOp",EDGE,"E708")])]})]});
            var Q53;
            Q53=makeQuery(id+"F10.boolean.opBoolean","INTERSECT",EDGE,{"disambiguationData":[OD(1.0)],"derivedFrom":[makeQuery(id+"F1.opExtrude","SWEPT_FACE",FACE,{"disambiguationData":[OSD([sQuery(id+"F0.wireOp",EDGE,"E0")])]}),makeQuery(id+"F10.opExtrude","SWEPT_FACE",FACE,{"disambiguationData":[OSD([sQuery(id+"F9.wireOp",EDGE,"E709")])]})]});
            var Q54;
            Q54=makeQuery(id+"F10.boolean.opBoolean","INTERSECT",EDGE,{"disambiguationData":[OD(1.0)],"derivedFrom":[makeQuery(id+"F1.opExtrude","SWEPT_FACE",FACE,{"disambiguationData":[OSD([sQuery(id+"F0.wireOp",EDGE,"E0")])]}),makeQuery(id+"F10.opExtrude","SWEPT_FACE",FACE,{"disambiguationData":[OSD([sQuery(id+"F9.wireOp",EDGE,"E725")])]})]});
            var Q55;
            Q55=makeQuery(id+"F10.boolean.opBoolean","INTERSECT",EDGE,{"disambiguationData":[OD(1.0)],"derivedFrom":[makeQuery(id+"F1.opExtrude","SWEPT_FACE",FACE,{"disambiguationData":[OSD([sQuery(id+"F0.wireOp",EDGE,"E0")])]}),makeQuery(id+"F10.opExtrude","SWEPT_FACE",FACE,{"disambiguationData":[OSD([sQuery(id+"F9.wireOp",EDGE,"E724")])]})]});
            var Q56;
            Q56=makeQuery(id+"F10.boolean.opBoolean","INTERSECT",EDGE,{"disambiguationData":[OD(1.0)],"derivedFrom":[makeQuery(id+"F1.opExtrude","SWEPT_FACE",FACE,{"disambiguationData":[OSD([sQuery(id+"F0.wireOp",EDGE,"E0")])]}),makeQuery(id+"F10.opExtrude","SWEPT_FACE",FACE,{"disambiguationData":[OSD([sQuery(id+"F9.wireOp",EDGE,"E723")])]})]});
            var Q57;
            Q57=makeQuery(id+"F10.boolean.opBoolean","INTERSECT",EDGE,{"disambiguationData":[OD(1.0)],"derivedFrom":[makeQuery(id+"F1.opExtrude","SWEPT_FACE",FACE,{"disambiguationData":[OSD([sQuery(id+"F0.wireOp",EDGE,"E0")])]}),makeQuery(id+"F10.opExtrude","SWEPT_FACE",FACE,{"disambiguationData":[OSD([sQuery(id+"F9.wireOp",EDGE,"E728")])]})]});
            var Q58;
            Q58=makeQuery(id+"F10.boolean.opBoolean","INTERSECT",EDGE,{"disambiguationData":[OD(1.0)],"derivedFrom":[makeQuery(id+"F1.opExtrude","SWEPT_FACE",FACE,{"disambiguationData":[OSD([sQuery(id+"F0.wireOp",EDGE,"E0")])]}),makeQuery(id+"F10.opExtrude","SWEPT_FACE",FACE,{"disambiguationData":[OSD([sQuery(id+"F9.wireOp",EDGE,"E727")])]})]});
            var Q59;
            Q59=makeQuery(id+"F10.boolean.opBoolean","INTERSECT",EDGE,{"disambiguationData":[OD(1.0)],"derivedFrom":[makeQuery(id+"F1.opExtrude","SWEPT_FACE",FACE,{"disambiguationData":[OSD([sQuery(id+"F0.wireOp",EDGE,"E0")])]}),makeQuery(id+"F10.opExtrude","SWEPT_FACE",FACE,{"disambiguationData":[OSD([sQuery(id+"F9.wireOp",EDGE,"E726")])]})]});
            var Q60;
            Q60=makeQuery(id+"F10.boolean.opBoolean","INTERSECT",EDGE,{"disambiguationData":[OD(1.0)],"derivedFrom":[makeQuery(id+"F1.opExtrude","SWEPT_FACE",FACE,{"disambiguationData":[OSD([sQuery(id+"F0.wireOp",EDGE,"E0")])]}),makeQuery(id+"F10.opExtrude","SWEPT_FACE",FACE,{"disambiguationData":[OSD([sQuery(id+"F9.wireOp",EDGE,"E759"),sQuery(id+"F9.wireOp",EDGE,"E760")])]})]});
            var Q61;
            Q61=makeQuery(id+"F10.boolean.opBoolean","INTERSECT",EDGE,{"disambiguationData":[OD(1.0)],"derivedFrom":[makeQuery(id+"F1.opExtrude","SWEPT_FACE",FACE,{"disambiguationData":[OSD([sQuery(id+"F0.wireOp",EDGE,"E0")])]}),makeQuery(id+"F10.opExtrude","SWEPT_FACE",FACE,{"disambiguationData":[OSD([sQuery(id+"F9.wireOp",EDGE,"E762")])]})]});
            var Q62;
            Q62=makeQuery(id+"F10.boolean.opBoolean","INTERSECT",EDGE,{"disambiguationData":[OD(1.0)],"derivedFrom":[makeQuery(id+"F1.opExtrude","SWEPT_FACE",FACE,{"disambiguationData":[OSD([sQuery(id+"F0.wireOp",EDGE,"E0")])]}),makeQuery(id+"F10.opExtrude","SWEPT_FACE",FACE,{"disambiguationData":[OSD([sQuery(id+"F9.wireOp",EDGE,"E752")])]})]});
            var Q63;
            Q63=makeQuery(id+"F10.boolean.opBoolean","INTERSECT",EDGE,{"disambiguationData":[OD(1.0)],"derivedFrom":[makeQuery(id+"F1.opExtrude","SWEPT_FACE",FACE,{"disambiguationData":[OSD([sQuery(id+"F0.wireOp",EDGE,"E0")])]}),makeQuery(id+"F10.opExtrude","SWEPT_FACE",FACE,{"disambiguationData":[OSD([sQuery(id+"F9.wireOp",EDGE,"E761")])]})]});
            var Q64;
            Q64=makeQuery(id+"F10.boolean.opBoolean","INTERSECT",EDGE,{"disambiguationData":[OD(1.0)],"derivedFrom":[makeQuery(id+"F1.opExtrude","SWEPT_FACE",FACE,{"disambiguationData":[OSD([sQuery(id+"F0.wireOp",EDGE,"E0")])]}),makeQuery(id+"F10.opExtrude","SWEPT_FACE",FACE,{"disambiguationData":[OSD([sQuery(id+"F9.wireOp",EDGE,"E742")])]})]});
            var Q65;
            Q65=makeQuery(id+"F10.boolean.opBoolean","INTERSECT",EDGE,{"disambiguationData":[OD(1.0)],"derivedFrom":[makeQuery(id+"F1.opExtrude","SWEPT_FACE",FACE,{"disambiguationData":[OSD([sQuery(id+"F0.wireOp",EDGE,"E0")])]}),makeQuery(id+"F10.opExtrude","SWEPT_FACE",FACE,{"disambiguationData":[OSD([sQuery(id+"F9.wireOp",EDGE,"E741")])]})]});
            var Q66;
            Q66=makeQuery(id+"F10.boolean.opBoolean","INTERSECT",EDGE,{"disambiguationData":[OD(1.0)],"derivedFrom":[makeQuery(id+"F1.opExtrude","SWEPT_FACE",FACE,{"disambiguationData":[OSD([sQuery(id+"F0.wireOp",EDGE,"E0")])]}),makeQuery(id+"F10.opExtrude","SWEPT_FACE",FACE,{"disambiguationData":[OSD([sQuery(id+"F9.wireOp",EDGE,"E746")])]})]});
            var Q67;
            Q67=makeQuery(id+"F10.boolean.opBoolean","INTERSECT",EDGE,{"disambiguationData":[OD(1.0)],"derivedFrom":[makeQuery(id+"F1.opExtrude","SWEPT_FACE",FACE,{"disambiguationData":[OSD([sQuery(id+"F0.wireOp",EDGE,"E0")])]}),makeQuery(id+"F10.opExtrude","SWEPT_FACE",FACE,{"disambiguationData":[OSD([sQuery(id+"F9.wireOp",EDGE,"E745")])]})]});
            var Q68;
            Q68=makeQuery(id+"F10.boolean.opBoolean","INTERSECT",EDGE,{"disambiguationData":[OD(1.0)],"derivedFrom":[makeQuery(id+"F1.opExtrude","SWEPT_FACE",FACE,{"disambiguationData":[OSD([sQuery(id+"F0.wireOp",EDGE,"E0")])]}),makeQuery(id+"F10.opExtrude","SWEPT_FACE",FACE,{"disambiguationData":[OSD([sQuery(id+"F9.wireOp",EDGE,"E744")])]})]});
            var Q69;
            Q69=makeQuery(id+"F5.boolean.opBoolean","INTERSECT",EDGE,{"disambiguationData":[OD(1.0)],"derivedFrom":[makeQuery(id+"F1.opExtrude","SWEPT_FACE",FACE,{"disambiguationData":[OSD([sQuery(id+"F0.wireOp",EDGE,"E0")])]}),makeQuery(id+"F5.opExtrude","SWEPT_FACE",FACE,{"disambiguationData":[OSD([sQuery(id+"F4.wireOp",EDGE,"E253")])]})]});
            var Q70;
            Q70=makeQuery(id+"F5.boolean.opBoolean","INTERSECT",EDGE,{"disambiguationData":[OD(1.0)],"derivedFrom":[makeQuery(id+"F1.opExtrude","SWEPT_FACE",FACE,{"disambiguationData":[OSD([sQuery(id+"F0.wireOp",EDGE,"E0")])]}),makeQuery(id+"F5.opExtrude","SWEPT_FACE",FACE,{"disambiguationData":[OSD([sQuery(id+"F4.wireOp",EDGE,"E252")])]})]});
            var Q71;
            Q71=makeQuery(id+"F5.boolean.opBoolean","INTERSECT",EDGE,{"disambiguationData":[OD(1.0)],"derivedFrom":[makeQuery(id+"F1.opExtrude","SWEPT_FACE",FACE,{"disambiguationData":[OSD([sQuery(id+"F0.wireOp",EDGE,"E0")])]}),makeQuery(id+"F5.opExtrude","SWEPT_FACE",FACE,{"disambiguationData":[OSD([sQuery(id+"F4.wireOp",EDGE,"E251")])]})]});
            var Q72;
            Q72=makeQuery(id+"F5.boolean.opBoolean","INTERSECT",EDGE,{"disambiguationData":[OD(1.0)],"derivedFrom":[makeQuery(id+"F1.opExtrude","SWEPT_FACE",FACE,{"disambiguationData":[OSD([sQuery(id+"F0.wireOp",EDGE,"E0")])]}),makeQuery(id+"F5.opExtrude","SWEPT_FACE",FACE,{"disambiguationData":[OSD([sQuery(id+"F4.wireOp",EDGE,"E250")])]})]});
            var Q73;
            Q73=makeQuery(id+"F5.boolean.opBoolean","INTERSECT",EDGE,{"disambiguationData":[OD(1.0)],"derivedFrom":[makeQuery(id+"F1.opExtrude","SWEPT_FACE",FACE,{"disambiguationData":[OSD([sQuery(id+"F0.wireOp",EDGE,"E0")])]}),makeQuery(id+"F5.opExtrude","SWEPT_FACE",FACE,{"disambiguationData":[OSD([sQuery(id+"F4.wireOp",EDGE,"E249")])]})]});
            var Q74;
            Q74=makeQuery(id+"F5.boolean.opBoolean","INTERSECT",EDGE,{"disambiguationData":[OD(1.0)],"derivedFrom":[makeQuery(id+"F1.opExtrude","SWEPT_FACE",FACE,{"disambiguationData":[OSD([sQuery(id+"F0.wireOp",EDGE,"E0")])]}),makeQuery(id+"F5.opExtrude","SWEPT_FACE",FACE,{"disambiguationData":[OSD([sQuery(id+"F4.wireOp",EDGE,"E248")])]})]});
            var Q75;
            Q75=makeQuery(id+"F5.boolean.opBoolean","INTERSECT",EDGE,{"disambiguationData":[OD(1.0)],"derivedFrom":[makeQuery(id+"F1.opExtrude","SWEPT_FACE",FACE,{"disambiguationData":[OSD([sQuery(id+"F0.wireOp",EDGE,"E0")])]}),makeQuery(id+"F5.opExtrude","SWEPT_FACE",FACE,{"disambiguationData":[OSD([sQuery(id+"F4.wireOp",EDGE,"E235")])]})]});
            var Q76;
            Q76=makeQuery(id+"F5.boolean.opBoolean","INTERSECT",EDGE,{"disambiguationData":[OD(1.0)],"derivedFrom":[makeQuery(id+"F1.opExtrude","SWEPT_FACE",FACE,{"disambiguationData":[OSD([sQuery(id+"F0.wireOp",EDGE,"E0")])]}),makeQuery(id+"F5.opExtrude","SWEPT_FACE",FACE,{"disambiguationData":[OSD([sQuery(id+"F4.wireOp",EDGE,"E234")])]})]});
            var Q77;
            Q77=makeQuery(id+"F5.boolean.opBoolean","INTERSECT",EDGE,{"disambiguationData":[OD(1.0)],"derivedFrom":[makeQuery(id+"F1.opExtrude","SWEPT_FACE",FACE,{"disambiguationData":[OSD([sQuery(id+"F0.wireOp",EDGE,"E0")])]}),makeQuery(id+"F5.opExtrude","SWEPT_FACE",FACE,{"disambiguationData":[OSD([sQuery(id+"F4.wireOp",EDGE,"E233")])]})]});
            var Q78;
            Q78=makeQuery(id+"F5.boolean.opBoolean","INTERSECT",EDGE,{"disambiguationData":[OD(1.0)],"derivedFrom":[makeQuery(id+"F1.opExtrude","SWEPT_FACE",FACE,{"disambiguationData":[OSD([sQuery(id+"F0.wireOp",EDGE,"E0")])]}),makeQuery(id+"F5.opExtrude","SWEPT_FACE",FACE,{"disambiguationData":[OSD([sQuery(id+"F4.wireOp",EDGE,"E232")])]})]});
            var Q79;
            Q79=makeQuery(id+"F5.boolean.opBoolean","INTERSECT",EDGE,{"disambiguationData":[OD(1.0)],"derivedFrom":[makeQuery(id+"F1.opExtrude","SWEPT_FACE",FACE,{"disambiguationData":[OSD([sQuery(id+"F0.wireOp",EDGE,"E0")])]}),makeQuery(id+"F5.opExtrude","SWEPT_FACE",FACE,{"disambiguationData":[OSD([sQuery(id+"F4.wireOp",EDGE,"E230")])]})]});
            var Q80;
            Q80=makeQuery(id+"F5.boolean.opBoolean","INTERSECT",EDGE,{"disambiguationData":[OD(1.0)],"derivedFrom":[makeQuery(id+"F1.opExtrude","SWEPT_FACE",FACE,{"disambiguationData":[OSD([sQuery(id+"F0.wireOp",EDGE,"E0")])]}),makeQuery(id+"F5.opExtrude","SWEPT_FACE",FACE,{"disambiguationData":[OSD([sQuery(id+"F4.wireOp",EDGE,"E217")])]})]});
            var Q81;
            Q81=makeQuery(id+"F5.boolean.opBoolean","INTERSECT",EDGE,{"disambiguationData":[OD(1.0)],"derivedFrom":[makeQuery(id+"F1.opExtrude","SWEPT_FACE",FACE,{"disambiguationData":[OSD([sQuery(id+"F0.wireOp",EDGE,"E0")])]}),makeQuery(id+"F5.opExtrude","SWEPT_FACE",FACE,{"disambiguationData":[OSD([sQuery(id+"F4.wireOp",EDGE,"E216")])]})]});
            var Q82;
            Q82=makeQuery(id+"F5.boolean.opBoolean","INTERSECT",EDGE,{"disambiguationData":[OD(1.0)],"derivedFrom":[makeQuery(id+"F1.opExtrude","SWEPT_FACE",FACE,{"disambiguationData":[OSD([sQuery(id+"F0.wireOp",EDGE,"E0")])]}),makeQuery(id+"F5.opExtrude","SWEPT_FACE",FACE,{"disambiguationData":[OSD([sQuery(id+"F4.wireOp",EDGE,"E215")])]})]});
            var Q83;
            Q83=makeQuery(id+"F5.boolean.opBoolean","INTERSECT",EDGE,{"disambiguationData":[OD(1.0)],"derivedFrom":[makeQuery(id+"F1.opExtrude","SWEPT_FACE",FACE,{"disambiguationData":[OSD([sQuery(id+"F0.wireOp",EDGE,"E0")])]}),makeQuery(id+"F5.opExtrude","SWEPT_FACE",FACE,{"disambiguationData":[OSD([sQuery(id+"F4.wireOp",EDGE,"E214")])]})]});
            var Q84;
            Q84=makeQuery(id+"F5.boolean.opBoolean","INTERSECT",EDGE,{"disambiguationData":[OD(1.0)],"derivedFrom":[makeQuery(id+"F1.opExtrude","SWEPT_FACE",FACE,{"disambiguationData":[OSD([sQuery(id+"F0.wireOp",EDGE,"E0")])]}),makeQuery(id+"F5.opExtrude","SWEPT_FACE",FACE,{"disambiguationData":[OSD([sQuery(id+"F4.wireOp",EDGE,"E213")])]})]});
            var Q85;
            Q85=makeQuery(id+"F5.boolean.opBoolean","INTERSECT",EDGE,{"disambiguationData":[OD(1.0)],"derivedFrom":[makeQuery(id+"F1.opExtrude","SWEPT_FACE",FACE,{"disambiguationData":[OSD([sQuery(id+"F0.wireOp",EDGE,"E0")])]}),makeQuery(id+"F5.opExtrude","SWEPT_FACE",FACE,{"disambiguationData":[OSD([sQuery(id+"F4.wireOp",EDGE,"E212")])]})]});
            var Q86;
            Q86=makeQuery(id+"F5.boolean.opBoolean","INTERSECT",EDGE,{"disambiguationData":[OD(1.0)],"derivedFrom":[makeQuery(id+"F1.opExtrude","SWEPT_FACE",FACE,{"disambiguationData":[OSD([sQuery(id+"F0.wireOp",EDGE,"E0")])]}),makeQuery(id+"F5.opExtrude","SWEPT_FACE",FACE,{"disambiguationData":[OSD([sQuery(id+"F4.wireOp",EDGE,"E199")])]})]});
            var Q87;
            Q87=makeQuery(id+"F5.boolean.opBoolean","INTERSECT",EDGE,{"disambiguationData":[OD(1.0)],"derivedFrom":[makeQuery(id+"F1.opExtrude","SWEPT_FACE",FACE,{"disambiguationData":[OSD([sQuery(id+"F0.wireOp",EDGE,"E0")])]}),makeQuery(id+"F5.opExtrude","SWEPT_FACE",FACE,{"disambiguationData":[OSD([sQuery(id+"F4.wireOp",EDGE,"E198")])]})]});
            var Q88;
            Q88=makeQuery(id+"F5.boolean.opBoolean","INTERSECT",EDGE,{"disambiguationData":[OD(1.0)],"derivedFrom":[makeQuery(id+"F1.opExtrude","SWEPT_FACE",FACE,{"disambiguationData":[OSD([sQuery(id+"F0.wireOp",EDGE,"E0")])]}),makeQuery(id+"F5.opExtrude","SWEPT_FACE",FACE,{"disambiguationData":[OSD([sQuery(id+"F4.wireOp",EDGE,"E197")])]})]});
            var Q89;
            Q89=makeQuery(id+"F5.boolean.opBoolean","INTERSECT",EDGE,{"disambiguationData":[OD(1.0)],"derivedFrom":[makeQuery(id+"F1.opExtrude","SWEPT_FACE",FACE,{"disambiguationData":[OSD([sQuery(id+"F0.wireOp",EDGE,"E0")])]}),makeQuery(id+"F5.opExtrude","SWEPT_FACE",FACE,{"disambiguationData":[OSD([sQuery(id+"F4.wireOp",EDGE,"E196")])]})]});
            var Q90;
            Q90=makeQuery(id+"F5.boolean.opBoolean","INTERSECT",EDGE,{"disambiguationData":[OD(1.0)],"derivedFrom":[makeQuery(id+"F1.opExtrude","SWEPT_FACE",FACE,{"disambiguationData":[OSD([sQuery(id+"F0.wireOp",EDGE,"E0")])]}),makeQuery(id+"F5.opExtrude","SWEPT_FACE",FACE,{"disambiguationData":[OSD([sQuery(id+"F4.wireOp",EDGE,"E195")])]})]});
            var Q91;
            Q91=makeQuery(id+"F5.boolean.opBoolean","INTERSECT",EDGE,{"disambiguationData":[OD(1.0)],"derivedFrom":[makeQuery(id+"F1.opExtrude","SWEPT_FACE",FACE,{"disambiguationData":[OSD([sQuery(id+"F0.wireOp",EDGE,"E0")])]}),makeQuery(id+"F5.opExtrude","SWEPT_FACE",FACE,{"disambiguationData":[OSD([sQuery(id+"F4.wireOp",EDGE,"E194")])]})]});
            var Q92;
            Q92=makeQuery(id+"F5.boolean.opBoolean","INTERSECT",EDGE,{"disambiguationData":[OD(1.0)],"derivedFrom":[makeQuery(id+"F1.opExtrude","SWEPT_FACE",FACE,{"disambiguationData":[OSD([sQuery(id+"F0.wireOp",EDGE,"E0")])]}),makeQuery(id+"F5.opExtrude","SWEPT_FACE",FACE,{"disambiguationData":[OSD([sQuery(id+"F4.wireOp",EDGE,"E181")])]})]});
            var Q93;
            Q93=makeQuery(id+"F5.boolean.opBoolean","INTERSECT",EDGE,{"disambiguationData":[OD(1.0)],"derivedFrom":[makeQuery(id+"F1.opExtrude","SWEPT_FACE",FACE,{"disambiguationData":[OSD([sQuery(id+"F0.wireOp",EDGE,"E0")])]}),makeQuery(id+"F5.opExtrude","SWEPT_FACE",FACE,{"disambiguationData":[OSD([sQuery(id+"F4.wireOp",EDGE,"E176")])]})]});
            var Q94;
            Q94=makeQuery(id+"F5.boolean.opBoolean","INTERSECT",EDGE,{"disambiguationData":[OD(1.0)],"derivedFrom":[makeQuery(id+"F1.opExtrude","SWEPT_FACE",FACE,{"disambiguationData":[OSD([sQuery(id+"F0.wireOp",EDGE,"E0")])]}),makeQuery(id+"F5.opExtrude","SWEPT_FACE",FACE,{"disambiguationData":[OSD([sQuery(id+"F4.wireOp",EDGE,"E177")])]})]});
            var Q95;
            Q95=makeQuery(id+"F5.boolean.opBoolean","INTERSECT",EDGE,{"disambiguationData":[OD(1.0)],"derivedFrom":[makeQuery(id+"F1.opExtrude","SWEPT_FACE",FACE,{"disambiguationData":[OSD([sQuery(id+"F0.wireOp",EDGE,"E0")])]}),makeQuery(id+"F5.opExtrude","SWEPT_FACE",FACE,{"disambiguationData":[OSD([sQuery(id+"F4.wireOp",EDGE,"E178")])]})]});
            var Q96;
            Q96=makeQuery(id+"F5.boolean.opBoolean","INTERSECT",EDGE,{"disambiguationData":[OD(1.0)],"derivedFrom":[makeQuery(id+"F1.opExtrude","SWEPT_FACE",FACE,{"disambiguationData":[OSD([sQuery(id+"F0.wireOp",EDGE,"E0")])]}),makeQuery(id+"F5.opExtrude","SWEPT_FACE",FACE,{"disambiguationData":[OSD([sQuery(id+"F4.wireOp",EDGE,"E179")])]})]});
            var Q97;
            Q97=makeQuery(id+"F5.boolean.opBoolean","INTERSECT",EDGE,{"disambiguationData":[OD(1.0)],"derivedFrom":[makeQuery(id+"F1.opExtrude","SWEPT_FACE",FACE,{"disambiguationData":[OSD([sQuery(id+"F0.wireOp",EDGE,"E0")])]}),makeQuery(id+"F5.opExtrude","SWEPT_FACE",FACE,{"disambiguationData":[OSD([sQuery(id+"F4.wireOp",EDGE,"E180")])]})]});
            var Q98;
            Q98=makeQuery(id+"F5.boolean.opBoolean","INTERSECT",EDGE,{"disambiguationData":[OD(1.0)],"derivedFrom":[makeQuery(id+"F1.opExtrude","SWEPT_FACE",FACE,{"disambiguationData":[OSD([sQuery(id+"F0.wireOp",EDGE,"E0")])]}),makeQuery(id+"F5.opExtrude","SWEPT_FACE",FACE,{"disambiguationData":[OSD([sQuery(id+"F4.wireOp",EDGE,"E163")])]})]});
            var Q99;
            Q99=makeQuery(id+"F5.boolean.opBoolean","INTERSECT",EDGE,{"disambiguationData":[OD(1.0)],"derivedFrom":[makeQuery(id+"F1.opExtrude","SWEPT_FACE",FACE,{"disambiguationData":[OSD([sQuery(id+"F0.wireOp",EDGE,"E0")])]}),makeQuery(id+"F5.opExtrude","SWEPT_FACE",FACE,{"disambiguationData":[OSD([sQuery(id+"F4.wireOp",EDGE,"E158")])]})]});
            var Q100;
            Q100=makeQuery(id+"F5.boolean.opBoolean","INTERSECT",EDGE,{"disambiguationData":[OD(1.0)],"derivedFrom":[makeQuery(id+"F1.opExtrude","SWEPT_FACE",FACE,{"disambiguationData":[OSD([sQuery(id+"F0.wireOp",EDGE,"E0")])]}),makeQuery(id+"F5.opExtrude","SWEPT_FACE",FACE,{"disambiguationData":[OSD([sQuery(id+"F4.wireOp",EDGE,"E159")])]})]});
            var Q101;
            Q101=makeQuery(id+"F5.boolean.opBoolean","INTERSECT",EDGE,{"disambiguationData":[OD(1.0)],"derivedFrom":[makeQuery(id+"F1.opExtrude","SWEPT_FACE",FACE,{"disambiguationData":[OSD([sQuery(id+"F0.wireOp",EDGE,"E0")])]}),makeQuery(id+"F5.opExtrude","SWEPT_FACE",FACE,{"disambiguationData":[OSD([sQuery(id+"F4.wireOp",EDGE,"E160")])]})]});
            var Q102;
            Q102=makeQuery(id+"F5.boolean.opBoolean","INTERSECT",EDGE,{"disambiguationData":[OD(1.0)],"derivedFrom":[makeQuery(id+"F1.opExtrude","SWEPT_FACE",FACE,{"disambiguationData":[OSD([sQuery(id+"F0.wireOp",EDGE,"E0")])]}),makeQuery(id+"F5.opExtrude","SWEPT_FACE",FACE,{"disambiguationData":[OSD([sQuery(id+"F4.wireOp",EDGE,"E161")])]})]});
            var Q103;
            Q103=makeQuery(id+"F5.boolean.opBoolean","INTERSECT",EDGE,{"disambiguationData":[OD(1.0)],"derivedFrom":[makeQuery(id+"F1.opExtrude","SWEPT_FACE",FACE,{"disambiguationData":[OSD([sQuery(id+"F0.wireOp",EDGE,"E0")])]}),makeQuery(id+"F5.opExtrude","SWEPT_FACE",FACE,{"disambiguationData":[OSD([sQuery(id+"F4.wireOp",EDGE,"E162")])]})]});
            var Q104;
            Q104=makeQuery(id+"F5.boolean.opBoolean","INTERSECT",EDGE,{"disambiguationData":[OD(1.0)],"derivedFrom":[makeQuery(id+"F1.opExtrude","SWEPT_FACE",FACE,{"disambiguationData":[OSD([sQuery(id+"F0.wireOp",EDGE,"E0")])]}),makeQuery(id+"F5.opExtrude","SWEPT_FACE",FACE,{"disambiguationData":[OSD([sQuery(id+"F4.wireOp",EDGE,"E145")])]})]});
            var Q105;
            Q105=makeQuery(id+"F5.boolean.opBoolean","INTERSECT",EDGE,{"disambiguationData":[OD(1.0)],"derivedFrom":[makeQuery(id+"F1.opExtrude","SWEPT_FACE",FACE,{"disambiguationData":[OSD([sQuery(id+"F0.wireOp",EDGE,"E0")])]}),makeQuery(id+"F5.opExtrude","SWEPT_FACE",FACE,{"disambiguationData":[OSD([sQuery(id+"F4.wireOp",EDGE,"E140")])]})]});
            var Q106;
            Q106=makeQuery(id+"F5.boolean.opBoolean","INTERSECT",EDGE,{"disambiguationData":[OD(1.0)],"derivedFrom":[makeQuery(id+"F1.opExtrude","SWEPT_FACE",FACE,{"disambiguationData":[OSD([sQuery(id+"F0.wireOp",EDGE,"E0")])]}),makeQuery(id+"F5.opExtrude","SWEPT_FACE",FACE,{"disambiguationData":[OSD([sQuery(id+"F4.wireOp",EDGE,"E141")])]})]});
            var Q107;
            Q107=makeQuery(id+"F5.boolean.opBoolean","INTERSECT",EDGE,{"disambiguationData":[OD(1.0)],"derivedFrom":[makeQuery(id+"F1.opExtrude","SWEPT_FACE",FACE,{"disambiguationData":[OSD([sQuery(id+"F0.wireOp",EDGE,"E0")])]}),makeQuery(id+"F5.opExtrude","SWEPT_FACE",FACE,{"disambiguationData":[OSD([sQuery(id+"F4.wireOp",EDGE,"E142")])]})]});
            var Q108;
            Q108=makeQuery(id+"F5.boolean.opBoolean","INTERSECT",EDGE,{"disambiguationData":[OD(1.0)],"derivedFrom":[makeQuery(id+"F1.opExtrude","SWEPT_FACE",FACE,{"disambiguationData":[OSD([sQuery(id+"F0.wireOp",EDGE,"E0")])]}),makeQuery(id+"F5.opExtrude","SWEPT_FACE",FACE,{"disambiguationData":[OSD([sQuery(id+"F4.wireOp",EDGE,"E143")])]})]});
            var Q109;
            Q109=makeQuery(id+"F5.boolean.opBoolean","INTERSECT",EDGE,{"disambiguationData":[OD(1.0)],"derivedFrom":[makeQuery(id+"F1.opExtrude","SWEPT_FACE",FACE,{"disambiguationData":[OSD([sQuery(id+"F0.wireOp",EDGE,"E0")])]}),makeQuery(id+"F5.opExtrude","SWEPT_FACE",FACE,{"disambiguationData":[OSD([sQuery(id+"F4.wireOp",EDGE,"E144")])]})]});
            var Q110;
            Q110=makeQuery(id+"F5.boolean.opBoolean","INTERSECT",EDGE,{"disambiguationData":[OD(1.0)],"derivedFrom":[makeQuery(id+"F1.opExtrude","SWEPT_FACE",FACE,{"disambiguationData":[OSD([sQuery(id+"F0.wireOp",EDGE,"E0")])]}),makeQuery(id+"F5.opExtrude","SWEPT_FACE",FACE,{"disambiguationData":[OSD([sQuery(id+"F4.wireOp",EDGE,"E127")])]})]});
            var Q111;
            Q111=makeQuery(id+"F5.boolean.opBoolean","INTERSECT",EDGE,{"disambiguationData":[OD(1.0)],"derivedFrom":[makeQuery(id+"F1.opExtrude","SWEPT_FACE",FACE,{"disambiguationData":[OSD([sQuery(id+"F0.wireOp",EDGE,"E0")])]}),makeQuery(id+"F5.opExtrude","SWEPT_FACE",FACE,{"disambiguationData":[OSD([sQuery(id+"F4.wireOp",EDGE,"E126")])]})]});
            var Q112;
            Q112=makeQuery(id+"F5.boolean.opBoolean","INTERSECT",EDGE,{"disambiguationData":[OD(1.0)],"derivedFrom":[makeQuery(id+"F1.opExtrude","SWEPT_FACE",FACE,{"disambiguationData":[OSD([sQuery(id+"F0.wireOp",EDGE,"E0")])]}),makeQuery(id+"F5.opExtrude","SWEPT_FACE",FACE,{"disambiguationData":[OSD([sQuery(id+"F4.wireOp",EDGE,"E125")])]})]});
            var Q113;
            Q113=makeQuery(id+"F5.boolean.opBoolean","INTERSECT",EDGE,{"disambiguationData":[OD(1.0)],"derivedFrom":[makeQuery(id+"F1.opExtrude","SWEPT_FACE",FACE,{"disambiguationData":[OSD([sQuery(id+"F0.wireOp",EDGE,"E0")])]}),makeQuery(id+"F5.opExtrude","SWEPT_FACE",FACE,{"disambiguationData":[OSD([sQuery(id+"F4.wireOp",EDGE,"E124")])]})]});
            var Q114;
            Q114=makeQuery(id+"F5.boolean.opBoolean","INTERSECT",EDGE,{"disambiguationData":[OD(1.0)],"derivedFrom":[makeQuery(id+"F1.opExtrude","SWEPT_FACE",FACE,{"disambiguationData":[OSD([sQuery(id+"F0.wireOp",EDGE,"E0")])]}),makeQuery(id+"F5.opExtrude","SWEPT_FACE",FACE,{"disambiguationData":[OSD([sQuery(id+"F4.wireOp",EDGE,"E123")])]})]});
            var Q115;
            Q115=makeQuery(id+"F5.boolean.opBoolean","INTERSECT",EDGE,{"disambiguationData":[OD(1.0)],"derivedFrom":[makeQuery(id+"F1.opExtrude","SWEPT_FACE",FACE,{"disambiguationData":[OSD([sQuery(id+"F0.wireOp",EDGE,"E0")])]}),makeQuery(id+"F5.opExtrude","SWEPT_FACE",FACE,{"disambiguationData":[OSD([sQuery(id+"F4.wireOp",EDGE,"E122")])]})]});
            var Q116;
            Q116=makeQuery(id+"F5.boolean.opBoolean","INTERSECT",EDGE,{"disambiguationData":[OD(1.0)],"derivedFrom":[makeQuery(id+"F1.opExtrude","SWEPT_FACE",FACE,{"disambiguationData":[OSD([sQuery(id+"F0.wireOp",EDGE,"E0")])]}),makeQuery(id+"F5.opExtrude","SWEPT_FACE",FACE,{"disambiguationData":[OSD([sQuery(id+"F4.wireOp",EDGE,"E109")])]})]});
            var Q117;
            Q117=makeQuery(id+"F5.boolean.opBoolean","INTERSECT",EDGE,{"disambiguationData":[OD(1.0)],"derivedFrom":[makeQuery(id+"F1.opExtrude","SWEPT_FACE",FACE,{"disambiguationData":[OSD([sQuery(id+"F0.wireOp",EDGE,"E0")])]}),makeQuery(id+"F5.opExtrude","SWEPT_FACE",FACE,{"disambiguationData":[OSD([sQuery(id+"F4.wireOp",EDGE,"E104")])]})]});
            var Q118;
            Q118=makeQuery(id+"F5.boolean.opBoolean","INTERSECT",EDGE,{"disambiguationData":[OD(1.0)],"derivedFrom":[makeQuery(id+"F1.opExtrude","SWEPT_FACE",FACE,{"disambiguationData":[OSD([sQuery(id+"F0.wireOp",EDGE,"E0")])]}),makeQuery(id+"F5.opExtrude","SWEPT_FACE",FACE,{"disambiguationData":[OSD([sQuery(id+"F4.wireOp",EDGE,"E105")])]})]});
            var Q119;
            Q119=makeQuery(id+"F5.boolean.opBoolean","INTERSECT",EDGE,{"disambiguationData":[OD(1.0)],"derivedFrom":[makeQuery(id+"F1.opExtrude","SWEPT_FACE",FACE,{"disambiguationData":[OSD([sQuery(id+"F0.wireOp",EDGE,"E0")])]}),makeQuery(id+"F5.opExtrude","SWEPT_FACE",FACE,{"disambiguationData":[OSD([sQuery(id+"F4.wireOp",EDGE,"E106")])]})]});
            var Q120;
            Q120=makeQuery(id+"F5.boolean.opBoolean","INTERSECT",EDGE,{"disambiguationData":[OD(1.0)],"derivedFrom":[makeQuery(id+"F1.opExtrude","SWEPT_FACE",FACE,{"disambiguationData":[OSD([sQuery(id+"F0.wireOp",EDGE,"E0")])]}),makeQuery(id+"F5.opExtrude","SWEPT_FACE",FACE,{"disambiguationData":[OSD([sQuery(id+"F4.wireOp",EDGE,"E107")])]})]});
            var Q121;
            Q121=makeQuery(id+"F5.boolean.opBoolean","INTERSECT",EDGE,{"disambiguationData":[OD(1.0)],"derivedFrom":[makeQuery(id+"F1.opExtrude","SWEPT_FACE",FACE,{"disambiguationData":[OSD([sQuery(id+"F0.wireOp",EDGE,"E0")])]}),makeQuery(id+"F5.opExtrude","SWEPT_FACE",FACE,{"disambiguationData":[OSD([sQuery(id+"F4.wireOp",EDGE,"E108")])]})]});
            var Q122;
            Q122=makeQuery(id+"F5.boolean.opBoolean","INTERSECT",EDGE,{"disambiguationData":[OD(1.0)],"derivedFrom":[makeQuery(id+"F1.opExtrude","SWEPT_FACE",FACE,{"disambiguationData":[OSD([sQuery(id+"F0.wireOp",EDGE,"E0")])]}),makeQuery(id+"F5.opExtrude","SWEPT_FACE",FACE,{"disambiguationData":[OSD([sQuery(id+"F4.wireOp",EDGE,"E91")])]})]});
            var Q123;
            Q123=makeQuery(id+"F5.boolean.opBoolean","INTERSECT",EDGE,{"disambiguationData":[OD(1.0)],"derivedFrom":[makeQuery(id+"F1.opExtrude","SWEPT_FACE",FACE,{"disambiguationData":[OSD([sQuery(id+"F0.wireOp",EDGE,"E0")])]}),makeQuery(id+"F5.opExtrude","SWEPT_FACE",FACE,{"disambiguationData":[OSD([sQuery(id+"F4.wireOp",EDGE,"E90")])]})]});
            var Q124;
            Q124=makeQuery(id+"F5.boolean.opBoolean","INTERSECT",EDGE,{"disambiguationData":[OD(1.0)],"derivedFrom":[makeQuery(id+"F1.opExtrude","SWEPT_FACE",FACE,{"disambiguationData":[OSD([sQuery(id+"F0.wireOp",EDGE,"E0")])]}),makeQuery(id+"F5.opExtrude","SWEPT_FACE",FACE,{"disambiguationData":[OSD([sQuery(id+"F4.wireOp",EDGE,"E89")])]})]});
            var Q125;
            Q125=makeQuery(id+"F5.boolean.opBoolean","INTERSECT",EDGE,{"disambiguationData":[OD(1.0)],"derivedFrom":[makeQuery(id+"F1.opExtrude","SWEPT_FACE",FACE,{"disambiguationData":[OSD([sQuery(id+"F0.wireOp",EDGE,"E0")])]}),makeQuery(id+"F5.opExtrude","SWEPT_FACE",FACE,{"disambiguationData":[OSD([sQuery(id+"F4.wireOp",EDGE,"E88")])]})]});
            var Q126;
            Q126=makeQuery(id+"F5.boolean.opBoolean","INTERSECT",EDGE,{"disambiguationData":[OD(1.0)],"derivedFrom":[makeQuery(id+"F1.opExtrude","SWEPT_FACE",FACE,{"disambiguationData":[OSD([sQuery(id+"F0.wireOp",EDGE,"E0")])]}),makeQuery(id+"F5.opExtrude","SWEPT_FACE",FACE,{"disambiguationData":[OSD([sQuery(id+"F4.wireOp",EDGE,"E87")])]})]});
            var Q127;
            Q127=makeQuery(id+"F5.boolean.opBoolean","INTERSECT",EDGE,{"disambiguationData":[OD(1.0)],"derivedFrom":[makeQuery(id+"F1.opExtrude","SWEPT_FACE",FACE,{"disambiguationData":[OSD([sQuery(id+"F0.wireOp",EDGE,"E0")])]}),makeQuery(id+"F5.opExtrude","SWEPT_FACE",FACE,{"disambiguationData":[OSD([sQuery(id+"F4.wireOp",EDGE,"E86")])]})]});
            var Q128;
            Q128=makeQuery(id+"F5.boolean.opBoolean","INTERSECT",EDGE,{"disambiguationData":[OD(1.0)],"derivedFrom":[makeQuery(id+"F1.opExtrude","SWEPT_FACE",FACE,{"disambiguationData":[OSD([sQuery(id+"F0.wireOp",EDGE,"E0")])]}),makeQuery(id+"F5.opExtrude","SWEPT_FACE",FACE,{"disambiguationData":[OSD([sQuery(id+"F4.wireOp",EDGE,"E73")])]})]});
            var Q129;
            Q129=makeQuery(id+"F5.boolean.opBoolean","INTERSECT",EDGE,{"disambiguationData":[OD(1.0)],"derivedFrom":[makeQuery(id+"F1.opExtrude","SWEPT_FACE",FACE,{"disambiguationData":[OSD([sQuery(id+"F0.wireOp",EDGE,"E0")])]}),makeQuery(id+"F5.opExtrude","SWEPT_FACE",FACE,{"disambiguationData":[OSD([sQuery(id+"F4.wireOp",EDGE,"E68")])]})]});
            var Q130;
            Q130=makeQuery(id+"F5.boolean.opBoolean","INTERSECT",EDGE,{"disambiguationData":[OD(1.0)],"derivedFrom":[makeQuery(id+"F1.opExtrude","SWEPT_FACE",FACE,{"disambiguationData":[OSD([sQuery(id+"F0.wireOp",EDGE,"E0")])]}),makeQuery(id+"F5.opExtrude","SWEPT_FACE",FACE,{"disambiguationData":[OSD([sQuery(id+"F4.wireOp",EDGE,"E72")])]})]});
            var Q131;
            Q131=makeQuery(id+"F5.boolean.opBoolean","INTERSECT",EDGE,{"disambiguationData":[OD(1.0)],"derivedFrom":[makeQuery(id+"F1.opExtrude","SWEPT_FACE",FACE,{"disambiguationData":[OSD([sQuery(id+"F0.wireOp",EDGE,"E0")])]}),makeQuery(id+"F5.opExtrude","SWEPT_FACE",FACE,{"disambiguationData":[OSD([sQuery(id+"F4.wireOp",EDGE,"E68")])]})]});
            var Q132;
            Q132=makeQuery(id+"F5.boolean.opBoolean","INTERSECT",EDGE,{"disambiguationData":[OD(1.0)],"derivedFrom":[makeQuery(id+"F1.opExtrude","SWEPT_FACE",FACE,{"disambiguationData":[OSD([sQuery(id+"F0.wireOp",EDGE,"E0")])]}),makeQuery(id+"F5.opExtrude","SWEPT_FACE",FACE,{"disambiguationData":[OSD([sQuery(id+"F4.wireOp",EDGE,"E69")])]})]});
            var Q133;
            Q133=makeQuery(id+"F5.boolean.opBoolean","INTERSECT",EDGE,{"disambiguationData":[OD(1.0)],"derivedFrom":[makeQuery(id+"F1.opExtrude","SWEPT_FACE",FACE,{"disambiguationData":[OSD([sQuery(id+"F0.wireOp",EDGE,"E0")])]}),makeQuery(id+"F5.opExtrude","SWEPT_FACE",FACE,{"disambiguationData":[OSD([sQuery(id+"F4.wireOp",EDGE,"E70")])]})]});
            var Q134;
            Q134=makeQuery(id+"F5.boolean.opBoolean","INTERSECT",EDGE,{"disambiguationData":[OD(1.0)],"derivedFrom":[makeQuery(id+"F1.opExtrude","SWEPT_FACE",FACE,{"disambiguationData":[OSD([sQuery(id+"F0.wireOp",EDGE,"E0")])]}),makeQuery(id+"F5.opExtrude","SWEPT_FACE",FACE,{"disambiguationData":[OSD([sQuery(id+"F4.wireOp",EDGE,"E71")])]})]});
            var Q135;
            Q135=makeQuery(id+"F5.boolean.opBoolean","INTERSECT",EDGE,{"disambiguationData":[OD(1.0)],"derivedFrom":[makeQuery(id+"F1.opExtrude","SWEPT_FACE",FACE,{"disambiguationData":[OSD([sQuery(id+"F0.wireOp",EDGE,"E0")])]}),makeQuery(id+"F5.opExtrude","SWEPT_FACE",FACE,{"disambiguationData":[OSD([sQuery(id+"F4.wireOp",EDGE,"E55")])]})]});
            var Q136;
            Q136=makeQuery(id+"F5.boolean.opBoolean","INTERSECT",EDGE,{"disambiguationData":[OD(1.0)],"derivedFrom":[makeQuery(id+"F1.opExtrude","SWEPT_FACE",FACE,{"disambiguationData":[OSD([sQuery(id+"F0.wireOp",EDGE,"E0")])]}),makeQuery(id+"F5.opExtrude","SWEPT_FACE",FACE,{"disambiguationData":[OSD([sQuery(id+"F4.wireOp",EDGE,"E54")])]})]});
            var Q137;
            Q137=makeQuery(id+"F5.boolean.opBoolean","INTERSECT",EDGE,{"disambiguationData":[OD(1.0)],"derivedFrom":[makeQuery(id+"F1.opExtrude","SWEPT_FACE",FACE,{"disambiguationData":[OSD([sQuery(id+"F0.wireOp",EDGE,"E0")])]}),makeQuery(id+"F5.opExtrude","SWEPT_FACE",FACE,{"disambiguationData":[OSD([sQuery(id+"F4.wireOp",EDGE,"E53")])]})]});
            var Q138;
            Q138=makeQuery(id+"F5.boolean.opBoolean","INTERSECT",EDGE,{"disambiguationData":[OD(1.0)],"derivedFrom":[makeQuery(id+"F1.opExtrude","SWEPT_FACE",FACE,{"disambiguationData":[OSD([sQuery(id+"F0.wireOp",EDGE,"E0")])]}),makeQuery(id+"F5.opExtrude","SWEPT_FACE",FACE,{"disambiguationData":[OSD([sQuery(id+"F4.wireOp",EDGE,"E52")])]})]});
            var Q139;
            Q139=makeQuery(id+"F5.boolean.opBoolean","INTERSECT",EDGE,{"disambiguationData":[OD(1.0)],"derivedFrom":[makeQuery(id+"F1.opExtrude","SWEPT_FACE",FACE,{"disambiguationData":[OSD([sQuery(id+"F0.wireOp",EDGE,"E0")])]}),makeQuery(id+"F5.opExtrude","SWEPT_FACE",FACE,{"disambiguationData":[OSD([sQuery(id+"F4.wireOp",EDGE,"E51")])]})]});
            var Q140;
            Q140=makeQuery(id+"F5.boolean.opBoolean","INTERSECT",EDGE,{"disambiguationData":[OD(1.0)],"derivedFrom":[makeQuery(id+"F1.opExtrude","SWEPT_FACE",FACE,{"disambiguationData":[OSD([sQuery(id+"F0.wireOp",EDGE,"E0")])]}),makeQuery(id+"F5.opExtrude","SWEPT_FACE",FACE,{"disambiguationData":[OSD([sQuery(id+"F4.wireOp",EDGE,"E50")])]})]});
            var Q141;
            Q141=makeQuery(id+"F5.boolean.opBoolean","INTERSECT",EDGE,{"disambiguationData":[OD(1.0)],"derivedFrom":[makeQuery(id+"F1.opExtrude","SWEPT_FACE",FACE,{"disambiguationData":[OSD([sQuery(id+"F0.wireOp",EDGE,"E0")])]}),makeQuery(id+"F5.opExtrude","SWEPT_FACE",FACE,{"disambiguationData":[OSD([sQuery(id+"F4.wireOp",EDGE,"E32")])]})]});
            var Q142;
            Q142=makeQuery(id+"F5.boolean.opBoolean","INTERSECT",EDGE,{"disambiguationData":[OD(1.0)],"derivedFrom":[makeQuery(id+"F1.opExtrude","SWEPT_FACE",FACE,{"disambiguationData":[OSD([sQuery(id+"F0.wireOp",EDGE,"E0")])]}),makeQuery(id+"F5.opExtrude","SWEPT_FACE",FACE,{"disambiguationData":[OSD([sQuery(id+"F4.wireOp",EDGE,"E37")])]})]});
            var Q143;
            Q143=makeQuery(id+"F5.boolean.opBoolean","INTERSECT",EDGE,{"disambiguationData":[OD(1.0)],"derivedFrom":[makeQuery(id+"F1.opExtrude","SWEPT_FACE",FACE,{"disambiguationData":[OSD([sQuery(id+"F0.wireOp",EDGE,"E0")])]}),makeQuery(id+"F5.opExtrude","SWEPT_FACE",FACE,{"disambiguationData":[OSD([sQuery(id+"F4.wireOp",EDGE,"E36")])]})]});
            var Q144;
            Q144=makeQuery(id+"F5.boolean.opBoolean","INTERSECT",EDGE,{"disambiguationData":[OD(1.0)],"derivedFrom":[makeQuery(id+"F1.opExtrude","SWEPT_FACE",FACE,{"disambiguationData":[OSD([sQuery(id+"F0.wireOp",EDGE,"E0")])]}),makeQuery(id+"F5.opExtrude","SWEPT_FACE",FACE,{"disambiguationData":[OSD([sQuery(id+"F4.wireOp",EDGE,"E35")])]})]});
            var Q145;
            Q145=makeQuery(id+"F5.boolean.opBoolean","INTERSECT",EDGE,{"disambiguationData":[OD(1.0)],"derivedFrom":[makeQuery(id+"F1.opExtrude","SWEPT_FACE",FACE,{"disambiguationData":[OSD([sQuery(id+"F0.wireOp",EDGE,"E0")])]}),makeQuery(id+"F5.opExtrude","SWEPT_FACE",FACE,{"disambiguationData":[OSD([sQuery(id+"F4.wireOp",EDGE,"E34")])]})]});
            var Q146;
            Q146=makeQuery(id+"F5.boolean.opBoolean","INTERSECT",EDGE,{"disambiguationData":[OD(1.0)],"derivedFrom":[makeQuery(id+"F1.opExtrude","SWEPT_FACE",FACE,{"disambiguationData":[OSD([sQuery(id+"F0.wireOp",EDGE,"E0")])]}),makeQuery(id+"F5.opExtrude","SWEPT_FACE",FACE,{"disambiguationData":[OSD([sQuery(id+"F4.wireOp",EDGE,"E33")])]})]});
            var Q147;
            Q147=makeQuery(id+"F5.boolean.opBoolean","INTERSECT",EDGE,{"disambiguationData":[OD(1.0)],"derivedFrom":[makeQuery(id+"F1.opExtrude","SWEPT_FACE",FACE,{"disambiguationData":[OSD([sQuery(id+"F0.wireOp",EDGE,"E0")])]}),makeQuery(id+"F5.opExtrude","SWEPT_FACE",FACE,{"disambiguationData":[OSD([sQuery(id+"F4.wireOp",EDGE,"E231")])]})]});
            fillet(context, id + "F15", {"entities" : qUnion([Q0, Q1, Q2, Q3, Q4, Q5, Q6, Q7, Q8, Q9, Q10, Q11, Q12, Q13, Q14, Q15, Q16, Q17, Q18, Q19, Q20, Q21, Q22, Q23, Q24, Q25, Q26, Q27, Q28, Q29, Q30, Q31, Q32, Q33, Q34, Q35, Q36, Q37, Q38, Q39, Q40, Q41, Q42, Q43, Q44, Q45, Q46, Q47, Q48, Q49, Q50, Q51, Q52, Q53, Q54, Q55, Q56, Q57, Q58, Q59, Q60, Q61, Q62, Q63, Q64, Q65, Q66, Q67, Q68, Q69, Q70, Q71, Q72, Q73, Q74, Q75, Q76, Q77, Q78, Q79, Q80, Q81, Q82, Q83, Q84, Q85, Q86, Q87, Q88, Q89, Q90, Q91, Q92, Q93, Q94, Q95, Q96, Q97, Q98, Q99, Q100, Q101, Q102, Q103, Q104, Q105, Q106, Q107, Q108, Q109, Q110, Q111, Q112, Q113, Q114, Q115, Q116, Q117, Q118, Q119, Q120, Q121, Q122, Q123, Q124, Q125, Q126, Q127, Q128, Q129, Q130, Q131, Q132, Q133, Q134, Q135, Q136, Q137, Q138, Q139, Q140, Q141, Q142, Q143, Q144, Q145, Q146, Q147]), "radius" : 0.4 * mm, "tangentPropagation" : true, "allowEdgeOverflow" : false});
        }
        {
            var Q0;
            Q0=makeQuery(id+"F10.boolean.opBoolean","INTERSECT",EDGE,{"disambiguationData":[OD(1.0)],"derivedFrom":[makeQuery(id+"F1.opExtrude","SWEPT_FACE",FACE,{"disambiguationData":[OSD([sQuery(id+"F0.wireOp",EDGE,"E0")])]}),makeQuery(id+"F10.opExtrude","SWEPT_FACE",FACE,{"disambiguationData":[OSD([sQuery(id+"F9.wireOp",EDGE,"E547")])]})]});
            var Q1;
            Q1=makeQuery(id+"F10.boolean.opBoolean","INTERSECT",EDGE,{"disambiguationData":[OD(1.0)],"derivedFrom":[makeQuery(id+"F1.opExtrude","SWEPT_FACE",FACE,{"disambiguationData":[OSD([sQuery(id+"F0.wireOp",EDGE,"E0")])]}),makeQuery(id+"F10.opExtrude","SWEPT_FACE",FACE,{"disambiguationData":[OSD([sQuery(id+"F9.wireOp",EDGE,"E546")])]})]});
            var Q2;
            Q2=makeQuery(id+"F10.boolean.opBoolean","INTERSECT",EDGE,{"disambiguationData":[OD(1.0)],"derivedFrom":[makeQuery(id+"F1.opExtrude","SWEPT_FACE",FACE,{"disambiguationData":[OSD([sQuery(id+"F0.wireOp",EDGE,"E0")])]}),makeQuery(id+"F10.opExtrude","SWEPT_FACE",FACE,{"disambiguationData":[OSD([sQuery(id+"F9.wireOp",EDGE,"E545")])]})]});
            var Q3;
            Q3=makeQuery(id+"F10.boolean.opBoolean","INTERSECT",EDGE,{"disambiguationData":[OD(1.0)],"derivedFrom":[makeQuery(id+"F1.opExtrude","SWEPT_FACE",FACE,{"disambiguationData":[OSD([sQuery(id+"F0.wireOp",EDGE,"E0")])]}),makeQuery(id+"F10.opExtrude","SWEPT_FACE",FACE,{"disambiguationData":[OSD([sQuery(id+"F9.wireOp",EDGE,"E530")])]})]});
            var Q4;
            Q4=makeQuery(id+"F10.boolean.opBoolean","INTERSECT",EDGE,{"disambiguationData":[OD(1.0)],"derivedFrom":[makeQuery(id+"F1.opExtrude","SWEPT_FACE",FACE,{"disambiguationData":[OSD([sQuery(id+"F0.wireOp",EDGE,"E0")])]}),makeQuery(id+"F10.opExtrude","SWEPT_FACE",FACE,{"disambiguationData":[OSD([sQuery(id+"F9.wireOp",EDGE,"E525")])]})]});
            var Q5;
            Q5=makeQuery(id+"F10.boolean.opBoolean","INTERSECT",EDGE,{"disambiguationData":[OD(1.0)],"derivedFrom":[makeQuery(id+"F1.opExtrude","SWEPT_FACE",FACE,{"disambiguationData":[OSD([sQuery(id+"F0.wireOp",EDGE,"E0")])]}),makeQuery(id+"F10.opExtrude","SWEPT_FACE",FACE,{"disambiguationData":[OSD([sQuery(id+"F9.wireOp",EDGE,"E529")])]})]});
            var Q6;
            Q6=makeQuery(id+"F10.boolean.opBoolean","INTERSECT",EDGE,{"disambiguationData":[OD(1.0)],"derivedFrom":[makeQuery(id+"F1.opExtrude","SWEPT_FACE",FACE,{"disambiguationData":[OSD([sQuery(id+"F0.wireOp",EDGE,"E0")])]}),makeQuery(id+"F10.opExtrude","SWEPT_FACE",FACE,{"disambiguationData":[OSD([sQuery(id+"F9.wireOp",EDGE,"E528")])]})]});
            var Q7;
            Q7=makeQuery(id+"F10.boolean.opBoolean","INTERSECT",EDGE,{"disambiguationData":[OD(1.0)],"derivedFrom":[makeQuery(id+"F1.opExtrude","SWEPT_FACE",FACE,{"disambiguationData":[OSD([sQuery(id+"F0.wireOp",EDGE,"E0")])]}),makeQuery(id+"F10.opExtrude","SWEPT_FACE",FACE,{"disambiguationData":[OSD([sQuery(id+"F9.wireOp",EDGE,"E526")])]})]});
            var Q8;
            Q8=makeQuery(id+"F10.boolean.opBoolean","INTERSECT",EDGE,{"disambiguationData":[OD(1.0)],"derivedFrom":[makeQuery(id+"F1.opExtrude","SWEPT_FACE",FACE,{"disambiguationData":[OSD([sQuery(id+"F0.wireOp",EDGE,"E0")])]}),makeQuery(id+"F10.opExtrude","SWEPT_FACE",FACE,{"disambiguationData":[OSD([sQuery(id+"F9.wireOp",EDGE,"E527")])]})]});
            var Q9;
            Q9=makeQuery(id+"F10.boolean.opBoolean","INTERSECT",EDGE,{"disambiguationData":[OD(1.0)],"derivedFrom":[makeQuery(id+"F1.opExtrude","SWEPT_FACE",FACE,{"disambiguationData":[OSD([sQuery(id+"F0.wireOp",EDGE,"E0")])]}),makeQuery(id+"F10.opExtrude","SWEPT_FACE",FACE,{"disambiguationData":[OSD([sQuery(id+"F9.wireOp",EDGE,"E512")])]})]});
            var Q10;
            Q10=makeQuery(id+"F10.boolean.opBoolean","INTERSECT",EDGE,{"disambiguationData":[OD(1.0)],"derivedFrom":[makeQuery(id+"F1.opExtrude","SWEPT_FACE",FACE,{"disambiguationData":[OSD([sQuery(id+"F0.wireOp",EDGE,"E0")])]}),makeQuery(id+"F10.opExtrude","SWEPT_FACE",FACE,{"disambiguationData":[OSD([sQuery(id+"F9.wireOp",EDGE,"E756")])]})]});
            var Q11;
            Q11=makeQuery(id+"F10.boolean.opBoolean","INTERSECT",EDGE,{"disambiguationData":[OD(1.0)],"derivedFrom":[makeQuery(id+"F1.opExtrude","SWEPT_FACE",FACE,{"disambiguationData":[OSD([sQuery(id+"F0.wireOp",EDGE,"E0")])]}),makeQuery(id+"F10.opExtrude","SWEPT_FACE",FACE,{"disambiguationData":[OSD([sQuery(id+"F9.wireOp",EDGE,"E754"),sQuery(id+"F9.wireOp",EDGE,"E755")])]})]});
            var Q12;
            Q12=makeQuery(id+"F10.boolean.opBoolean","INTERSECT",EDGE,{"disambiguationData":[OD(1.0)],"derivedFrom":[makeQuery(id+"F1.opExtrude","SWEPT_FACE",FACE,{"disambiguationData":[OSD([sQuery(id+"F0.wireOp",EDGE,"E0")])]}),makeQuery(id+"F10.opExtrude","SWEPT_FACE",FACE,{"disambiguationData":[OSD([sQuery(id+"F9.wireOp",EDGE,"E757")])]})]});
            var Q13;
            Q13=makeQuery(id+"F7.boolean.opBoolean","INTERSECT",EDGE,{"disambiguationData":[OD(1.0)],"derivedFrom":[makeQuery(id+"F1.opExtrude","SWEPT_FACE",FACE,{"disambiguationData":[OSD([sQuery(id+"F0.wireOp",EDGE,"E0")])]}),makeQuery(id+"F7.opExtrude","SWEPT_FACE",FACE,{"disambiguationData":[OSD([sQuery(id+"F6.wireOp",EDGE,"E268")])]})]});
            var Q14;
            Q14=makeQuery(id+"F7.boolean.opBoolean","INTERSECT",EDGE,{"disambiguationData":[OD(1.0)],"derivedFrom":[makeQuery(id+"F1.opExtrude","SWEPT_FACE",FACE,{"disambiguationData":[OSD([sQuery(id+"F0.wireOp",EDGE,"E0")])]}),makeQuery(id+"F7.opExtrude","SWEPT_FACE",FACE,{"disambiguationData":[OSD([sQuery(id+"F6.wireOp",EDGE,"E267")])]})]});
            var Q15;
            Q15=makeQuery(id+"F7.boolean.opBoolean","INTERSECT",EDGE,{"disambiguationData":[OD(1.0)],"derivedFrom":[makeQuery(id+"F1.opExtrude","SWEPT_FACE",FACE,{"disambiguationData":[OSD([sQuery(id+"F0.wireOp",EDGE,"E0")])]}),makeQuery(id+"F7.opExtrude","SWEPT_FACE",FACE,{"disambiguationData":[OSD([sQuery(id+"F6.wireOp",EDGE,"E266")])]})]});
            var Q16;
            Q16=makeQuery(id+"F7.boolean.opBoolean","INTERSECT",EDGE,{"disambiguationData":[OD(1.0)],"derivedFrom":[makeQuery(id+"F1.opExtrude","SWEPT_FACE",FACE,{"disambiguationData":[OSD([sQuery(id+"F0.wireOp",EDGE,"E0")])]}),makeQuery(id+"F7.opExtrude","SWEPT_FACE",FACE,{"disambiguationData":[OSD([sQuery(id+"F6.wireOp",EDGE,"E271")])]})]});
            var Q17;
            Q17=makeQuery(id+"F7.boolean.opBoolean","INTERSECT",EDGE,{"disambiguationData":[OD(1.0)],"derivedFrom":[makeQuery(id+"F1.opExtrude","SWEPT_FACE",FACE,{"disambiguationData":[OSD([sQuery(id+"F0.wireOp",EDGE,"E0")])]}),makeQuery(id+"F7.opExtrude","SWEPT_FACE",FACE,{"disambiguationData":[OSD([sQuery(id+"F6.wireOp",EDGE,"E270")])]})]});
            var Q18;
            Q18=makeQuery(id+"F7.boolean.opBoolean","INTERSECT",EDGE,{"disambiguationData":[OD(1.0)],"derivedFrom":[makeQuery(id+"F1.opExtrude","SWEPT_FACE",FACE,{"disambiguationData":[OSD([sQuery(id+"F0.wireOp",EDGE,"E0")])]}),makeQuery(id+"F7.opExtrude","SWEPT_FACE",FACE,{"disambiguationData":[OSD([sQuery(id+"F6.wireOp",EDGE,"E286")])]})]});
            var Q19;
            Q19=makeQuery(id+"F7.boolean.opBoolean","INTERSECT",EDGE,{"disambiguationData":[OD(1.0)],"derivedFrom":[makeQuery(id+"F1.opExtrude","SWEPT_FACE",FACE,{"disambiguationData":[OSD([sQuery(id+"F0.wireOp",EDGE,"E0")])]}),makeQuery(id+"F7.opExtrude","SWEPT_FACE",FACE,{"disambiguationData":[OSD([sQuery(id+"F6.wireOp",EDGE,"E287")])]})]});
            var Q20;
            Q20=makeQuery(id+"F7.boolean.opBoolean","INTERSECT",EDGE,{"disambiguationData":[OD(1.0)],"derivedFrom":[makeQuery(id+"F1.opExtrude","SWEPT_FACE",FACE,{"disambiguationData":[OSD([sQuery(id+"F0.wireOp",EDGE,"E0")])]}),makeQuery(id+"F7.opExtrude","SWEPT_FACE",FACE,{"disambiguationData":[OSD([sQuery(id+"F6.wireOp",EDGE,"E285")])]})]});
            var Q21;
            Q21=makeQuery(id+"F7.boolean.opBoolean","INTERSECT",EDGE,{"disambiguationData":[OD(1.0)],"derivedFrom":[makeQuery(id+"F1.opExtrude","SWEPT_FACE",FACE,{"disambiguationData":[OSD([sQuery(id+"F0.wireOp",EDGE,"E0")])]}),makeQuery(id+"F7.opExtrude","SWEPT_FACE",FACE,{"disambiguationData":[OSD([sQuery(id+"F6.wireOp",EDGE,"E284")])]})]});
            var Q22;
            Q22=makeQuery(id+"F7.boolean.opBoolean","INTERSECT",EDGE,{"disambiguationData":[OD(1.0)],"derivedFrom":[makeQuery(id+"F1.opExtrude","SWEPT_FACE",FACE,{"disambiguationData":[OSD([sQuery(id+"F0.wireOp",EDGE,"E0")])]}),makeQuery(id+"F7.opExtrude","SWEPT_FACE",FACE,{"disambiguationData":[OSD([sQuery(id+"F6.wireOp",EDGE,"E288")])]})]});
            var Q23;
            Q23=makeQuery(id+"F7.boolean.opBoolean","INTERSECT",EDGE,{"disambiguationData":[OD(1.0)],"derivedFrom":[makeQuery(id+"F1.opExtrude","SWEPT_FACE",FACE,{"disambiguationData":[OSD([sQuery(id+"F0.wireOp",EDGE,"E0")])]}),makeQuery(id+"F7.opExtrude","SWEPT_FACE",FACE,{"disambiguationData":[OSD([sQuery(id+"F6.wireOp",EDGE,"E289")])]})]});
            var Q24;
            Q24=makeQuery(id+"F7.boolean.opBoolean","INTERSECT",EDGE,{"disambiguationData":[OD(1.0)],"derivedFrom":[makeQuery(id+"F1.opExtrude","SWEPT_FACE",FACE,{"disambiguationData":[OSD([sQuery(id+"F0.wireOp",EDGE,"E0")])]}),makeQuery(id+"F7.opExtrude","SWEPT_FACE",FACE,{"disambiguationData":[OSD([sQuery(id+"F6.wireOp",EDGE,"E307")])]})]});
            var Q25;
            Q25=makeQuery(id+"F7.boolean.opBoolean","INTERSECT",EDGE,{"disambiguationData":[OD(1.0)],"derivedFrom":[makeQuery(id+"F1.opExtrude","SWEPT_FACE",FACE,{"disambiguationData":[OSD([sQuery(id+"F0.wireOp",EDGE,"E0")])]}),makeQuery(id+"F7.opExtrude","SWEPT_FACE",FACE,{"disambiguationData":[OSD([sQuery(id+"F6.wireOp",EDGE,"E302")])]})]});
            var Q26;
            Q26=makeQuery(id+"F7.boolean.opBoolean","INTERSECT",EDGE,{"disambiguationData":[OD(1.0)],"derivedFrom":[makeQuery(id+"F1.opExtrude","SWEPT_FACE",FACE,{"disambiguationData":[OSD([sQuery(id+"F0.wireOp",EDGE,"E0")])]}),makeQuery(id+"F7.opExtrude","SWEPT_FACE",FACE,{"disambiguationData":[OSD([sQuery(id+"F6.wireOp",EDGE,"E303")])]})]});
            var Q27;
            Q27=makeQuery(id+"F7.boolean.opBoolean","INTERSECT",EDGE,{"disambiguationData":[OD(1.0)],"derivedFrom":[makeQuery(id+"F1.opExtrude","SWEPT_FACE",FACE,{"disambiguationData":[OSD([sQuery(id+"F0.wireOp",EDGE,"E0")])]}),makeQuery(id+"F7.opExtrude","SWEPT_FACE",FACE,{"disambiguationData":[OSD([sQuery(id+"F6.wireOp",EDGE,"E304")])]})]});
            var Q28;
            Q28=makeQuery(id+"F7.boolean.opBoolean","INTERSECT",EDGE,{"disambiguationData":[OD(1.0)],"derivedFrom":[makeQuery(id+"F1.opExtrude","SWEPT_FACE",FACE,{"disambiguationData":[OSD([sQuery(id+"F0.wireOp",EDGE,"E0")])]}),makeQuery(id+"F7.opExtrude","SWEPT_FACE",FACE,{"disambiguationData":[OSD([sQuery(id+"F6.wireOp",EDGE,"E305")])]})]});
            var Q29;
            Q29=makeQuery(id+"F7.boolean.opBoolean","INTERSECT",EDGE,{"disambiguationData":[OD(1.0)],"derivedFrom":[makeQuery(id+"F1.opExtrude","SWEPT_FACE",FACE,{"disambiguationData":[OSD([sQuery(id+"F0.wireOp",EDGE,"E0")])]}),makeQuery(id+"F7.opExtrude","SWEPT_FACE",FACE,{"disambiguationData":[OSD([sQuery(id+"F6.wireOp",EDGE,"E306")])]})]});
            var Q30;
            Q30=makeQuery(id+"F7.boolean.opBoolean","INTERSECT",EDGE,{"disambiguationData":[OD(1.0)],"derivedFrom":[makeQuery(id+"F1.opExtrude","SWEPT_FACE",FACE,{"disambiguationData":[OSD([sQuery(id+"F0.wireOp",EDGE,"E0")])]}),makeQuery(id+"F7.opExtrude","SWEPT_FACE",FACE,{"disambiguationData":[OSD([sQuery(id+"F6.wireOp",EDGE,"E323")])]})]});
            var Q31;
            Q31=makeQuery(id+"F7.boolean.opBoolean","INTERSECT",EDGE,{"disambiguationData":[OD(1.0)],"derivedFrom":[makeQuery(id+"F1.opExtrude","SWEPT_FACE",FACE,{"disambiguationData":[OSD([sQuery(id+"F0.wireOp",EDGE,"E0")])]}),makeQuery(id+"F7.opExtrude","SWEPT_FACE",FACE,{"disambiguationData":[OSD([sQuery(id+"F6.wireOp",EDGE,"E324")])]})]});
            var Q32;
            Q32=makeQuery(id+"F7.boolean.opBoolean","INTERSECT",EDGE,{"disambiguationData":[OD(1.0)],"derivedFrom":[makeQuery(id+"F1.opExtrude","SWEPT_FACE",FACE,{"disambiguationData":[OSD([sQuery(id+"F0.wireOp",EDGE,"E0")])]}),makeQuery(id+"F7.opExtrude","SWEPT_FACE",FACE,{"disambiguationData":[OSD([sQuery(id+"F6.wireOp",EDGE,"E325")])]})]});
            var Q33;
            Q33=makeQuery(id+"F7.boolean.opBoolean","INTERSECT",EDGE,{"disambiguationData":[OD(1.0)],"derivedFrom":[makeQuery(id+"F1.opExtrude","SWEPT_FACE",FACE,{"disambiguationData":[OSD([sQuery(id+"F0.wireOp",EDGE,"E0")])]}),makeQuery(id+"F7.opExtrude","SWEPT_FACE",FACE,{"disambiguationData":[OSD([sQuery(id+"F6.wireOp",EDGE,"E320")])]})]});
            var Q34;
            Q34=makeQuery(id+"F7.boolean.opBoolean","INTERSECT",EDGE,{"disambiguationData":[OD(1.0)],"derivedFrom":[makeQuery(id+"F1.opExtrude","SWEPT_FACE",FACE,{"disambiguationData":[OSD([sQuery(id+"F0.wireOp",EDGE,"E0")])]}),makeQuery(id+"F7.opExtrude","SWEPT_FACE",FACE,{"disambiguationData":[OSD([sQuery(id+"F6.wireOp",EDGE,"E321")])]})]});
            var Q35;
            Q35=makeQuery(id+"F7.boolean.opBoolean","INTERSECT",EDGE,{"disambiguationData":[OD(1.0)],"derivedFrom":[makeQuery(id+"F1.opExtrude","SWEPT_FACE",FACE,{"disambiguationData":[OSD([sQuery(id+"F0.wireOp",EDGE,"E0")])]}),makeQuery(id+"F7.opExtrude","SWEPT_FACE",FACE,{"disambiguationData":[OSD([sQuery(id+"F6.wireOp",EDGE,"E322")])]})]});
            var Q36;
            Q36=makeQuery(id+"F7.boolean.opBoolean","INTERSECT",EDGE,{"disambiguationData":[OD(1.0)],"derivedFrom":[makeQuery(id+"F1.opExtrude","SWEPT_FACE",FACE,{"disambiguationData":[OSD([sQuery(id+"F0.wireOp",EDGE,"E0")])]}),makeQuery(id+"F7.opExtrude","SWEPT_FACE",FACE,{"disambiguationData":[OSD([sQuery(id+"F6.wireOp",EDGE,"E343")])]})]});
            var Q37;
            Q37=makeQuery(id+"F7.boolean.opBoolean","INTERSECT",EDGE,{"disambiguationData":[OD(1.0)],"derivedFrom":[makeQuery(id+"F1.opExtrude","SWEPT_FACE",FACE,{"disambiguationData":[OSD([sQuery(id+"F0.wireOp",EDGE,"E0")])]}),makeQuery(id+"F7.opExtrude","SWEPT_FACE",FACE,{"disambiguationData":[OSD([sQuery(id+"F6.wireOp",EDGE,"E342")])]})]});
            var Q38;
            Q38=makeQuery(id+"F7.boolean.opBoolean","INTERSECT",EDGE,{"disambiguationData":[OD(1.0)],"derivedFrom":[makeQuery(id+"F1.opExtrude","SWEPT_FACE",FACE,{"disambiguationData":[OSD([sQuery(id+"F0.wireOp",EDGE,"E0")])]}),makeQuery(id+"F7.opExtrude","SWEPT_FACE",FACE,{"disambiguationData":[OSD([sQuery(id+"F6.wireOp",EDGE,"E341")])]})]});
            var Q39;
            Q39=makeQuery(id+"F7.boolean.opBoolean","INTERSECT",EDGE,{"disambiguationData":[OD(1.0)],"derivedFrom":[makeQuery(id+"F1.opExtrude","SWEPT_FACE",FACE,{"disambiguationData":[OSD([sQuery(id+"F0.wireOp",EDGE,"E0")])]}),makeQuery(id+"F7.opExtrude","SWEPT_FACE",FACE,{"disambiguationData":[OSD([sQuery(id+"F6.wireOp",EDGE,"E340")])]})]});
            var Q40;
            Q40=makeQuery(id+"F7.boolean.opBoolean","INTERSECT",EDGE,{"disambiguationData":[OD(1.0)],"derivedFrom":[makeQuery(id+"F1.opExtrude","SWEPT_FACE",FACE,{"disambiguationData":[OSD([sQuery(id+"F0.wireOp",EDGE,"E0")])]}),makeQuery(id+"F7.opExtrude","SWEPT_FACE",FACE,{"disambiguationData":[OSD([sQuery(id+"F6.wireOp",EDGE,"E339")])]})]});
            var Q41;
            Q41=makeQuery(id+"F7.boolean.opBoolean","INTERSECT",EDGE,{"disambiguationData":[OD(1.0)],"derivedFrom":[makeQuery(id+"F1.opExtrude","SWEPT_FACE",FACE,{"disambiguationData":[OSD([sQuery(id+"F0.wireOp",EDGE,"E0")])]}),makeQuery(id+"F7.opExtrude","SWEPT_FACE",FACE,{"disambiguationData":[OSD([sQuery(id+"F6.wireOp",EDGE,"E338")])]})]});
            var Q42;
            Q42=makeQuery(id+"F7.boolean.opBoolean","INTERSECT",EDGE,{"disambiguationData":[OD(1.0)],"derivedFrom":[makeQuery(id+"F1.opExtrude","SWEPT_FACE",FACE,{"disambiguationData":[OSD([sQuery(id+"F0.wireOp",EDGE,"E0")])]}),makeQuery(id+"F7.opExtrude","SWEPT_FACE",FACE,{"disambiguationData":[OSD([sQuery(id+"F6.wireOp",EDGE,"E339")])]})]});
            var Q43;
            Q43=makeQuery(id+"F7.boolean.opBoolean","INTERSECT",EDGE,{"disambiguationData":[OD(1.0)],"derivedFrom":[makeQuery(id+"F1.opExtrude","SWEPT_FACE",FACE,{"disambiguationData":[OSD([sQuery(id+"F0.wireOp",EDGE,"E0")])]}),makeQuery(id+"F7.opExtrude","SWEPT_FACE",FACE,{"disambiguationData":[OSD([sQuery(id+"F6.wireOp",EDGE,"E361")])]})]});
            var Q44;
            Q44=makeQuery(id+"F7.boolean.opBoolean","INTERSECT",EDGE,{"disambiguationData":[OD(1.0)],"derivedFrom":[makeQuery(id+"F1.opExtrude","SWEPT_FACE",FACE,{"disambiguationData":[OSD([sQuery(id+"F0.wireOp",EDGE,"E0")])]}),makeQuery(id+"F7.opExtrude","SWEPT_FACE",FACE,{"disambiguationData":[OSD([sQuery(id+"F6.wireOp",EDGE,"E356")])]})]});
            var Q45;
            Q45=makeQuery(id+"F7.boolean.opBoolean","INTERSECT",EDGE,{"disambiguationData":[OD(1.0)],"derivedFrom":[makeQuery(id+"F1.opExtrude","SWEPT_FACE",FACE,{"disambiguationData":[OSD([sQuery(id+"F0.wireOp",EDGE,"E0")])]}),makeQuery(id+"F7.opExtrude","SWEPT_FACE",FACE,{"disambiguationData":[OSD([sQuery(id+"F6.wireOp",EDGE,"E357")])]})]});
            var Q46;
            Q46=makeQuery(id+"F7.boolean.opBoolean","INTERSECT",EDGE,{"disambiguationData":[OD(1.0)],"derivedFrom":[makeQuery(id+"F1.opExtrude","SWEPT_FACE",FACE,{"disambiguationData":[OSD([sQuery(id+"F0.wireOp",EDGE,"E0")])]}),makeQuery(id+"F7.opExtrude","SWEPT_FACE",FACE,{"disambiguationData":[OSD([sQuery(id+"F6.wireOp",EDGE,"E358")])]})]});
            var Q47;
            Q47=makeQuery(id+"F7.boolean.opBoolean","INTERSECT",EDGE,{"disambiguationData":[OD(1.0)],"derivedFrom":[makeQuery(id+"F1.opExtrude","SWEPT_FACE",FACE,{"disambiguationData":[OSD([sQuery(id+"F0.wireOp",EDGE,"E0")])]}),makeQuery(id+"F7.opExtrude","SWEPT_FACE",FACE,{"disambiguationData":[OSD([sQuery(id+"F6.wireOp",EDGE,"E359")])]})]});
            var Q48;
            Q48=makeQuery(id+"F7.boolean.opBoolean","INTERSECT",EDGE,{"disambiguationData":[OD(1.0)],"derivedFrom":[makeQuery(id+"F1.opExtrude","SWEPT_FACE",FACE,{"disambiguationData":[OSD([sQuery(id+"F0.wireOp",EDGE,"E0")])]}),makeQuery(id+"F7.opExtrude","SWEPT_FACE",FACE,{"disambiguationData":[OSD([sQuery(id+"F6.wireOp",EDGE,"E360")])]})]});
            var Q49;
            Q49=makeQuery(id+"F7.boolean.opBoolean","INTERSECT",EDGE,{"disambiguationData":[OD(1.0)],"derivedFrom":[makeQuery(id+"F1.opExtrude","SWEPT_FACE",FACE,{"disambiguationData":[OSD([sQuery(id+"F0.wireOp",EDGE,"E0")])]}),makeQuery(id+"F7.opExtrude","SWEPT_FACE",FACE,{"disambiguationData":[OSD([sQuery(id+"F6.wireOp",EDGE,"E377")])]})]});
            var Q50;
            Q50=makeQuery(id+"F7.boolean.opBoolean","INTERSECT",EDGE,{"disambiguationData":[OD(1.0)],"derivedFrom":[makeQuery(id+"F1.opExtrude","SWEPT_FACE",FACE,{"disambiguationData":[OSD([sQuery(id+"F0.wireOp",EDGE,"E0")])]}),makeQuery(id+"F7.opExtrude","SWEPT_FACE",FACE,{"disambiguationData":[OSD([sQuery(id+"F6.wireOp",EDGE,"E378")])]})]});
            var Q51;
            Q51=makeQuery(id+"F7.boolean.opBoolean","INTERSECT",EDGE,{"disambiguationData":[OD(1.0)],"derivedFrom":[makeQuery(id+"F1.opExtrude","SWEPT_FACE",FACE,{"disambiguationData":[OSD([sQuery(id+"F0.wireOp",EDGE,"E0")])]}),makeQuery(id+"F7.opExtrude","SWEPT_FACE",FACE,{"disambiguationData":[OSD([sQuery(id+"F6.wireOp",EDGE,"E379")])]})]});
            var Q52;
            Q52=makeQuery(id+"F7.boolean.opBoolean","INTERSECT",EDGE,{"disambiguationData":[OD(1.0)],"derivedFrom":[makeQuery(id+"F1.opExtrude","SWEPT_FACE",FACE,{"disambiguationData":[OSD([sQuery(id+"F0.wireOp",EDGE,"E0")])]}),makeQuery(id+"F7.opExtrude","SWEPT_FACE",FACE,{"disambiguationData":[OSD([sQuery(id+"F6.wireOp",EDGE,"E374")])]})]});
            var Q53;
            Q53=makeQuery(id+"F7.boolean.opBoolean","INTERSECT",EDGE,{"disambiguationData":[OD(1.0)],"derivedFrom":[makeQuery(id+"F1.opExtrude","SWEPT_FACE",FACE,{"disambiguationData":[OSD([sQuery(id+"F0.wireOp",EDGE,"E0")])]}),makeQuery(id+"F7.opExtrude","SWEPT_FACE",FACE,{"disambiguationData":[OSD([sQuery(id+"F6.wireOp",EDGE,"E375")])]})]});
            var Q54;
            Q54=makeQuery(id+"F7.boolean.opBoolean","INTERSECT",EDGE,{"disambiguationData":[OD(1.0)],"derivedFrom":[makeQuery(id+"F1.opExtrude","SWEPT_FACE",FACE,{"disambiguationData":[OSD([sQuery(id+"F0.wireOp",EDGE,"E0")])]}),makeQuery(id+"F7.opExtrude","SWEPT_FACE",FACE,{"disambiguationData":[OSD([sQuery(id+"F6.wireOp",EDGE,"E376")])]})]});
            var Q55;
            Q55=makeQuery(id+"F7.boolean.opBoolean","INTERSECT",EDGE,{"disambiguationData":[OD(1.0)],"derivedFrom":[makeQuery(id+"F1.opExtrude","SWEPT_FACE",FACE,{"disambiguationData":[OSD([sQuery(id+"F0.wireOp",EDGE,"E0")])]}),makeQuery(id+"F7.opExtrude","SWEPT_FACE",FACE,{"disambiguationData":[OSD([sQuery(id+"F6.wireOp",EDGE,"E397")])]})]});
            var Q56;
            Q56=makeQuery(id+"F7.boolean.opBoolean","INTERSECT",EDGE,{"disambiguationData":[OD(1.0)],"derivedFrom":[makeQuery(id+"F1.opExtrude","SWEPT_FACE",FACE,{"disambiguationData":[OSD([sQuery(id+"F0.wireOp",EDGE,"E0")])]}),makeQuery(id+"F7.opExtrude","SWEPT_FACE",FACE,{"disambiguationData":[OSD([sQuery(id+"F6.wireOp",EDGE,"E393")])]})]});
            var Q57;
            Q57=makeQuery(id+"F7.boolean.opBoolean","INTERSECT",EDGE,{"disambiguationData":[OD(1.0)],"derivedFrom":[makeQuery(id+"F1.opExtrude","SWEPT_FACE",FACE,{"disambiguationData":[OSD([sQuery(id+"F0.wireOp",EDGE,"E0")])]}),makeQuery(id+"F7.opExtrude","SWEPT_FACE",FACE,{"disambiguationData":[OSD([sQuery(id+"F6.wireOp",EDGE,"E394")])]})]});
            var Q58;
            Q58=makeQuery(id+"F7.boolean.opBoolean","INTERSECT",EDGE,{"disambiguationData":[OD(1.0)],"derivedFrom":[makeQuery(id+"F1.opExtrude","SWEPT_FACE",FACE,{"disambiguationData":[OSD([sQuery(id+"F0.wireOp",EDGE,"E0")])]}),makeQuery(id+"F7.opExtrude","SWEPT_FACE",FACE,{"disambiguationData":[OSD([sQuery(id+"F6.wireOp",EDGE,"E395")])]})]});
            var Q59;
            Q59=makeQuery(id+"F7.boolean.opBoolean","INTERSECT",EDGE,{"disambiguationData":[OD(1.0)],"derivedFrom":[makeQuery(id+"F1.opExtrude","SWEPT_FACE",FACE,{"disambiguationData":[OSD([sQuery(id+"F0.wireOp",EDGE,"E0")])]}),makeQuery(id+"F7.opExtrude","SWEPT_FACE",FACE,{"disambiguationData":[OSD([sQuery(id+"F6.wireOp",EDGE,"E396")])]})]});
            var Q60;
            Q60=makeQuery(id+"F7.boolean.opBoolean","INTERSECT",EDGE,{"disambiguationData":[OD(1.0)],"derivedFrom":[makeQuery(id+"F1.opExtrude","SWEPT_FACE",FACE,{"disambiguationData":[OSD([sQuery(id+"F0.wireOp",EDGE,"E0")])]}),makeQuery(id+"F7.opExtrude","SWEPT_FACE",FACE,{"disambiguationData":[OSD([sQuery(id+"F6.wireOp",EDGE,"E414")])]})]});
            var Q61;
            Q61=makeQuery(id+"F7.boolean.opBoolean","INTERSECT",EDGE,{"disambiguationData":[OD(1.0)],"derivedFrom":[makeQuery(id+"F1.opExtrude","SWEPT_FACE",FACE,{"disambiguationData":[OSD([sQuery(id+"F0.wireOp",EDGE,"E0")])]}),makeQuery(id+"F7.opExtrude","SWEPT_FACE",FACE,{"disambiguationData":[OSD([sQuery(id+"F6.wireOp",EDGE,"E413")])]})]});
            var Q62;
            Q62=makeQuery(id+"F7.boolean.opBoolean","INTERSECT",EDGE,{"disambiguationData":[OD(1.0)],"derivedFrom":[makeQuery(id+"F1.opExtrude","SWEPT_FACE",FACE,{"disambiguationData":[OSD([sQuery(id+"F0.wireOp",EDGE,"E0")])]}),makeQuery(id+"F7.opExtrude","SWEPT_FACE",FACE,{"disambiguationData":[OSD([sQuery(id+"F6.wireOp",EDGE,"E412")])]})]});
            var Q63;
            Q63=makeQuery(id+"F7.boolean.opBoolean","INTERSECT",EDGE,{"disambiguationData":[OD(1.0)],"derivedFrom":[makeQuery(id+"F1.opExtrude","SWEPT_FACE",FACE,{"disambiguationData":[OSD([sQuery(id+"F0.wireOp",EDGE,"E0")])]}),makeQuery(id+"F7.opExtrude","SWEPT_FACE",FACE,{"disambiguationData":[OSD([sQuery(id+"F6.wireOp",EDGE,"E411")])]})]});
            var Q64;
            Q64=makeQuery(id+"F7.boolean.opBoolean","INTERSECT",EDGE,{"disambiguationData":[OD(1.0)],"derivedFrom":[makeQuery(id+"F1.opExtrude","SWEPT_FACE",FACE,{"disambiguationData":[OSD([sQuery(id+"F0.wireOp",EDGE,"E0")])]}),makeQuery(id+"F7.opExtrude","SWEPT_FACE",FACE,{"disambiguationData":[OSD([sQuery(id+"F6.wireOp",EDGE,"E410")])]})]});
            var Q65;
            Q65=makeQuery(id+"F7.boolean.opBoolean","INTERSECT",EDGE,{"disambiguationData":[OD(1.0)],"derivedFrom":[makeQuery(id+"F1.opExtrude","SWEPT_FACE",FACE,{"disambiguationData":[OSD([sQuery(id+"F0.wireOp",EDGE,"E0")])]}),makeQuery(id+"F7.opExtrude","SWEPT_FACE",FACE,{"disambiguationData":[OSD([sQuery(id+"F6.wireOp",EDGE,"E392")])]})]});
            var Q66;
            Q66=makeQuery(id+"F7.boolean.opBoolean","INTERSECT",EDGE,{"disambiguationData":[OD(1.0)],"derivedFrom":[makeQuery(id+"F1.opExtrude","SWEPT_FACE",FACE,{"disambiguationData":[OSD([sQuery(id+"F0.wireOp",EDGE,"E0")])]}),makeQuery(id+"F7.opExtrude","SWEPT_FACE",FACE,{"disambiguationData":[OSD([sQuery(id+"F6.wireOp",EDGE,"E433")])]})]});
            var Q67;
            Q67=makeQuery(id+"F7.boolean.opBoolean","INTERSECT",EDGE,{"disambiguationData":[OD(1.0)],"derivedFrom":[makeQuery(id+"F1.opExtrude","SWEPT_FACE",FACE,{"disambiguationData":[OSD([sQuery(id+"F0.wireOp",EDGE,"E0")])]}),makeQuery(id+"F7.opExtrude","SWEPT_FACE",FACE,{"disambiguationData":[OSD([sQuery(id+"F6.wireOp",EDGE,"E428")])]})]});
            var Q68;
            Q68=makeQuery(id+"F7.boolean.opBoolean","INTERSECT",EDGE,{"disambiguationData":[OD(1.0)],"derivedFrom":[makeQuery(id+"F1.opExtrude","SWEPT_FACE",FACE,{"disambiguationData":[OSD([sQuery(id+"F0.wireOp",EDGE,"E0")])]}),makeQuery(id+"F7.opExtrude","SWEPT_FACE",FACE,{"disambiguationData":[OSD([sQuery(id+"F6.wireOp",EDGE,"E429")])]})]});
            var Q69;
            Q69=makeQuery(id+"F7.boolean.opBoolean","INTERSECT",EDGE,{"disambiguationData":[OD(1.0)],"derivedFrom":[makeQuery(id+"F1.opExtrude","SWEPT_FACE",FACE,{"disambiguationData":[OSD([sQuery(id+"F0.wireOp",EDGE,"E0")])]}),makeQuery(id+"F7.opExtrude","SWEPT_FACE",FACE,{"disambiguationData":[OSD([sQuery(id+"F6.wireOp",EDGE,"E430")])]})]});
            var Q70;
            Q70=makeQuery(id+"F7.boolean.opBoolean","INTERSECT",EDGE,{"disambiguationData":[OD(1.0)],"derivedFrom":[makeQuery(id+"F1.opExtrude","SWEPT_FACE",FACE,{"disambiguationData":[OSD([sQuery(id+"F0.wireOp",EDGE,"E0")])]}),makeQuery(id+"F7.opExtrude","SWEPT_FACE",FACE,{"disambiguationData":[OSD([sQuery(id+"F6.wireOp",EDGE,"E431")])]})]});
            var Q71;
            Q71=makeQuery(id+"F7.boolean.opBoolean","INTERSECT",EDGE,{"disambiguationData":[OD(1.0)],"derivedFrom":[makeQuery(id+"F1.opExtrude","SWEPT_FACE",FACE,{"disambiguationData":[OSD([sQuery(id+"F0.wireOp",EDGE,"E0")])]}),makeQuery(id+"F7.opExtrude","SWEPT_FACE",FACE,{"disambiguationData":[OSD([sQuery(id+"F6.wireOp",EDGE,"E432")])]})]});
            var Q72;
            Q72=makeQuery(id+"F7.boolean.opBoolean","INTERSECT",EDGE,{"disambiguationData":[OD(1.0)],"derivedFrom":[makeQuery(id+"F1.opExtrude","SWEPT_FACE",FACE,{"disambiguationData":[OSD([sQuery(id+"F0.wireOp",EDGE,"E0")])]}),makeQuery(id+"F7.opExtrude","SWEPT_FACE",FACE,{"disambiguationData":[OSD([sQuery(id+"F6.wireOp",EDGE,"E449")])]})]});
            var Q73;
            Q73=makeQuery(id+"F7.boolean.opBoolean","INTERSECT",EDGE,{"disambiguationData":[OD(1.0)],"derivedFrom":[makeQuery(id+"F1.opExtrude","SWEPT_FACE",FACE,{"disambiguationData":[OSD([sQuery(id+"F0.wireOp",EDGE,"E0")])]}),makeQuery(id+"F7.opExtrude","SWEPT_FACE",FACE,{"disambiguationData":[OSD([sQuery(id+"F6.wireOp",EDGE,"E450")])]})]});
            var Q74;
            Q74=makeQuery(id+"F7.boolean.opBoolean","INTERSECT",EDGE,{"disambiguationData":[OD(1.0)],"derivedFrom":[makeQuery(id+"F1.opExtrude","SWEPT_FACE",FACE,{"disambiguationData":[OSD([sQuery(id+"F0.wireOp",EDGE,"E0")])]}),makeQuery(id+"F7.opExtrude","SWEPT_FACE",FACE,{"disambiguationData":[OSD([sQuery(id+"F6.wireOp",EDGE,"E451")])]})]});
            var Q75;
            Q75=makeQuery(id+"F7.boolean.opBoolean","INTERSECT",EDGE,{"disambiguationData":[OD(1.0)],"derivedFrom":[makeQuery(id+"F1.opExtrude","SWEPT_FACE",FACE,{"disambiguationData":[OSD([sQuery(id+"F0.wireOp",EDGE,"E0")])]}),makeQuery(id+"F7.opExtrude","SWEPT_FACE",FACE,{"disambiguationData":[OSD([sQuery(id+"F6.wireOp",EDGE,"E446")])]})]});
            var Q76;
            Q76=makeQuery(id+"F7.boolean.opBoolean","INTERSECT",EDGE,{"disambiguationData":[OD(1.0)],"derivedFrom":[makeQuery(id+"F1.opExtrude","SWEPT_FACE",FACE,{"disambiguationData":[OSD([sQuery(id+"F0.wireOp",EDGE,"E0")])]}),makeQuery(id+"F7.opExtrude","SWEPT_FACE",FACE,{"disambiguationData":[OSD([sQuery(id+"F6.wireOp",EDGE,"E447")])]})]});
            var Q77;
            Q77=makeQuery(id+"F7.boolean.opBoolean","INTERSECT",EDGE,{"disambiguationData":[OD(1.0)],"derivedFrom":[makeQuery(id+"F1.opExtrude","SWEPT_FACE",FACE,{"disambiguationData":[OSD([sQuery(id+"F0.wireOp",EDGE,"E0")])]}),makeQuery(id+"F7.opExtrude","SWEPT_FACE",FACE,{"disambiguationData":[OSD([sQuery(id+"F6.wireOp",EDGE,"E448")])]})]});
            var Q78;
            Q78=makeQuery(id+"F7.boolean.opBoolean","INTERSECT",EDGE,{"disambiguationData":[OD(1.0)],"derivedFrom":[makeQuery(id+"F1.opExtrude","SWEPT_FACE",FACE,{"disambiguationData":[OSD([sQuery(id+"F0.wireOp",EDGE,"E0")])]}),makeQuery(id+"F7.opExtrude","SWEPT_FACE",FACE,{"disambiguationData":[OSD([sQuery(id+"F6.wireOp",EDGE,"E466")])]})]});
            var Q79;
            Q79=makeQuery(id+"F7.boolean.opBoolean","INTERSECT",EDGE,{"disambiguationData":[OD(1.0)],"derivedFrom":[makeQuery(id+"F1.opExtrude","SWEPT_FACE",FACE,{"disambiguationData":[OSD([sQuery(id+"F0.wireOp",EDGE,"E0")])]}),makeQuery(id+"F7.opExtrude","SWEPT_FACE",FACE,{"disambiguationData":[OSD([sQuery(id+"F6.wireOp",EDGE,"E467")])]})]});
            var Q80;
            Q80=makeQuery(id+"F7.boolean.opBoolean","INTERSECT",EDGE,{"disambiguationData":[OD(1.0)],"derivedFrom":[makeQuery(id+"F1.opExtrude","SWEPT_FACE",FACE,{"disambiguationData":[OSD([sQuery(id+"F0.wireOp",EDGE,"E0")])]}),makeQuery(id+"F7.opExtrude","SWEPT_FACE",FACE,{"disambiguationData":[OSD([sQuery(id+"F6.wireOp",EDGE,"E468")])]})]});
            var Q81;
            Q81=makeQuery(id+"F7.boolean.opBoolean","INTERSECT",EDGE,{"disambiguationData":[OD(1.0)],"derivedFrom":[makeQuery(id+"F1.opExtrude","SWEPT_FACE",FACE,{"disambiguationData":[OSD([sQuery(id+"F0.wireOp",EDGE,"E0")])]}),makeQuery(id+"F7.opExtrude","SWEPT_FACE",FACE,{"disambiguationData":[OSD([sQuery(id+"F6.wireOp",EDGE,"E469")])]})]});
            var Q82;
            Q82=makeQuery(id+"F7.boolean.opBoolean","INTERSECT",EDGE,{"disambiguationData":[OD(1.0)],"derivedFrom":[makeQuery(id+"F1.opExtrude","SWEPT_FACE",FACE,{"disambiguationData":[OSD([sQuery(id+"F0.wireOp",EDGE,"E0")])]}),makeQuery(id+"F7.opExtrude","SWEPT_FACE",FACE,{"disambiguationData":[OSD([sQuery(id+"F6.wireOp",EDGE,"E464")])]})]});
            var Q83;
            Q83=makeQuery(id+"F7.boolean.opBoolean","INTERSECT",EDGE,{"disambiguationData":[OD(1.0)],"derivedFrom":[makeQuery(id+"F1.opExtrude","SWEPT_FACE",FACE,{"disambiguationData":[OSD([sQuery(id+"F0.wireOp",EDGE,"E0")])]}),makeQuery(id+"F7.opExtrude","SWEPT_FACE",FACE,{"disambiguationData":[OSD([sQuery(id+"F6.wireOp",EDGE,"E465")])]})]});
            var Q84;
            Q84=makeQuery(id+"F7.boolean.opBoolean","INTERSECT",EDGE,{"disambiguationData":[OD(1.0)],"derivedFrom":[makeQuery(id+"F1.opExtrude","SWEPT_FACE",FACE,{"disambiguationData":[OSD([sQuery(id+"F0.wireOp",EDGE,"E0")])]}),makeQuery(id+"F7.opExtrude","SWEPT_FACE",FACE,{"disambiguationData":[OSD([sQuery(id+"F6.wireOp",EDGE,"E487")])]})]});
            var Q85;
            Q85=makeQuery(id+"F7.boolean.opBoolean","INTERSECT",EDGE,{"disambiguationData":[OD(1.0)],"derivedFrom":[makeQuery(id+"F1.opExtrude","SWEPT_FACE",FACE,{"disambiguationData":[OSD([sQuery(id+"F0.wireOp",EDGE,"E0")])]}),makeQuery(id+"F7.opExtrude","SWEPT_FACE",FACE,{"disambiguationData":[OSD([sQuery(id+"F6.wireOp",EDGE,"E482")])]})]});
            var Q86;
            Q86=makeQuery(id+"F7.boolean.opBoolean","INTERSECT",EDGE,{"disambiguationData":[OD(1.0)],"derivedFrom":[makeQuery(id+"F1.opExtrude","SWEPT_FACE",FACE,{"disambiguationData":[OSD([sQuery(id+"F0.wireOp",EDGE,"E0")])]}),makeQuery(id+"F7.opExtrude","SWEPT_FACE",FACE,{"disambiguationData":[OSD([sQuery(id+"F6.wireOp",EDGE,"E483")])]})]});
            var Q87;
            Q87=makeQuery(id+"F7.boolean.opBoolean","INTERSECT",EDGE,{"disambiguationData":[OD(1.0)],"derivedFrom":[makeQuery(id+"F1.opExtrude","SWEPT_FACE",FACE,{"disambiguationData":[OSD([sQuery(id+"F0.wireOp",EDGE,"E0")])]}),makeQuery(id+"F7.opExtrude","SWEPT_FACE",FACE,{"disambiguationData":[OSD([sQuery(id+"F6.wireOp",EDGE,"E484")])]})]});
            var Q88;
            Q88=makeQuery(id+"F7.boolean.opBoolean","INTERSECT",EDGE,{"disambiguationData":[OD(1.0)],"derivedFrom":[makeQuery(id+"F1.opExtrude","SWEPT_FACE",FACE,{"disambiguationData":[OSD([sQuery(id+"F0.wireOp",EDGE,"E0")])]}),makeQuery(id+"F7.opExtrude","SWEPT_FACE",FACE,{"disambiguationData":[OSD([sQuery(id+"F6.wireOp",EDGE,"E485")])]})]});
            var Q89;
            Q89=makeQuery(id+"F7.boolean.opBoolean","INTERSECT",EDGE,{"disambiguationData":[OD(1.0)],"derivedFrom":[makeQuery(id+"F1.opExtrude","SWEPT_FACE",FACE,{"disambiguationData":[OSD([sQuery(id+"F0.wireOp",EDGE,"E0")])]}),makeQuery(id+"F7.opExtrude","SWEPT_FACE",FACE,{"disambiguationData":[OSD([sQuery(id+"F6.wireOp",EDGE,"E486")])]})]});
            var Q90;
            Q90=makeQuery(id+"F7.boolean.opBoolean","INTERSECT",EDGE,{"disambiguationData":[OD(1.0)],"derivedFrom":[makeQuery(id+"F1.opExtrude","SWEPT_FACE",FACE,{"disambiguationData":[OSD([sQuery(id+"F0.wireOp",EDGE,"E0")])]}),makeQuery(id+"F7.opExtrude","SWEPT_FACE",FACE,{"disambiguationData":[OSD([sQuery(id+"F6.wireOp",EDGE,"E503")])]})]});
            var Q91;
            Q91=makeQuery(id+"F7.boolean.opBoolean","INTERSECT",EDGE,{"disambiguationData":[OD(1.0)],"derivedFrom":[makeQuery(id+"F1.opExtrude","SWEPT_FACE",FACE,{"disambiguationData":[OSD([sQuery(id+"F0.wireOp",EDGE,"E0")])]}),makeQuery(id+"F7.opExtrude","SWEPT_FACE",FACE,{"disambiguationData":[OSD([sQuery(id+"F6.wireOp",EDGE,"E504")])]})]});
            var Q92;
            Q92=makeQuery(id+"F7.boolean.opBoolean","INTERSECT",EDGE,{"disambiguationData":[OD(1.0)],"derivedFrom":[makeQuery(id+"F1.opExtrude","SWEPT_FACE",FACE,{"disambiguationData":[OSD([sQuery(id+"F0.wireOp",EDGE,"E0")])]}),makeQuery(id+"F7.opExtrude","SWEPT_FACE",FACE,{"disambiguationData":[OSD([sQuery(id+"F6.wireOp",EDGE,"E505")])]})]});
            var Q93;
            Q93=makeQuery(id+"F7.boolean.opBoolean","INTERSECT",EDGE,{"disambiguationData":[OD(1.0)],"derivedFrom":[makeQuery(id+"F1.opExtrude","SWEPT_FACE",FACE,{"disambiguationData":[OSD([sQuery(id+"F0.wireOp",EDGE,"E0")])]}),makeQuery(id+"F7.opExtrude","SWEPT_FACE",FACE,{"disambiguationData":[OSD([sQuery(id+"F6.wireOp",EDGE,"E500")])]})]});
            var Q94;
            Q94=makeQuery(id+"F7.boolean.opBoolean","INTERSECT",EDGE,{"disambiguationData":[OD(1.0)],"derivedFrom":[makeQuery(id+"F1.opExtrude","SWEPT_FACE",FACE,{"disambiguationData":[OSD([sQuery(id+"F0.wireOp",EDGE,"E0")])]}),makeQuery(id+"F7.opExtrude","SWEPT_FACE",FACE,{"disambiguationData":[OSD([sQuery(id+"F6.wireOp",EDGE,"E501")])]})]});
            var Q95;
            Q95=makeQuery(id+"F7.boolean.opBoolean","INTERSECT",EDGE,{"disambiguationData":[OD(1.0)],"derivedFrom":[makeQuery(id+"F1.opExtrude","SWEPT_FACE",FACE,{"disambiguationData":[OSD([sQuery(id+"F0.wireOp",EDGE,"E0")])]}),makeQuery(id+"F7.opExtrude","SWEPT_FACE",FACE,{"disambiguationData":[OSD([sQuery(id+"F6.wireOp",EDGE,"E502")])]})]});
            var Q96;
            Q96=makeQuery(id+"F7.boolean.opBoolean","INTERSECT",EDGE,{"disambiguationData":[OD(1.0)],"derivedFrom":[makeQuery(id+"F1.opExtrude","SWEPT_FACE",FACE,{"disambiguationData":[OSD([sQuery(id+"F0.wireOp",EDGE,"E0")])]}),makeQuery(id+"F7.opExtrude","SWEPT_FACE",FACE,{"disambiguationData":[OSD([sQuery(id+"F6.wireOp",EDGE,"E483")])]})]});
            fillet(context, id + "F16", {"entities" : qUnion([Q0, Q1, Q2, Q3, Q4, Q5, Q6, Q7, Q8, Q9, Q10, Q11, Q12, Q13, Q14, Q15, Q16, Q17, Q18, Q19, Q20, Q21, Q22, Q23, Q24, Q25, Q26, Q27, Q28, Q29, Q30, Q31, Q32, Q33, Q34, Q35, Q36, Q37, Q38, Q39, Q40, Q41, Q42, Q43, Q44, Q45, Q46, Q47, Q48, Q49, Q50, Q51, Q52, Q53, Q54, Q55, Q56, Q57, Q58, Q59, Q60, Q61, Q62, Q63, Q64, Q65, Q66, Q67, Q68, Q69, Q70, Q71, Q72, Q73, Q74, Q75, Q76, Q77, Q78, Q79, Q80, Q81, Q82, Q83, Q84, Q85, Q86, Q87, Q88, Q89, Q90, Q91, Q92, Q93, Q94, Q95, Q96]), "radius" : 0.4 * mm, "tangentPropagation" : true, "allowEdgeOverflow" : false});
        }
        {
            var Q0;
            Q0=makeQuery(id+"F1.opExtrude","SWEPT_BODY",BODY,{"disambiguationData":[OSD([sQuery(id+"F0.wireOp",EDGE,"E0")])]});
            transform(context, id + "F17", {"entities" : qUnion([Q0]), "transformType" : TransformType.TRANSLATION_3D, "dx" : 14.75 * mm, "dy" : 0 * mm, "dz" : 0 * mm, "makeCopy" : true});
        }
        {
            var Q0;
            Q0=makeQuery(id+"F17.opPattern","COPY",BODY,{"derivedFrom":makeQuery(id+"F1.opExtrude","SWEPT_BODY",BODY,{"disambiguationData":[OSD([sQuery(id+"F0.wireOp",EDGE,"E0")])]}),"instanceName":"1"});
            var Q1;
            Q1=makeQuery(id+"F17.opPattern","COPY",FACE,{"derivedFrom":makeQuery(id+"F1.opExtrude","SWEPT_FACE",FACE,{"disambiguationData":[OSD([sQuery(id+"F0.wireOp",EDGE,"E0")])]}),"instanceName":"1"});
            transform(context, id + "F18", {"entities" : qUnion([Q0]), "transformType" : TransformType.ROTATION, "transformAxis" : qUnion([Q1]), "angle" : 180 * degree, "makeCopy" : false});
        }
        {
            var Q0;
            Q0=makeQuery(id+"F1.opExtrude","SWEPT_BODY",BODY,{"disambiguationData":[OSD([sQuery(id+"F0.wireOp",EDGE,"E0")])]});
            var Q1;
            Q1=makeQuery(id+"F17.opPattern","COPY",BODY,{"derivedFrom":makeQuery(id+"F1.opExtrude","SWEPT_BODY",BODY,{"disambiguationData":[OSD([sQuery(id+"F0.wireOp",EDGE,"E0")])]}),"instanceName":"1"});
            booleanBodies(context, id + "F19", {"operationType" : BooleanOperationType.UNION, "tools" : qUnion([Q0, Q1])});
        }
        {
            var Q0;
            {var subQ0=makeQuery(id+"F1.opExtrude","CAP_FACE",FACE,{"disambiguationData":[OSD([sQuery(id+"F0.wireOp",EDGE,"E0")])],"isStart":false});Q0=makeQuery(id+"F19.opBoolean","MERGE",FACE,{"derivedFrom":[subQ0,makeQuery(id+"F17.opPattern","COPY",FACE,{"derivedFrom":subQ0,"instanceName":"1"})]});}
            var sketch = newSketch(context, id + "F20", { "sketchPlane" : qUnion([Q0])});
            skLineSegment(sketch, "E1020", {"start": v(0, 0) * mm, "end": v(-14.75, 0) * mm, "construction": true});
            skLineSegment(sketch, "E1021", {"start": v(-14.75, 0) * mm, "end": v(-14.75, 7.88) * mm, "construction": true});
            skLineSegment(sketch, "E1022", {"start": v(-14.75, 7.88) * mm, "end": v(0, 7.88) * mm});
            skLineSegment(sketch, "E1023", {"start": v(0, 7.88) * mm, "end": v(0, -7.88) * mm, "construction": true});
            skLineSegment(sketch, "E1024", {"start": v(-14.75, 0) * mm, "end": v(-14.75, -7.88) * mm, "construction": true});
            skLineSegment(sketch, "E1025", {"start": v(-14.75, -7.88) * mm, "end": v(0, -7.88) * mm});
            skArc(sketch, "E1026", {"start": v(-14.75, 7.88) * mm, "mid": v(-22.63, 0) * mm, "end": v(-14.75, -7.88) * mm});
            skArc(sketch, "E1027", {"start": v(0, -7.88) * mm, "mid": v(7.88, 0) * mm, "end": v(0, 7.88) * mm});
            skSolve(sketch);
        }
        {
            var Q0;
            Q0 = qSketchRegion(id + "F20", true);
            extrude(context, id + "F21", {"entities" : qUnion([Q0]), "operationType" : NewBodyOperationType.ADD, "depth" : 3 * mm});
        }
        {
            var Q0;
            Q0=makeQuery(id+"F21.opExtrude","CAP_EDGE",EDGE,{"disambiguationData":[OSD([sQuery(id+"F20.wireOp",EDGE,"E1025")])],"isStart":true});
            var Q1;
            Q1=makeQuery(id+"F21.opExtrude","CAP_EDGE",EDGE,{"disambiguationData":[OSD([sQuery(id+"F20.wireOp",EDGE,"E1022")])],"isStart":true});
            fillet(context, id + "F22", {"entities" : qUnion([Q0, Q1]), "radius" : .7 * mm, "tangentPropagation" : true, "allowEdgeOverflow" : false});
        }
    });
